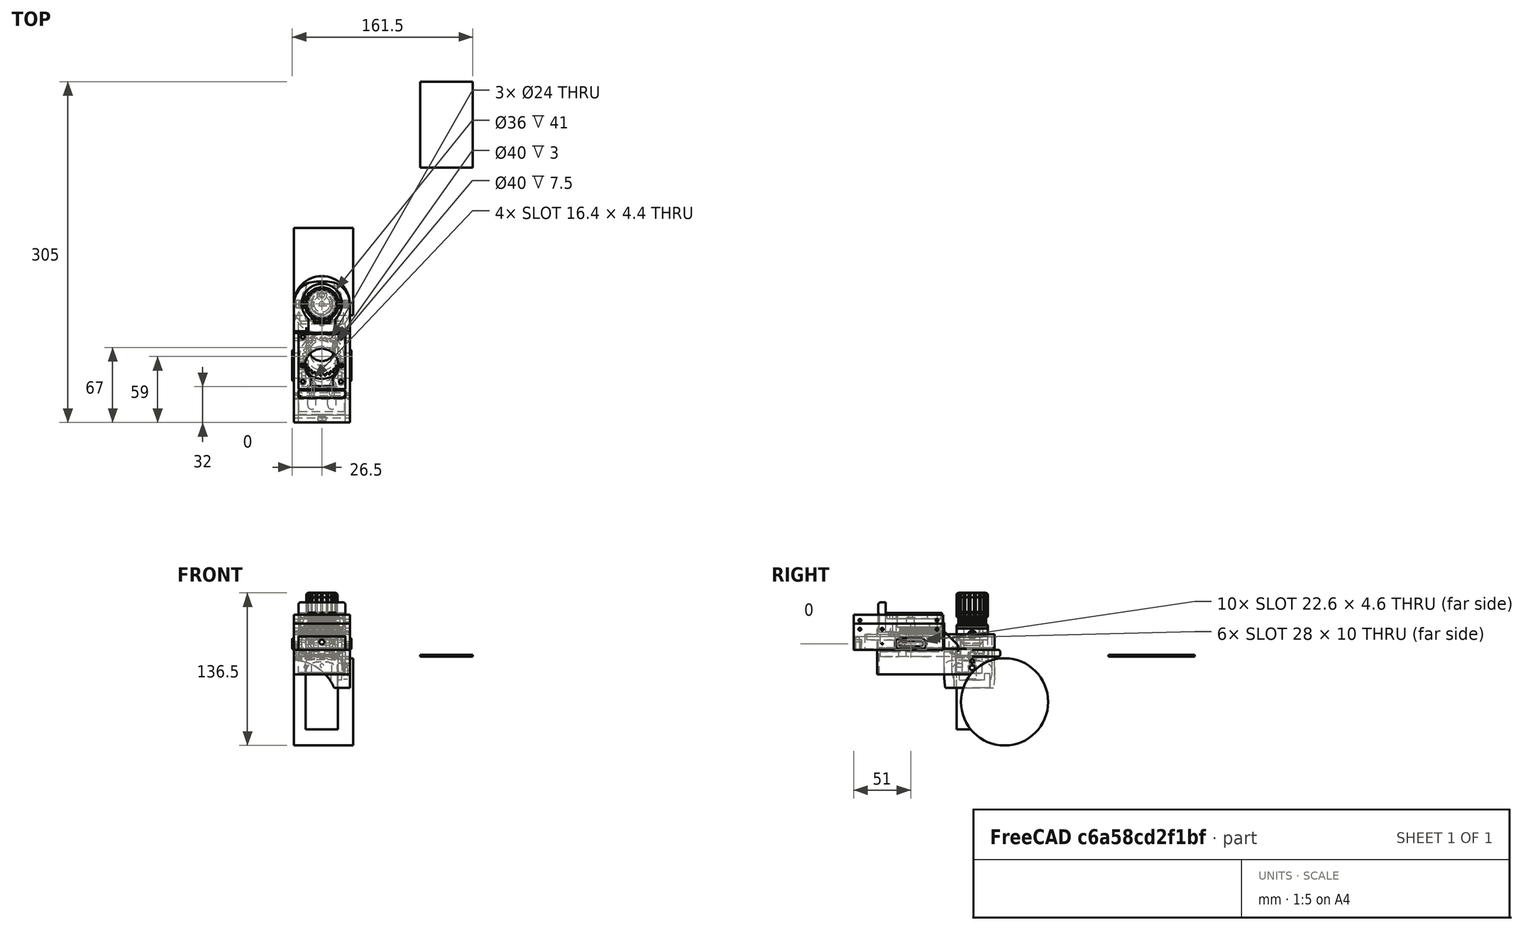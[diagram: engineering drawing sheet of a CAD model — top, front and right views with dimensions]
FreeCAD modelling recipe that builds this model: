
FCSTD DOCUMENT  (FreeCAD 0.18R4 (GitTag))
Label: new28BYJ-fokuser
License: All rights reserved
LicenseURL: http://en.wikipedia.org/wiki/All_rights_reserved
objects: Part::Feature×777, Part::Cylinder×371, Part::Box×218, Part::MultiFuse×160, Part::Cut×77, Part::Extrusion×34, Part::Fillet×30, App::Part×24, Sketcher::SketchObject×24, Part::FeaturePython×10, Part::Part2DObjectPython×10, Part::Chamfer×5, Part::Sphere×1
note: 1717 computed .brp shape members not serialized (recipe doc carries the construction recipe); baked Part::Feature solids carry a one-line shape summary decoded from their .brp

FEATURE [Part::Feature] Cut018020020009027020001  label="base nema"
  shape: bbox 50 x 86 x 24 mm, 75 faces (baked)
FEATURE [Part::Box] Box  label="Krychle"
  AttacherType = Attacher::AttachEngine3D
  Height = 24
  Length = 50
  Placement = pos=(-25,-66,-16) rot=(0,0,1;0rad)
  Width = 51
FEATURE [Part::Cut] Cut
  Base = -> Cut018020020009027020001
  Tool = -> Box
FEATURE [Part::Box] Box001  label="Krychle001"
  AttacherType = Attacher::AttachEngine3D
  Height = 24
  Length = 50
  Placement = pos=(-25,-85,-16) rot=(0,0,1;0rad)
  Width = 70
FEATURE [Part::Box] Box002  label="Kry"
  AttacherType = Attacher::AttachEngine3D
  Height = 24
  Length = 42
  Placement = pos=(-21,-83,-19.5) rot=(0,0,1;0rad)
  Width = 65
FEATURE [Part::MultiFuse] Fusion
  Shapes = -> [Box001,Cut]
FEATURE [Part::Cylinder] Cylinder  label="Válec"
  Angle = 360
  AttacherType = Attacher::AttachEngine3D
  Height = 27
  Placement = pos=(0,0,-17) rot=(0,0,1;0rad)
  Radius = 14.7
FEATURE [Part::Cylinder] Cylinder001  label="Válec001"
  Angle = 360
  AttacherType = Attacher::AttachEngine3D
  Height = 10
  Placement = pos=(0,-45,0) rot=(0,0,1;0rad)
  Radius = 10
FEATURE [Part::Cylinder] Cylinder002  label="Válec002"
  Angle = 360
  AttacherType = Attacher::AttachEngine3D
  Height = 10
  Placement = pos=(0,-37,0) rot=(0,0,1;0rad)
  Radius = 10
FEATURE [Part::Box] Box003  label="Krychle003"
  AttacherType = Attacher::AttachEngine3D
  Height = 10
  Length = 20
  Placement = pos=(-10,-45,0) rot=(0,0,1;0rad)
  Width = 8
FEATURE [Part::Cylinder] Cylinder003  label="Válec003"
  Angle = 360
  AttacherType = Attacher::AttachEngine3D
  Height = 10
  Placement = pos=(9,-68,0) rot=(0,0,1;0rad)
  Radius = 2.2
FEATURE [Part::Cylinder] Cylinder004  label="Válec004"
  Angle = 360
  AttacherType = Attacher::AttachEngine3D
  Height = 10
  Placement = pos=(-9,-68,0) rot=(0,0,1;0rad)
  Radius = 2.2
FEATURE [Part::Cylinder] Cylinder005  label="Válec005"
  Angle = 360
  AttacherType = Attacher::AttachEngine3D
  Height = 10
  Placement = pos=(9,-80,0) rot=(0,0,1;0rad)
  Radius = 2.2
FEATURE [Part::Cylinder] Cylinder006  label="Válec006"
  Angle = 360
  AttacherType = Attacher::AttachEngine3D
  Height = 10
  Placement = pos=(-9,-80,0) rot=(0,0,1;0rad)
  Radius = 2.2
FEATURE [Part::Box] Box004  label="Krychle004"
  AttacherType = Attacher::AttachEngine3D
  Height = 10
  Length = 4.4
  Placement = pos=(-11.2,-80,0) rot=(0,0,1;0rad)
  Width = 12
FEATURE [Part::Box] Box005  label="Krychle005"
  AttacherType = Attacher::AttachEngine3D
  Height = 10
  Length = 4.4
  Placement = pos=(6.8,-80,0) rot=(0,0,1;0rad)
  Width = 12
FEATURE [Part::MultiFuse] Fusion001
  Shapes = -> [Cylinder,Cylinder001,Cylinder002,Box003,Cylinder003,Cylinder004,Cylinder005,Cylinder006,Box004,Box005,Box002]
FEATURE [Part::Cut] Cut018020020009027020002  label="N_EAF"
  Base = -> Fusion
  Tool = -> Fusion001
FEATURE [Part::Box] Box021049  label="Krychle076"
  AttacherType = Attacher::AttachEngine3D
  Height = 24
  Length = 50
  Placement = pos=(-25,-66,-16) rot=(0,0,1;0rad)
  Width = 51
FEATURE [Part::Feature] Cut018020020009019001  label="Nema refractor"
  shape: bbox 50 x 89 x 24 mm, 96 faces (baked)
FEATURE [Part::Cut] Cut018020020009027020002002
  Base = -> Cut018020020009019001
  Tool = -> Box021049
FEATURE [Part::Feature] Cylinder112019  label="Válec127"
  Placement = pos=(0,0,0) rot=(0,0,1;4.18879rad)
  shape: bbox 7.858 x 10.31 x 3.3 mm, 3 faces (baked)
FEATURE [Part::Feature] difference001004  label="Pulley GT2  - 043"
  shape: bbox 27.96 x 27.96 x 19.5 mm, 1014 faces (baked)
FEATURE [Part::Feature] Cylinder112018  label="Válec126"
  Placement = pos=(0,0,0) rot=(0,0,1;2.0944rad)
  shape: bbox 7.858 x 10.31 x 3.3 mm, 3 faces (baked)
FEATURE [Part::Cylinder] Cylinder112004  label="Válec112"
  Angle = 360
  AttacherType = Attacher::AttachEngine3D
  Height = 40
  Placement = pos=(-20,0,19.5) rot=(0,1,0;1.5708rad)
  Radius = 2.15
FEATURE [Part::Cylinder] Cylinder112013  label="Válec121"
  Angle = 360
  AttacherType = Attacher::AttachEngine3D
  Height = 17
  Placement = pos=(0,0,8) rot=(0,0,1;0rad)
  Radius = 9
FEATURE [Part::Chamfer] Chamfer006
  Base = -> Cylinder112013
  Edges = 1 edges r=4: [Edge3]
FEATURE [Part::Cylinder] Cylinder112014  label="Válec122"
  Angle = 360
  AttacherType = Attacher::AttachEngine3D
  Height = 25
  Radius = 5.5
FEATURE [Part::Cylinder] Cylinder112008  label="Válec116"
  Angle = 360
  AttacherType = Attacher::AttachEngine3D
  Height = 40
  Placement = pos=(0,0,-5) rot=(0,0,1;0rad)
  Radius = 2.15
FEATURE [Part::Cylinder] Cylinder112015  label="Válec123"
  Angle = 360
  AttacherType = Attacher::AttachEngine3D
  Height = 10
  Placement = pos=(0,0,15) rot=(0,0,1;0rad)
  Radius = 14
FEATURE [Part::Cylinder] Cylinder112011  label="Válec119"
  Angle = 360
  AttacherType = Attacher::AttachEngine3D
  Height = 18
  Placement = pos=(0,0,36) rot=(0,0,1;0rad)
  Radius = 14
FEATURE [Part::Cylinder] Cylinder112010  label="Válec118"
  Angle = 360
  AttacherType = Attacher::AttachEngine3D
  Height = 27
  Radius = 7.2
FEATURE [Part::Cylinder] Cylinder112016  label="Válec124"
  Angle = 360
  AttacherType = Attacher::AttachEngine3D
  Height = 40
  Placement = pos=(0,0,-5) rot=(0,0,1;0rad)
  Radius = 2.15
FEATURE [Part::Cylinder] Cylinder112017  label="Válec125"
  Angle = 360
  AttacherType = Attacher::AttachEngine3D
  Height = 8.5
  Radius = 9
FEATURE [Part::Cut] Cut018020020009016
  Base = -> difference001004
  Placement = pos=(0,0,16.5) rot=(0,0,1;0rad)
  Tool = -> Cylinder112017
FEATURE [Part::MultiFuse] Fusion005033
  Shapes = -> [Cut018020020009016,Cylinder112014,Chamfer006,Cylinder112011,Cylinder112015]
FEATURE [Part::Fillet] Fillet011
  Base = -> Fusion005033
  Edges = 2 edges: [Edge8 r=1,Edge2738 r=3]
FEATURE [Part::Cylinder] Cylinder112012  label="Válec120"
  Angle = 360
  AttacherType = Attacher::AttachEngine3D
  Height = 10
  Placement = pos=(0,0,4.5) rot=(0,1,0;1.5708rad)
  Radius = 1.65
FEATURE [Part::MultiFuse] Fusion005032
  Shapes = -> [Cylinder112016,Cylinder112012,Cylinder112018,Cylinder112019]
FEATURE [Part::Cut] Cut018020020009017  label="pully40 v003"
  Base = -> Fillet011
  Tool = -> Fusion005032
FEATURE [Part::Cylinder] Cylinder112020  label="Válec128"
  Angle = 360
  AttacherType = Attacher::AttachEngine3D
  Height = 10
  Placement = pos=(-19,0,19.5) rot=(0,1,0;1.5708rad)
  Radius = 3.7
FEATURE [Part::Cylinder] Cylinder112021  label="Válec129"
  Angle = 360
  AttacherType = Attacher::AttachEngine3D
  Height = 10
  Placement = pos=(9,0,19.5) rot=(0,1,0;1.5708rad)
  Radius = 3.7
FEATURE [Part::MultiFuse] Fusion005034
  Shapes = -> [Cylinder112020,Cylinder112021,Cylinder112008,Cylinder112004,Cylinder112010]
FEATURE [Part::Cut] Cut018020020009018  label="Pulley40 V3"
  Base = -> Cut018020020009017
  Tool = -> Fusion005034
FEATURE [Part::Feature] Cut018020020009027020002003003  label="N_EAF002"
  shape: bbox 50 x 105 x 24 mm, 61 faces (baked)
FEATURE [Part::Fillet] Fillet  label="N_EAF_a"
  Base = -> Cut018020020009027020002003003
  Edges = 8 edges r=1.5: [Edge82,Edge83,Edge87,Edge88,Edge97,Edge100,Edge103,Edge126]
FEATURE [Part::Box] Box021055  label="Krychle082"
  AttacherType = Attacher::AttachEngine3D
  Height = 24
  Length = 50
  Placement = pos=(-25,-85,-16) rot=(0,0,1;0rad)
  Width = 70
FEATURE [Part::MultiFuse] Fusion005036
  Shapes = -> [Cut018020020009027020002002,Box021055]
FEATURE [Part::Cylinder] Cylinder112024003  label="Válec135"
  Angle = 360
  AttacherType = Attacher::AttachEngine3D
  Height = 10
  Placement = pos=(9,-80,0) rot=(0,0,1;0rad)
  Radius = 2.2
FEATURE [Part::Cylinder] Cylinder112024004  label="Válec136"
  Angle = 360
  AttacherType = Attacher::AttachEngine3D
  Height = 10
  Placement = pos=(0,-45,0) rot=(0,0,1;0rad)
  Radius = 10
FEATURE [Part::Cylinder] Cylinder112024005  label="Válec137"
  Angle = 360
  AttacherType = Attacher::AttachEngine3D
  Height = 10
  Placement = pos=(-9,-80,0) rot=(0,0,1;0rad)
  Radius = 2.2
FEATURE [Part::Box] Box021056  label="Krychle083"
  AttacherType = Attacher::AttachEngine3D
  Height = 10
  Length = 4.4
  Placement = pos=(-11.2,-80,0) rot=(0,0,1;0rad)
  Width = 12
FEATURE [Part::Box] Box021057  label="Krychle084"
  AttacherType = Attacher::AttachEngine3D
  Height = 10
  Length = 4.4
  Placement = pos=(6.8,-80,0) rot=(0,0,1;0rad)
  Width = 12
FEATURE [Part::Cylinder] Cylinder112024006  label="Válec138"
  Angle = 360
  AttacherType = Attacher::AttachEngine3D
  Height = 10
  Placement = pos=(-9,-68,0) rot=(0,0,1;0rad)
  Radius = 2.2
FEATURE [Part::Cylinder] Cylinder112024007  label="Válec139"
  Angle = 360
  AttacherType = Attacher::AttachEngine3D
  Height = 10
  Placement = pos=(9,-68,0) rot=(0,0,1;0rad)
  Radius = 2.2
FEATURE [Part::Box] Box021058  label="Kry001"
  AttacherType = Attacher::AttachEngine3D
  Height = 24
  Length = 42
  Placement = pos=(-21,-83,-19.5) rot=(0,0,1;0rad)
  Width = 65
FEATURE [Part::Cylinder] Cylinder112024008  label="Válec140"
  Angle = 360
  AttacherType = Attacher::AttachEngine3D
  Height = 10
  Placement = pos=(0,-37,0) rot=(0,0,1;0rad)
  Radius = 10
FEATURE [Part::Box] Box021059  label="Krychle085"
  AttacherType = Attacher::AttachEngine3D
  Height = 10
  Length = 20
  Placement = pos=(-10,-45,0) rot=(0,0,1;0rad)
  Width = 8
FEATURE [Part::Cylinder] Cylinder112024009  label="Válec141"
  Angle = 360
  AttacherType = Attacher::AttachEngine3D
  Height = 27
  Placement = pos=(0,0,-17) rot=(0,0,1;0rad)
  Radius = 14.7
FEATURE [Part::MultiFuse] Fusion005037
  Shapes = -> [Cylinder112024009,Cylinder112024004,Cylinder112024008,Box021059,Cylinder112024007,Cylinder112024006,Cylinder112024003,Cylinder112024005,Box021056,Box021057,Box021058]
FEATURE [Part::Cut] Cut018020020009027020002003004  label="R_EAF"
  Base = -> Fusion005036
  Tool = -> Fusion005037
FEATURE [Part::Feature] Cut018020020009027020002003004001  label="R_EAF001"
  shape: bbox 50 x 108 x 24 mm, 82 faces (baked)
FEATURE [Part::Fillet] Fillet012  label="R_EAF_a"
  Base = -> Cut018020020009027020002003004001
  Edges = 8 edges r=1.5: [Edge106,Edge136,Edge138,Edge196,Edge197,Edge198,Edge243,Edge244]
FEATURE [App::Part] Part001  label="Refractor"
  Group = -> [Cut018020020009019001,Box021049,Cut018020020009027020002002,Cylinder112024006,Box021057,Box021058,Cylinder112024007,Cylinder112024008,Cylinder112024009,Box021059,Box021056,Box021055,Cylinder112024005,Cylinder112024003,Cylinder112024004,Fusion005036,Fusion005037,Cut018020020009027020002003004,Cut018020020009027020002003004001,Fillet012]
  License = CC BY 3.0
  LicenseURL = http://creativecommons.org/licenses/by/3.0/
  Origin = -> Origin001
FEATURE [Part::Cylinder] Cylinder112024015  label="cy4"
  Angle = 360
  AttacherType = Attacher::AttachEngine3D
  Height = 24
  Placement = pos=(-9,-68,0) rot=(0,0,1;0rad)
  Radius = 2.2
FEATURE [Part::Box] Box021060  label="cub3"
  AttacherType = Attacher::AttachEngine3D
  Height = 24
  Length = 4.4
  Placement = pos=(6.8,-80,0) rot=(0,0,1;0rad)
  Width = 12
FEATURE [Part::Box] Box021061  label="cub5"
  AttacherType = Attacher::AttachEngine3D
  Height = 15
  Length = 42
  Placement = pos=(-21,-83,22) rot=(0,0,1;0rad)
  Width = 65
FEATURE [Part::Cylinder] Cylinder112024016  label="cy3"
  Angle = 360
  AttacherType = Attacher::AttachEngine3D
  Height = 24
  Placement = pos=(9,-68,0) rot=(0,0,1;0rad)
  Radius = 2.2
FEATURE [Part::Cylinder] Cylinder112024017  label="cy2"
  Angle = 360
  AttacherType = Attacher::AttachEngine3D
  Height = 24
  Placement = pos=(0,-39,0) rot=(0,0,1;0rad)
  Radius = 14
FEATURE [Part::Box] Box021062  label="cub1"
  AttacherType = Attacher::AttachEngine3D
  Height = 6
  Length = 28
  Placement = pos=(-14,-45,0) rot=(0,0,1;0rad)
  Width = 6
FEATURE [Part::Box] Box021063  label="cub2"
  AttacherType = Attacher::AttachEngine3D
  Height = 24
  Length = 4.4
  Placement = pos=(-11.2,-80,0) rot=(0,0,1;0rad)
  Width = 12
FEATURE [Part::Cylinder] Cylinder112024019  label="cy6"
  Angle = 360
  AttacherType = Attacher::AttachEngine3D
  Height = 24
  Placement = pos=(-9,-80,0) rot=(0,0,1;0rad)
  Radius = 2.2
FEATURE [Part::Cylinder] Cylinder112024020  label="cy5"
  Angle = 360
  AttacherType = Attacher::AttachEngine3D
  Height = 24
  Placement = pos=(9,-80,0) rot=(0,0,1;0rad)
  Radius = 2.2
FEATURE [Part::Cylinder] Cylinder112024021  label="cy1"
  Angle = 360
  AttacherType = Attacher::AttachEngine3D
  Height = 24
  Placement = pos=(0,-45,0) rot=(0,0,1;0rad)
  Radius = 14
FEATURE [Part::FeaturePython] Screw  label="M4x30-Screw"  # Fasteners workbench fastener (typed FeaturePython)
  Placement = pos=(0,0,7.5) rot=(0,0,1;0rad)
  diameter = 6
  invert = false
  length = 1
  matchOuter = false
  offset = 0
  thread = false
  type = 13
FEATURE [Part::Cylinder] Cylinder112024022  label="Válec154"
  Angle = 360
  AttacherType = Attacher::AttachEngine3D
  Height = 10
  Radius = 9
FEATURE [Part::Cut] Cut018020020009027020002003004003
  Base = -> Cylinder112024022
  Tool = -> Screw
FEATURE [Part::Fillet] Fillet013  label="knob"
  Base = -> Cut018020020009027020002003004003
  Edges = 2 edges r=2: [Edge1,Edge3]
  Placement = pos=(0,0,2) rot=(0,0,1;0rad)
FEATURE [Part::Cylinder] Cylinder112024026  label="Cy9"
  Angle = 360
  AttacherType = Attacher::AttachEngine3D
  Height = 6
  Radius = 25
FEATURE [Part::Cylinder] Cylinder112024027  label="cy7"
  Angle = 360
  AttacherType = Attacher::AttachEngine3D
  Height = 10
  Radius = 10
FEATURE [Part::Box] Box021064  label="Cub6"
  AttacherType = Attacher::AttachEngine3D
  Height = 30
  Length = 50
  Placement = pos=(-25,-85,0) rot=(0,0,1;0rad)
  Width = 60
FEATURE [Part::Box] Box021065  label="Cub7"
  AttacherType = Attacher::AttachEngine3D
  Height = 6
  Length = 50
  Placement = pos=(-25,-85,0) rot=(0,0,1;0rad)
  Width = 85
FEATURE [Part::Box] Box021067  label="cub4"
  AttacherType = Attacher::AttachEngine3D
  Height = 18
  Length = 28
  Placement = pos=(-14,-45,6) rot=(0,0,1;0rad)
  Width = 25
FEATURE [Part::Cylinder] Cylinder112024025003  label="hole3s"
  Angle = 360
  AttacherType = Attacher::AttachEngine3D
  Height = 10
  Placement = pos=(0,16.5,0) rot=(0,0,1;0rad)
  Radius = 1.7
FEATURE [Part::Feature] Cylinder112024025003001  label="hole2s"
  Placement = pos=(0,0,0) rot=(0,0,1;2.0944rad)
  shape: bbox 3.4 x 3.4 x 10 mm, 3 faces (baked)
FEATURE [Part::Feature] Cylinder112024025003002  label="hole1s"
  Placement = pos=(0,0,0) rot=(0,0,1;4.18879rad)
  shape: bbox 3.4 x 3.4 x 10 mm, 3 faces (baked)
FEATURE [Part::Cylinder] Cylinder112024025003003  label="hole3i"
  Angle = 360
  AttacherType = Attacher::AttachEngine3D
  Height = 4
  Placement = pos=(0,16.5,3) rot=(0,0,1;0rad)
  Radius = 3
FEATURE [Part::Feature] Cylinder112024025003003001  label="holeě2i"
  Placement = pos=(0,0,0) rot=(0,0,1;2.0944rad)
  shape: bbox 6 x 6 x 4 mm, 3 faces (baked)
FEATURE [Part::Feature] Cylinder112024025003003002  label="hole1i"
  Placement = pos=(0,0,0) rot=(0,0,1;4.18879rad)
  shape: bbox 6 x 6 x 4 mm, 3 faces (baked)
FEATURE [Part::MultiFuse] Fusion005041  label="Hole for SC screw"
  Placement = pos=(0,0,0) rot=(0,0,1;3.14159rad)
  Shapes = -> [Cylinder112024025003003002,Cylinder112024025003002,Cylinder112024025003003001,Cylinder112024025003001,Cylinder112024025003,Cylinder112024025003003]
FEATURE [Part::Box] Box021068  label="Cub8"
  AttacherType = Attacher::AttachEngine3D
  Height = 16
  Length = 50
  Placement = pos=(-25,-25,6) rot=(0,0,1;0rad)
  Width = 12.5
FEATURE [Part::Chamfer] Chamfer
  Base = -> Box021068
  Edges = 1 edges r=12: [Edge12]
FEATURE [Part::MultiFuse] Fusion005040  label="Solid base"
  Shapes = -> [Box021064,Cylinder112024026,Box021065,Chamfer]
FEATURE [Part::Cylinder] Cylinder112024025003003003  label="cy8"
  Angle = 360
  AttacherType = Attacher::AttachEngine3D
  Height = 15
  Placement = pos=(0,0,6) rot=(0,0,1;0rad)
  Radius = 25
FEATURE [Part::MultiFuse] Fusion005039  label="Holes"
  Shapes = -> [Cylinder112024021,Cylinder112024017,Box021062,Cylinder112024016,Cylinder112024015,Cylinder112024020,Cylinder112024019,Box021063,Box021060,Cylinder112024027,Box021067,Box021061,Cylinder112024025003003003]
FEATURE [Part::Cut] Cut018020020009027020002003004004  label="SCT-base"
  Base = -> Fusion005040
  Tool = -> Fusion005039
FEATURE [Part::Feature] difference001001  label="difference002"
  Placement = pos=(0,0,30) rot=(1,0,0;3.14159rad)
  shape: bbox 29.87 x 29.87 x 23.5 mm, 1122 faces (baked)
FEATURE [Part::Cylinder] Cylinder112024025003003004  label="Válec169"
  Angle = 360
  AttacherType = Attacher::AttachEngine3D
  Height = 30
  Placement = pos=(0,0,30) rot=(0,0,1;0rad)
  Radius = 7.5
FEATURE [Part::Cylinder] Cylinder112024025003003005  label="Válec170"
  Angle = 360
  AttacherType = Attacher::AttachEngine3D
  Height = 5
  Placement = pos=(0,0,30) rot=(0,0,1;0rad)
  Radius = 13
FEATURE [Part::MultiFuse] Fusion005042
  Shapes = -> [Cylinder112024025003003004,difference001001,Cylinder112024025003003005]
FEATURE [Part::Fillet] Fillet015  label="SCT-PulleyV1"
  Base = -> Fusion005042
  Edges = 2 edges r=3: [Edge1,Edge4]
FEATURE [Part::Cylinder] Cylinder112024025003003006  label="Válec171"
  Angle = 360
  AttacherType = Attacher::AttachEngine3D
  Height = 30
  Placement = pos=(11,0,30) rot=(0,0,1;0rad)
  Radius = 2
FEATURE [Part::Cylinder] Cylinder112024025003003007  label="Válec172"
  Angle = 360
  AttacherType = Attacher::AttachEngine3D
  Height = 30
  Placement = pos=(0,0,30) rot=(0,0,1;0rad)
  Radius = 11
FEATURE [Part::Feature] Cylinder112024025003003006001  label="Válec173"
  Placement = pos=(0,0,0) rot=(0,0,1;0.698132rad)
  shape: bbox 4 x 4 x 30 mm, 3 faces (baked)
FEATURE [Part::Feature] Cylinder112024025003003006002  label="Válec174"
  Placement = pos=(0,0,0) rot=(0,0,1;1.0472rad)
  shape: bbox 4 x 4 x 30 mm, 3 faces (baked)
FEATURE [Part::Feature] Cylinder112024025003003006003  label="Válec175"
  Placement = pos=(0,0,0) rot=(0,0,1;0.349066rad)
  shape: bbox 4 x 4 x 30 mm, 3 faces (baked)
FEATURE [Part::Feature] Cylinder112024025003003006004  label="Válec176"
  Placement = pos=(0,0,0) rot=(0,0,1;1.39626rad)
  shape: bbox 4 x 4 x 30 mm, 3 faces (baked)
FEATURE [Part::Feature] Cylinder112024025003003006005  label="Válec177"
  Placement = pos=(0,0,0) rot=(0,0,1;1.74533rad)
  shape: bbox 4 x 4 x 30 mm, 3 faces (baked)
FEATURE [Part::MultiFuse] Fusion005043
  Placement = pos=(0,0,-6) rot=(0,0,1;0rad)
  Shapes = -> [Cylinder112024025003003006001,Cylinder112024025003003006002,Cylinder112024025003003006003,Cylinder112024025003003006004,Cylinder112024025003003006005,Cylinder112024025003003006]
FEATURE [Part::Feature] Fusion005043001  label="Fusion005044"
  Placement = pos=(0,0,-6) rot=(0,0,1;4.18879rad)
  shape: bbox 19.84 x 11.07 x 30 mm, 12 faces (baked)
FEATURE [Part::Feature] Fusion005043002  label="Fusion005045"
  Placement = pos=(0,0,-6) rot=(0,0,1;2.0944rad)
  shape: bbox 9.5 x 20.6 x 30 mm, 12 faces (baked)
FEATURE [Part::MultiFuse] Fusion005043003
  Shapes = -> [Cylinder112024025003003007,Fusion005043,Fusion005043001,Fusion005043002]
FEATURE [Part::Sphere] Sphere  label="Koule"
  Angle1 = -90
  Angle2 = 90
  Angle3 = 360
  AttacherType = Attacher::AttachEngine3D
  Placement = pos=(0,0,47) rot=(0,0,1;0rad)
  Radius = 13
FEATURE [Part::Cylinder] Cylinder112024025003003006006  label="Válec178"
  Angle = 360
  AttacherType = Attacher::AttachEngine3D
  Height = 13
  Placement = pos=(0,0,47) rot=(0,0,1;0rad)
  Radius = 14
FEATURE [Part::Cut] Cut018020020009027020002003004004002
  Base = -> Cylinder112024025003003006006
  Tool = -> Sphere
FEATURE [Part::Cut] Cut018020020009027020002003004004003
  Base = -> Fusion005043003
  Tool = -> Cut018020020009027020002003004004002
FEATURE [Part::Cylinder] Cylinder112024025003003006007  label="Válec179"
  Angle = 360
  AttacherType = Attacher::AttachEngine3D
  Height = 9
  Radius = 9.5
FEATURE [Part::Cylinder] Cylinder112024025003003006008  label="Válec180"
  Angle = 360
  AttacherType = Attacher::AttachEngine3D
  Height = 10
  Radius = 6.7
FEATURE [Part::Cut] Cut018020020009027020002003004004004  label="Distance ring"
  Base = -> Cylinder112024025003003006007
  Tool = -> Cylinder112024025003003006008
FEATURE [Part::Fillet] Fillet016  label="SCT-EAF-no screw"
  Base = -> Cut018020020009027020002003004004
  Edges = 16 edges r=1.5: [Edge6,Edge7,Edge8,Edge20,Edge24,Edge51,Edge53,Edge54,Edge55,Edge60,Edge102,Edge104,Edge113,Edge115,Edge126,Edge127]
FEATURE [Part::Cut] Cut018020020009027020002003004004005  label="SCT-EAF 9,25 Edge HD"
  Base = -> Fillet016
  Tool = -> Fusion005041
FEATURE [App::Part] Part003  label="SCT"
  Group = -> [Cut018020020009027020002003004004,Cylinder112024015,Cylinder112024025003003001,Cylinder112024025003002,Cylinder112024025003001,Cylinder112024025003003002,Fusion005039,Fusion005040,Fusion005041,Box021067,Cylinder112024025003003003,Cylinder112024027,Box021068,Box021064,Cylinder112024025003,Box021065,Cylinder112024025003003,Chamfer,Fillet016,Cylinder112024016,Box021061,Cylinder112024021,Box021062,+7 more]
  License = CC BY 3.0
  LicenseURL = http://creativecommons.org/licenses/by/3.0/
  Origin = -> Origin003
FEATURE [Part::Feature] difference001006  label="Pulley43"
  Placement = pos=(0,0,24) rot=(0,0,1;0rad)
  shape: bbox 29.87 x 29.87 x 17.5 mm, 1122 faces (baked)
FEATURE [Part::Cylinder] Cylinder112024025003003006009  label="Válec181"
  Angle = 360
  AttacherType = Attacher::AttachEngine3D
  Height = 20
  Placement = pos=(0,0,6) rot=(0,0,1;0rad)
  Radius = 6.5
FEATURE [Part::MultiFuse] Fusion005043004
  Shapes = -> [difference001006,Cut018020020009027020002003004004003]
FEATURE [Part::Cut] Cut018020020009027020002003004004006  label="PulleyV3sct"
  Base = -> Fusion005043004
  Tool = -> Cylinder112024025003003006009
FEATURE [Part::Cylinder] Cylinder112024025003003006010  label="Válec182"
  Angle = 360
  AttacherType = Attacher::AttachEngine3D
  Height = 17
  Placement = pos=(15,0,36) rot=(0,0,1;0rad)
  Radius = 2
FEATURE [Part::Feature] Cylinder112024025003003006010001  label="Válec183"
  Placement = pos=(0,0,0) rot=(0,0,1;0.349066rad)
  shape: bbox 4 x 4 x 17 mm, 3 faces (baked)
FEATURE [Part::Feature] Cylinder112024025003003006010002  label="Válec184"
  Placement = pos=(0,0,0) rot=(0,0,1;0.698132rad)
  shape: bbox 4 x 4 x 17 mm, 3 faces (baked)
FEATURE [Part::MultiFuse] Fusion005043005
  Shapes = -> [Cylinder112024025003003006010,Cylinder112024025003003006010001,Cylinder112024025003003006010002]
FEATURE [Part::Feature] Fusion005043005001  label="Fusion005043006"
  Placement = pos=(0,0,0) rot=(0,0,1;1.0472rad)
  shape: bbox 14.1 x 5.782 x 17 mm, 9 faces, 3 solids (baked)
FEATURE [Part::Feature] Fusion005043005002  label="Fusion005043007"
  Placement = pos=(0,0,0) rot=(0,0,1;2.0944rad)
  shape: bbox 10.6 x 11.86 x 17 mm, 9 faces, 3 solids (baked)
FEATURE [Part::Feature] Fusion005043005003  label="Fusion005043008"
  Placement = pos=(0,0,0) rot=(0,0,1;4.18879rad)
  shape: bbox 14.1 x 5.782 x 17 mm, 9 faces, 3 solids (baked)
FEATURE [Part::Feature] Fusion005043005004  label="Fusion005043009"
  Placement = pos=(0,0,0) rot=(0,0,1;3.14159rad)
  shape: bbox 7.509 x 13.64 x 17 mm, 9 faces, 3 solids (baked)
FEATURE [Part::Feature] Fusion005043005005  label="Fusion005043010"
  Placement = pos=(0,0,0) rot=(0,0,-1;1.0472rad)
  shape: bbox 10.6 x 11.86 x 17 mm, 9 faces, 3 solids (baked)
FEATURE [Part::MultiFuse] Fusion005043005006
  Shapes = -> [Fusion005043005,Fusion005043005001,Fusion005043005002,Fusion005043005003,Fusion005043005005,Fusion005043005004]
FEATURE [Part::Cut] Cut018020020009027020002003004004007  label="Pulley-CrayfordV4"
  Base = -> Cut018020020009018
  Tool = -> Fusion005043005006
FEATURE [App::Part] Part002  label="Pulley"
  Group = -> [Cylinder112024025003003006008,Cylinder112024025003003006007,Cut018020020009027020002003004004004,Cylinder112024025003003006005,Fusion005043003,Fusion005043,Cut018020020009027020002003004004002,Cut018020020009027020002003004004003,Cylinder112024025003003006003,Cylinder112024025003003006002,Cylinder112024025003003006001,Cylinder112024025003003006004,Cylinder112024025003003006009,+48 more]
  License = CC BY 3.0
  LicenseURL = http://creativecommons.org/licenses/by/3.0/
  Origin = -> Origin002
FEATURE [Part::FeaturePython] Screw001  label="M4x30-Screw001"  # Fasteners workbench fastener (typed FeaturePython)
  Placement = pos=(0,0,7.5) rot=(0,0,1;0rad)
  diameter = 6
  invert = false
  length = 1
  matchOuter = false
  offset = 0
  thread = false
  type = 13
FEATURE [Part::Cylinder] Cylinder112024025003003006010003  label="Válec185"
  Angle = 360
  AttacherType = Attacher::AttachEngine3D
  Height = 10
  Radius = 8.5
FEATURE [Part::Cut] Cut018020020009027020002003004004008
  Base = -> Cylinder112024025003003006010003
  Tool = -> Screw001
FEATURE [Part::Fillet] Fillet017  label="knob001"
  Base = -> Cut018020020009027020002003004004008
  Edges = 2 edges r=2: [Edge1,Edge3]
FEATURE [Part::Cylinder] Cylinder112024025003003006010004  label="Válec186"
  Angle = 360
  AttacherType = Attacher::AttachEngine3D
  Height = 10
  Placement = pos=(8.5,0,0) rot=(0,0,1;0.349066rad)
  Radius = 1
FEATURE [Part::Feature] Cylinder112024025003003006010004001  label="Válec187"
  Placement = pos=(0,0,0) rot=(0,0,1;0.349066rad)
  shape: bbox 2 x 2 x 10 mm, 3 faces (baked)
FEATURE [Part::Feature] Cylinder112024025003003006010004002  label="Válec188"
  Placement = pos=(0,0,0) rot=(0,0,1;0.698132rad)
  shape: bbox 2 x 2 x 10 mm, 3 faces (baked)
FEATURE [Part::MultiFuse] Fusion005043005007
  Shapes = -> [Cylinder112024025003003006010004,Cylinder112024025003003006010004001,Cylinder112024025003003006010004002]
FEATURE [Part::Feature] Fusion005043005007001  label="Fusion005043005008"
  Placement = pos=(0,0,0) rot=(0,0,1;1.0472rad)
  shape: bbox 7.726 x 3.01 x 10 mm, 9 faces, 3 solids (baked)
FEATURE [Part::MultiFuse] Fusion005043005007002
  Shapes = -> [Fusion005043005007,Fusion005043005007001]
FEATURE [Part::Feature] Fusion005043005007002001  label="Fusion005043005007003"
  Placement = pos=(0,0,0) rot=(0,0,1;4.18879rad)
  shape: bbox 14.24 x 7.464 x 10 mm, 18 faces, 6 solids (baked)
FEATURE [Part::Feature] Fusion005043005007002002  label="Fusion005043005007004"
  Placement = pos=(0,0,0) rot=(0,0,1;2.0944rad)
  shape: bbox 6.25 x 14.82 x 10 mm, 18 faces, 6 solids (baked)
FEATURE [Part::MultiFuse] Fusion005043005007002003
  Shapes = -> [Fusion005043005007002001,Fusion005043005007002002,Fusion005043005007002]
FEATURE [Part::Cut] Cut018020020009027020002003004004009  label="Knob M4 v2"
  Base = -> Fillet017
  Tool = -> Fusion005043005007002003
FEATURE [Part::Cylinder] Cylinder112024025003003006010004004  label="Válec190"
  Angle = 360
  AttacherType = Attacher::AttachEngine3D
  Height = 17
  Placement = pos=(10,-24,6) rot=(0,0,1;0rad)
  Radius = 4.5
FEATURE [Part::Box] Box021069  label="Krychle086"
  AttacherType = Attacher::AttachEngine3D
  Height = 17
  Length = 11
  Placement = pos=(10,-28.5,6) rot=(0,0,1;0rad)
  Width = 9
FEATURE [Part::MultiFuse] Fusion005043005007002004
  Shapes = -> [Cylinder112024025003003006010004004,Box021069]
FEATURE [Part::Cylinder] Cylinder112024025003003006010004005  label="Válec191"
  Angle = 360
  AttacherType = Attacher::AttachEngine3D
  Height = 17
  Placement = pos=(-10,-24,6) rot=(0,0,1;0rad)
  Radius = 4.5
FEATURE [Part::Box] Box021070  label="Krychle087"
  AttacherType = Attacher::AttachEngine3D
  Height = 17
  Length = 11
  Placement = pos=(-21,-28.5,6) rot=(0,0,1;0rad)
  Width = 9
FEATURE [Part::MultiFuse] Fusion005043005007002005
  Shapes = -> [Cylinder112024025003003006010004005,Box021070]
FEATURE [Part::Cylinder] Cylinder112024025003003006010004006  label="cy009"
  Angle = 360
  AttacherType = Attacher::AttachEngine3D
  Height = 24
  Placement = pos=(-9,-68,0) rot=(0,0,1;0rad)
  Radius = 2.2
FEATURE [Part::Feature] Cylinder112024025003003006010004007  label="holeě2i001"
  Placement = pos=(0,0,0) rot=(0,0,1;2.0944rad)
  shape: bbox 6 x 6 x 4 mm, 3 faces (baked)
FEATURE [Part::Feature] Cylinder112024025003003006010004008  label="hole1s001"
  Placement = pos=(0,0,0) rot=(0,0,1;4.18879rad)
  shape: bbox 3.4 x 3.4 x 10 mm, 3 faces (baked)
FEATURE [Part::Feature] Cylinder112024025003003006010004009  label="hole2s001"
  Placement = pos=(0,0,0) rot=(0,0,1;2.0944rad)
  shape: bbox 3.4 x 3.4 x 10 mm, 3 faces (baked)
FEATURE [Part::Feature] Cylinder112024025003003006010004010  label="hole1i001"
  Placement = pos=(0,0,0) rot=(0,0,1;4.18879rad)
  shape: bbox 6 x 6 x 4 mm, 3 faces (baked)
FEATURE [Part::Box] Box021071  label="cub006"
  AttacherType = Attacher::AttachEngine3D
  Height = 18
  Length = 28
  Placement = pos=(-14,-45,6) rot=(0,0,1;0rad)
  Width = 25
FEATURE [Part::Cylinder] Cylinder112024025003003006010004011  label="cy010"
  Angle = 360
  AttacherType = Attacher::AttachEngine3D
  Height = 15
  Placement = pos=(0,0,6) rot=(0,0,1;0rad)
  Radius = 25
FEATURE [Part::Cylinder] Cylinder112024025003003006010004012  label="cy011"
  Angle = 360
  AttacherType = Attacher::AttachEngine3D
  Height = 10
  Radius = 10
FEATURE [Part::Box] Box021072  label="Cub009"
  AttacherType = Attacher::AttachEngine3D
  Height = 16
  Length = 50
  Placement = pos=(-25,-25,6) rot=(0,0,1;0rad)
  Width = 12.5
FEATURE [Part::Box] Box021073  label="Cub010"
  AttacherType = Attacher::AttachEngine3D
  Height = 30
  Length = 50
  Placement = pos=(-25,-85,0) rot=(0,0,1;0rad)
  Width = 60
FEATURE [Part::Cylinder] Cylinder112024025003003006010004013  label="hole3s001"
  Angle = 360
  AttacherType = Attacher::AttachEngine3D
  Height = 10
  Placement = pos=(0,16.5,0) rot=(0,0,1;0rad)
  Radius = 1.7
FEATURE [Part::Box] Box021074  label="Cub011"
  AttacherType = Attacher::AttachEngine3D
  Height = 6
  Length = 50
  Placement = pos=(-25,-85,0) rot=(0,0,1;0rad)
  Width = 85
FEATURE [Part::Cylinder] Cylinder112024025003003006010004014  label="hole3i001"
  Angle = 360
  AttacherType = Attacher::AttachEngine3D
  Height = 4
  Placement = pos=(0,16.5,3) rot=(0,0,1;0rad)
  Radius = 3
FEATURE [Part::MultiFuse] Fusion005043005007002009  label="Hole for SC screw001"
  Placement = pos=(0,0,0) rot=(0,0,1;3.14159rad)
  Shapes = -> [Cylinder112024025003003006010004010,Cylinder112024025003003006010004008,Cylinder112024025003003006010004007,Cylinder112024025003003006010004009,Cylinder112024025003003006010004013,Cylinder112024025003003006010004014]
FEATURE [Part::Chamfer] Chamfer007
  Base = -> Box021072
  Edges = 1 edges r=12: [Edge12]
FEATURE [Part::Cylinder] Cylinder112024025003003006010004015  label="cy012"
  Angle = 360
  AttacherType = Attacher::AttachEngine3D
  Height = 24
  Placement = pos=(9,-68,0) rot=(0,0,1;0rad)
  Radius = 2.2
FEATURE [Part::Box] Box021075  label="cub007"
  AttacherType = Attacher::AttachEngine3D
  Height = 15
  Length = 42
  Placement = pos=(-21,-83,22) rot=(0,0,1;0rad)
  Width = 65
FEATURE [Part::Cylinder] Cylinder112024025003003006010004016  label="cy013"
  Angle = 360
  AttacherType = Attacher::AttachEngine3D
  Height = 24
  Placement = pos=(0,-45,0) rot=(0,0,1;0rad)
  Radius = 14
FEATURE [Part::Box] Box021076  label="cub008"
  AttacherType = Attacher::AttachEngine3D
  Height = 6
  Length = 28
  Placement = pos=(-14,-45,0) rot=(0,0,1;0rad)
  Width = 6
FEATURE [Part::Cylinder] Cylinder112024025003003006010004017  label="Cy010"
  Angle = 360
  AttacherType = Attacher::AttachEngine3D
  Height = 6
  Radius = 25
FEATURE [Part::MultiFuse] Fusion005043005007002008  label="Solid base001"
  Shapes = -> [Box021073,Cylinder112024025003003006010004017,Box021074,Chamfer007]
FEATURE [Part::Cylinder] Cylinder112024025003003006010004018  label="cy014"
  Angle = 360
  AttacherType = Attacher::AttachEngine3D
  Height = 24
  Placement = pos=(0,-39,0) rot=(0,0,1;0rad)
  Radius = 14
FEATURE [Part::Box] Box021077  label="cub009"
  AttacherType = Attacher::AttachEngine3D
  Height = 24
  Length = 4.4
  Placement = pos=(6.8,-80,0) rot=(0,0,1;0rad)
  Width = 12
FEATURE [Part::Box] Box021078  label="cub010"
  AttacherType = Attacher::AttachEngine3D
  Height = 24
  Length = 4.4
  Placement = pos=(-11.2,-80,0) rot=(0,0,1;0rad)
  Width = 12
FEATURE [Part::Cylinder] Cylinder112024025003003006010004019  label="cy015"
  Angle = 360
  AttacherType = Attacher::AttachEngine3D
  Height = 24
  Placement = pos=(-9,-80,0) rot=(0,0,1;0rad)
  Radius = 2.2
FEATURE [Part::Cylinder] Cylinder112024025003003006010004020  label="cy016"
  Angle = 360
  AttacherType = Attacher::AttachEngine3D
  Height = 24
  Placement = pos=(9,-80,0) rot=(0,0,1;0rad)
  Radius = 2.2
FEATURE [Part::MultiFuse] Fusion005043005007002007  label="Holes001"
  Shapes = -> [Cylinder112024025003003006010004016,Cylinder112024025003003006010004018,Box021076,Cylinder112024025003003006010004015,Cylinder112024025003003006010004006,Cylinder112024025003003006010004020,Cylinder112024025003003006010004019,Box021078,Box021077,Cylinder112024025003003006010004012,Box021071,Box021075,Cylinder112024025003003006010004011]
FEATURE [Part::Cut] Cut018020020009027020002003004004010  label="SCT-base001"
  Base = -> Fusion005043005007002008
  Tool = -> Fusion005043005007002007
FEATURE [Part::Fillet] Fillet018  label="SCT-EAF-no screw001"
  Base = -> Cut018020020009027020002003004004010
  Edges = 16 edges r=1.5: [Edge6,Edge7,Edge8,Edge20,Edge24,Edge51,Edge53,Edge54,Edge55,Edge60,Edge102,Edge104,Edge113,Edge115,Edge126,Edge127]
FEATURE [Part::Cut] Cut018020020009027020002003004004011  label="SCT-EAF 9,25 Edge HD001"
  Base = -> Fillet018
  Tool = -> Fusion005043005007002009
FEATURE [Part::Cylinder] Cylinder112024025003003006010004021  label="Válec192"
  Angle = 360
  AttacherType = Attacher::AttachEngine3D
  Height = 14
  Placement = pos=(14,-24,6) rot=(0,0,1;0rad)
  Radius = 1.15
FEATURE [Part::Box] Box021079  label="Krychle088"
  AttacherType = Attacher::AttachEngine3D
  Height = 14
  Length = 8
  Placement = pos=(10,-28.3,6) rot=(0,0,1;0rad)
  Width = 8.6
FEATURE [Part::Cylinder] Cylinder112024025003003006010004022  label="Válec193"
  Angle = 360
  AttacherType = Attacher::AttachEngine3D
  Height = 6
  Placement = pos=(10,-24,0) rot=(0,0,1;0rad)
  Radius = 1.7
FEATURE [Part::Box] Box021080  label="Krychle089"
  AttacherType = Attacher::AttachEngine3D
  Height = 6
  Length = 8
  Placement = pos=(10,-25.7,0) rot=(0,0,1;0rad)
  Width = 3.4
FEATURE [Part::Cylinder] Cylinder112024025003003006010004023  label="Válec194"
  Angle = 360
  AttacherType = Attacher::AttachEngine3D
  Height = 6
  Placement = pos=(18,-24,0) rot=(0,0,1;0rad)
  Radius = 1.7
FEATURE [Part::MultiFuse] Fusion005043005007002011
  Shapes = -> [Cylinder112024025003003006010004022,Box021080,Cylinder112024025003003006010004023]
FEATURE [Part::Cylinder] Cylinder112024025003003006010004024  label="Válec195"
  Angle = 360
  AttacherType = Attacher::AttachEngine3D
  Height = 6
  Placement = pos=(10,-24,0) rot=(0,0,1;0rad)
  Radius = 1.7
FEATURE [Part::Box] Box021081  label="Krychle090"
  AttacherType = Attacher::AttachEngine3D
  Height = 6
  Length = 8
  Placement = pos=(10,-25.7,0) rot=(0,0,1;0rad)
  Width = 3.4
FEATURE [Part::Cylinder] Cylinder112024025003003006010004025  label="Válec196"
  Angle = 360
  AttacherType = Attacher::AttachEngine3D
  Height = 6
  Placement = pos=(18,-24,0) rot=(0,0,1;0rad)
  Radius = 1.7
FEATURE [Part::MultiFuse] Fusion005043005007002012
  Placement = pos=(-28,0,0) rot=(0,0,1;0rad)
  Shapes = -> [Cylinder112024025003003006010004024,Box021081,Cylinder112024025003003006010004025]
FEATURE [Part::Cylinder] Cylinder112024025003003006010004026  label="Válec197"
  Angle = 360
  AttacherType = Attacher::AttachEngine3D
  Height = 50
  Placement = pos=(-25,-24,11) rot=(0,1,0;1.5708rad)
  Radius = 1.15
FEATURE [Part::Cylinder] Cylinder112024025003003006010004027  label="Válec198"
  Angle = 360
  AttacherType = Attacher::AttachEngine3D
  Height = 14
  Placement = pos=(10,-24,6) rot=(0,0,1;0rad)
  Radius = 4.3
FEATURE [Part::Cylinder] Cylinder112024025003003006010004028  label="Válec199"
  Angle = 360
  AttacherType = Attacher::AttachEngine3D
  Height = 14
  Placement = pos=(17.5,-24,11) rot=(0,1,0;1.5708rad)
  Radius = 1.7
FEATURE [Part::MultiFuse] Fusion005043005007002015
  Shapes = -> [Cylinder112024025003003006010004021,Cylinder112024025003003006010004028]
FEATURE [Part::Cylinder] Cylinder112024025003003006010004029  label="Válec200"
  Angle = 360
  AttacherType = Attacher::AttachEngine3D
  Height = 3.2
  Placement = pos=(10,-24,0) rot=(0,0,1;0rad)
  Radius = 3
FEATURE [Part::Box] Box021082  label="Krychle091"
  AttacherType = Attacher::AttachEngine3D
  Height = 3.2
  Length = 8
  Placement = pos=(10,-27,0) rot=(0,0,1;0rad)
  Width = 6
FEATURE [Part::Cylinder] Cylinder112024025003003006010004030  label="Válec201"
  Angle = 360
  AttacherType = Attacher::AttachEngine3D
  Height = 3.2
  Placement = pos=(18,-24,0) rot=(0,0,1;0rad)
  Radius = 3
FEATURE [Part::MultiFuse] Fusion005043005007002016
  Shapes = -> [Cylinder112024025003003006010004029,Box021082,Cylinder112024025003003006010004030]
FEATURE [Part::Box] Box021083  label="Krychle092"
  AttacherType = Attacher::AttachEngine3D
  Height = 3.2
  Length = 8
  Placement = pos=(10,-27,0) rot=(0,0,1;0rad)
  Width = 6
FEATURE [Part::Cylinder] Cylinder112024025003003006010004031  label="Válec202"
  Angle = 360
  AttacherType = Attacher::AttachEngine3D
  Height = 3.2
  Placement = pos=(10,-24,0) rot=(0,0,1;0rad)
  Radius = 3
FEATURE [Part::Cylinder] Cylinder112024025003003006010004032  label="Válec203"
  Angle = 360
  AttacherType = Attacher::AttachEngine3D
  Height = 3.2
  Placement = pos=(18,-24,0) rot=(0,0,1;0rad)
  Radius = 3
FEATURE [Part::MultiFuse] Fusion005043005007002017
  Placement = pos=(-28,0,0) rot=(0,0,1;0rad)
  Shapes = -> [Cylinder112024025003003006010004031,Box021083,Cylinder112024025003003006010004032]
FEATURE [Part::MultiFuse] Fusion005043005007002006
  Shapes = -> [Fusion005043005007002004,Fusion005043005007002005,Fusion005043005007002011,Fusion005043005007002012,Cylinder112024025003003006010004026,Fusion005043005007002016,Fusion005043005007002017]
FEATURE [Part::Cut] Cut018020020009027020002003004004012  label="STC-EAF V2"
  Base = -> Cut018020020009027020002003004004011
  Tool = -> Fusion005043005007002006
FEATURE [Part::Cylinder] Cylinder112024025003003006010004033  label="Válec204"
  Angle = 360
  AttacherType = Attacher::AttachEngine3D
  Height = 10
  Placement = pos=(8.5,0,0) rot=(0,0,1;0.349066rad)
  Radius = 1
FEATURE [Part::Cylinder] Cylinder112024025003003006010004034  label="Válec205"
  Angle = 360
  AttacherType = Attacher::AttachEngine3D
  Height = 7
  Radius = 8.5
FEATURE [Part::Feature] Cylinder112024025003003006010004035  label="Válec206"
  Placement = pos=(0,0,0) rot=(0,0,1;0.349066rad)
  shape: bbox 2 x 2 x 10 mm, 3 faces (baked)
FEATURE [Part::Feature] Fusion005043005007002021
  Placement = pos=(0,0,0) rot=(0,0,1;2.0944rad)
  shape: bbox 6.25 x 14.82 x 10 mm, 18 faces, 6 solids (baked)
FEATURE [Part::Feature] Fusion005043005007002022
  Placement = pos=(0,0,0) rot=(0,0,1;4.18879rad)
  shape: bbox 14.24 x 7.464 x 10 mm, 18 faces, 6 solids (baked)
FEATURE [Part::Feature] Fusion005043005007002023
  Placement = pos=(0,0,0) rot=(0,0,1;1.0472rad)
  shape: bbox 7.726 x 3.01 x 10 mm, 9 faces, 3 solids (baked)
FEATURE [Part::Feature] Cylinder112024025003003006010004036  label="Válec207"
  Placement = pos=(0,0,0) rot=(0,0,1;0.698132rad)
  shape: bbox 2 x 2 x 10 mm, 3 faces (baked)
FEATURE [Part::MultiFuse] Fusion005043005007002020
  Shapes = -> [Cylinder112024025003003006010004033,Cylinder112024025003003006010004035,Cylinder112024025003003006010004036]
FEATURE [Part::MultiFuse] Fusion005043005007002019
  Shapes = -> [Fusion005043005007002020,Fusion005043005007002023]
FEATURE [Part::MultiFuse] Fusion005043005007002018
  Shapes = -> [Fusion005043005007002022,Fusion005043005007002021,Fusion005043005007002019]
FEATURE [Part::FeaturePython] Screw005  label="M3x10-Screw"  # Fasteners workbench fastener (typed FeaturePython)
  Placement = pos=(0,0,4) rot=(0,0,1;0rad)
  diameter = 3
  invert = false
  length = 3
  matchOuter = false
  offset = 0
  thread = false
  type = 5
FEATURE [Part::Cut] Cut018020020009027020002003004004014
  Base = -> Cylinder112024025003003006010004034
  Tool = -> Screw005
FEATURE [Part::Fillet] Fillet019
  Base = -> Cut018020020009027020002003004004014
  Edges = 2 edges r=1.5: [Edge1,Edge3]
FEATURE [Part::Cut] Cut018020020009027020002003004004015
  Base = -> Fillet019
  Tool = -> Fusion005043005007002018
FEATURE [Part::Cylinder] Cylinder112024025003003006010004037  label="Válec208"
  Angle = 360
  AttacherType = Attacher::AttachEngine3D
  Height = 3
  Placement = pos=(0,0,4) rot=(0,0,1;0rad)
  Radius = 2.5
FEATURE [Part::Cut] Cut018020020009027020002003004004016  label="Knob M3"
  Base = -> Cut018020020009027020002003004004015
  Tool = -> Cylinder112024025003003006010004037
FEATURE [Part::FeaturePython] Screw006  label="M4x10-Screw"  # Fasteners workbench fastener (typed FeaturePython)
  Placement = pos=(0,0,6) rot=(0,0,1;0rad)
  diameter = 4
  invert = false
  length = 2
  matchOuter = false
  offset = 0
  thread = false
  type = 5
FEATURE [Part::Feature] Fusion005043005007002024
  Placement = pos=(0,0,0) rot=(0,0,1;2.0944rad)
  shape: bbox 6.25 x 14.82 x 10 mm, 18 faces, 6 solids (baked)
FEATURE [Part::Feature] Fusion005043005007002025
  Placement = pos=(0,0,0) rot=(0,0,1;4.18879rad)
  shape: bbox 14.24 x 7.464 x 10 mm, 18 faces, 6 solids (baked)
FEATURE [Part::Feature] Fusion005043005007002026
  Placement = pos=(0,0,0) rot=(0,0,1;1.0472rad)
  shape: bbox 7.726 x 3.01 x 10 mm, 9 faces, 3 solids (baked)
FEATURE [Part::Feature] Cylinder112024025003003006010004038  label="Válec209"
  Placement = pos=(0,0,0) rot=(0,0,1;0.698132rad)
  shape: bbox 2 x 2 x 10 mm, 3 faces (baked)
FEATURE [Part::Feature] Cylinder112024025003003006010004039  label="Válec210"
  Placement = pos=(0,0,0) rot=(0,0,1;0.349066rad)
  shape: bbox 2 x 2 x 10 mm, 3 faces (baked)
FEATURE [Part::Cylinder] Cylinder112024025003003006010004040  label="Válec211"
  Angle = 360
  AttacherType = Attacher::AttachEngine3D
  Height = 10
  Placement = pos=(8.5,0,0) rot=(0,0,1;0.349066rad)
  Radius = 1
FEATURE [Part::Cylinder] Cylinder112024025003003006010004041  label="Válec212"
  Angle = 360
  AttacherType = Attacher::AttachEngine3D
  Height = 10
  Radius = 8.5
FEATURE [Part::Cylinder] Cylinder112024025003003006010004042  label="Válec213"
  Angle = 360
  AttacherType = Attacher::AttachEngine3D
  Height = 4
  Placement = pos=(0,0,6) rot=(0,0,1;0rad)
  Radius = 3.1
FEATURE [Part::MultiFuse] Fusion005043005007002029
  Shapes = -> [Cylinder112024025003003006010004040,Cylinder112024025003003006010004039,Cylinder112024025003003006010004038]
FEATURE [Part::MultiFuse] Fusion005043005007002028
  Shapes = -> [Fusion005043005007002029,Fusion005043005007002026]
FEATURE [Part::MultiFuse] Fusion005043005007002027
  Shapes = -> [Fusion005043005007002025,Fusion005043005007002024,Fusion005043005007002028]
FEATURE [Part::MultiFuse] Fusion005043005007002030
  Shapes = -> [Cylinder112024025003003006010004042,Screw006]
FEATURE [Part::Cut] Cut018020020009027020002003004004017
  Base = -> Cylinder112024025003003006010004041
  Tool = -> Fusion005043005007002030
FEATURE [Part::Fillet] Fillet020
  Base = -> Cut018020020009027020002003004004017
  Edges = 2 edges r=1.6: [Edge1,Edge3]
FEATURE [Part::Cut] Cut018020020009027020002003004004018  label="Knib M4 v2"
  Base = -> Fillet020
  Tool = -> Fusion005043005007002027
FEATURE [Part::Cylinder] Cylinder112024025003003006010004043  label="Válec214"
  Angle = 360
  AttacherType = Attacher::AttachEngine3D
  Height = 14
  Placement = pos=(11,-24,4) rot=(0,0,1;0rad)
  Radius = 1
FEATURE [Part::MultiFuse] Fusion005043005007002014
  Shapes = -> [Box021079,Cylinder112024025003003006010004027,Cylinder112024025003003006010004043]
FEATURE [Part::Cut] Cut018020020009027020002003004004013  label="kladka"
  Base = -> Fusion005043005007002014
  Tool = -> Fusion005043005007002015
FEATURE [Part::Chamfer] Chamfer008  label=" tensioner"
  Base = -> Cut018020020009027020002003004004013
  Edges = 2 edges r=0.3: [Edge1,Edge4]
FEATURE [App::Part] Part006  label="SCT - V2"
  Group = -> [Cut018020020009027020002003004004010,Cut018020020009027020002003004004011,Chamfer007,Fillet018,Cylinder112024025003003006010004004,Box021072,Box021074,Box021073,Box021070,Cylinder112024025003003006010004006,Cylinder112024025003003006010004011,Box021069,Box021071,Cylinder112024025003003006010004014,Cylinder112024025003003006010004015,Cylinder112024025003003006010004016,Box021075,Box021076,+62 more]
  License = CC BY 3.0
  LicenseURL = http://creativecommons.org/licenses/by/3.0/
  Origin = -> Origin006
FEATURE [Part::Feature] Cylinder112024025003003006010004044  label="holeě2i002"
  Placement = pos=(0,0,0) rot=(0,0,1;2.0944rad)
  shape: bbox 6 x 6 x 4 mm, 3 faces (baked)
FEATURE [Part::Feature] Cylinder112024025003003006010004045  label="hole1s002"
  Placement = pos=(0,0,0) rot=(0,0,1;4.18879rad)
  shape: bbox 3.4 x 3.4 x 10 mm, 3 faces (baked)
FEATURE [Part::Feature] Cylinder112024025003003006010004046  label="hole2s002"
  Placement = pos=(0,0,0) rot=(0,0,1;2.0944rad)
  shape: bbox 3.4 x 3.4 x 10 mm, 3 faces (baked)
FEATURE [Part::Feature] Cylinder112024025003003006010004047  label="hole1i002"
  Placement = pos=(0,0,0) rot=(0,0,1;4.18879rad)
  shape: bbox 6 x 6 x 4 mm, 3 faces (baked)
FEATURE [Part::Box] Box021084  label="Cub012"
  AttacherType = Attacher::AttachEngine3D
  Height = 31
  Length = 50
  Placement = pos=(-25,-93,0) rot=(0,0,1;0rad)
  Width = 68
FEATURE [Part::Cylinder] Cylinder112024025003003006010004048  label="Cy011"
  Angle = 360
  AttacherType = Attacher::AttachEngine3D
  Height = 6
  Radius = 25
FEATURE [Part::Cylinder] Cylinder112024025003003006010004049  label="hole3i002"
  Angle = 360
  AttacherType = Attacher::AttachEngine3D
  Height = 4
  Placement = pos=(0,16.5,3) rot=(0,0,1;0rad)
  Radius = 3
FEATURE [Part::Cylinder] Cylinder112024025003003006010004052  label="cy017"
  Angle = 360
  AttacherType = Attacher::AttachEngine3D
  Height = 24
  Placement = pos=(-9,-68,0) rot=(0,0,1;0rad)
  Radius = 2.2
FEATURE [Part::Box] Box021087  label="cub011"
  AttacherType = Attacher::AttachEngine3D
  Height = 18
  Length = 28
  Placement = pos=(-14,-45,6) rot=(0,0,1;0rad)
  Width = 25
FEATURE [Part::Cylinder] Cylinder112024025003003006010004053  label="cy018"
  Angle = 360
  AttacherType = Attacher::AttachEngine3D
  Height = 15
  Placement = pos=(0,0,6) rot=(0,0,1;0rad)
  Radius = 25
FEATURE [Part::Box] Box021088  label="Cub013"
  AttacherType = Attacher::AttachEngine3D
  Height = 16
  Length = 50
  Placement = pos=(-25,-25,6) rot=(0,0,1;0rad)
  Width = 12.5
FEATURE [Part::Chamfer] Chamfer009
  Base = -> Box021088
  Edges = 1 edges r=12: [Edge12]
FEATURE [Part::Box] Box021089  label="Cub014"
  AttacherType = Attacher::AttachEngine3D
  Height = 6
  Length = 50
  Placement = pos=(-25,-85,0) rot=(0,0,1;0rad)
  Width = 85
FEATURE [Part::Cylinder] Cylinder112024025003003006010004054  label="cy019"
  Angle = 360
  AttacherType = Attacher::AttachEngine3D
  Height = 24
  Placement = pos=(9,-68,0) rot=(0,0,1;0rad)
  Radius = 2.2
FEATURE [Part::Box] Box021090  label="cub012"
  AttacherType = Attacher::AttachEngine3D
  Height = 18
  Length = 42
  Placement = pos=(-21,-90,19) rot=(0,0,1;0rad)
  Width = 72
FEATURE [Part::Cylinder] Cylinder112024025003003006010004055  label="cy020"
  Angle = 360
  AttacherType = Attacher::AttachEngine3D
  Height = 10
  Radius = 10
FEATURE [Part::Cylinder] Cylinder112024025003003006010004056  label="hole3s002"
  Angle = 360
  AttacherType = Attacher::AttachEngine3D
  Height = 10
  Placement = pos=(0,16.5,0) rot=(0,0,1;0rad)
  Radius = 1.7
FEATURE [Part::Cylinder] Cylinder112024025003003006010004057  label="cy021"
  Angle = 360
  AttacherType = Attacher::AttachEngine3D
  Height = 24
  Placement = pos=(0,-45,0) rot=(0,0,1;0rad)
  Radius = 14
FEATURE [Part::Box] Box021091  label="cub013"
  AttacherType = Attacher::AttachEngine3D
  Height = 6
  Length = 28
  Placement = pos=(-14,-45,0) rot=(0,0,1;0rad)
  Width = 6
FEATURE [Part::MultiFuse] Fusion005043005007002034  label="Hole for SC screw002"
  Placement = pos=(0,0,0) rot=(0,0,1;3.14159rad)
  Shapes = -> [Cylinder112024025003003006010004047,Cylinder112024025003003006010004045,Cylinder112024025003003006010004044,Cylinder112024025003003006010004046,Cylinder112024025003003006010004056,Cylinder112024025003003006010004049]
FEATURE [Part::MultiFuse] Fusion005043005007002039  label="Solid base002"
  Shapes = -> [Box021084,Cylinder112024025003003006010004048,Box021089,Chamfer009]
FEATURE [Part::Box] Box021096  label="cub014"
  AttacherType = Attacher::AttachEngine3D
  Height = 24
  Length = 4.4
  Placement = pos=(6.8,-80,0) rot=(0,0,1;0rad)
  Width = 12
FEATURE [Part::Cylinder] Cylinder112024025003003006010004066  label="cy022"
  Angle = 360
  AttacherType = Attacher::AttachEngine3D
  Height = 24
  Placement = pos=(9,-80,0) rot=(0,0,1;0rad)
  Radius = 2.2
FEATURE [Part::Cylinder] Cylinder112024025003003006010004067  label="cy023"
  Angle = 360
  AttacherType = Attacher::AttachEngine3D
  Height = 24
  Placement = pos=(-9,-80,0) rot=(0,0,1;0rad)
  Radius = 2.2
FEATURE [Part::Box] Box021097  label="cub015"
  AttacherType = Attacher::AttachEngine3D
  Height = 24
  Length = 4.4
  Placement = pos=(-11.2,-80,0) rot=(0,0,1;0rad)
  Width = 12
FEATURE [Part::Cylinder] Cylinder112024025003003006010004069  label="cy024"
  Angle = 360
  AttacherType = Attacher::AttachEngine3D
  Height = 24
  Placement = pos=(0,-39,0) rot=(0,0,1;0rad)
  Radius = 14
FEATURE [Part::Box] Box021098  label="Krychle099"
  AttacherType = Attacher::AttachEngine3D
  Height = 3
  Length = 41
  Placement = pos=(-20.5,-83,19) rot=(0,0,1;0rad)
  Width = 61
FEATURE [Part::Box] Box021099  label="Krychle100"
  AttacherType = Attacher::AttachEngine3D
  Height = 12
  Length = 41
  Placement = pos=(-20.5,-83,19) rot=(0,0,1;0rad)
  Width = 6
FEATURE [Part::Box] Box021100  label="Krychle101"
  AttacherType = Attacher::AttachEngine3D
  Height = 8
  Length = 41
  Placement = pos=(-20.5,-24.5,19) rot=(0,0,1;0rad)
  Width = 2.5
FEATURE [Part::MultiFuse] Fusion005043005007002041  label="Plate"
  Shapes = -> [Box021100,Box021099,Box021098]
FEATURE [Part::Cylinder] Cylinder112024025003003006010004070  label="cy025"
  Angle = 360
  AttacherType = Attacher::AttachEngine3D
  Height = 24
  Placement = pos=(0,-39,0) rot=(0,0,1;0rad)
  Radius = 14
FEATURE [Part::Cylinder] Cylinder112024025003003006010004071  label="cy026"
  Angle = 360
  AttacherType = Attacher::AttachEngine3D
  Height = 24
  Placement = pos=(-9,-72.5,0) rot=(0,0,1;0rad)
  Radius = 2.2
FEATURE [Part::Cylinder] Cylinder112024025003003006010004072  label="cy027"
  Angle = 360
  AttacherType = Attacher::AttachEngine3D
  Height = 24
  Placement = pos=(9,-72.5,0) rot=(0,0,1;0rad)
  Radius = 2.2
FEATURE [Part::FeaturePython] Screw007  label="M4x25-Screw"  # Fasteners workbench fastener (typed FeaturePython)
  Placement = pos=(0,-79.75,26) rot=(-1,0,0;1.5708rad)
  diameter = 6
  invert = false
  length = 0
  matchOuter = false
  offset = 0
  thread = false
  type = 13
FEATURE [Part::Cylinder] Cylinder112024025003003006010004073  label="cy028"
  Angle = 360
  AttacherType = Attacher::AttachEngine3D
  Height = 24
  Placement = pos=(0,-72.5,26) rot=(1,0,0;1.5708rad)
  Radius = 2.2
FEATURE [Part::MultiFuse] Fusion005043005007002036  label="Holes002"
  Shapes = -> [Cylinder112024025003003006010004057,Cylinder112024025003003006010004069,Box021091,Cylinder112024025003003006010004054,Cylinder112024025003003006010004052,Cylinder112024025003003006010004066,Cylinder112024025003003006010004067,Box021097,Box021096,Cylinder112024025003003006010004055,Box021087,Box021090,Cylinder112024025003003006010004053,Cylinder112024025003003006010004073]
FEATURE [Part::Cut] Cut018020020009027020002003004004019  label="SCT-base002"
  Base = -> Fusion005043005007002039
  Tool = -> Fusion005043005007002036
FEATURE [Part::Fillet] Fillet021  label="SCT-EAF-no screw002"
  Base = -> Cut018020020009027020002003004004019
  Edges = 9 edges: [Edge6 r=1.5,Edge7 r=1.5,Edge8 r=1.5,Edge29 r=1,Edge30 r=1,Edge31 r=1,Edge109 r=1,Edge118 r=1,Edge134 r=1]
FEATURE [Part::Cut] Cut018020020009027020002003004004020  label="SCT-EAF 9,25 Edge HD V3"
  Base = -> Fillet021
  Tool = -> Fusion005043005007002034
FEATURE [Part::MultiFuse] Fusion005043005007002042
  Shapes = -> [Screw007,Cylinder112024025003003006010004070,Cylinder112024025003003006010004071,Cylinder112024025003003006010004072]
FEATURE [Part::Cut] Cut018020020009027020002003004004021
  Base = -> Fusion005043005007002041
  Tool = -> Fusion005043005007002042
FEATURE [Part::Fillet] Fillet022  label="Motor plate"
  Base = -> Cut018020020009027020002003004004021
  Edges = 4 edges r=1: [Edge2,Edge4,Edge32,Edge63]
FEATURE [App::Part] Part007  label="SCT EAF V3"
  Group = -> [Fusion005043005007002042,Fusion005043005007002041,Screw007,Cylinder112024025003003006010004071,Box021099,Cylinder112024025003003006010004072,Box021100,Box021098,Cylinder112024025003003006010004070,Cut018020020009027020002003004004021,Fillet022,Chamfer009,Fillet021,Cut018020020009027020002003004004019,Fusion005043005007002034,Fusion005043005007002036,Cylinder112024025003003006010004045,+25 more]
  License = CC BY 3.0
  LicenseURL = http://creativecommons.org/licenses/by/3.0/
  Origin = -> Origin007
FEATURE [Part::FeaturePython] Screw009  label="M4x30-Screw003"  # Fasteners workbench fastener (typed FeaturePython)
  Placement = pos=(0,0,2.25) rot=(0,0,1;0rad)
  diameter = 6
  invert = false
  length = 1
  matchOuter = false
  offset = 0
  thread = false
  type = 13
FEATURE [Part::Cylinder] Cylinder112024025003003006010004075  label="Válec227"
  Angle = 360
  AttacherType = Attacher::AttachEngine3D
  Height = 10
  Placement = pos=(8.5,0,0) rot=(0,0,1;0.349066rad)
  Radius = 1
FEATURE [Part::Cylinder] Cylinder112024025003003006010004076  label="Válec228"
  Angle = 360
  AttacherType = Attacher::AttachEngine3D
  Height = 5
  Radius = 8.5
FEATURE [Part::Cut] Cut018020020009027020002003004004023
  Base = -> Cylinder112024025003003006010004076
  Tool = -> Screw009
FEATURE [Part::Fillet] Fillet024  label="knob003"
  Base = -> Cut018020020009027020002003004004023
  Edges = 2 edges r=2: [Edge1,Edge3]
FEATURE [Part::Feature] Cylinder112024025003003006010004077  label="Válec229"
  Placement = pos=(0,0,0) rot=(0,0,1;0.349066rad)
  shape: bbox 2 x 2 x 10 mm, 3 faces (baked)
FEATURE [Part::Feature] Fusion005043005007002046
  Placement = pos=(0,0,0) rot=(0,0,1;2.0944rad)
  shape: bbox 6.25 x 14.82 x 10 mm, 18 faces, 6 solids (baked)
FEATURE [Part::Feature] Cylinder112024025003003006010004078  label="Válec230"
  Placement = pos=(0,0,0) rot=(0,0,1;0.698132rad)
  shape: bbox 2 x 2 x 10 mm, 3 faces (baked)
FEATURE [Part::MultiFuse] Fusion005043005007002045
  Shapes = -> [Cylinder112024025003003006010004075,Cylinder112024025003003006010004077,Cylinder112024025003003006010004078]
FEATURE [Part::Feature] Fusion005043005007002047
  Placement = pos=(0,0,0) rot=(0,0,1;1.0472rad)
  shape: bbox 7.726 x 3.01 x 10 mm, 9 faces, 3 solids (baked)
FEATURE [Part::MultiFuse] Fusion005043005007002044
  Shapes = -> [Fusion005043005007002045,Fusion005043005007002047]
FEATURE [Part::Feature] Fusion005043005007002048
  Placement = pos=(0,0,0) rot=(0,0,1;4.18879rad)
  shape: bbox 14.24 x 7.464 x 10 mm, 18 faces, 6 solids (baked)
FEATURE [Part::MultiFuse] Fusion005043005007002043
  Shapes = -> [Fusion005043005007002048,Fusion005043005007002046,Fusion005043005007002044]
FEATURE [Part::Cut] Cut018020020009027020002003004004024  label="Knob M4 v003"
  Base = -> Fillet024
  Tool = -> Fusion005043005007002043
FEATURE [App::Part] Part005  label="Knob M4"
  Group = -> [Cylinder112024022,Cut018020020009027020002003004003,Screw,Fillet013,Cut018020020009027020002003004004008,Screw001,Cylinder112024025003003006010003,Cylinder112024025003003006010004,Cylinder112024025003003006010004002,Fusion005043005007001,Fusion005043005007002001,Fusion005043005007002002,Cylinder112024025003003006010004001,Fusion005043005007002,Fusion005043005007,Fusion005043005007002003,Fillet017,+31 more]
  License = CC BY 3.0
  LicenseURL = http://creativecommons.org/licenses/by/3.0/
  Origin = -> Origin005
FEATURE [App::Part] Part  label="Newton"
  Group = -> [Fusion,Fusion001,Cut,Cylinder005,Cylinder001,Cylinder006,Box004,Box005,Box001,Cylinder004,Cylinder003,Box002,Box,Cylinder002,Box003,Cylinder,Cut018020020009027020001,Cut018020020009027020002,Cut018020020009027020002003003,Fillet,Part005]
  License = CC BY 3.0
  LicenseURL = http://creativecommons.org/licenses/by/3.0/
  Origin = -> Origin
FEATURE [Part::Feature] Cut018020020009027020002003004004025  label="base nema001"
  shape: bbox 50 x 86 x 24 mm, 75 faces (baked)
FEATURE [Part::Cylinder] Cylinder112024025003003006010004079  label="Válec231"
  Angle = 360
  AttacherType = Attacher::AttachEngine3D
  Height = 10
  Placement = pos=(0,-37,0) rot=(0,0,1;0rad)
  Radius = 10
FEATURE [Part::Cylinder] Cylinder112024025003003006010004080  label="Válec232"
  Angle = 360
  AttacherType = Attacher::AttachEngine3D
  Height = 10
  Placement = pos=(-9,-68,0) rot=(0,0,1;0rad)
  Radius = 2.2
FEATURE [Part::Box] Box021101  label="Krychle102"
  AttacherType = Attacher::AttachEngine3D
  Height = 10
  Length = 4.4
  Placement = pos=(6.8,-80,0) rot=(0,0,1;0rad)
  Width = 12
FEATURE [Part::Box] Box021102  label="Krychle103"
  AttacherType = Attacher::AttachEngine3D
  Height = 10
  Length = 20
  Placement = pos=(-10,-45,0) rot=(0,0,1;0rad)
  Width = 8
FEATURE [Part::Cylinder] Cylinder112024025003003006010004081  label="Válec233"
  Angle = 360
  AttacherType = Attacher::AttachEngine3D
  Height = 10
  Placement = pos=(-9,-80,0) rot=(0,0,1;0rad)
  Radius = 2.2
FEATURE [Part::Cylinder] Cylinder112024025003003006010004082  label="Válec234"
  Angle = 360
  AttacherType = Attacher::AttachEngine3D
  Height = 10
  Placement = pos=(9,-68,0) rot=(0,0,1;0rad)
  Radius = 2.2
FEATURE [Part::Box] Box021103  label="Krychle104"
  AttacherType = Attacher::AttachEngine3D
  Height = 10
  Length = 4.4
  Placement = pos=(-11.2,-80,0) rot=(0,0,1;0rad)
  Width = 12
FEATURE [Part::Box] Box021104  label="Kry002"
  AttacherType = Attacher::AttachEngine3D
  Height = 24
  Length = 42
  Placement = pos=(-21,-93,-19.5) rot=(0,0,1;0rad)
  Width = 75
FEATURE [Part::Cylinder] Cylinder112024025003003006010004083  label="Válec235"
  Angle = 360
  AttacherType = Attacher::AttachEngine3D
  Height = 10
  Placement = pos=(0,-45,0) rot=(0,0,1;0rad)
  Radius = 10
FEATURE [Part::Cylinder] Cylinder112024025003003006010004084  label="Válec236"
  Angle = 360
  AttacherType = Attacher::AttachEngine3D
  Height = 10
  Placement = pos=(9,-80,0) rot=(0,0,1;0rad)
  Radius = 2.2
FEATURE [Part::Cylinder] Cylinder112024025003003006010004085  label="Válec237"
  Angle = 360
  AttacherType = Attacher::AttachEngine3D
  Height = 27
  Placement = pos=(0,0,-17) rot=(0,0,1;0rad)
  Radius = 14.7
FEATURE [Part::Box] Box021105  label="Krychle105"
  AttacherType = Attacher::AttachEngine3D
  Height = 24
  Length = 50
  Placement = pos=(-25,-66,-16) rot=(0,0,1;0rad)
  Width = 51
FEATURE [Part::Cut] Cut018020020009027020002003004004027
  Base = -> Cut018020020009027020002003004004025
  Tool = -> Box021105
FEATURE [Part::Box] Box021106  label="Krychle106"
  AttacherType = Attacher::AttachEngine3D
  Height = 24
  Length = 50
  Placement = pos=(-25,-96,-16) rot=(0,0,1;0rad)
  Width = 81
FEATURE [Part::MultiFuse] Fusion005043005007002050
  Shapes = -> [Box021106,Cut018020020009027020002003004004027]
FEATURE [Part::FeaturePython] Screw010  label="M4x25-Screw001"  # Fasteners workbench fastener (typed FeaturePython)
  Placement = pos=(0,-79.75,26) rot=(-1,0,0;1.5708rad)
  diameter = 6
  invert = false
  length = 0
  matchOuter = false
  offset = 0
  thread = false
  type = 13
FEATURE [Part::Box] Box021107  label="Krychle107"
  AttacherType = Attacher::AttachEngine3D
  Height = 12
  Length = 41
  Placement = pos=(-20.5,-83,19) rot=(0,0,1;0rad)
  Width = 6
FEATURE [Part::Cylinder] Cylinder112024025003003006010004086  label="cy029"
  Angle = 360
  AttacherType = Attacher::AttachEngine3D
  Height = 24
  Placement = pos=(0,-39,0) rot=(0,0,1;0rad)
  Radius = 14
FEATURE [Part::Cylinder] Cylinder112024025003003006010004087  label="cy030"
  Angle = 360
  AttacherType = Attacher::AttachEngine3D
  Height = 24
  Placement = pos=(9,-72.5,0) rot=(0,0,1;0rad)
  Radius = 2.2
FEATURE [Part::Cylinder] Cylinder112024025003003006010004088  label="cy031"
  Angle = 360
  AttacherType = Attacher::AttachEngine3D
  Height = 24
  Placement = pos=(-9,-72.5,0) rot=(0,0,1;0rad)
  Radius = 2.2
FEATURE [Part::MultiFuse] Fusion005043005007002052
  Shapes = -> [Screw010,Cylinder112024025003003006010004086,Cylinder112024025003003006010004088,Cylinder112024025003003006010004087]
FEATURE [Part::Box] Box021108  label="Krychle108"
  AttacherType = Attacher::AttachEngine3D
  Height = 3
  Length = 41
  Placement = pos=(-20.5,-83,19) rot=(0,0,1;0rad)
  Width = 61
FEATURE [Part::Box] Box021109  label="Krychle109"
  AttacherType = Attacher::AttachEngine3D
  Height = 8
  Length = 41
  Placement = pos=(-20.5,-24.5,19) rot=(0,0,1;0rad)
  Width = 2.5
FEATURE [Part::MultiFuse] Fusion005043005007002051  label="Plate001"
  Shapes = -> [Box021109,Box021107,Box021108]
FEATURE [Part::Cut] Cut018020020009027020002003004004028
  Base = -> Fusion005043005007002051
  Tool = -> Fusion005043005007002052
FEATURE [Part::Fillet] Fillet025  label="Motor plate001"
  Base = -> Cut018020020009027020002003004004028
  Edges = 4 edges r=1: [Edge2,Edge4,Edge32,Edge63]
  Placement = pos=(0,0,24) rot=(0,1,0;3.14159rad)
FEATURE [Part::Cylinder] Cylinder112024025003003006010004089  label="Válec238"
  Angle = 360
  AttacherType = Attacher::AttachEngine3D
  Height = 10
  Placement = pos=(0,-89,-2) rot=(1,0,0;1.5708rad)
  Radius = 2.2
FEATURE [Part::MultiFuse] Fusion005043005007002049
  Shapes = -> [Cylinder112024025003003006010004085,Cylinder112024025003003006010004083,Cylinder112024025003003006010004079,Box021102,Cylinder112024025003003006010004082,Cylinder112024025003003006010004080,Cylinder112024025003003006010004084,Cylinder112024025003003006010004081,Box021103,Box021101,Box021104,Cylinder112024025003003006010004089]
FEATURE [Part::Cut] Cut018020020009027020002003004004026  label="N_EAF003"
  Base = -> Fusion005043005007002050
  Tool = -> Fusion005043005007002049
FEATURE [Part::Feature] Cut018020020009027020002003004004026001  label="N_EAF004"
  shape: bbox 50 x 116 x 24 mm, 62 faces (baked)
FEATURE [Part::Fillet] Fillet026  label="N_EAFV2"
  Base = -> Cut018020020009027020002003004004026001
  Edges = 8 edges r=1: [Edge75,Edge76,Edge78,Edge79,Edge80,Edge81,Edge177,Edge180]
FEATURE [App::Part] Part009  label="Newton V2"
  Group = -> [Cut018020020009027020002003004004026001,Fillet026,Cut018020020009027020002003004004025,Fusion005043005007002050,Fusion005043005007002049,Cylinder112024025003003006010004080,Cylinder112024025003003006010004079,Box021102,Box021103,Box021104,Cylinder112024025003003006010004081,Cylinder112024025003003006010004084,Cylinder112024025003003006010004085,Box021105,Cylinder112024025003003006010004082,+6 more]
  Origin = -> Origin009
FEATURE [Part::Feature] Cut018020020009027020002003004004026002  label="Nema refractor001"
  shape: bbox 50 x 89 x 24 mm, 96 faces (baked)
FEATURE [Part::Box] Box021110  label="Krychle110"
  AttacherType = Attacher::AttachEngine3D
  Height = 24
  Length = 50
  Placement = pos=(-25,-66,-16) rot=(0,0,1;0rad)
  Width = 51
FEATURE [Part::Cut] Cut018020020009027020002003004004026004
  Base = -> Cut018020020009027020002003004004026002
  Tool = -> Box021110
FEATURE [Part::Box] Box021111  label="Krychle111"
  AttacherType = Attacher::AttachEngine3D
  Height = 24
  Length = 50
  Placement = pos=(-25,-96,-16) rot=(0,0,1;0rad)
  Width = 81
FEATURE [Part::MultiFuse] Fusion005043005007002054
  Shapes = -> [Cut018020020009027020002003004004026004,Box021111]
FEATURE [Part::Box] Box021112  label="Krychle112"
  AttacherType = Attacher::AttachEngine3D
  Height = 10
  Length = 4.4
  Placement = pos=(6.8,-80,0) rot=(0,0,1;0rad)
  Width = 12
FEATURE [Part::Cylinder] Cylinder112024025003003006010004090  label="Válec239"
  Angle = 360
  AttacherType = Attacher::AttachEngine3D
  Height = 10
  Placement = pos=(0,-45,0) rot=(0,0,1;0rad)
  Radius = 10
FEATURE [Part::Box] Box021113  label="Krychle113"
  AttacherType = Attacher::AttachEngine3D
  Height = 10
  Length = 4.4
  Placement = pos=(-11.2,-80,0) rot=(0,0,1;0rad)
  Width = 12
FEATURE [Part::Cylinder] Cylinder112024025003003006010004091  label="Válec240"
  Angle = 360
  AttacherType = Attacher::AttachEngine3D
  Height = 10
  Placement = pos=(9,-80,0) rot=(0,0,1;0rad)
  Radius = 2.2
FEATURE [Part::Cylinder] Cylinder112024025003003006010004092  label="Válec241"
  Angle = 360
  AttacherType = Attacher::AttachEngine3D
  Height = 10
  Placement = pos=(-9,-80,0) rot=(0,0,1;0rad)
  Radius = 2.2
FEATURE [Part::Cylinder] Cylinder112024025003003006010004093  label="Válec242"
  Angle = 360
  AttacherType = Attacher::AttachEngine3D
  Height = 10
  Placement = pos=(-9,-68,0) rot=(0,0,1;0rad)
  Radius = 2.2
FEATURE [Part::Cylinder] Cylinder112024025003003006010004094  label="Válec243"
  Angle = 360
  AttacherType = Attacher::AttachEngine3D
  Height = 10
  Placement = pos=(9,-68,0) rot=(0,0,1;0rad)
  Radius = 2.2
FEATURE [Part::Box] Box021114  label="Kry003"
  AttacherType = Attacher::AttachEngine3D
  Height = 24
  Length = 42
  Placement = pos=(-21,-93,-19.5) rot=(0,0,1;0rad)
  Width = 75
FEATURE [Part::Cylinder] Cylinder112024025003003006010004095  label="Válec244"
  Angle = 360
  AttacherType = Attacher::AttachEngine3D
  Height = 10
  Placement = pos=(0,-37,0) rot=(0,0,1;0rad)
  Radius = 10
FEATURE [Part::Cylinder] Cylinder112024025003003006010004096  label="Válec245"
  Angle = 360
  AttacherType = Attacher::AttachEngine3D
  Height = 27
  Placement = pos=(0,0,-17) rot=(0,0,1;0rad)
  Radius = 14.7
FEATURE [Part::Box] Box021115  label="Krychle114"
  AttacherType = Attacher::AttachEngine3D
  Height = 10
  Length = 20
  Placement = pos=(-10,-45,0) rot=(0,0,1;0rad)
  Width = 8
FEATURE [Part::Cylinder] Cylinder112024025003003006010004097  label="Válec246"
  Angle = 360
  AttacherType = Attacher::AttachEngine3D
  Height = 10
  Placement = pos=(0,-86,-2) rot=(1,0,0;1.5708rad)
  Radius = 2.2
FEATURE [Part::MultiFuse] Fusion005043005007002053
  Shapes = -> [Cylinder112024025003003006010004096,Cylinder112024025003003006010004090,Cylinder112024025003003006010004095,Box021115,Cylinder112024025003003006010004094,Cylinder112024025003003006010004093,Cylinder112024025003003006010004091,Cylinder112024025003003006010004092,Box021113,Box021112,Box021114,Cylinder112024025003003006010004097]
FEATURE [Part::Cut] Cut018020020009027020002003004004026003  label="R_EAF002"
  Base = -> Fusion005043005007002054
  Tool = -> Fusion005043005007002053
FEATURE [Part::Feature] Cut018020020009027020002003004004026003001  label="R_EAF003"
  shape: bbox 50 x 119 x 24 mm, 83 faces (baked)
FEATURE [Part::Fillet] Fillet027
  Base = -> Cut018020020009027020002003004004026003001
  Edges = 8 edges r=1: [Edge1,Edge2,Edge3,Edge4,Edge56,Edge61,Edge246,Edge249]
FEATURE [App::Part] Part010  label="Refractor V2"
  Group = -> [Cut018020020009027020002003004004026002,Cylinder112024025003003006010004090,Box021110,Box021111,Box021112,Cylinder112024025003003006010004091,Box021113,Cylinder112024025003003006010004093,Cylinder112024025003003006010004094,Box021114,Cylinder112024025003003006010004096,Cylinder112024025003003006010004092,Box021115,Cylinder112024025003003006010004095,Cylinder112024025003003006010004097,+17 more]
  License = CC BY 3.0
  LicenseURL = http://creativecommons.org/licenses/by/3.0/
  Origin = -> Origin010
FEATURE [Part::Cylinder] Cylinder112024025003003006010004098  label="Cy012"
  Angle = 360
  AttacherType = Attacher::AttachEngine3D
  Height = 6
  Radius = 25
FEATURE [Part::Box] Box021116  label="Cub015"
  AttacherType = Attacher::AttachEngine3D
  Height = 17.5
  Length = 50
  Placement = pos=(-25,-85,0) rot=(0,0,1;0rad)
  Width = 85
FEATURE [Part::Feature] Cylinder112024025003003006010004099  label="hole2s003"
  Placement = pos=(0,0,0) rot=(0,0,1;2.0944rad)
  shape: bbox 3.4 x 3.4 x 10 mm, 3 faces (baked)
FEATURE [Part::Feature] Cylinder112024025003003006010004100  label="holeě2i003"
  Placement = pos=(0,0,0) rot=(0,0,1;2.0944rad)
  shape: bbox 6 x 6 x 4 mm, 3 faces (baked)
FEATURE [Part::Feature] Cylinder112024025003003006010004101  label="hole1i003"
  Placement = pos=(0,0,0) rot=(0,0,1;4.18879rad)
  shape: bbox 6 x 6 x 4 mm, 3 faces (baked)
FEATURE [Part::Feature] Cylinder112024025003003006010004102  label="hole1s003"
  Placement = pos=(0,0,0) rot=(0,0,1;4.18879rad)
  shape: bbox 3.4 x 3.4 x 10 mm, 3 faces (baked)
FEATURE [Part::Cylinder] Cylinder112024025003003006010004103  label="hole3i003"
  Angle = 360
  AttacherType = Attacher::AttachEngine3D
  Height = 4
  Placement = pos=(0,16.5,3) rot=(0,0,1;0rad)
  Radius = 3
FEATURE [Part::Box] Box021117  label="Cub016"
  AttacherType = Attacher::AttachEngine3D
  Height = 6
  Length = 50
  Placement = pos=(-25,-85,0) rot=(0,0,1;0rad)
  Width = 85
FEATURE [Part::MultiFuse] Fusion005043005007002055  label="Solid base003"
  Shapes = -> [Box021116,Cylinder112024025003003006010004098,Box021117]
FEATURE [Part::Cylinder] Cylinder112024025003003006010004104  label="hole3s003"
  Angle = 360
  AttacherType = Attacher::AttachEngine3D
  Height = 10
  Placement = pos=(0,16.5,0) rot=(0,0,1;0rad)
  Radius = 1.7
FEATURE [Part::MultiFuse] Fusion005043005007002056  label="Hole for SC screw003"
  Placement = pos=(0,0,0) rot=(0,0,1;3.66519rad)
  Shapes = -> [Cylinder112024025003003006010004101,Cylinder112024025003003006010004102,Cylinder112024025003003006010004100,Cylinder112024025003003006010004099,Cylinder112024025003003006010004104,Cylinder112024025003003006010004103]
FEATURE [Part::Cylinder] Cylinder112024025003003006010004105  label="cy032"
  Angle = 360
  AttacherType = Attacher::AttachEngine3D
  Height = 24
  Placement = pos=(9,-61,12) rot=(0,0,1;0rad)
  Radius = 4
FEATURE [Part::Cylinder] Cylinder112024025003003006010004106  label="cy033"
  Angle = 360
  AttacherType = Attacher::AttachEngine3D
  Height = 24
  Placement = pos=(0,-41.5,6) rot=(0,0,1;0rad)
  Radius = 14
FEATURE [Part::Cylinder] Cylinder112024025003003006010004107  label="cy034"
  Angle = 360
  AttacherType = Attacher::AttachEngine3D
  Height = 15
  Placement = pos=(0,0,6) rot=(0,0,1;0rad)
  Radius = 22
FEATURE [Part::Cylinder] Cylinder112024025003003006010004108  label="cy035"
  Angle = 360
  AttacherType = Attacher::AttachEngine3D
  Height = 24
  Placement = pos=(-9,-61,12) rot=(0,0,1;0rad)
  Radius = 4
FEATURE [Part::Cylinder] Cylinder112024025003003006010004109  label="cy036"
  Angle = 360
  AttacherType = Attacher::AttachEngine3D
  Height = 10
  Radius = 10
FEATURE [Part::Box] Box021120  label="cub018"
  AttacherType = Attacher::AttachEngine3D
  Height = 18
  Length = 28
  Placement = pos=(-14,-41.5,6) rot=(0,0,1;0rad)
  Width = 41.5
FEATURE [Part::Box] Box021122  label="cub019"
  AttacherType = Attacher::AttachEngine3D
  Height = 10
  Length = 8
  Placement = pos=(-13,-78,12) rot=(0,0,1;0rad)
  Width = 17
FEATURE [Part::Cylinder] Cylinder112024025003003006010004111  label="cy038"
  Angle = 360
  AttacherType = Attacher::AttachEngine3D
  Height = 24
  Placement = pos=(9,-78,12) rot=(0,0,1;0rad)
  Radius = 4
FEATURE [Part::Box] Box021123  label="cub020"
  AttacherType = Attacher::AttachEngine3D
  Height = 10
  Length = 8
  Placement = pos=(5,-78,12) rot=(0,0,1;0rad)
  Width = 17
FEATURE [Part::Cylinder] Cylinder112024025003003006010004112  label="cy039"
  Angle = 360
  AttacherType = Attacher::AttachEngine3D
  Height = 24
  Placement = pos=(-9,-78,12) rot=(0,0,1;0rad)
  Radius = 4
FEATURE [Part::Feature] Cylinder112024025003003006010004114  label="hole2s004"
  Placement = pos=(0,0,0) rot=(0,0,1;2.0944rad)
  shape: bbox 3.4 x 3.4 x 10 mm, 3 faces (baked)
FEATURE [Part::Feature] Cylinder112024025003003006010004115  label="hole1i004"
  Placement = pos=(0,0,0) rot=(0,0,1;4.18879rad)
  shape: bbox 6 x 6 x 4 mm, 3 faces (baked)
FEATURE [Part::Feature] Cylinder112024025003003006010004116  label="holeě2i004"
  Placement = pos=(0,0,0) rot=(0,0,1;2.0944rad)
  shape: bbox 6 x 6 x 4 mm, 3 faces (baked)
FEATURE [Part::Feature] Cylinder112024025003003006010004117  label="hole1s004"
  Placement = pos=(0,0,0) rot=(0,0,1;4.18879rad)
  shape: bbox 3.4 x 3.4 x 10 mm, 3 faces (baked)
FEATURE [Part::Cylinder] Cylinder112024025003003006010004118  label="hole3i004"
  Angle = 360
  AttacherType = Attacher::AttachEngine3D
  Height = 4
  Placement = pos=(0,16.5,3) rot=(0,0,1;0rad)
  Radius = 3
FEATURE [Part::Cylinder] Cylinder112024025003003006010004119  label="hole3s004"
  Angle = 360
  AttacherType = Attacher::AttachEngine3D
  Height = 10
  Placement = pos=(0,16.5,0) rot=(0,0,1;0rad)
  Radius = 1.7
FEATURE [Part::MultiFuse] Fusion005043005007002058  label="Hole for SC screw004"
  Placement = pos=(0,0,0) rot=(0,0,1;0.523599rad)
  Shapes = -> [Cylinder112024025003003006010004115,Cylinder112024025003003006010004117,Cylinder112024025003003006010004116,Cylinder112024025003003006010004114,Cylinder112024025003003006010004119,Cylinder112024025003003006010004118]
FEATURE [Part::Box] Box021124  label="ukos"
  AttacherType = Attacher::AttachEngine3D
  Height = 30
  Length = 50
  Placement = pos=(-25,0,6) rot=(1,0,0;0.977384rad)
  Width = 10
FEATURE [Part::Box] Box021125  label="Krychle116"
  AttacherType = Attacher::AttachEngine3D
  Height = 14
  Length = 5
  Placement = pos=(-25,-87,4) rot=(0,0,1;0rad)
  Width = 73
FEATURE [Part::Box] Box021126  label="Krychle117"
  AttacherType = Attacher::AttachEngine3D
  Height = 14
  Length = 5
  Placement = pos=(20,-87,4) rot=(0,0,1;0rad)
  Width = 73
FEATURE [Part::Cylinder] Cylinder112024025003003006010004120  label="Válec247"
  Angle = 360
  AttacherType = Attacher::AttachEngine3D
  Height = 20
  Placement = pos=(-27,-53.5,11) rot=(0,1,0;1.5708rad)
  Radius = 2.2
FEATURE [Part::Box] Box021127  label="Krychle118"
  AttacherType = Attacher::AttachEngine3D
  Height = 10
  Length = 3.5
  Placement = pos=(13.5,-57,11) rot=(0,0,1;0rad)
  Width = 7
FEATURE [Sketcher::SketchObject] Sketch
  MapMode = 5
  Placement = pos=(13.5,-57,11) rot=(0.57735,-0.57735,-0.57735;2.0944rad)
  Support = -> [Box021127]
  sketch-geometry (7):
    g0: LineSegment StartX=-3.5 StartY=4 StartZ=0 EndX=-6.9641 EndY=2 EndZ=0
    g1: LineSegment StartX=-6.9641 StartY=2 StartZ=0 EndX=-6.9641 EndY=-2 EndZ=0
    g2: LineSegment StartX=-6.9641 StartY=-2 StartZ=0 EndX=-3.5 EndY=-4 EndZ=0
    g3: LineSegment StartX=-3.5 StartY=-4 StartZ=0 EndX=-0.0358984 EndY=-2 EndZ=0
    g4: LineSegment StartX=-0.0358984 StartY=-2 StartZ=0 EndX=-0.0358984 EndY=2 EndZ=0
    g5: LineSegment StartX=-0.0358984 StartY=2 StartZ=0 EndX=-3.5 EndY=4 EndZ=0
    g6: Circle [constr] CenterX=-3.5 CenterY=0 CenterZ=0 NormalX=0 NormalY=0 NormalZ=1 AngleXU=0 Radius=4
  constraints (14):
    c: Coincident(g0,g1)
    c: Coincident(g1,g2)
    c: Coincident(g2,g3)
    c: Coincident(g3,g4)
    c: Coincident(g4,g5)
    c: Coincident(g5,g0)
    c: Equal(g0, g1-g5) x5
    c: PointOnObject(g0,g6)
    c: PointOnObject(g1,g6)
    c: PointOnObject(g2,g6)
    c: PointOnObject(g3,g6)
    c: PointOnObject(g4,g6)
    c: PointOnObject(g5,g6)
    c: PointOnObject(g6,g-1)
FEATURE [Part::Extrusion] Extrude
  Base = -> Sketch
  Dir = (-1,0,0)
  DirMode = 2
  FaceMakerClass = Part::FaceMakerBullseye
  LengthFwd = -3.5
  LengthRev = 0
  Solid = true
  Symmetric = false
FEATURE [Part::MultiFuse] Fusion005043005007002059  label="Matice"
  Placement = pos=(0.5,0,0) rot=(0,0,1;0rad)
  Shapes = -> [Box021127,Extrude]
FEATURE [Part::Box] Box021128  label="Krychle119"
  AttacherType = Attacher::AttachEngine3D
  Height = 10
  Length = 3.5
  Placement = pos=(13.5,-57,11) rot=(0,0,1;0rad)
  Width = 7
FEATURE [Sketcher::SketchObject] Sketch001
  MapMode = 5
  Placement = pos=(13.5,-57,11) rot=(0.57735,-0.57735,-0.57735;2.0944rad)
  Support = -> [Box021128]
  sketch-geometry (7):
    g0: LineSegment StartX=-3.5 StartY=4 StartZ=0 EndX=-6.9641 EndY=2 EndZ=0
    g1: LineSegment StartX=-6.9641 StartY=2 StartZ=0 EndX=-6.9641 EndY=-2 EndZ=0
    g2: LineSegment StartX=-6.9641 StartY=-2 StartZ=0 EndX=-3.5 EndY=-4 EndZ=0
    g3: LineSegment StartX=-3.5 StartY=-4 StartZ=0 EndX=-0.0358984 EndY=-2 EndZ=0
    g4: LineSegment StartX=-0.0358984 StartY=-2 StartZ=0 EndX=-0.0358984 EndY=2 EndZ=0
    g5: LineSegment StartX=-0.0358984 StartY=2 StartZ=0 EndX=-3.5 EndY=4 EndZ=0
    g6: Circle [constr] CenterX=-3.5 CenterY=0 CenterZ=0 NormalX=0 NormalY=0 NormalZ=1 AngleXU=0 Radius=4
  constraints (14):
    c: Coincident(g0,g1)
    c: Coincident(g1,g2)
    c: Coincident(g2,g3)
    c: Coincident(g3,g4)
    c: Coincident(g4,g5)
    c: Coincident(g5,g0)
    c: Equal(g0, g1-g5) x5
    c: PointOnObject(g0,g6)
    c: PointOnObject(g1,g6)
    c: PointOnObject(g2,g6)
    c: PointOnObject(g3,g6)
    c: PointOnObject(g4,g6)
    c: PointOnObject(g5,g6)
    c: PointOnObject(g6,g-1)
FEATURE [Part::Extrusion] Extrude001
  Base = -> Sketch001
  Dir = (-1,0,0)
  DirMode = 2
  FaceMakerClass = Part::FaceMakerBullseye
  LengthFwd = -3.5
  LengthRev = 0
  Solid = true
  Symmetric = false
FEATURE [Part::MultiFuse] Fusion005043005007002060  label="Matice001"
  Placement = pos=(-31,0,0) rot=(0,0,1;0rad)
  Shapes = -> [Box021128,Extrude001]
FEATURE [Part::Cylinder] Cylinder112024025003003006010004121  label="Válec248"
  Angle = 360
  AttacherType = Attacher::AttachEngine3D
  Height = 20
  Placement = pos=(7,-53.5,11) rot=(0,1,0;1.5708rad)
  Radius = 2.2
FEATURE [Part::MultiFuse] Fusion005043005007002061  label="matice dir"
  Placement = pos=(0,0,-0.5) rot=(0,0,1;0rad)
  Shapes = -> [Cylinder112024025003003006010004120,Fusion005043005007002059,Fusion005043005007002060,Cylinder112024025003003006010004121]
FEATURE [Part::MultiFuse] Fusion005043005007002057  label="Holes003"
  Shapes = -> [Cylinder112024025003003006010004106,Cylinder112024025003003006010004105,Cylinder112024025003003006010004108,Cylinder112024025003003006010004111,Cylinder112024025003003006010004112,Box021122,Box021123,Cylinder112024025003003006010004109,Box021120,Cylinder112024025003003006010004107,Fusion005043005007002056,Fusion005043005007002058,Box021124,Box021125,Box021126,Fusion005043005007002061]
FEATURE [Part::Cut] Cut018020020009027020002003004004026003002  label="SCT-base003"
  Base = -> Fusion005043005007002055
  Tool = -> Fusion005043005007002057
FEATURE [Part::Fillet] Fillet028  label="SCT-baseV4"
  Base = -> Cut018020020009027020002003004004026003002
  Edges = 5 edges r=1: [Edge1,Edge8,Edge30,Edge35,Edge37]
FEATURE [Part::Box] Box021129  label="Krychle120"
  AttacherType = Attacher::AttachEngine3D
  Height = 42.5
  Length = 50
  Placement = pos=(-25,-84,6) rot=(0,0,1;0rad)
  Width = 58
FEATURE [Part::Box] Box021130  label="Krychle121"
  AttacherType = Attacher::AttachEngine3D
  Height = 12.5
  Length = 42
  Placement = pos=(-21,-84,5.5) rot=(0,0,1;0rad)
  Width = 58
FEATURE [Part::Box] Box021131  label="Krychle122"
  AttacherType = Attacher::AttachEngine3D
  Height = 26
  Length = 42
  Placement = pos=(-21,-77.5,22.5) rot=(0,0,1;0rad)
  Width = 58
FEATURE [Part::Box] Box021132  label="Krychle123"
  AttacherType = Attacher::AttachEngine3D
  Height = 10
  Length = 53
  Placement = pos=(-26.5,-64,6.5) rot=(0,0,1;0rad)
  Width = 18
FEATURE [Part::Cylinder] Cylinder112024025003003006010004122  label="Válec249"
  Angle = 360
  AttacherType = Attacher::AttachEngine3D
  Height = 53
  Placement = pos=(-26.5,-46,11.5) rot=(0,1,0;1.5708rad)
  Radius = 5
FEATURE [Part::Cylinder] Cylinder112024025003003006010004123  label="Válec250"
  Angle = 360
  AttacherType = Attacher::AttachEngine3D
  Height = 53
  Placement = pos=(-26.5,-64,11.5) rot=(0,1,0;1.5708rad)
  Radius = 5
FEATURE [Part::MultiFuse] Fusion005043005007002062  label="Motor M1"
  Shapes = -> [Cylinder112024025003003006010004123,Cylinder112024025003003006010004122,Box021132,Box021129]
FEATURE [Part::Box] Box021133  label="Krychle124"
  AttacherType = Attacher::AttachEngine3D
  Height = 19.5
  Length = 50
  Placement = pos=(-25,-77.5,29.5) rot=(0,0,1;0rad)
  Width = 58
FEATURE [Part::Cylinder] Cylinder112024025003003006010004128  label="cy043"
  Angle = 360
  AttacherType = Attacher::AttachEngine3D
  Height = 24
  Placement = pos=(0,-39,0) rot=(0,0,1;0rad)
  Radius = 12
FEATURE [Part::Cylinder] Cylinder112024025003003006010004129  label="cy044"
  Angle = 360
  AttacherType = Attacher::AttachEngine3D
  Height = 24
  Placement = pos=(-9,-72.5,0) rot=(0,0,1;0rad)
  Radius = 2.2
FEATURE [Part::Cylinder] Cylinder112024025003003006010004130  label="cy045"
  Angle = 360
  AttacherType = Attacher::AttachEngine3D
  Height = 24
  Placement = pos=(9,-72.5,0) rot=(0,0,1;0rad)
  Radius = 2.2
FEATURE [Part::Cylinder] Cylinder112024025003003006010004131  label="Válec251"
  Angle = 360
  AttacherType = Attacher::AttachEngine3D
  Height = 53
  Placement = pos=(-26.5,-64,11.5) rot=(0,1,0;1.5708rad)
  Radius = 2.3
FEATURE [Part::Cylinder] Cylinder112024025003003006010004132  label="Válec252"
  Angle = 360
  AttacherType = Attacher::AttachEngine3D
  Height = 53
  Placement = pos=(-26.5,-46,11.5) rot=(0,1,0;1.5708rad)
  Radius = 2.3
FEATURE [Part::Box] Box021137  label="Krychle128"
  AttacherType = Attacher::AttachEngine3D
  Height = 4.6
  Length = 53
  Placement = pos=(-26.5,-64,9.2) rot=(0,0,1;0rad)
  Width = 18
FEATURE [Part::Box] Box021138  label="Krychle129"
  AttacherType = Attacher::AttachEngine3D
  Height = 19
  Length = 4
  Placement = pos=(21,-84,29.5) rot=(0,0,1;0rad)
  Width = 6.5
FEATURE [Part::Box] Box021139  label="Krychle130"
  AttacherType = Attacher::AttachEngine3D
  Height = 19
  Length = 4
  Placement = pos=(-25,-84,29.5) rot=(0,0,1;0rad)
  Width = 6.5
FEATURE [Part::MultiFuse] Fusion005043005007002063  label="Motor vyrezy"
  Shapes = -> [Box021130,Box021131,Box021133,Cylinder112024025003003006010004129,Cylinder112024025003003006010004130,Cylinder112024025003003006010004128,Cylinder112024025003003006010004131,Cylinder112024025003003006010004132,Box021137,Box021138,Box021139]
FEATURE [Part::Cut] Cut018020020009027020002003004004026003003  label="EAF Motor"
  Base = -> Fusion005043005007002062
  Tool = -> Fusion005043005007002063
FEATURE [Part::Fillet] Fillet030  label="EAF-Motor V4"
  Base = -> Cut018020020009027020002003004004026003003
  Edges = 20 edges: [Edge4 r=1,Edge7 r=1,Edge8 r=1,Edge9 r=2,Edge10 r=2,Edge16 r=1,Edge20 r=1,Edge24 r=2,Edge28 r=2,Edge31 r=2,Edge34 r=1,Edge39 r=2,Edge43 r=2,Edge77 r=2,Edge79 r=2,Edge85 r=2,Edge117 r=1,Edge120 r=1,Edge123 r=1,Edge124 r=1]
FEATURE [Part::Part2DObjectPython] ShapeString  # Draft 2D object (typed FeaturePython)
  FontFile = <path>
  Placement = pos=(-13.13,-84,29.82) rot=(1,0,0;1.5708rad)
  Size = 10
  String = EAF
  Tracking = 0
FEATURE [Part::Extrusion] Extrude002
  Base = -> ShapeString
  Dir = (0,-1,0)
  DirMode = 2
  FaceMakerClass = Part::FaceMakerBullseye
  LengthFwd = -0.75
  LengthRev = 0
  Solid = false
  Symmetric = false
FEATURE [Part::Cut] Cut018020020009027020002003004004026003005  label="EAF-motor-V4"
  Base = -> Fillet030
  Tool = -> Extrude002
FEATURE [Part::Feature] Cut018020020009027020002003004004026003005001  label="EAF-motor-V005"
  shape: bbox 53 x 58 x 42.5 mm, 103 faces (baked)
FEATURE [Part::Feature] Cut018020020009027020002003004004026003005002  label="EAF-motor-V006"
  Placement = pos=(0,0,25.5) rot=(0,1,0;3.14159rad)
  shape: bbox 53 x 58 x 42.5 mm, 103 faces (baked)
FEATURE [Part::Box] Box021145  label="Krychle135"
  AttacherType = Attacher::AttachEngine3D
  Height = 13
  Length = 50
  Placement = pos=(-25,-96,7) rot=(0,0,1;0rad)
  Width = 116
FEATURE [Part::Cylinder] Cylinder016  label="TubusTelescop"
  Angle = 360
  AttacherType = Attacher::AttachEngine3D
  Height = 250
  Placement = pos=(-103,29,-200) rot=(0,0,1;0rad)
  Radius = 90
FEATURE [Part::Cylinder] Cylinder112024025003003006010004141  label="Velky"
  Angle = 360
  AttacherType = Attacher::AttachEngine3D
  Height = 53
  Placement = pos=(-25,29,-40.5) rot=(0,1,0;1.5708rad)
  Radius = 39
FEATURE [Part::Box] Box021146  label="Krychle136"
  AttacherType = Attacher::AttachEngine3D
  Height = 50
  Length = 29
  Placement = pos=(-14.5,-14,-65) rot=(0,0,1;0rad)
  Width = 16
FEATURE [Part::Cylinder] Cylinder112024025003003006010004142  label="Válec261"
  Angle = 360
  AttacherType = Attacher::AttachEngine3D
  Height = 16
  Placement = pos=(0,0,-15) rot=(0,0,1;0rad)
  Radius = 9
FEATURE [Part::Cylinder] Cylinder112024025003003006010004143  label="Válec262"
  Angle = 360
  AttacherType = Attacher::AttachEngine3D
  Height = 16
  Placement = pos=(0,0,-15) rot=(0,0,1;0rad)
  Radius = 14
FEATURE [Part::MultiFuse] Fusion005043005007002069  label="Tělo"
  Shapes = -> [Box021146,Cylinder112024025003003006010004141,Cylinder112024025003003006010004143]
FEATURE [Part::Cylinder] Cylinder112024025003003006010004144  label="Válec263"
  Angle = 360
  AttacherType = Attacher::AttachEngine3D
  Height = 10
  Placement = pos=(0,-6,-8) rot=(1,0,0;1.5708rad)
  Radius = 1.6
FEATURE [Part::MultiFuse] Fusion005043005007002068  label="Diry v telo"
  Shapes = -> [Cylinder112024025003003006010004144,Cylinder112024025003003006010004142]
FEATURE [Part::Cut] Cut018020020009027020002003004004026003005005  label="Body001"
  Base = -> Fusion005043005007002069
  Tool = -> Fusion005043005007002068
FEATURE [Part::Box] Box021147  label="Krychle137"
  AttacherType = Attacher::AttachEngine3D
  Height = 23
  Length = 50
  Placement = pos=(-25,-25,-16) rot=(0.995037,0,0.099504;0rad)
  Width = 45
FEATURE [Part::MultiFuse] Fusion005043005007002070  label="Main"
  Shapes = -> [Box021147,Box021145]
FEATURE [Part::Fillet] Fillet028002
  Base = -> Fusion005043005007002070
  Edges = 4 edges r=20: [Edge3,Edge10,Edge13,Edge23]
FEATURE [Part::Cylinder] Cylinder112024025003003006010004145  label="Válec264"
  Angle = 360
  AttacherType = Attacher::AttachEngine3D
  Height = 41
  Placement = pos=(0,0,-17) rot=(0,0,1;0rad)
  Radius = 14.7
FEATURE [Part::Box] Box021148  label="Krychle138"
  AttacherType = Attacher::AttachEngine3D
  Height = 50
  Length = 29
  Placement = pos=(-14.5,-14,-65) rot=(0,0,1;0rad)
  Width = 16
FEATURE [Part::Cylinder] Cylinder112024025003003006010004146  label="Velky001"
  Angle = 360
  AttacherType = Attacher::AttachEngine3D
  Height = 53
  Placement = pos=(-25,29,-40.5) rot=(0,1,0;1.5708rad)
  Radius = 39
FEATURE [Part::Cylinder] Cylinder112024025003003006010004147  label="Válec265"
  Angle = 360
  AttacherType = Attacher::AttachEngine3D
  Height = 16
  Placement = pos=(0,0,-15) rot=(0,0,1;0rad)
  Radius = 14
FEATURE [Part::MultiFuse] Fusion005043005007002072  label="Tělo001"
  Shapes = -> [Box021148,Cylinder112024025003003006010004146,Cylinder112024025003003006010004147]
FEATURE [Part::Cylinder] Cylinder112024025003003006010004148  label="Válec266"
  Angle = 360
  AttacherType = Attacher::AttachEngine3D
  Height = 10
  Placement = pos=(0,-6,-8) rot=(1,0,0;1.5708rad)
  Radius = 1.6
FEATURE [Part::Cylinder] Cylinder112024025003003006010004149  label="Válec267"
  Angle = 360
  AttacherType = Attacher::AttachEngine3D
  Height = 16
  Placement = pos=(0,0,-15) rot=(0,0,1;0rad)
  Radius = 9
FEATURE [Part::MultiFuse] Fusion005043005007002071  label="Diry v telo001"
  Shapes = -> [Cylinder112024025003003006010004148,Cylinder112024025003003006010004149]
FEATURE [Part::Cut] Cut018020020009027020002003004004026003005006  label="Body002"
  Base = -> Fusion005043005007002072
  Tool = -> Fusion005043005007002071
FEATURE [Part::Cylinder] Cylinder112024025003003006010004150  label="TubusTelescop001"
  Angle = 360
  AttacherType = Attacher::AttachEngine3D
  Height = 250
  Placement = pos=(-104.5,29,-200) rot=(0,0,1;0rad)
  Radius = 90.5
FEATURE [Part::Box] Box021149  label="Krychle139"
  AttacherType = Attacher::AttachEngine3D
  Height = 16
  Length = 30
  Placement = pos=(-15,-25,-32) rot=(0,0,1;0rad)
  Width = 10
FEATURE [Part::Cylinder] Cylinder112024025003003006010004151  label="Válec268"
  Angle = 360
  AttacherType = Attacher::AttachEngine3D
  Height = 10
  Placement = pos=(-11,-15,-27) rot=(1,0,0;1.5708rad)
  Radius = 1.7
FEATURE [Part::MultiFuse] Fusion005043005007002074  label="Body003"
  Shapes = -> [Box021149,Fillet028002]
FEATURE [Part::Cylinder] Cylinder112024025003003006010004152  label="Válec269"
  Angle = 360
  AttacherType = Attacher::AttachEngine3D
  Height = 10
  Placement = pos=(11,-15,-27) rot=(1,0,0;1.5708rad)
  Radius = 1.7
FEATURE [Part::Cylinder] Cylinder112024025003003006010004153  label="Válec270"
  Angle = 360
  AttacherType = Attacher::AttachEngine3D
  Height = 5
  Placement = pos=(11,-20,-27) rot=(1,0,0;1.5708rad)
  Radius = 3
FEATURE [Part::Cylinder] Cylinder112024025003003006010004154  label="Válec271"
  Angle = 360
  AttacherType = Attacher::AttachEngine3D
  Height = 5
  Placement = pos=(-11,-20,-27) rot=(1,0,0;1.5708rad)
  Radius = 3
FEATURE [Part::MultiFuse] Fusion005043005007002075  label="Inbus"
  Shapes = -> [Cylinder112024025003003006010004151,Cylinder112024025003003006010004152,Cylinder112024025003003006010004153,Cylinder112024025003003006010004154]
FEATURE [Part::Box] Box021150  label="Krychle140"
  AttacherType = Attacher::AttachEngine3D
  Height = 13
  Length = 4.5
  Placement = pos=(-25,-102,7) rot=(0,0,1;0rad)
  Width = 77
FEATURE [Part::Box] Box021151  label="Krychle141"
  AttacherType = Attacher::AttachEngine3D
  Height = 13
  Length = 4.5
  Placement = pos=(20.5,-102,7) rot=(0,0,1;0rad)
  Width = 77
FEATURE [Part::Cylinder] Cylinder112024025003003006010004155  label="sroub"
  Angle = 360
  AttacherType = Attacher::AttachEngine3D
  Height = 60
  Placement = pos=(-30,-64,14) rot=(0,1,0;1.5708rad)
  Radius = 2.2
FEATURE [Part::Cylinder] Cylinder112024025003003006010004156  label="Válec273"
  Angle = 360
  AttacherType = Attacher::AttachEngine3D
  Height = 13
  Placement = pos=(0,-57.5,7) rot=(0,0,1;0rad)
  Radius = 12
FEATURE [Part::Box] Box021152  label="Krychle142"
  AttacherType = Attacher::AttachEngine3D
  Height = 13
  Length = 24
  Placement = pos=(-12,-57.5,7) rot=(0,0,1;0rad)
  Width = 49
FEATURE [Part::Cylinder] Cylinder112024025003003006010004157  label="Válec274"
  Angle = 360
  AttacherType = Attacher::AttachEngine3D
  Height = 5
  Placement = pos=(-9,-90.5,7) rot=(0,0,1;0rad)
  Radius = 3.7
FEATURE [Part::Cylinder] Cylinder112024025003003006010004158  label="Válec275"
  Angle = 360
  AttacherType = Attacher::AttachEngine3D
  Height = 5
  Placement = pos=(9,-90.5,7) rot=(0,0,1;0rad)
  Radius = 3.7
FEATURE [Part::Cylinder] Cylinder112024025003003006010004159  label="Válec276"
  Angle = 360
  AttacherType = Attacher::AttachEngine3D
  Height = 5
  Placement = pos=(-9,-72.5,7) rot=(0,0,1;0rad)
  Radius = 3.7
FEATURE [Part::Cylinder] Cylinder112024025003003006010004160  label="Válec277"
  Angle = 360
  AttacherType = Attacher::AttachEngine3D
  Height = 5
  Placement = pos=(9,-72.5,7) rot=(0,0,1;0rad)
  Radius = 3.7
FEATURE [Part::Box] Box021153  label="Krychle143"
  AttacherType = Attacher::AttachEngine3D
  Height = 5
  Length = 7.4
  Placement = pos=(5.3,-90.5,7) rot=(0,0,1;0rad)
  Width = 18
FEATURE [Part::Box] Box021154  label="Krychle144"
  AttacherType = Attacher::AttachEngine3D
  Height = 5
  Length = 7.4
  Placement = pos=(-12.7,-90.5,7) rot=(0,0,1;0rad)
  Width = 18
FEATURE [Part::Cylinder] Cylinder112024025003003006010004161  label="Válec278"
  Angle = 360
  AttacherType = Attacher::AttachEngine3D
  Height = 10
  Placement = pos=(0,-15,-32) rot=(1,0,0;1.5708rad)
  Radius = 4
FEATURE [Part::Cylinder] Cylinder112024025003003006010004162  label="Válec279"
  Angle = 360
  AttacherType = Attacher::AttachEngine3D
  Height = 14
  Placement = pos=(0,0,6) rot=(0,0,1;0rad)
  Radius = 16.25
FEATURE [Part::Box] Box021155  label="Krychle145"
  AttacherType = Attacher::AttachEngine3D
  Height = 10
  Length = 3.5
  Placement = pos=(13.5,-58,0) rot=(0,0,1;0rad)
  Width = 7
FEATURE [Sketcher::SketchObject] Sketch002
  MapMode = 5
  Placement = pos=(13.5,-58,0) rot=(0.57735,-0.57735,-0.57735;2.0944rad)
  Support = -> [Box021155]
  sketch-geometry (7):
    g0: LineSegment StartX=-3.5 StartY=4 StartZ=0 EndX=-6.9641 EndY=2 EndZ=0
    g1: LineSegment StartX=-6.9641 StartY=2 StartZ=0 EndX=-6.9641 EndY=-2 EndZ=0
    g2: LineSegment StartX=-6.9641 StartY=-2 StartZ=0 EndX=-3.5 EndY=-4 EndZ=0
    g3: LineSegment StartX=-3.5 StartY=-4 StartZ=0 EndX=-0.0358984 EndY=-2 EndZ=0
    g4: LineSegment StartX=-0.0358984 StartY=-2 StartZ=0 EndX=-0.0358984 EndY=2 EndZ=0
    g5: LineSegment StartX=-0.0358984 StartY=2 StartZ=0 EndX=-3.5 EndY=4 EndZ=0
    g6: Circle [constr] CenterX=-3.5 CenterY=0 CenterZ=0 NormalX=0 NormalY=0 NormalZ=1 AngleXU=0 Radius=4
  constraints (14):
    c: Coincident(g0,g1)
    c: Coincident(g1,g2)
    c: Coincident(g2,g3)
    c: Coincident(g3,g4)
    c: Coincident(g4,g5)
    c: Coincident(g5,g0)
    c: Equal(g0, g1-g5) x5
    c: PointOnObject(g0,g6)
    c: PointOnObject(g1,g6)
    c: PointOnObject(g2,g6)
    c: PointOnObject(g3,g6)
    c: PointOnObject(g4,g6)
    c: PointOnObject(g5,g6)
    c: PointOnObject(g6,g-1)
FEATURE [Part::Extrusion] Extrude003
  Base = -> Sketch002
  Dir = (-1,0,0)
  DirMode = 2
  FaceMakerClass = Part::FaceMakerBullseye
  LengthFwd = -3.5
  LengthRev = 0
  Solid = true
  Symmetric = false
FEATURE [Part::MultiFuse] Fusion005043005007002078004  label="Matice002"
  Placement = pos=(1,-118.5,14) rot=(1,0,0;3.14159rad)
  Shapes = -> [Box021155,Extrude003]
FEATURE [Part::Box] Box021156  label="Krychle146"
  AttacherType = Attacher::AttachEngine3D
  Height = 10
  Length = 3.5
  Placement = pos=(13.5,-58,0) rot=(0,0,1;0rad)
  Width = 7
FEATURE [Sketcher::SketchObject] Sketch003
  MapMode = 5
  Placement = pos=(13.5,-58,0) rot=(0.57735,-0.57735,-0.57735;2.0944rad)
  Support = -> [Box021156]
  sketch-geometry (7):
    g0: LineSegment StartX=-3.5 StartY=4 StartZ=0 EndX=-6.9641 EndY=2 EndZ=0
    g1: LineSegment StartX=-6.9641 StartY=2 StartZ=0 EndX=-6.9641 EndY=-2 EndZ=0
    g2: LineSegment StartX=-6.9641 StartY=-2 StartZ=0 EndX=-3.5 EndY=-4 EndZ=0
    g3: LineSegment StartX=-3.5 StartY=-4 StartZ=0 EndX=-0.0358984 EndY=-2 EndZ=0
    g4: LineSegment StartX=-0.0358984 StartY=-2 StartZ=0 EndX=-0.0358984 EndY=2 EndZ=0
    g5: LineSegment StartX=-0.0358984 StartY=2 StartZ=0 EndX=-3.5 EndY=4 EndZ=0
    g6: Circle [constr] CenterX=-3.5 CenterY=0 CenterZ=0 NormalX=0 NormalY=0 NormalZ=1 AngleXU=0 Radius=4
  constraints (14):
    c: Coincident(g0,g1)
    c: Coincident(g1,g2)
    c: Coincident(g2,g3)
    c: Coincident(g3,g4)
    c: Coincident(g4,g5)
    c: Coincident(g5,g0)
    c: Equal(g0, g1-g5) x5
    c: PointOnObject(g0,g6)
    c: PointOnObject(g1,g6)
    c: PointOnObject(g2,g6)
    c: PointOnObject(g3,g6)
    c: PointOnObject(g4,g6)
    c: PointOnObject(g5,g6)
    c: PointOnObject(g6,g-1)
FEATURE [Part::Extrusion] Extrude004
  Base = -> Sketch003
  Dir = (-1,0,0)
  DirMode = 2
  FaceMakerClass = Part::FaceMakerBullseye
  LengthFwd = -3.5
  LengthRev = 0
  Solid = true
  Symmetric = false
FEATURE [Part::MultiFuse] Fusion005043005007002078005  label="Matice003"
  Placement = pos=(-31.5,-118.5,14) rot=(1,0,0;3.14159rad)
  Shapes = -> [Box021156,Extrude004]
FEATURE [Part::Box] Box021157  label="Krychle147"
  AttacherType = Attacher::AttachEngine3D
  Height = 10
  Length = 3.5
  Placement = pos=(13.5,-58,0) rot=(0,0,1;0rad)
  Width = 7
FEATURE [Sketcher::SketchObject] Sketch004
  MapMode = 5
  Placement = pos=(13.5,-58,0) rot=(0.57735,-0.57735,-0.57735;2.0944rad)
  Support = -> [Box021157]
  sketch-geometry (7):
    g0: LineSegment StartX=-3.5 StartY=4 StartZ=0 EndX=-6.9641 EndY=2 EndZ=0
    g1: LineSegment StartX=-6.9641 StartY=2 StartZ=0 EndX=-6.9641 EndY=-2 EndZ=0
    g2: LineSegment StartX=-6.9641 StartY=-2 StartZ=0 EndX=-3.5 EndY=-4 EndZ=0
    g3: LineSegment StartX=-3.5 StartY=-4 StartZ=0 EndX=-0.0358984 EndY=-2 EndZ=0
    g4: LineSegment StartX=-0.0358984 StartY=-2 StartZ=0 EndX=-0.0358984 EndY=2 EndZ=0
    g5: LineSegment StartX=-0.0358984 StartY=2 StartZ=0 EndX=-3.5 EndY=4 EndZ=0
    g6: Circle [constr] CenterX=-3.5 CenterY=0 CenterZ=0 NormalX=0 NormalY=0 NormalZ=1 AngleXU=0 Radius=4
  constraints (14):
    c: Coincident(g0,g1)
    c: Coincident(g1,g2)
    c: Coincident(g2,g3)
    c: Coincident(g3,g4)
    c: Coincident(g4,g5)
    c: Coincident(g5,g0)
    c: Equal(g0, g1-g5) x5
    c: PointOnObject(g0,g6)
    c: PointOnObject(g1,g6)
    c: PointOnObject(g2,g6)
    c: PointOnObject(g3,g6)
    c: PointOnObject(g4,g6)
    c: PointOnObject(g5,g6)
    c: PointOnObject(g6,g-1)
FEATURE [Part::Extrusion] Extrude005
  Base = -> Sketch004
  Dir = (-1,0,0)
  DirMode = 2
  FaceMakerClass = Part::FaceMakerBullseye
  LengthFwd = -3.5
  LengthRev = 0
  Solid = true
  Symmetric = false
FEATURE [Part::MultiFuse] Fusion005043005007002078006  label="Matice004"
  Placement = pos=(3,-27.5,-52) rot=(1,0,0;4.18879rad)
  Shapes = -> [Box021157,Extrude005]
FEATURE [Part::Cylinder] Cylinder112024025003003006010004163  label="Válec280"
  Angle = 360
  AttacherType = Attacher::AttachEngine3D
  Height = 15
  Placement = pos=(13,0,-5) rot=(0,1,0;1.5708rad)
  Radius = 2.2
FEATURE [Part::MultiFuse] Fusion005043005007002073  label="Holes004"
  Shapes = -> [Cylinder112024025003003006010004145,Cylinder112024025003003006010004150,Cut018020020009027020002003004004026003005006,Fusion005043005007002075,Box021150,Box021151,Cylinder112024025003003006010004155,Cylinder112024025003003006010004156,Box021152,Box021154,Box021153,Cylinder112024025003003006010004160,Cylinder112024025003003006010004158,Cylinder112024025003003006010004159,+7 more]
FEATURE [Part::Cut] Cut018020020009027020002003004004026003005007  label="BODY"
  Base = -> Fusion005043005007002074
  Tool = -> Fusion005043005007002073
FEATURE [Part::Feature] Cut018020020009027020002003004004026003005007001  label="BODY001"
  shape: bbox 50 x 116 x 52 mm, 85 faces (baked)
FEATURE [Part::Box] Box021158  label="Krychle148"
  AttacherType = Attacher::AttachEngine3D
  Height = 12.5
  Length = 42
  Placement = pos=(-21,-95,5.5) rot=(0,0,1;0rad)
  Width = 69
FEATURE [Part::Box] Box021159  label="Krychle149"
  AttacherType = Attacher::AttachEngine3D
  Height = 26
  Length = 42
  Placement = pos=(-21,-69.5,30.5) rot=(0,0,1;0rad)
  Width = 58
FEATURE [Part::Box] Box021160  label="Krychle150"
  AttacherType = Attacher::AttachEngine3D
  Height = 10
  Length = 53
  Placement = pos=(-26.5,-64,6.5) rot=(0,0,1;0rad)
  Width = 18
FEATURE [Part::Cylinder] Cylinder112024025003003006010004164  label="Válec281"
  Angle = 360
  AttacherType = Attacher::AttachEngine3D
  Height = 53
  Placement = pos=(-26.5,-46,11.5) rot=(0,1,0;1.5708rad)
  Radius = 5
FEATURE [Part::Cylinder] Cylinder112024025003003006010004165  label="Válec282"
  Angle = 360
  AttacherType = Attacher::AttachEngine3D
  Height = 53
  Placement = pos=(-26.5,-64,11.5) rot=(0,1,0;1.5708rad)
  Radius = 5
FEATURE [Part::Box] Box021161  label="Krychle151"
  AttacherType = Attacher::AttachEngine3D
  Height = 42.5
  Length = 50
  Placement = pos=(-25,-95,6) rot=(0,0,1;0rad)
  Width = 69
FEATURE [Part::Box] Box021162  label="Krychle152"
  AttacherType = Attacher::AttachEngine3D
  Height = 19.5
  Length = 50
  Placement = pos=(-25,-69.5,30.5) rot=(0,0,1;0rad)
  Width = 58
FEATURE [Part::Cylinder] Cylinder112024025003003006010004166  label="cy046"
  Angle = 360
  AttacherType = Attacher::AttachEngine3D
  Height = 32
  Placement = pos=(0,-47.5,0) rot=(0,0,1;0rad)
  Radius = 12
FEATURE [Part::Cylinder] Cylinder112024025003003006010004167  label="cy047"
  Angle = 360
  AttacherType = Attacher::AttachEngine3D
  Height = 20
  Placement = pos=(-15.5,-62.5,15) rot=(0,0,1;0rad)
  Radius = 1.7
FEATURE [Part::Cylinder] Cylinder112024025003003006010004168  label="cy048"
  Angle = 360
  AttacherType = Attacher::AttachEngine3D
  Height = 20
  Placement = pos=(15.5,-62.5,15) rot=(0,0,1;0rad)
  Radius = 1.7
FEATURE [Part::Cylinder] Cylinder112024025003003006010004169  label="Válec283"
  Angle = 360
  AttacherType = Attacher::AttachEngine3D
  Height = 53
  Placement = pos=(-26.5,-64,11.5) rot=(0,1,0;1.5708rad)
  Radius = 2.3
FEATURE [Part::Cylinder] Cylinder112024025003003006010004170  label="Válec284"
  Angle = 360
  AttacherType = Attacher::AttachEngine3D
  Height = 53
  Placement = pos=(-26.5,-46,11.5) rot=(0,1,0;1.5708rad)
  Radius = 2.3
FEATURE [Part::Box] Box021163  label="Krychle153"
  AttacherType = Attacher::AttachEngine3D
  Height = 4.6
  Length = 53
  Placement = pos=(-26.5,-64,9.2) rot=(0,0,1;0rad)
  Width = 18
FEATURE [Part::Box] Box021164  label="Krychle154"
  AttacherType = Attacher::AttachEngine3D
  Height = 19
  Length = 4
  Placement = pos=(21,-84,29.5) rot=(0,0,1;0rad)
  Width = 6.5
FEATURE [Part::Box] Box021165  label="Krychle155"
  AttacherType = Attacher::AttachEngine3D
  Height = 19
  Length = 4
  Placement = pos=(-25,-84,29.5) rot=(0,0,1;0rad)
  Width = 6.5
FEATURE [Part::Part2DObjectPython] ShapeString001  # Draft 2D object (typed FeaturePython)
  FontFile = <path>
  Placement = pos=(-13.13,-84,29.82) rot=(1,0,0;1.5708rad)
  Size = 5
  String = OnStep Fokus
  Tracking = 0
FEATURE [Part::Extrusion] Extrude006  label="Test"
  Base = -> ShapeString001
  Dir = (0,-1,2e-16)
  DirMode = 2
  FaceMakerClass = Part::FaceMakerBullseye
  LengthFwd = -0.75
  LengthRev = 0
  Placement = pos=(-9,-11,-10.5) rot=(0,0,1;0rad)
  Solid = false
  Symmetric = false
FEATURE [Part::MultiFuse] Fusion005043005007002078007  label="Motor M002"
  Shapes = -> [Cylinder112024025003003006010004165,Cylinder112024025003003006010004164,Box021160,Box021161]
FEATURE [Part::Feature] Fusion001001  label="Nema17"
  Placement = pos=(0,0,0) rot=(0,0,1;1.5708rad)
  shape: bbox 42.3 x 48 x 46.35 mm, 98 faces (baked)
FEATURE [App::Part] Part014  label="Nema 17"
  Group = -> [Fusion001001]
  License = CC BY 3.0
  LicenseURL = http://creativecommons.org/licenses/by/3.0/
  Origin = -> Origin014
  Placement = pos=(0,-47.5,57) rot=(1,0,0;3.14159rad)
FEATURE [Part::Cylinder] Cylinder112024025003003006010004171  label="cy049"
  Angle = 360
  AttacherType = Attacher::AttachEngine3D
  Height = 20
  Placement = pos=(-15.5,-31.5,15) rot=(0,0,1;0rad)
  Radius = 1.7
FEATURE [Part::Cylinder] Cylinder112024025003003006010004172  label="cy050"
  Angle = 360
  AttacherType = Attacher::AttachEngine3D
  Height = 20
  Placement = pos=(15.5,-31.5,15) rot=(0,0,1;0rad)
  Radius = 1.7
FEATURE [Part::Cylinder] Cylinder112024025003003006010004173  label="cy051"
  Angle = 360
  AttacherType = Attacher::AttachEngine3D
  Height = 5
  Placement = pos=(-15.5,-31.5,18) rot=(0,0,1;0rad)
  Radius = 3
FEATURE [Part::Cylinder] Cylinder112024025003003006010004174  label="cy052"
  Angle = 360
  AttacherType = Attacher::AttachEngine3D
  Height = 4
  Placement = pos=(15.5,-31.5,18) rot=(0,0,1;0rad)
  Radius = 3
FEATURE [Part::Cylinder] Cylinder112024025003003006010004175  label="cy053"
  Angle = 360
  AttacherType = Attacher::AttachEngine3D
  Height = 4
  Placement = pos=(-15.5,-62.5,18) rot=(0,0,1;0rad)
  Radius = 3
FEATURE [Part::Cylinder] Cylinder112024025003003006010004176  label="cy054"
  Angle = 360
  AttacherType = Attacher::AttachEngine3D
  Height = 4
  Placement = pos=(15.5,-62.5,18) rot=(0,0,1;0rad)
  Radius = 3
FEATURE [Part::MultiFuse] Fusion005043005007002078009  label="motor Inbus"
  Shapes = -> [Cylinder112024025003003006010004171,Cylinder112024025003003006010004172,Cylinder112024025003003006010004167,Cylinder112024025003003006010004168,Cylinder112024025003003006010004173,Cylinder112024025003003006010004174,Cylinder112024025003003006010004175,Cylinder112024025003003006010004176]
FEATURE [Part::Box] Box021166  label="Krychle156"
  AttacherType = Attacher::AttachEngine3D
  Height = 10
  Length = 10
  Width = 10
FEATURE [Part::Feature] Shape
  shape: bbox 19.56 x 2e-07 x 2e-07 mm, 0 faces, 0 solids (baked)
FEATURE [Part::Feature] Shape001
  shape: bbox 2e-07 x 20.45 x 2e-07 mm, 0 faces, 0 solids (baked)
FEATURE [Part::Feature] Shape002
  shape: bbox 19.56 x 2e-07 x 2e-07 mm, 0 faces, 0 solids (baked)
FEATURE [Part::Feature] Shape003
  shape: bbox 2e-07 x 20.32 x 2e-07 mm, 0 faces, 0 solids (baked)
FEATURE [Part::Feature] Shape004
  shape: bbox 0.127 x 0.127 x 2e-07 mm, 0 faces, 0 solids (baked)
FEATURE [Part::Feature] Shape005
  shape: bbox 3.048 x 2.032 x 2e-07 mm, 0 faces, 0 solids (baked)
FEATURE [Part::Feature] Shape006
  shape: bbox 3.81 x 0.127 x 2e-07 mm, 0 faces, 0 solids (baked)
FEATURE [Part::Feature] Shape007
  shape: bbox 2.413 x 2e-07 x 2e-07 mm, 0 faces, 0 solids (baked)
FEATURE [Part::Feature] Shape008
  shape: bbox 0.8865 x 0.8865 x 2e-07 mm, 0 faces, 0 solids (baked)
FEATURE [Part::Feature] Shape009
  shape: bbox 6.243 x 2e-07 x 2e-07 mm, 0 faces, 0 solids (baked)
FEATURE [Part::Feature] Shape010
  shape: bbox 0.8306 x 0.8306 x 2e-07 mm, 0 faces, 0 solids (baked)
FEATURE [Part::Feature] Shape011
  shape: bbox 1.168 x 0.6909 x 2e-07 mm, 0 faces, 0 solids (baked)
FEATURE [Part::Feature] Shape012
  shape: bbox 1.118 x 0.5969 x 2e-07 mm, 0 faces, 0 solids (baked)
FEATURE [Part::Feature] Shape013
  shape: bbox 4.064 x 0.127 x 2e-07 mm, 0 faces, 0 solids (baked)
FEATURE [Part::Feature] Shape014
  shape: bbox 2e-07 x 0.9042 x 2e-07 mm, 0 faces, 0 solids (baked)
FEATURE [Part::Feature] Shape015
  shape: bbox 3.383 x 3.917 x 2e-07 mm, 0 faces, 0 solids (baked)
FEATURE [Part::Feature] Shape016
  shape: bbox 8.024 x 2e-07 x 2e-07 mm, 0 faces, 0 solids (baked)
FEATURE [Part::Feature] Shape017
  shape: bbox 2e-07 x 4.064 x 2e-07 mm, 0 faces, 0 solids (baked)
FEATURE [Part::Feature] Shape018
  shape: bbox 1.778 x 0.127 x 2e-07 mm, 0 faces, 0 solids (baked)
FEATURE [Part::Feature] Shape019
  shape: bbox 5.588 x 2e-07 x 2e-07 mm, 0 faces, 0 solids (baked)
FEATURE [Part::Feature] Shape020
  shape: bbox 5.588 x 2e-07 x 2e-07 mm, 0 faces, 0 solids (baked)
FEATURE [Part::Feature] Shape021
  shape: bbox 2e-07 x 10.16 x 2e-07 mm, 0 faces, 0 solids (baked)
FEATURE [Part::Feature] Shape022
  shape: bbox 2e-07 x 1.27 x 2e-07 mm, 0 faces, 0 solids (baked)
FEATURE [Part::Feature] Shape023
  shape: bbox 2e-07 x 7.62 x 2e-07 mm, 0 faces, 0 solids (baked)
FEATURE [Part::Feature] Shape024
  shape: bbox 2e-07 x 1.27 x 2e-07 mm, 0 faces, 0 solids (baked)
FEATURE [Part::Feature] Shape025
  shape: bbox 1.27 x 2e-07 x 2e-07 mm, 0 faces, 0 solids (baked)
FEATURE [Part::Feature] Shape026
  shape: bbox 2e-07 x 7.62 x 2e-07 mm, 0 faces, 0 solids (baked)
FEATURE [Part::Feature] Shape027
  shape: bbox 1.27 x 2e-07 x 2e-07 mm, 0 faces, 0 solids (baked)
FEATURE [Part::Feature] Shape028
  shape: bbox 2e-07 x 10.2 x 2e-07 mm, 0 faces, 0 solids (baked)
FEATURE [Part::Feature] Shape029
  shape: bbox 14.65 x 2e-07 x 2e-07 mm, 0 faces, 0 solids (baked)
FEATURE [Part::Feature] Shape030
  shape: bbox 2e-07 x 10.2 x 2e-07 mm, 0 faces, 0 solids (baked)
FEATURE [Part::Feature] Shape031
  shape: bbox 14.65 x 2e-07 x 2e-07 mm, 0 faces, 0 solids (baked)
FEATURE [Part::Feature] Shape032
  shape: bbox 1.928 x 2e-07 x 2e-07 mm, 0 faces, 0 solids (baked)
FEATURE [Part::Feature] Shape033
  shape: bbox 2e-07 x 3.302 x 2e-07 mm, 0 faces, 0 solids (baked)
FEATURE [Part::Feature] Shape034
  shape: bbox 1.016 x 2e-07 x 2e-07 mm, 0 faces, 0 solids (baked)
FEATURE [Part::Feature] Shape035
  shape: bbox 2e-07 x 3.048 x 2e-07 mm, 0 faces, 0 solids (baked)
FEATURE [Part::Feature] Shape036
  shape: bbox 1.016 x 2e-07 x 2e-07 mm, 0 faces, 0 solids (baked)
FEATURE [Part::Feature] Shape037
  shape: bbox 2e-07 x 3.048 x 2e-07 mm, 0 faces, 0 solids (baked)
FEATURE [Part::Feature] Shape038
  shape: bbox 1.928 x 0.00254 x 2e-07 mm, 0 faces, 0 solids (baked)
FEATURE [Part::Feature] Shape039
  shape: bbox 2 x 2 x 2e-07 mm, 0 faces, 0 solids (baked)
FEATURE [Part::Feature] Shape040
  shape: bbox 2.5 x 2.5 x 2e-07 mm, 0 faces, 0 solids (baked)
FEATURE [Part::Feature] Shape041
  shape: bbox 2 x 2 x 2e-07 mm, 0 faces, 0 solids (baked)
FEATURE [Part::Feature] Shape042
  shape: bbox 2.5 x 2.5 x 2e-07 mm, 0 faces, 0 solids (baked)
FEATURE [Part::Feature] Shape043
  shape: bbox 2 x 2 x 2e-07 mm, 0 faces, 0 solids (baked)
FEATURE [Part::Feature] Shape044
  shape: bbox 2.5 x 2.5 x 2e-07 mm, 0 faces, 0 solids (baked)
FEATURE [Part::Feature] Shape045
  shape: bbox 2 x 2 x 2e-07 mm, 0 faces, 0 solids (baked)
FEATURE [Part::Feature] Shape046
  shape: bbox 2.5 x 2.5 x 2e-07 mm, 0 faces, 0 solids (baked)
FEATURE [Part::Feature] Shape047
  shape: bbox 1.016 x 1.016 x 2e-07 mm, 0 faces, 0 solids (baked)
FEATURE [Part::Feature] Shape048
  shape: bbox 1.88 x 1.88 x 2e-07 mm, 0 faces, 0 solids (baked)
FEATURE [Part::Feature] Shape049
  shape: bbox 1.016 x 1.016 x 2e-07 mm, 0 faces, 0 solids (baked)
FEATURE [Part::Feature] Shape050
  shape: bbox 1.88 x 1.88 x 2e-07 mm, 0 faces, 0 solids (baked)
FEATURE [Part::Feature] Shape051
  shape: bbox 1.016 x 1.016 x 2e-07 mm, 0 faces, 0 solids (baked)
FEATURE [Part::Feature] Shape052
  shape: bbox 1.88 x 1.88 x 2e-07 mm, 0 faces, 0 solids (baked)
FEATURE [Part::Feature] Shape053
  shape: bbox 0.9144 x 0.9144 x 2e-07 mm, 0 faces, 0 solids (baked)
FEATURE [Part::Feature] Shape054
  shape: bbox 1.524 x 1.524 x 2e-07 mm, 0 faces, 0 solids (baked)
FEATURE [Part::Feature] Shape055
  shape: bbox 0.9144 x 0.9144 x 2e-07 mm, 0 faces, 0 solids (baked)
FEATURE [Part::Feature] Shape056
  shape: bbox 1.524 x 1.524 x 2e-07 mm, 0 faces, 0 solids (baked)
FEATURE [Part::Feature] Shape057
  shape: bbox 0.9144 x 0.9144 x 2e-07 mm, 0 faces, 0 solids (baked)
FEATURE [Part::Feature] Shape058
  shape: bbox 1.524 x 1.524 x 2e-07 mm, 0 faces, 0 solids (baked)
FEATURE [Part::Feature] Shape059
  shape: bbox 0.9144 x 0.9144 x 2e-07 mm, 0 faces, 0 solids (baked)
FEATURE [Part::Feature] Shape060
  shape: bbox 1.524 x 1.524 x 2e-07 mm, 0 faces, 0 solids (baked)
FEATURE [Part::Feature] Shape061
  shape: bbox 1.016 x 1.016 x 2e-07 mm, 0 faces, 0 solids (baked)
FEATURE [Part::Feature] Shape062
  shape: bbox 2e-07 x 1.88 x 2e-07 mm, 0 faces, 0 solids (baked)
FEATURE [Part::Feature] Shape063
  shape: bbox 1.88 x 2e-07 x 2e-07 mm, 0 faces, 0 solids (baked)
FEATURE [Part::Feature] Shape064
  shape: bbox 2e-07 x 1.88 x 2e-07 mm, 0 faces, 0 solids (baked)
FEATURE [Part::Feature] Shape065
  shape: bbox 1.88 x 2e-07 x 2e-07 mm, 0 faces, 0 solids (baked)
FEATURE [Part::Feature] Shape066
  shape: bbox 2.032 x 2.032 x 2e-07 mm, 0 faces, 0 solids (baked)
FEATURE [Part::Feature] Shape067
  shape: bbox 2.032 x 2.032 x 2e-07 mm, 0 faces, 0 solids (baked)
FEATURE [Part::Box] Box021167  label="PCB001"
  AttacherType = Attacher::AttachEngine3D
  Height = 25
  Length = 23
  Placement = pos=(-10.5,-10.5,0) rot=(0,0,1;0rad)
  Width = 21
FEATURE [Part::Box] Box021168  label="Krychle157"
  AttacherType = Attacher::AttachEngine3D
  Height = 16
  Length = 20
  Placement = pos=(-13,-7,0) rot=(0,0,1;0rad)
  Width = 14
FEATURE [Part::Cylinder] Cylinder112024025003003006010004177  label="Válec285"
  Angle = 360
  AttacherType = Attacher::AttachEngine3D
  Height = 15
  Placement = pos=(-2.5,8,-5) rot=(0,0,1;0rad)
  Radius = 0.75
FEATURE [Part::Cylinder] Cylinder112024025003003006010004178  label="Válec286"
  Angle = 360
  AttacherType = Attacher::AttachEngine3D
  Height = 15
  Placement = pos=(5,-7.5,-5) rot=(0,0,1;0rad)
  Radius = 0.75
FEATURE [Part::Cylinder] Cylinder112024025003003006010004179  label="Válec287"
  Angle = 360
  AttacherType = Attacher::AttachEngine3D
  Height = 15
  Placement = pos=(5,8,-5) rot=(0,0,1;0rad)
  Radius = 0.75
FEATURE [Part::Cylinder] Cylinder112024025003003006010004180  label="Válec288"
  Angle = 359
  AttacherType = Attacher::AttachEngine3D
  Height = 18
  Placement = pos=(-2.5,-7.5,-5) rot=(0,0,1;0rad)
  Radius = 0.75
FEATURE [Part::Box] Box021169  label="Krychle158"
  AttacherType = Attacher::AttachEngine3D
  Height = 15
  Length = 21
  Placement = pos=(-10.5,-6,-2) rot=(0,0,1;0rad)
  Width = 12
FEATURE [Part::Cylinder] Cylinder112024025003003006010004181  label="Válec289"
  Angle = 359
  AttacherType = Attacher::AttachEngine3D
  Height = 2
  Placement = pos=(-5.5,-5.5,-2) rot=(0,0,1;0rad)
  Radius = 1.75
FEATURE [Part::Cylinder] Cylinder112024025003003006010004182  label="Válec290"
  Angle = 359
  AttacherType = Attacher::AttachEngine3D
  Height = 2
  Placement = pos=(-5.5,6,-2) rot=(0,0,1;0rad)
  Radius = 1.75
FEATURE [Part::MultiFuse] Fusion005043005007002078010  label="Port"
  Placement = pos=(0,-82,26) rot=(0,0,1;1.5708rad)
  Shapes = -> [Box021167,Box021169,Cylinder112024025003003006010004178,Cylinder112024025003003006010004177,Box021168,Cylinder112024025003003006010004180,Cylinder112024025003003006010004179,Cylinder112024025003003006010004181,Cylinder112024025003003006010004182]
FEATURE [Part::MultiFuse] Fusion005043005007002078008  label="Motor vyrezy001"
  Shapes = -> [Box021158,Box021159,Box021162,Cylinder112024025003003006010004166,Cylinder112024025003003006010004169,Cylinder112024025003003006010004170,Box021163,Fusion005043005007002078009,Fusion005043005007002078010,Extrude006]
FEATURE [Part::Cut] Cut018020020009027020002003004004026003005007002  label="EAF Motor001"
  Base = -> Fusion005043005007002078007
  Tool = -> Fusion005043005007002078008
FEATURE [Part::Fillet] Fillet028003  label="OnSterpFokus"
  Base = -> Cut018020020009027020002003004004026003005007002
  Edges = 14 edges: [Edge4 r=1,Edge7 r=1,Edge8 r=2,Edge17 r=1,Edge21 r=1,Edge25 r=2,Edge38 r=2,Edge42 r=2,Edge46 r=2,Edge48 r=2,Edge677 r=1,Edge680 r=1,Edge683 r=1,Edge684 r=1]
FEATURE [Part::Feature] Fillet028003001  label="OnSterpFokus001"
  shape: bbox 53 x 69 x 42.5 mm, 320 faces (baked)
FEATURE [Part::Feature] Fillet028003002  label="SCT-baseV005"
  shape: bbox 50 x 110 x 18.33 mm, 80 faces (baked)
FEATURE [Part::Box] Box021170  label="Krychle159"
  AttacherType = Attacher::AttachEngine3D
  Height = 13
  Length = 50
  Placement = pos=(-25,-96,7) rot=(0,0,1;0rad)
  Width = 86
FEATURE [Part::Box] Box021171  label="Krychle160"
  AttacherType = Attacher::AttachEngine3D
  Height = 23
  Length = 50
  Placement = pos=(-25,-25,-16) rot=(0.995037,0,0.099504;0rad)
  Width = 15
FEATURE [Part::Cylinder] Cylinder112024025003003006010004190  label="sroub001"
  Angle = 360
  AttacherType = Attacher::AttachEngine3D
  Height = 60
  Placement = pos=(-30,-64,14) rot=(0,1,0;1.5708rad)
  Radius = 2.2
FEATURE [Part::Cylinder] Cylinder112024025003003006010004191  label="Válec296"
  Angle = 360
  AttacherType = Attacher::AttachEngine3D
  Height = 5
  Placement = pos=(-9,-90.5,7) rot=(0,0,1;0rad)
  Radius = 3.7
FEATURE [Part::Box] Box021173  label="Krychle162"
  AttacherType = Attacher::AttachEngine3D
  Height = 13
  Length = 4.5
  Placement = pos=(20.5,-102,7) rot=(0,0,1;0rad)
  Width = 77
FEATURE [Part::Cylinder] Cylinder112024025003003006010004196  label="Válec301"
  Angle = 360
  AttacherType = Attacher::AttachEngine3D
  Height = 5
  Placement = pos=(9,-90.5,7) rot=(0,0,1;0rad)
  Radius = 3.7
FEATURE [Part::Box] Box021174  label="Krychle163"
  AttacherType = Attacher::AttachEngine3D
  Height = 5
  Length = 7.4
  Placement = pos=(5.3,-90.5,7) rot=(0,0,1;0rad)
  Width = 18
FEATURE [Part::Box] Box021178  label="Krychle167"
  AttacherType = Attacher::AttachEngine3D
  Height = 13
  Length = 4.5
  Placement = pos=(-25,-102,7) rot=(0,0,1;0rad)
  Width = 77
FEATURE [Part::Cylinder] Cylinder112024025003003006010004197  label="Válec302"
  Angle = 360
  AttacherType = Attacher::AttachEngine3D
  Height = 5
  Placement = pos=(-9,-72.5,7) rot=(0,0,1;0rad)
  Radius = 3.7
FEATURE [Part::Box] Box021179  label="Krychle168"
  AttacherType = Attacher::AttachEngine3D
  Height = 13
  Length = 24
  Placement = pos=(-12,-57.5,7) rot=(0,0,1;0rad)
  Width = 49
FEATURE [Part::Cylinder] Cylinder112024025003003006010004199  label="Válec304"
  Angle = 360
  AttacherType = Attacher::AttachEngine3D
  Height = 13
  Placement = pos=(0,-57.5,7) rot=(0,0,1;0rad)
  Radius = 12
FEATURE [Part::Cylinder] Cylinder112024025003003006010004200  label="Válec305"
  Angle = 360
  AttacherType = Attacher::AttachEngine3D
  Height = 5
  Placement = pos=(9,-72.5,7) rot=(0,0,1;0rad)
  Radius = 3.7
FEATURE [Part::Box] Box021181  label="Krychle170"
  AttacherType = Attacher::AttachEngine3D
  Height = 5
  Length = 7.4
  Placement = pos=(-12.7,-90.5,7) rot=(0,0,1;0rad)
  Width = 18
FEATURE [Part::Box] Box021175  label="Krychle164"
  AttacherType = Attacher::AttachEngine3D
  Height = 10
  Length = 3.5
  Placement = pos=(13.5,-58,0) rot=(0,0,1;0rad)
  Width = 7
FEATURE [Sketcher::SketchObject] Sketch005
  MapMode = 5
  Placement = pos=(13.5,-58,0) rot=(0.57735,-0.57735,-0.57735;2.0944rad)
  Support = -> [Box021175]
  sketch-geometry (7):
    g0: LineSegment StartX=-3.5 StartY=4 StartZ=0 EndX=-6.9641 EndY=2 EndZ=0
    g1: LineSegment StartX=-6.9641 StartY=2 StartZ=0 EndX=-6.9641 EndY=-2 EndZ=0
    g2: LineSegment StartX=-6.9641 StartY=-2 StartZ=0 EndX=-3.5 EndY=-4 EndZ=0
    g3: LineSegment StartX=-3.5 StartY=-4 StartZ=0 EndX=-0.0358984 EndY=-2 EndZ=0
    g4: LineSegment StartX=-0.0358984 StartY=-2 StartZ=0 EndX=-0.0358984 EndY=2 EndZ=0
    g5: LineSegment StartX=-0.0358984 StartY=2 StartZ=0 EndX=-3.5 EndY=4 EndZ=0
    g6: Circle [constr] CenterX=-3.5 CenterY=0 CenterZ=0 NormalX=0 NormalY=0 NormalZ=1 AngleXU=0 Radius=4
  constraints (14):
    c: Coincident(g0,g1)
    c: Coincident(g1,g2)
    c: Coincident(g2,g3)
    c: Coincident(g3,g4)
    c: Coincident(g4,g5)
    c: Coincident(g5,g0)
    c: Equal(g0, g1-g5) x5
    c: PointOnObject(g0,g6)
    c: PointOnObject(g1,g6)
    c: PointOnObject(g2,g6)
    c: PointOnObject(g3,g6)
    c: PointOnObject(g4,g6)
    c: PointOnObject(g5,g6)
    c: PointOnObject(g6,g-1)
FEATURE [Part::Extrusion] Extrude007
  Base = -> Sketch005
  Dir = (-1,0,0)
  DirMode = 2
  FaceMakerClass = Part::FaceMakerBullseye
  LengthFwd = -3.5
  LengthRev = 0
  Solid = true
  Symmetric = false
FEATURE [Part::Box] Box021176  label="Krychle165"
  AttacherType = Attacher::AttachEngine3D
  Height = 10
  Length = 3.5
  Placement = pos=(13.5,-58,0) rot=(0,0,1;0rad)
  Width = 7
FEATURE [Sketcher::SketchObject] Sketch007
  MapMode = 5
  Placement = pos=(13.5,-58,0) rot=(0.57735,-0.57735,-0.57735;2.0944rad)
  Support = -> [Box021176]
  sketch-geometry (7):
    g0: LineSegment StartX=-3.5 StartY=4 StartZ=0 EndX=-6.9641 EndY=2 EndZ=0
    g1: LineSegment StartX=-6.9641 StartY=2 StartZ=0 EndX=-6.9641 EndY=-2 EndZ=0
    g2: LineSegment StartX=-6.9641 StartY=-2 StartZ=0 EndX=-3.5 EndY=-4 EndZ=0
    g3: LineSegment StartX=-3.5 StartY=-4 StartZ=0 EndX=-0.0358984 EndY=-2 EndZ=0
    g4: LineSegment StartX=-0.0358984 StartY=-2 StartZ=0 EndX=-0.0358984 EndY=2 EndZ=0
    g5: LineSegment StartX=-0.0358984 StartY=2 StartZ=0 EndX=-3.5 EndY=4 EndZ=0
    g6: Circle [constr] CenterX=-3.5 CenterY=0 CenterZ=0 NormalX=0 NormalY=0 NormalZ=1 AngleXU=0 Radius=4
  constraints (14):
    c: Coincident(g0,g1)
    c: Coincident(g1,g2)
    c: Coincident(g2,g3)
    c: Coincident(g3,g4)
    c: Coincident(g4,g5)
    c: Coincident(g5,g0)
    c: Equal(g0, g1-g5) x5
    c: PointOnObject(g0,g6)
    c: PointOnObject(g1,g6)
    c: PointOnObject(g2,g6)
    c: PointOnObject(g3,g6)
    c: PointOnObject(g4,g6)
    c: PointOnObject(g5,g6)
    c: PointOnObject(g6,g-1)
FEATURE [Part::Extrusion] Extrude008
  Base = -> Sketch007
  Dir = (-1,0,0)
  DirMode = 2
  FaceMakerClass = Part::FaceMakerBullseye
  LengthFwd = -3.5
  LengthRev = 0
  Solid = true
  Symmetric = false
FEATURE [Part::MultiFuse] Fusion005043005007002078019  label="Matice007"
  Placement = pos=(1,-118.5,14) rot=(1,0,0;3.14159rad)
  Shapes = -> [Box021175,Extrude007]
FEATURE [Part::MultiFuse] Fusion005043005007002078011  label="Matice005"
  Placement = pos=(-31.5,-118.5,14) rot=(1,0,0;3.14159rad)
  Shapes = -> [Box021176,Extrude008]
FEATURE [Part::MultiFuse] Fusion005043005007002078016  label="Holes005"
  Shapes = -> [Box021178,Box021173,Cylinder112024025003003006010004190,Cylinder112024025003003006010004199,Box021179,Box021181,Box021174,Cylinder112024025003003006010004200,Cylinder112024025003003006010004196,Cylinder112024025003003006010004197,Cylinder112024025003003006010004191,Fusion005043005007002078019,Fusion005043005007002078011]
FEATURE [Part::Cylinder] Cylinder112024025003003006010004201  label="Válec306"
  Angle = 90
  AttacherType = Attacher::AttachEngine3D
  Height = 13
  Placement = pos=(-25,-23,7) rot=(0,0,1;0rad)
  Radius = 13
FEATURE [Part::Cylinder] Cylinder112024025003003006010004202  label="Válec307"
  Angle = 90
  AttacherType = Attacher::AttachEngine3D
  Height = 13
  Placement = pos=(25,-23,7) rot=(0,0,1;1.5708rad)
  Radius = 13
FEATURE [Part::MultiFuse] Fusion005043005007002078013  label="Main001"
  Shapes = -> [Box021171,Box021170,Cut018020020009027020002003004004026003005,Cylinder112024025003003006010004201,Cylinder112024025003003006010004202]
FEATURE [Part::Cut] Cut018020020009027020002003004004026003005007003  label="EAF_H"
  Base = -> Fusion005043005007002078013
  Tool = -> Fusion005043005007002078016
FEATURE [App::Part] Part004  label="Body"
  Group = -> [Cylinder112024025003003006010004142,Box021146,Cylinder112024025003003006010004144,Cylinder112024025003003006010004141,Cylinder112024025003003006010004143,Fusion005043005007002069,Fusion005043005007002068,Cut018020020009027020002003004004026003005005,Cylinder016,ShapeString,Sketch005,Sketch007,Fillet030,Cut018020020009027020002003004004026003005007003,Cut018020020009027020002003004004026003003,+42 more]
  License = CC BY 3.0
  LicenseURL = http://creativecommons.org/licenses/by/3.0/
  Origin = -> Origin004
FEATURE [Part::Part2DObjectPython] ShapeString002  # Draft 2D object (typed FeaturePython)
  FontFile = <path>
  Placement = pos=(-13.13,-84,29.82) rot=(1,0,0;1.5708rad)
  Size = 10
  String = EAF
  Tracking = 0
FEATURE [Part::Box] Box021182  label="Krychle171"
  AttacherType = Attacher::AttachEngine3D
  Height = 4.6
  Length = 53
  Placement = pos=(-26.5,-64,9.2) rot=(0,0,1;0rad)
  Width = 18
FEATURE [Part::Box] Box021183  label="Krychle172"
  AttacherType = Attacher::AttachEngine3D
  Height = 19
  Length = 4
  Placement = pos=(21,-84,29.5) rot=(0,0,1;0rad)
  Width = 6.5
FEATURE [Part::Cylinder] Cylinder112024025003003006010004203  label="cy055"
  Angle = 360
  AttacherType = Attacher::AttachEngine3D
  Height = 24
  Placement = pos=(9,-72.5,0) rot=(0,0,1;0rad)
  Radius = 2.2
FEATURE [Part::Box] Box021184  label="Krychle173"
  AttacherType = Attacher::AttachEngine3D
  Height = 42.5
  Length = 50
  Placement = pos=(-25,-84,6) rot=(0,0,1;0rad)
  Width = 58
FEATURE [Part::Box] Box021185  label="Krychle174"
  AttacherType = Attacher::AttachEngine3D
  Height = 10
  Length = 53
  Placement = pos=(-26.5,-64,6.5) rot=(0,0,1;0rad)
  Width = 18
FEATURE [Part::Cylinder] Cylinder112024025003003006010004204  label="Válec308"
  Angle = 360
  AttacherType = Attacher::AttachEngine3D
  Height = 53
  Placement = pos=(-26.5,-46,11.5) rot=(0,1,0;1.5708rad)
  Radius = 5
FEATURE [Part::Cylinder] Cylinder112024025003003006010004205  label="cy056"
  Angle = 360
  AttacherType = Attacher::AttachEngine3D
  Height = 24
  Placement = pos=(0,-39,0) rot=(0,0,1;0rad)
  Radius = 12
FEATURE [Part::Extrusion] Extrude009
  Base = -> ShapeString002
  Dir = (0,-1,0)
  DirMode = 2
  FaceMakerClass = Part::FaceMakerBullseye
  LengthFwd = -0.75
  LengthRev = 0
  Solid = false
  Symmetric = false
FEATURE [Part::Box] Box021186  label="Krychle175"
  AttacherType = Attacher::AttachEngine3D
  Height = 19.5
  Length = 50
  Placement = pos=(-25,-77.5,29.5) rot=(0,0,1;0rad)
  Width = 58
FEATURE [Part::Cylinder] Cylinder112024025003003006010004206  label="Válec309"
  Angle = 360
  AttacherType = Attacher::AttachEngine3D
  Height = 53
  Placement = pos=(-26.5,-64,11.5) rot=(0,1,0;1.5708rad)
  Radius = 2.3
FEATURE [Part::Box] Box021187  label="Krychle176"
  AttacherType = Attacher::AttachEngine3D
  Height = 26
  Length = 42
  Placement = pos=(-21,-77.5,22.5) rot=(0,0,1;0rad)
  Width = 58
FEATURE [Part::Cylinder] Cylinder112024025003003006010004207  label="cy057"
  Angle = 360
  AttacherType = Attacher::AttachEngine3D
  Height = 24
  Placement = pos=(-9,-72.5,0) rot=(0,0,1;0rad)
  Radius = 2.2
FEATURE [Part::Cylinder] Cylinder112024025003003006010004208  label="Válec310"
  Angle = 360
  AttacherType = Attacher::AttachEngine3D
  Height = 53
  Placement = pos=(-26.5,-46,11.5) rot=(0,1,0;1.5708rad)
  Radius = 2.3
FEATURE [Part::Box] Box021188  label="Krychle177"
  AttacherType = Attacher::AttachEngine3D
  Height = 19
  Length = 4
  Placement = pos=(-25,-84,29.5) rot=(0,0,1;0rad)
  Width = 6.5
FEATURE [Part::Box] Box021189  label="Krychle178"
  AttacherType = Attacher::AttachEngine3D
  Height = 12.5
  Length = 42
  Placement = pos=(-21,-84,5.5) rot=(0,0,1;0rad)
  Width = 58
FEATURE [Part::MultiFuse] Fusion005043005007002078020  label="Motor vyrezy002"
  Shapes = -> [Box021189,Box021187,Box021186,Cylinder112024025003003006010004207,Cylinder112024025003003006010004203,Cylinder112024025003003006010004205,Cylinder112024025003003006010004206,Cylinder112024025003003006010004208,Box021182,Box021183,Box021188]
FEATURE [Part::Cylinder] Cylinder112024025003003006010004209  label="Válec311"
  Angle = 360
  AttacherType = Attacher::AttachEngine3D
  Height = 53
  Placement = pos=(-26.5,-64,11.5) rot=(0,1,0;1.5708rad)
  Radius = 5
FEATURE [Part::MultiFuse] Fusion005043005007002078021  label="Motor M003"
  Shapes = -> [Cylinder112024025003003006010004209,Cylinder112024025003003006010004204,Box021185,Box021184]
FEATURE [Part::Cut] Cut018020020009027020002003004004026003005007006  label="EAF Motor002"
  Base = -> Fusion005043005007002078021
  Tool = -> Fusion005043005007002078020
FEATURE [Part::Fillet] Fillet028003003  label="EAF-Motor V005"
  Base = -> Cut018020020009027020002003004004026003005007006
  Edges = 20 edges: [Edge4 r=1,Edge7 r=1,Edge8 r=1,Edge9 r=2,Edge10 r=2,Edge16 r=1,Edge20 r=1,Edge24 r=2,Edge28 r=2,Edge31 r=2,Edge34 r=1,Edge39 r=2,Edge43 r=2,Edge77 r=2,Edge79 r=2,Edge85 r=2,Edge117 r=1,Edge120 r=1,Edge123 r=1,Edge124 r=1]
FEATURE [Part::Box] Box021190  label="Krychle179"
  AttacherType = Attacher::AttachEngine3D
  Height = 13
  Length = 50
  Placement = pos=(-25,-96,7) rot=(0,0,1;0rad)
  Width = 86
FEATURE [Part::Box] Box021191  label="Krychle180"
  AttacherType = Attacher::AttachEngine3D
  Height = 23
  Length = 50
  Placement = pos=(-25,-25,-16) rot=(0.995037,0,0.099504;0rad)
  Width = 15
FEATURE [Part::Box] Box021192  label="Krychle181"
  AttacherType = Attacher::AttachEngine3D
  Height = 5
  Length = 7.4
  Placement = pos=(5.3,-90.5,7) rot=(0,0,1;0rad)
  Width = 18
FEATURE [Part::Cylinder] Cylinder112024025003003006010004210  label="Válec312"
  Angle = 360
  AttacherType = Attacher::AttachEngine3D
  Height = 5
  Placement = pos=(-9,-90.5,7) rot=(0,0,1;0rad)
  Radius = 3.7
FEATURE [Part::Box] Box021193  label="Krychle182"
  AttacherType = Attacher::AttachEngine3D
  Height = 13
  Length = 4.5
  Placement = pos=(-25,-102,7) rot=(0,0,1;0rad)
  Width = 77
FEATURE [Part::Box] Box021194  label="Krychle183"
  AttacherType = Attacher::AttachEngine3D
  Height = 13
  Length = 4.5
  Placement = pos=(20.5,-102,7) rot=(0,0,1;0rad)
  Width = 77
FEATURE [Part::Cylinder] Cylinder112024025003003006010004211  label="Válec313"
  Angle = 360
  AttacherType = Attacher::AttachEngine3D
  Height = 5
  Placement = pos=(-9,-72.5,7) rot=(0,0,1;0rad)
  Radius = 3.7
FEATURE [Part::Box] Box021195  label="Krychle184"
  AttacherType = Attacher::AttachEngine3D
  Height = 13
  Length = 24
  Placement = pos=(-12,-57.5,7) rot=(0,0,1;0rad)
  Width = 49
FEATURE [Part::Cylinder] Cylinder112024025003003006010004212  label="Válec314"
  Angle = 360
  AttacherType = Attacher::AttachEngine3D
  Height = 13
  Placement = pos=(0,-57.5,7) rot=(0,0,1;0rad)
  Radius = 12
FEATURE [Part::Cylinder] Cylinder112024025003003006010004213  label="sroub002"
  Angle = 360
  AttacherType = Attacher::AttachEngine3D
  Height = 60
  Placement = pos=(-30,-64,14) rot=(0,1,0;1.5708rad)
  Radius = 2.2
FEATURE [Part::Cylinder] Cylinder112024025003003006010004214  label="Válec315"
  Angle = 360
  AttacherType = Attacher::AttachEngine3D
  Height = 5
  Placement = pos=(9,-90.5,7) rot=(0,0,1;0rad)
  Radius = 3.7
FEATURE [Part::Cylinder] Cylinder112024025003003006010004215  label="Válec316"
  Angle = 360
  AttacherType = Attacher::AttachEngine3D
  Height = 5
  Placement = pos=(9,-72.5,7) rot=(0,0,1;0rad)
  Radius = 3.7
FEATURE [Part::Cylinder] Cylinder112024025003003006010004216  label="Válec317"
  Angle = 90
  AttacherType = Attacher::AttachEngine3D
  Height = 13
  Placement = pos=(25,-23,7) rot=(0,0,1;1.5708rad)
  Radius = 13
FEATURE [Part::Cylinder] Cylinder112024025003003006010004217  label="Válec318"
  Angle = 90
  AttacherType = Attacher::AttachEngine3D
  Height = 13
  Placement = pos=(-25,-23,7) rot=(0,0,1;0rad)
  Radius = 13
FEATURE [Part::MultiFuse] Fusion005043005007002078023  label="Main002"
  Shapes = -> [Box021191,Box021190,Cylinder112024025003003006010004217,Cylinder112024025003003006010004216]
FEATURE [Part::Box] Box021196  label="Krychle185"
  AttacherType = Attacher::AttachEngine3D
  Height = 10
  Length = 3.5
  Placement = pos=(13.5,-58,0) rot=(0,0,1;0rad)
  Width = 7
FEATURE [Sketcher::SketchObject] Sketch009
  MapMode = 5
  Placement = pos=(13.5,-58,0) rot=(0.57735,-0.57735,-0.57735;2.0944rad)
  Support = -> [Box021196]
  sketch-geometry (7):
    g0: LineSegment StartX=-3.5 StartY=4 StartZ=0 EndX=-6.9641 EndY=2 EndZ=0
    g1: LineSegment StartX=-6.9641 StartY=2 StartZ=0 EndX=-6.9641 EndY=-2 EndZ=0
    g2: LineSegment StartX=-6.9641 StartY=-2 StartZ=0 EndX=-3.5 EndY=-4 EndZ=0
    g3: LineSegment StartX=-3.5 StartY=-4 StartZ=0 EndX=-0.0358984 EndY=-2 EndZ=0
    g4: LineSegment StartX=-0.0358984 StartY=-2 StartZ=0 EndX=-0.0358984 EndY=2 EndZ=0
    g5: LineSegment StartX=-0.0358984 StartY=2 StartZ=0 EndX=-3.5 EndY=4 EndZ=0
    g6: Circle [constr] CenterX=-3.5 CenterY=0 CenterZ=0 NormalX=0 NormalY=0 NormalZ=1 AngleXU=0 Radius=4
  constraints (14):
    c: Coincident(g0,g1)
    c: Coincident(g1,g2)
    c: Coincident(g2,g3)
    c: Coincident(g3,g4)
    c: Coincident(g4,g5)
    c: Coincident(g5,g0)
    c: Equal(g0, g1-g5) x5
    c: PointOnObject(g0,g6)
    c: PointOnObject(g1,g6)
    c: PointOnObject(g2,g6)
    c: PointOnObject(g3,g6)
    c: PointOnObject(g4,g6)
    c: PointOnObject(g5,g6)
    c: PointOnObject(g6,g-1)
FEATURE [Part::Box] Box021197  label="Krychle186"
  AttacherType = Attacher::AttachEngine3D
  Height = 5
  Length = 7.4
  Placement = pos=(-12.7,-90.5,7) rot=(0,0,1;0rad)
  Width = 18
FEATURE [Part::Box] Box021198  label="Krychle187"
  AttacherType = Attacher::AttachEngine3D
  Height = 10
  Length = 3.5
  Placement = pos=(13.5,-58,0) rot=(0,0,1;0rad)
  Width = 7
FEATURE [Sketcher::SketchObject] Sketch008
  MapMode = 5
  Placement = pos=(13.5,-58,0) rot=(0.57735,-0.57735,-0.57735;2.0944rad)
  Support = -> [Box021198]
  sketch-geometry (7):
    g0: LineSegment StartX=-3.5 StartY=4 StartZ=0 EndX=-6.9641 EndY=2 EndZ=0
    g1: LineSegment StartX=-6.9641 StartY=2 StartZ=0 EndX=-6.9641 EndY=-2 EndZ=0
    g2: LineSegment StartX=-6.9641 StartY=-2 StartZ=0 EndX=-3.5 EndY=-4 EndZ=0
    g3: LineSegment StartX=-3.5 StartY=-4 StartZ=0 EndX=-0.0358984 EndY=-2 EndZ=0
    g4: LineSegment StartX=-0.0358984 StartY=-2 StartZ=0 EndX=-0.0358984 EndY=2 EndZ=0
    g5: LineSegment StartX=-0.0358984 StartY=2 StartZ=0 EndX=-3.5 EndY=4 EndZ=0
    g6: Circle [constr] CenterX=-3.5 CenterY=0 CenterZ=0 NormalX=0 NormalY=0 NormalZ=1 AngleXU=0 Radius=4
  constraints (14):
    c: Coincident(g0,g1)
    c: Coincident(g1,g2)
    c: Coincident(g2,g3)
    c: Coincident(g3,g4)
    c: Coincident(g4,g5)
    c: Coincident(g5,g0)
    c: Equal(g0, g1-g5) x5
    c: PointOnObject(g0,g6)
    c: PointOnObject(g1,g6)
    c: PointOnObject(g2,g6)
    c: PointOnObject(g3,g6)
    c: PointOnObject(g4,g6)
    c: PointOnObject(g5,g6)
    c: PointOnObject(g6,g-1)
FEATURE [Part::Extrusion] Extrude010
  Base = -> Sketch009
  Dir = (-1,0,0)
  DirMode = 2
  FaceMakerClass = Part::FaceMakerBullseye
  LengthFwd = -3.5
  LengthRev = 0
  Solid = true
  Symmetric = false
FEATURE [Part::MultiFuse] Fusion005043005007002078024  label="Matice009"
  Placement = pos=(-31.5,-118.5,14) rot=(1,0,0;3.14159rad)
  Shapes = -> [Box021196,Extrude010]
FEATURE [Part::Extrusion] Extrude011
  Base = -> Sketch008
  Dir = (-1,0,0)
  DirMode = 2
  FaceMakerClass = Part::FaceMakerBullseye
  LengthFwd = -3.5
  LengthRev = 0
  Solid = true
  Symmetric = false
FEATURE [Part::MultiFuse] Fusion005043005007002078022  label="Matice008"
  Placement = pos=(1,-118.5,14) rot=(1,0,0;3.14159rad)
  Shapes = -> [Box021198,Extrude011]
FEATURE [Part::MultiFuse] Fusion005043005007002078025  label="Holes006"
  Shapes = -> [Box021193,Box021194,Cylinder112024025003003006010004213,Cylinder112024025003003006010004212,Box021195,Box021197,Box021192,Cylinder112024025003003006010004215,Cylinder112024025003003006010004214,Cylinder112024025003003006010004211,Cylinder112024025003003006010004210,Fusion005043005007002078022,Fusion005043005007002078024]
FEATURE [Part::Cut] Cut018020020009027020002003004004026003005007005  label="EAF_H001"
  Base = -> Fusion005043005007002078023
  Tool = -> Fusion005043005007002078025
FEATURE [Part::Box] Box021199  label="Krychle188"
  AttacherType = Attacher::AttachEngine3D
  Height = 23
  Length = 50
  Placement = pos=(-25,-25,-16) rot=(0.995037,0,0.099504;0rad)
  Width = 15
FEATURE [Part::Cylinder] Cylinder112024025003003006010004218  label="Válec319"
  Angle = 360
  AttacherType = Attacher::AttachEngine3D
  Height = 5
  Placement = pos=(-9,-90.5,7) rot=(0,0,1;0rad)
  Radius = 3.7
FEATURE [Part::Box] Box021200  label="Krychle189"
  AttacherType = Attacher::AttachEngine3D
  Height = 13
  Length = 50
  Placement = pos=(-25,-96,7) rot=(0,0,1;0rad)
  Width = 73
FEATURE [Part::Box] Box021201  label="Krychle190"
  AttacherType = Attacher::AttachEngine3D
  Height = 5
  Length = 7.4
  Placement = pos=(5.3,-90.5,7) rot=(0,0,1;0rad)
  Width = 18
FEATURE [Part::Box] Box021202  label="Krychle191"
  AttacherType = Attacher::AttachEngine3D
  Height = 10
  Length = 3.5
  Placement = pos=(13.5,-58,0) rot=(0,0,1;0rad)
  Width = 7
FEATURE [Sketcher::SketchObject] Sketch011
  MapMode = 5
  Placement = pos=(13.5,-58,0) rot=(0.57735,-0.57735,-0.57735;2.0944rad)
  Support = -> [Box021202]
  sketch-geometry (7):
    g0: LineSegment StartX=-3.5 StartY=4 StartZ=0 EndX=-6.9641 EndY=2 EndZ=0
    g1: LineSegment StartX=-6.9641 StartY=2 StartZ=0 EndX=-6.9641 EndY=-2 EndZ=0
    g2: LineSegment StartX=-6.9641 StartY=-2 StartZ=0 EndX=-3.5 EndY=-4 EndZ=0
    g3: LineSegment StartX=-3.5 StartY=-4 StartZ=0 EndX=-0.0358984 EndY=-2 EndZ=0
    g4: LineSegment StartX=-0.0358984 StartY=-2 StartZ=0 EndX=-0.0358984 EndY=2 EndZ=0
    g5: LineSegment StartX=-0.0358984 StartY=2 StartZ=0 EndX=-3.5 EndY=4 EndZ=0
    g6: Circle [constr] CenterX=-3.5 CenterY=0 CenterZ=0 NormalX=0 NormalY=0 NormalZ=1 AngleXU=0 Radius=4
  constraints (14):
    c: Coincident(g0,g1)
    c: Coincident(g1,g2)
    c: Coincident(g2,g3)
    c: Coincident(g3,g4)
    c: Coincident(g4,g5)
    c: Coincident(g5,g0)
    c: Equal(g0, g1-g5) x5
    c: PointOnObject(g0,g6)
    c: PointOnObject(g1,g6)
    c: PointOnObject(g2,g6)
    c: PointOnObject(g3,g6)
    c: PointOnObject(g4,g6)
    c: PointOnObject(g5,g6)
    c: PointOnObject(g6,g-1)
FEATURE [Part::Cylinder] Cylinder112024025003003006010004219  label="Válec320"
  Angle = 360
  AttacherType = Attacher::AttachEngine3D
  Height = 13
  Placement = pos=(25,-23,7) rot=(0,0,1;1.5708rad)
  Radius = 13
FEATURE [Part::Box] Box021203  label="Krychle192"
  AttacherType = Attacher::AttachEngine3D
  Height = 5
  Length = 7.4
  Placement = pos=(-12.7,-90.5,7) rot=(0,0,1;0rad)
  Width = 18
FEATURE [Part::Cylinder] Cylinder112024025003003006010004220  label="Válec321"
  Angle = 360
  AttacherType = Attacher::AttachEngine3D
  Height = 5
  Placement = pos=(9,-72.5,7) rot=(0,0,1;0rad)
  Radius = 3.7
FEATURE [Part::Cylinder] Cylinder112024025003003006010004221  label="Válec322"
  Angle = 360
  AttacherType = Attacher::AttachEngine3D
  Height = 13
  Placement = pos=(-25,-23,7) rot=(0,0,1;0rad)
  Radius = 13
FEATURE [Part::Box] Box021204  label="Krychle193"
  AttacherType = Attacher::AttachEngine3D
  Height = 13
  Length = 4.5
  Placement = pos=(20.5,-102,7) rot=(0,0,1;0rad)
  Width = 77
FEATURE [Part::Cylinder] Cylinder112024025003003006010004222  label="Válec323"
  Angle = 360
  AttacherType = Attacher::AttachEngine3D
  Height = 5
  Placement = pos=(9,-90.5,7) rot=(0,0,1;0rad)
  Radius = 3.7
FEATURE [Part::Cylinder] Cylinder112024025003003006010004223  label="sroub003"
  Angle = 360
  AttacherType = Attacher::AttachEngine3D
  Height = 60
  Placement = pos=(-30,-64,14) rot=(0,1,0;1.5708rad)
  Radius = 2.2
FEATURE [Part::Cylinder] Cylinder112024025003003006010004224  label="Válec324"
  Angle = 360
  AttacherType = Attacher::AttachEngine3D
  Height = 13
  Placement = pos=(0,-57.5,7) rot=(0,0,1;0rad)
  Radius = 12
FEATURE [Part::Extrusion] Extrude013
  Base = -> Sketch011
  Dir = (-1,0,0)
  DirMode = 2
  FaceMakerClass = Part::FaceMakerBullseye
  LengthFwd = -3.5
  LengthRev = 0
  Solid = true
  Symmetric = false
FEATURE [Part::MultiFuse] Fusion005043005007002078029  label="Matice011"
  Placement = pos=(-31.5,-118.5,14) rot=(1,0,0;3.14159rad)
  Shapes = -> [Box021202,Extrude013]
FEATURE [Part::Cylinder] Cylinder112024025003003006010004225  label="Válec325"
  Angle = 360
  AttacherType = Attacher::AttachEngine3D
  Height = 5
  Placement = pos=(-9,-72.5,7) rot=(0,0,1;0rad)
  Radius = 3.7
FEATURE [Part::Box] Box021205  label="Krychle194"
  AttacherType = Attacher::AttachEngine3D
  Height = 13
  Length = 24
  Placement = pos=(-12,-57.5,7) rot=(0,0,1;0rad)
  Width = 49
FEATURE [Part::Box] Box021206  label="Krychle195"
  AttacherType = Attacher::AttachEngine3D
  Height = 13
  Length = 4.5
  Placement = pos=(-25,-102,7) rot=(0,0,1;0rad)
  Width = 77
FEATURE [Part::Box] Box021207  label="Krychle196"
  AttacherType = Attacher::AttachEngine3D
  Height = 10
  Length = 3.5
  Placement = pos=(13.5,-58,0) rot=(0,0,1;0rad)
  Width = 7
FEATURE [Sketcher::SketchObject] Sketch010
  MapMode = 5
  Placement = pos=(13.5,-58,0) rot=(0.57735,-0.57735,-0.57735;2.0944rad)
  Support = -> [Box021207]
  sketch-geometry (7):
    g0: LineSegment StartX=-3.5 StartY=4 StartZ=0 EndX=-6.9641 EndY=2 EndZ=0
    g1: LineSegment StartX=-6.9641 StartY=2 StartZ=0 EndX=-6.9641 EndY=-2 EndZ=0
    g2: LineSegment StartX=-6.9641 StartY=-2 StartZ=0 EndX=-3.5 EndY=-4 EndZ=0
    g3: LineSegment StartX=-3.5 StartY=-4 StartZ=0 EndX=-0.0358984 EndY=-2 EndZ=0
    g4: LineSegment StartX=-0.0358984 StartY=-2 StartZ=0 EndX=-0.0358984 EndY=2 EndZ=0
    g5: LineSegment StartX=-0.0358984 StartY=2 StartZ=0 EndX=-3.5 EndY=4 EndZ=0
    g6: Circle [constr] CenterX=-3.5 CenterY=0 CenterZ=0 NormalX=0 NormalY=0 NormalZ=1 AngleXU=0 Radius=4
  constraints (14):
    c: Coincident(g0,g1)
    c: Coincident(g1,g2)
    c: Coincident(g2,g3)
    c: Coincident(g3,g4)
    c: Coincident(g4,g5)
    c: Coincident(g5,g0)
    c: Equal(g0, g1-g5) x5
    c: PointOnObject(g0,g6)
    c: PointOnObject(g1,g6)
    c: PointOnObject(g2,g6)
    c: PointOnObject(g3,g6)
    c: PointOnObject(g4,g6)
    c: PointOnObject(g5,g6)
    c: PointOnObject(g6,g-1)
FEATURE [Part::Extrusion] Extrude012
  Base = -> Sketch010
  Dir = (-1,0,0)
  DirMode = 2
  FaceMakerClass = Part::FaceMakerBullseye
  LengthFwd = -3.5
  LengthRev = 0
  Solid = true
  Symmetric = false
FEATURE [Part::MultiFuse] Fusion005043005007002078028  label="Matice010"
  Placement = pos=(1,-118.5,14) rot=(1,0,0;3.14159rad)
  Shapes = -> [Box021207,Extrude012]
FEATURE [Part::MultiFuse] Fusion005043005007002078027  label="Holes007"
  Shapes = -> [Box021206,Box021204,Cylinder112024025003003006010004223,Cylinder112024025003003006010004224,Box021205,Box021203,Box021201,Cylinder112024025003003006010004220,Cylinder112024025003003006010004222,Cylinder112024025003003006010004225,Cylinder112024025003003006010004218,Fusion005043005007002078028,Fusion005043005007002078029]
FEATURE [Part::Box] Box021208  label="Krychle197"
  AttacherType = Attacher::AttachEngine3D
  Height = 13
  Length = 13
  Placement = pos=(25,-36,7) rot=(0,0,1;0rad)
  Width = 26
FEATURE [Part::Box] Box021209  label="Krychle198"
  AttacherType = Attacher::AttachEngine3D
  Height = 13
  Length = 13
  Placement = pos=(-38,-36,7) rot=(0,0,1;0rad)
  Width = 26
FEATURE [Part::MultiFuse] Fusion005043005007002078030
  Shapes = -> [Cylinder112024025003003006010004221,Cylinder112024025003003006010004219]
FEATURE [Part::MultiFuse] Fusion005043005007002078031
  Shapes = -> [Box021208,Box021209]
FEATURE [Part::Cut] Cut018020020009027020002003004004026003005007008
  Base = -> Fusion005043005007002078030
  Tool = -> Fusion005043005007002078031
FEATURE [Part::MultiFuse] Fusion005043005007002078026  label="Main003"
  Shapes = -> [Box021199,Box021200,Cut018020020009027020002003004004026003005007008]
FEATURE [Part::Cut] Cut018020020009027020002003004004026003005007007  label="EAF_H002"
  Base = -> Fusion005043005007002078026
  Tool = -> Fusion005043005007002078027
FEATURE [Part::Box] Box021210  label="Krychle199"
  AttacherType = Attacher::AttachEngine3D
  Height = 13
  Length = 50
  Placement = pos=(-25,-96,7) rot=(0,0,1;0rad)
  Width = 116
FEATURE [Part::Box] Box021211  label="Krychle200"
  AttacherType = Attacher::AttachEngine3D
  Height = 27
  Length = 50
  Placement = pos=(-25,-25,-20) rot=(0.995037,0,0.099504;0rad)
  Width = 45
FEATURE [Part::MultiFuse] Fusion005043005007002078040  label="Main004"
  Shapes = -> [Box021211,Box021210]
FEATURE [Part::Cylinder] Cylinder112024025003003006010004226  label="Válec326"
  Angle = 360
  AttacherType = Attacher::AttachEngine3D
  Height = 16
  Placement = pos=(0,0,-15) rot=(0,0,1;0rad)
  Radius = 14.5
FEATURE [Part::Cylinder] Cylinder112024025003003006010004229  label="Válec329"
  Angle = 360
  AttacherType = Attacher::AttachEngine3D
  Height = 41
  Placement = pos=(0,0,-21) rot=(0,0,1;0rad)
  Radius = 14.7
FEATURE [Part::Box] Box021212  label="Krychle201"
  AttacherType = Attacher::AttachEngine3D
  Height = 50
  Length = 32
  Placement = pos=(-16,-14,-65) rot=(0,0,1;0rad)
  Width = 16
FEATURE [Part::Box] Box021213  label="Krychle202"
  AttacherType = Attacher::AttachEngine3D
  Height = 20
  Length = 30
  Placement = pos=(-15,-25,-36) rot=(0,0,1;0rad)
  Width = 14
FEATURE [Part::Cylinder] Cylinder112024025003003006010004235  label="Velky002"
  Angle = 360
  AttacherType = Attacher::AttachEngine3D
  Height = 53
  Placement = pos=(-27,27,-44.5) rot=(0,1,0;1.5708rad)
  Radius = 41.5
FEATURE [Part::MultiFuse] Fusion005043005007002078032  label="Tělo002"
  Shapes = -> [Box021212,Cylinder112024025003003006010004235,Cylinder112024025003003006010004226]
FEATURE [Part::Box] Box021214  label="Krychle203"
  AttacherType = Attacher::AttachEngine3D
  Height = 13
  Length = 4.5
  Placement = pos=(-25,-102,7) rot=(0,0,1;0rad)
  Width = 77
FEATURE [Part::Box] Box021215  label="Krychle204"
  AttacherType = Attacher::AttachEngine3D
  Height = 13
  Length = 4.5
  Placement = pos=(20.5,-102,7) rot=(0,0,1;0rad)
  Width = 77
FEATURE [Part::Cylinder] Cylinder112024025003003006010004236  label="sroub004"
  Angle = 360
  AttacherType = Attacher::AttachEngine3D
  Height = 60
  Placement = pos=(-30,-64,14) rot=(0,1,0;1.5708rad)
  Radius = 2.2
FEATURE [Part::Box] Box021216  label="Krychle205"
  AttacherType = Attacher::AttachEngine3D
  Height = 13
  Length = 24
  Placement = pos=(-12,-57.5,7) rot=(0,0,1;0rad)
  Width = 49
FEATURE [Part::Cylinder] Cylinder112024025003003006010004237  label="Válec334"
  Angle = 360
  AttacherType = Attacher::AttachEngine3D
  Height = 13
  Placement = pos=(0,-57.5,7) rot=(0,0,1;0rad)
  Radius = 12
FEATURE [Part::Fillet] Fillet028003004
  Base = -> Fusion005043005007002078040
  Edges = 4 edges r=20: [Edge3,Edge10,Edge13,Edge23]
FEATURE [Part::MultiFuse] Fusion005043005007002078038  label="Body005"
  Shapes = -> [Box021213,Fillet028003004]
FEATURE [Part::Box] Box021217  label="Krychle206"
  AttacherType = Attacher::AttachEngine3D
  Height = 5
  Length = 7.4
  Placement = pos=(-12.7,-90.5,7) rot=(0,0,1;0rad)
  Width = 18
FEATURE [Part::Cylinder] Cylinder112024025003003006010004238  label="Válec335"
  Angle = 360
  AttacherType = Attacher::AttachEngine3D
  Height = 14
  Placement = pos=(0,0,6) rot=(0,0,1;0rad)
  Radius = 16.25
FEATURE [Part::Cylinder] Cylinder112024025003003006010004239  label="Válec336"
  Angle = 360
  AttacherType = Attacher::AttachEngine3D
  Height = 5
  Placement = pos=(9,-90.5,7) rot=(0,0,1;0rad)
  Radius = 3.7
FEATURE [Part::Box] Box021218  label="Krychle207"
  AttacherType = Attacher::AttachEngine3D
  Height = 10
  Length = 3.5
  Placement = pos=(13.5,-58,0) rot=(0,0,1;0rad)
  Width = 7
FEATURE [Sketcher::SketchObject] Sketch012
  MapMode = 5
  Placement = pos=(13.5,-58,0) rot=(0.57735,-0.57735,-0.57735;2.0944rad)
  Support = -> [Box021218]
  sketch-geometry (7):
    g0: LineSegment StartX=-3.5 StartY=4 StartZ=0 EndX=-6.9641 EndY=2 EndZ=0
    g1: LineSegment StartX=-6.9641 StartY=2 StartZ=0 EndX=-6.9641 EndY=-2 EndZ=0
    g2: LineSegment StartX=-6.9641 StartY=-2 StartZ=0 EndX=-3.5 EndY=-4 EndZ=0
    g3: LineSegment StartX=-3.5 StartY=-4 StartZ=0 EndX=-0.0358984 EndY=-2 EndZ=0
    g4: LineSegment StartX=-0.0358984 StartY=-2 StartZ=0 EndX=-0.0358984 EndY=2 EndZ=0
    g5: LineSegment StartX=-0.0358984 StartY=2 StartZ=0 EndX=-3.5 EndY=4 EndZ=0
    g6: Circle [constr] CenterX=-3.5 CenterY=0 CenterZ=0 NormalX=0 NormalY=0 NormalZ=1 AngleXU=0 Radius=4
  constraints (14):
    c: Coincident(g0,g1)
    c: Coincident(g1,g2)
    c: Coincident(g2,g3)
    c: Coincident(g3,g4)
    c: Coincident(g4,g5)
    c: Coincident(g5,g0)
    c: Equal(g0, g1-g5) x5
    c: PointOnObject(g0,g6)
    c: PointOnObject(g1,g6)
    c: PointOnObject(g2,g6)
    c: PointOnObject(g3,g6)
    c: PointOnObject(g4,g6)
    c: PointOnObject(g5,g6)
    c: PointOnObject(g6,g-1)
FEATURE [Part::Box] Box021219  label="Krychle208"
  AttacherType = Attacher::AttachEngine3D
  Height = 5
  Length = 7.4
  Placement = pos=(5.3,-90.5,7) rot=(0,0,1;0rad)
  Width = 18
FEATURE [Part::Box] Box021220  label="Krychle209"
  AttacherType = Attacher::AttachEngine3D
  Height = 10
  Length = 3.5
  Placement = pos=(13.5,-58,0) rot=(0,0,1;0rad)
  Width = 7
FEATURE [Sketcher::SketchObject] Sketch013
  MapMode = 5
  Placement = pos=(13.5,-58,0) rot=(0.57735,-0.57735,-0.57735;2.0944rad)
  Support = -> [Box021220]
  sketch-geometry (7):
    g0: LineSegment StartX=-3.5 StartY=4 StartZ=0 EndX=-6.9641 EndY=2 EndZ=0
    g1: LineSegment StartX=-6.9641 StartY=2 StartZ=0 EndX=-6.9641 EndY=-2 EndZ=0
    g2: LineSegment StartX=-6.9641 StartY=-2 StartZ=0 EndX=-3.5 EndY=-4 EndZ=0
    g3: LineSegment StartX=-3.5 StartY=-4 StartZ=0 EndX=-0.0358984 EndY=-2 EndZ=0
    g4: LineSegment StartX=-0.0358984 StartY=-2 StartZ=0 EndX=-0.0358984 EndY=2 EndZ=0
    g5: LineSegment StartX=-0.0358984 StartY=2 StartZ=0 EndX=-3.5 EndY=4 EndZ=0
    g6: Circle [constr] CenterX=-3.5 CenterY=0 CenterZ=0 NormalX=0 NormalY=0 NormalZ=1 AngleXU=0 Radius=4
  constraints (14):
    c: Coincident(g0,g1)
    c: Coincident(g1,g2)
    c: Coincident(g2,g3)
    c: Coincident(g3,g4)
    c: Coincident(g4,g5)
    c: Coincident(g5,g0)
    c: Equal(g0, g1-g5) x5
    c: PointOnObject(g0,g6)
    c: PointOnObject(g1,g6)
    c: PointOnObject(g2,g6)
    c: PointOnObject(g3,g6)
    c: PointOnObject(g4,g6)
    c: PointOnObject(g5,g6)
    c: PointOnObject(g6,g-1)
FEATURE [Part::Cylinder] Cylinder112024025003003006010004240  label="Válec337"
  Angle = 360
  AttacherType = Attacher::AttachEngine3D
  Height = 5
  Placement = pos=(-9,-72.5,7) rot=(0,0,1;0rad)
  Radius = 3.7
FEATURE [Part::Extrusion] Extrude014
  Base = -> Sketch012
  Dir = (-1,0,0)
  DirMode = 2
  FaceMakerClass = Part::FaceMakerBullseye
  LengthFwd = -3.5
  LengthRev = 0
  Solid = true
  Symmetric = false
FEATURE [Part::MultiFuse] Fusion005043005007002078036  label="Matice012"
  Placement = pos=(1,-118.5,14) rot=(1,0,0;3.14159rad)
  Shapes = -> [Box021218,Extrude014]
FEATURE [Part::Cylinder] Cylinder112024025003003006010004241  label="Válec338"
  Angle = 360
  AttacherType = Attacher::AttachEngine3D
  Height = 5
  Placement = pos=(9,-72.5,7) rot=(0,0,1;0rad)
  Radius = 3.7
FEATURE [Part::Extrusion] Extrude015
  Base = -> Sketch013
  Dir = (-1,0,0)
  DirMode = 2
  FaceMakerClass = Part::FaceMakerBullseye
  LengthFwd = -3.5
  LengthRev = 0
  Solid = true
  Symmetric = false
FEATURE [Part::MultiFuse] Fusion005043005007002078039  label="Matice014"
  Placement = pos=(-31.5,-118.5,14) rot=(1,0,0;3.14159rad)
  Shapes = -> [Box021220,Extrude015]
FEATURE [Part::Cylinder] Cylinder112024025003003006010004242  label="Válec339"
  Angle = 360
  AttacherType = Attacher::AttachEngine3D
  Height = 5
  Placement = pos=(-9,-90.5,7) rot=(0,0,1;0rad)
  Radius = 3.7
FEATURE [Part::Box] Box021221  label="Krychle210"
  AttacherType = Attacher::AttachEngine3D
  Height = 10
  Length = 3.5
  Placement = pos=(13.5,-58,0) rot=(0,0,1;0rad)
  Width = 7
FEATURE [Sketcher::SketchObject] Sketch014
  MapMode = 5
  Placement = pos=(13.5,-58,0) rot=(0.57735,-0.57735,-0.57735;2.0944rad)
  Support = -> [Box021221]
  sketch-geometry (7):
    g0: LineSegment StartX=-3.5 StartY=4 StartZ=0 EndX=-6.9641 EndY=2 EndZ=0
    g1: LineSegment StartX=-6.9641 StartY=2 StartZ=0 EndX=-6.9641 EndY=-2 EndZ=0
    g2: LineSegment StartX=-6.9641 StartY=-2 StartZ=0 EndX=-3.5 EndY=-4 EndZ=0
    g3: LineSegment StartX=-3.5 StartY=-4 StartZ=0 EndX=-0.0358984 EndY=-2 EndZ=0
    g4: LineSegment StartX=-0.0358984 StartY=-2 StartZ=0 EndX=-0.0358984 EndY=2 EndZ=0
    g5: LineSegment StartX=-0.0358984 StartY=2 StartZ=0 EndX=-3.5 EndY=4 EndZ=0
    g6: Circle [constr] CenterX=-3.5 CenterY=0 CenterZ=0 NormalX=0 NormalY=0 NormalZ=1 AngleXU=0 Radius=4
  constraints (14):
    c: Coincident(g0,g1)
    c: Coincident(g1,g2)
    c: Coincident(g2,g3)
    c: Coincident(g3,g4)
    c: Coincident(g4,g5)
    c: Coincident(g5,g0)
    c: Equal(g0, g1-g5) x5
    c: PointOnObject(g0,g6)
    c: PointOnObject(g1,g6)
    c: PointOnObject(g2,g6)
    c: PointOnObject(g3,g6)
    c: PointOnObject(g4,g6)
    c: PointOnObject(g5,g6)
    c: PointOnObject(g6,g-1)
FEATURE [Part::Cylinder] Cylinder112024025003003006010004243  label="Sroub2"
  Angle = 360
  AttacherType = Attacher::AttachEngine3D
  Height = 60
  Placement = pos=(-30,0,-7) rot=(0,1,0;1.5708rad)
  Radius = 2.2
FEATURE [Part::Extrusion] Extrude016
  Base = -> Sketch014
  Dir = (-1,0,0)
  DirMode = 2
  FaceMakerClass = Part::FaceMakerBullseye
  LengthFwd = -3.5
  LengthRev = 0
  Solid = true
  Symmetric = false
FEATURE [Part::MultiFuse] Fusion005043005007002078037  label="Matice013"
  Placement = pos=(5,-27.5,-54) rot=(1,0,0;4.18879rad)
  Shapes = -> [Box021221,Extrude016]
FEATURE [Part::Box] Box021223  label="Krychle212"
  AttacherType = Attacher::AttachEngine3D
  Height = 10
  Length = 3.5
  Placement = pos=(13.5,-58,0) rot=(0,0,1;0rad)
  Width = 7
FEATURE [Sketcher::SketchObject] Sketch015
  MapMode = 5
  Placement = pos=(13.5,-58,0) rot=(0.57735,-0.57735,-0.57735;2.0944rad)
  Support = -> [Box021223]
  sketch-geometry (7):
    g0: LineSegment StartX=-3.5 StartY=4 StartZ=0 EndX=-6.9641 EndY=2 EndZ=0
    g1: LineSegment StartX=-6.9641 StartY=2 StartZ=0 EndX=-6.9641 EndY=-2 EndZ=0
    g2: LineSegment StartX=-6.9641 StartY=-2 StartZ=0 EndX=-3.5 EndY=-4 EndZ=0
    g3: LineSegment StartX=-3.5 StartY=-4 StartZ=0 EndX=-0.0358984 EndY=-2 EndZ=0
    g4: LineSegment StartX=-0.0358984 StartY=-2 StartZ=0 EndX=-0.0358984 EndY=2 EndZ=0
    g5: LineSegment StartX=-0.0358984 StartY=2 StartZ=0 EndX=-3.5 EndY=4 EndZ=0
    g6: Circle [constr] CenterX=-3.5 CenterY=0 CenterZ=0 NormalX=0 NormalY=0 NormalZ=1 AngleXU=0 Radius=4
  constraints (14):
    c: Coincident(g0,g1)
    c: Coincident(g1,g2)
    c: Coincident(g2,g3)
    c: Coincident(g3,g4)
    c: Coincident(g4,g5)
    c: Coincident(g5,g0)
    c: Equal(g0, g1-g5) x5
    c: PointOnObject(g0,g6)
    c: PointOnObject(g1,g6)
    c: PointOnObject(g2,g6)
    c: PointOnObject(g3,g6)
    c: PointOnObject(g4,g6)
    c: PointOnObject(g5,g6)
    c: PointOnObject(g6,g-1)
FEATURE [Part::Extrusion] Extrude017
  Base = -> Sketch015
  Dir = (-1,0,0)
  DirMode = 2
  FaceMakerClass = Part::FaceMakerBullseye
  LengthFwd = -3.5
  LengthRev = 0
  Solid = true
  Symmetric = false
FEATURE [Part::MultiFuse] Fusion005043005007002078041  label="Matice015"
  Placement = pos=(-35,-27.5,-54) rot=(1,0,0;4.18879rad)
  Shapes = -> [Box021223,Extrude017]
FEATURE [Part::MultiFuse] Fusion005043005007002078035  label="Holes008"
  Shapes = -> [Cylinder112024025003003006010004229,Box021214,Box021215,Cylinder112024025003003006010004236,Cylinder112024025003003006010004237,Box021216,Box021217,Box021219,Cylinder112024025003003006010004241,Cylinder112024025003003006010004239,Cylinder112024025003003006010004240,Cylinder112024025003003006010004242,Cylinder112024025003003006010004238,Fusion005043005007002078036,Fusion005043005007002078039,+4 more]
FEATURE [Part::Cut] Cut018020020009027020002003004004026003005007010  label="GSO "
  Base = -> Fusion005043005007002078038
  Tool = -> Fusion005043005007002078035
FEATURE [Part::Feature] Fusion005043005007002078052
  Placement = pos=(0,0,0) rot=(0,0,1;1.0472rad)
  shape: bbox 14.1 x 5.782 x 17 mm, 9 faces, 3 solids (baked)
FEATURE [Part::Feature] Fusion005043005007002078053
  Placement = pos=(0,0,0) rot=(0,0,1;2.0944rad)
  shape: bbox 10.6 x 11.86 x 17 mm, 9 faces, 3 solids (baked)
FEATURE [Part::Feature] Fusion005043005007002078054
  Placement = pos=(0,0,0) rot=(0,0,1;4.18879rad)
  shape: bbox 14.1 x 5.782 x 17 mm, 9 faces, 3 solids (baked)
FEATURE [Part::Feature] Cylinder112024025003003006010004262  label="Válec359"
  Placement = pos=(0,0,0) rot=(0,0,1;0.698132rad)
  shape: bbox 4 x 4 x 17 mm, 3 faces (baked)
FEATURE [Part::Feature] Fusion005043005007002078055
  Placement = pos=(0,0,0) rot=(0,0,1;3.14159rad)
  shape: bbox 7.509 x 13.64 x 17 mm, 9 faces, 3 solids (baked)
FEATURE [Part::Feature] Fusion005043005007002078056
  Placement = pos=(0,0,0) rot=(0,0,-1;1.0472rad)
  shape: bbox 10.6 x 11.86 x 17 mm, 9 faces, 3 solids (baked)
FEATURE [Part::Feature] Cylinder112024025003003006010004263  label="Válec360"
  Placement = pos=(0,0,0) rot=(0,0,1;0.349066rad)
  shape: bbox 4 x 4 x 17 mm, 3 faces (baked)
FEATURE [Part::Cylinder] Cylinder112024025003003006010004264  label="Válec361"
  Angle = 360
  AttacherType = Attacher::AttachEngine3D
  Height = 17
  Placement = pos=(15,0,36) rot=(0,0,1;0rad)
  Radius = 2
FEATURE [Part::MultiFuse] Fusion005043005007002078057
  Shapes = -> [Cylinder112024025003003006010004264,Cylinder112024025003003006010004263,Cylinder112024025003003006010004262]
FEATURE [Part::Feature] difference001007  label="PulleyGSO"
  Placement = pos=(0,0,12.5) rot=(0,0,1;0rad)
  shape: bbox 27.96 x 27.96 x 23.5 mm, 1072 faces (baked)
FEATURE [Part::Cylinder] Cylinder112024025003003006010004276  label="imbus"
  Angle = 360
  AttacherType = Attacher::AttachEngine3D
  Height = 10
  Placement = pos=(0,-8,19.5) rot=(1,0,0;1.5708rad)
  Radius = 2.9
FEATURE [Part::Feature] Cylinder112024025003003006010004276001  label="imbus001"
  Placement = pos=(0,0,0) rot=(0,0,1;2.0944rad)
  shape: bbox 11.56 x 10.02 x 5.8 mm, 3 faces (baked)
FEATURE [Part::Feature] Cylinder112024025003003006010004276002  label="imbus002"
  Placement = pos=(0,0,0) rot=(0,0,1;4.18879rad)
  shape: bbox 11.56 x 10.02 x 5.8 mm, 3 faces (baked)
FEATURE [Part::Cylinder] Cylinder112024025003003006010004276003  label="staff"
  Angle = 360
  AttacherType = Attacher::AttachEngine3D
  Height = 30
  Placement = pos=(0,0,12) rot=(0,0,1;0rad)
  Radius = 2.6
FEATURE [Part::Cylinder] Cylinder112024025003003006010004276004  label="valecspodni001"
  Angle = 360
  AttacherType = Attacher::AttachEngine3D
  Height = 10
  Placement = pos=(0,0,15) rot=(0.707107,0,0.707107;0rad)
  Radius = 14
FEATURE [Part::Cylinder] Cylinder112024025003003006010004276005  label="valecspodni002"
  Angle = 360
  AttacherType = Attacher::AttachEngine3D
  Height = 10
  Placement = pos=(0,0,15) rot=(0.707107,0,0.707107;0rad)
  Radius = 9
FEATURE [Part::Cut] Cut018020020009027020002003004004026003005007011  label="Valecspodni"
  Base = -> Cylinder112024025003003006010004276004
  Tool = -> Cylinder112024025003003006010004276005
FEATURE [Part::Cylinder] Cylinder112024025003003006010004276006  label="Valec horni001"
  Angle = 360
  AttacherType = Attacher::AttachEngine3D
  Height = 18
  Placement = pos=(0,0,36) rot=(0,0,1;0rad)
  Radius = 14
FEATURE [Part::Fillet] Fillet028003005
  Base = -> Cylinder112024025003003006010004276006
  Edges = 1 edges r=2: [Edge1]
FEATURE [Part::MultiFuse] Fusion005043005007002078059  label="PulejMain"
  Shapes = -> [difference001007,Cut018020020009027020002003004004026003005007011,Fillet028003005]
FEATURE [Part::Cylinder] Cylinder112024025003003006010004276007  label="Válec362"
  Angle = 360
  AttacherType = Attacher::AttachEngine3D
  Height = 4
  Placement = pos=(0,0,10) rot=(0,0,1;0rad)
  Radius = 4.2
FEATURE [Part::MultiFuse] Fusion005043005007002078058  label="DiryGSOP"
  Shapes = -> [Fusion005043005007002078057,Fusion005043005007002078052,Fusion005043005007002078053,Fusion005043005007002078054,Fusion005043005007002078056,Fusion005043005007002078055,Cylinder112024025003003006010004276,Cylinder112024025003003006010004276001,Cylinder112024025003003006010004276002,Cylinder112024025003003006010004276003,Cylinder112024025003003006010004276007]
FEATURE [Part::Cut] Cut018020020009027020002003004004026003005007012  label="GSO puley"
  Base = -> Fusion005043005007002078059
  Placement = pos=(0,0,-16) rot=(0,0,1;0rad)
  Tool = -> Fusion005043005007002078058
FEATURE [Part::Cylinder] Cylinder112024025003003006010004232  label="Válec331"
  Angle = 360
  AttacherType = Attacher::AttachEngine3D
  Height = 20
  Placement = pos=(-8,-5,-27) rot=(1,0,0;1.5708rad)
  Radius = 1.7
FEATURE [Part::Cylinder] Cylinder112024025003003006010004233  label="Válec332"
  Angle = 360
  AttacherType = Attacher::AttachEngine3D
  Height = 20
  Placement = pos=(8,-5,-27) rot=(1,0,0;1.5708rad)
  Radius = 1.7
FEATURE [Part::Cylinder] Cylinder112024025003003006010004227  label="Válec327"
  Angle = 360
  AttacherType = Attacher::AttachEngine3D
  Height = 5
  Placement = pos=(8,-20,-27) rot=(1,0,0;1.5708rad)
  Radius = 3
FEATURE [Part::Cylinder] Cylinder112024025003003006010004234  label="Válec333"
  Angle = 360
  AttacherType = Attacher::AttachEngine3D
  Height = 5
  Placement = pos=(-8,-20,-27) rot=(1,0,0;1.5708rad)
  Radius = 3
FEATURE [Part::MultiFuse] Fusion005043005007002078034  label="Inbus001"
  Shapes = -> [Cylinder112024025003003006010004232,Cylinder112024025003003006010004233,Cylinder112024025003003006010004227,Cylinder112024025003003006010004234]
FEATURE [Part::Box] Box021225  label="Krychle214"
  AttacherType = Attacher::AttachEngine3D
  Height = 20
  Length = 30
  Placement = pos=(-15,-11.5,-36.5) rot=(1,0,0;0.174533rad)
  Width = 5
FEATURE [Part::Box] Box021226  label="Krychle215"
  AttacherType = Attacher::AttachEngine3D
  Height = 20
  Length = 30
  Placement = pos=(-15,-25,-36) rot=(0,0,1;0rad)
  Width = 14
FEATURE [Part::MultiFuse] Fusion005043005007002078060  label="GSO 001"
  Shapes = -> [Box021226,Cut018020020009027020002003004004026003005007010]
FEATURE [Part::Cylinder] Cylinder112024025003003006010004276008  label="Válec363"
  Angle = 360
  AttacherType = Attacher::AttachEngine3D
  Height = 43
  Placement = pos=(0,0,-21) rot=(0,0,1;0rad)
  Radius = 15.5
FEATURE [Part::Cylinder] Cylinder112024025003003006010004276009  label="Válec364"
  Angle = 360
  AttacherType = Attacher::AttachEngine3D
  Height = 14
  Placement = pos=(0,0,6.5) rot=(0,0,1;0rad)
  Radius = 17
FEATURE [Part::MultiFuse] Fusion005043005007002078061  label="Diry in"
  Shapes = -> [Box021225,Fusion005043005007002078034,Cylinder112024025003003006010004276008,Cylinder112024025003003006010004276009]
FEATURE [Part::Cut] Cut018020020009027020002003004004026003005007013
  Base = -> Fusion005043005007002078060
  Tool = -> Fusion005043005007002078061
FEATURE [Part::Fillet] Fillet028003006  label="GSO_EAF"
  Base = -> Cut018020020009027020002003004004026003005007013
  Edges = 16 edges: [Edge89 r=0.4,Edge167 r=1,Edge197 r=1,Edge218 r=1,Edge220 r=1,Edge222 r=1,Edge227 r=1,Edge240 r=1,Edge243 r=1,Edge244 r=1,Edge245 r=1,Edge246 r=1,Edge247 r=1,Edge248 r=1,Edge249 r=1,Edge317 r=0.4]
FEATURE [Part::Cylinder] Cylinder112024025003003006010004276010  label="Válec365"
  Angle = 360
  AttacherType = Attacher::AttachEngine3D
  Height = 41
  Placement = pos=(0,0,-21) rot=(0,0,1;0rad)
  Radius = 18
FEATURE [Part::Box] Box021227  label="Krychle216"
  AttacherType = Attacher::AttachEngine3D
  Height = 50
  Length = 32
  Placement = pos=(-16,-14,-65) rot=(0,0,1;0rad)
  Width = 16
FEATURE [Part::Box] Box021228  label="Krychle217"
  AttacherType = Attacher::AttachEngine3D
  Height = 13
  Length = 50
  Placement = pos=(-25,-96,7) rot=(0,0,1;0rad)
  Width = 96
FEATURE [Part::Cylinder] Cylinder112024025003003006010004276011  label="Velky003"
  Angle = 360
  AttacherType = Attacher::AttachEngine3D
  Height = 53
  Placement = pos=(-27,27,-44.5) rot=(0,1,0;1.5708rad)
  Radius = 41.5
FEATURE [Part::Box] Box021229  label="Krychle218"
  AttacherType = Attacher::AttachEngine3D
  Height = 13
  Length = 4.5
  Placement = pos=(20.5,-102,7) rot=(0,0,1;0rad)
  Width = 77
FEATURE [Part::Cylinder] Cylinder112024025003003006010004276012  label="sroub005"
  Angle = 360
  AttacherType = Attacher::AttachEngine3D
  Height = 60
  Placement = pos=(-30,-64,13) rot=(0,1,0;1.5708rad)
  Radius = 2.2
FEATURE [Part::Box] Box021231  label="Krychle220"
  AttacherType = Attacher::AttachEngine3D
  Height = 13
  Length = 4.5
  Placement = pos=(-25,-102,7) rot=(0,0,1;0rad)
  Width = 77
FEATURE [Part::Cylinder] Cylinder112024025003003006010004276013  label="Válec366"
  Angle = 360
  AttacherType = Attacher::AttachEngine3D
  Height = 16
  Placement = pos=(0,0,-15) rot=(0,0,1;0rad)
  Radius = 14.5
FEATURE [Part::MultiFuse] Fusion005043005007002078072  label="Tělo003"
  Placement = pos=(0,0,0) rot=(0,0,1;1.5708rad)
  Shapes = -> [Box021227,Cylinder112024025003003006010004276011,Cylinder112024025003003006010004276013]
FEATURE [Part::Cylinder] Cylinder112024025003003006010004276014  label="Válec367"
  Angle = 360
  AttacherType = Attacher::AttachEngine3D
  Height = 5
  Placement = pos=(-9,-90.5,15) rot=(0,0,1;0rad)
  Radius = 3.7
FEATURE [Part::Cylinder] Cylinder112024025003003006010004276015  label="Válec368"
  Angle = 360
  AttacherType = Attacher::AttachEngine3D
  Height = 5
  Placement = pos=(9,-90.5,15) rot=(0,0,1;0rad)
  Radius = 3.7
FEATURE [Part::Box] Box021233  label="Krychle222"
  AttacherType = Attacher::AttachEngine3D
  Height = 5
  Length = 7.4
  Placement = pos=(-12.7,-90.5,15) rot=(0,0,1;0rad)
  Width = 18
FEATURE [Part::Box] Box021234  label="Krychle223"
  AttacherType = Attacher::AttachEngine3D
  Height = 10
  Length = 3.5
  Placement = pos=(13.5,-58,0) rot=(0,0,1;0rad)
  Width = 7
FEATURE [Sketcher::SketchObject] Sketch016
  MapMode = 5
  Placement = pos=(13.5,-58,0) rot=(0.57735,-0.57735,-0.57735;2.0944rad)
  Support = -> [Box021234]
  sketch-geometry (7):
    g0: LineSegment StartX=-3.5 StartY=4 StartZ=0 EndX=-6.9641 EndY=2 EndZ=0
    g1: LineSegment StartX=-6.9641 StartY=2 StartZ=0 EndX=-6.9641 EndY=-2 EndZ=0
    g2: LineSegment StartX=-6.9641 StartY=-2 StartZ=0 EndX=-3.5 EndY=-4 EndZ=0
    g3: LineSegment StartX=-3.5 StartY=-4 StartZ=0 EndX=-0.0358984 EndY=-2 EndZ=0
    g4: LineSegment StartX=-0.0358984 StartY=-2 StartZ=0 EndX=-0.0358984 EndY=2 EndZ=0
    g5: LineSegment StartX=-0.0358984 StartY=2 StartZ=0 EndX=-3.5 EndY=4 EndZ=0
    g6: Circle [constr] CenterX=-3.5 CenterY=0 CenterZ=0 NormalX=0 NormalY=0 NormalZ=1 AngleXU=0 Radius=4
  constraints (14):
    c: Coincident(g0,g1)
    c: Coincident(g1,g2)
    c: Coincident(g2,g3)
    c: Coincident(g3,g4)
    c: Coincident(g4,g5)
    c: Coincident(g5,g0)
    c: Equal(g0, g1-g5) x5
    c: PointOnObject(g0,g6)
    c: PointOnObject(g1,g6)
    c: PointOnObject(g2,g6)
    c: PointOnObject(g3,g6)
    c: PointOnObject(g4,g6)
    c: PointOnObject(g5,g6)
    c: PointOnObject(g6,g-1)
FEATURE [Part::Extrusion] Extrude019
  Base = -> Sketch016
  Dir = (-1,0,0)
  DirMode = 2
  FaceMakerClass = Part::FaceMakerBullseye
  LengthFwd = -3.5
  LengthRev = 0
  Solid = true
  Symmetric = false
FEATURE [Part::MultiFuse] Fusion005043005007002078067  label="Matice017"
  Placement = pos=(6,-54.5,-10) rot=(1,0,0;3.14159rad)
  Shapes = -> [Box021234,Extrude019]
FEATURE [Part::Cylinder] Cylinder112024025003003006010004276017  label="Sroub003"
  Angle = 360
  AttacherType = Attacher::AttachEngine3D
  Height = 20
  Placement = pos=(10,0,-10) rot=(0,1,0;1.5708rad)
  Radius = 2.2
FEATURE [Part::Box] Box021235  label="Krychle224"
  AttacherType = Attacher::AttachEngine3D
  Height = 10
  Length = 3.5
  Placement = pos=(13.5,-58,0) rot=(0,0,1;0rad)
  Width = 7
FEATURE [Sketcher::SketchObject] Sketch018
  MapMode = 5
  Placement = pos=(13.5,-58,0) rot=(0.57735,-0.57735,-0.57735;2.0944rad)
  Support = -> [Box021235]
  sketch-geometry (7):
    g0: LineSegment StartX=-3.5 StartY=4 StartZ=0 EndX=-6.9641 EndY=2 EndZ=0
    g1: LineSegment StartX=-6.9641 StartY=2 StartZ=0 EndX=-6.9641 EndY=-2 EndZ=0
    g2: LineSegment StartX=-6.9641 StartY=-2 StartZ=0 EndX=-3.5 EndY=-4 EndZ=0
    g3: LineSegment StartX=-3.5 StartY=-4 StartZ=0 EndX=-0.0358984 EndY=-2 EndZ=0
    g4: LineSegment StartX=-0.0358984 StartY=-2 StartZ=0 EndX=-0.0358984 EndY=2 EndZ=0
    g5: LineSegment StartX=-0.0358984 StartY=2 StartZ=0 EndX=-3.5 EndY=4 EndZ=0
    g6: Circle [constr] CenterX=-3.5 CenterY=0 CenterZ=0 NormalX=0 NormalY=0 NormalZ=1 AngleXU=0 Radius=4
  constraints (14):
    c: Coincident(g0,g1)
    c: Coincident(g1,g2)
    c: Coincident(g2,g3)
    c: Coincident(g3,g4)
    c: Coincident(g4,g5)
    c: Coincident(g5,g0)
    c: Equal(g0, g1-g5) x5
    c: PointOnObject(g0,g6)
    c: PointOnObject(g1,g6)
    c: PointOnObject(g2,g6)
    c: PointOnObject(g3,g6)
    c: PointOnObject(g4,g6)
    c: PointOnObject(g5,g6)
    c: PointOnObject(g6,g-1)
FEATURE [Part::Cylinder] Cylinder112024025003003006010004276020  label="Válec372"
  Angle = 360
  AttacherType = Attacher::AttachEngine3D
  Height = 5
  Placement = pos=(-9,-72.5,15) rot=(0,0,1;0rad)
  Radius = 3.7
FEATURE [Part::Cylinder] Cylinder112024025003003006010004276021  label="Válec373"
  Angle = 360
  AttacherType = Attacher::AttachEngine3D
  Height = 13
  Placement = pos=(0,-57.5,7) rot=(0,0,1;0rad)
  Radius = 12
FEATURE [Part::Extrusion] Extrude021
  Base = -> Sketch018
  Dir = (-1,0,0)
  DirMode = 2
  FaceMakerClass = Part::FaceMakerBullseye
  LengthFwd = -3.5
  LengthRev = 0
  Solid = true
  Symmetric = false
FEATURE [Part::MultiFuse] Fusion005043005007002078066  label="Matice016"
  Placement = pos=(1,-118.5,13) rot=(1,0,0;3.14159rad)
  Shapes = -> [Box021235,Extrude021]
FEATURE [Part::Box] Box021236  label="Krychle225"
  AttacherType = Attacher::AttachEngine3D
  Height = 13
  Length = 24
  Placement = pos=(-12,-57.5,7) rot=(0,0,1;0rad)
  Width = 49
FEATURE [Part::Cylinder] Cylinder112024025003003006010004276022  label="Válec374"
  Angle = 360
  AttacherType = Attacher::AttachEngine3D
  Height = 14
  Placement = pos=(0,0,6) rot=(0,0,1;0rad)
  Radius = 16.25
FEATURE [Part::Box] Box021237  label="Krychle226"
  AttacherType = Attacher::AttachEngine3D
  Height = 5
  Length = 7.4
  Placement = pos=(5.3,-90.5,15) rot=(0,0,1;0rad)
  Width = 18
FEATURE [Part::Box] Box021238  label="Krychle227"
  AttacherType = Attacher::AttachEngine3D
  Height = 10
  Length = 3.5
  Placement = pos=(13.5,-58,0) rot=(0,0,1;0rad)
  Width = 7
FEATURE [Sketcher::SketchObject] Sketch019
  MapMode = 5
  Placement = pos=(13.5,-58,0) rot=(0.57735,-0.57735,-0.57735;2.0944rad)
  Support = -> [Box021238]
  sketch-geometry (7):
    g0: LineSegment StartX=-3.5 StartY=4 StartZ=0 EndX=-6.9641 EndY=2 EndZ=0
    g1: LineSegment StartX=-6.9641 StartY=2 StartZ=0 EndX=-6.9641 EndY=-2 EndZ=0
    g2: LineSegment StartX=-6.9641 StartY=-2 StartZ=0 EndX=-3.5 EndY=-4 EndZ=0
    g3: LineSegment StartX=-3.5 StartY=-4 StartZ=0 EndX=-0.0358984 EndY=-2 EndZ=0
    g4: LineSegment StartX=-0.0358984 StartY=-2 StartZ=0 EndX=-0.0358984 EndY=2 EndZ=0
    g5: LineSegment StartX=-0.0358984 StartY=2 StartZ=0 EndX=-3.5 EndY=4 EndZ=0
    g6: Circle [constr] CenterX=-3.5 CenterY=0 CenterZ=0 NormalX=0 NormalY=0 NormalZ=1 AngleXU=0 Radius=4
  constraints (14):
    c: Coincident(g0,g1)
    c: Coincident(g1,g2)
    c: Coincident(g2,g3)
    c: Coincident(g3,g4)
    c: Coincident(g4,g5)
    c: Coincident(g5,g0)
    c: Equal(g0, g1-g5) x5
    c: PointOnObject(g0,g6)
    c: PointOnObject(g1,g6)
    c: PointOnObject(g2,g6)
    c: PointOnObject(g3,g6)
    c: PointOnObject(g4,g6)
    c: PointOnObject(g5,g6)
    c: PointOnObject(g6,g-1)
FEATURE [Part::Extrusion] Extrude018
  Base = -> Sketch019
  Dir = (-1,0,0)
  DirMode = 2
  FaceMakerClass = Part::FaceMakerBullseye
  LengthFwd = -3.5
  LengthRev = 0
  Solid = true
  Symmetric = false
FEATURE [Part::MultiFuse] Fusion005043005007002078071  label="Matice019"
  Placement = pos=(-31.5,-118.5,13) rot=(1,0,0;3.14159rad)
  Shapes = -> [Box021238,Extrude018]
FEATURE [Part::Cylinder] Cylinder112024025003003006010004276023  label="Válec375"
  Angle = 360
  AttacherType = Attacher::AttachEngine3D
  Height = 5
  Placement = pos=(9,-72.5,15) rot=(0,0,1;0rad)
  Radius = 3.7
FEATURE [Part::Box] Box021239  label="Krychle228"
  AttacherType = Attacher::AttachEngine3D
  Height = 10
  Length = 3.5
  Placement = pos=(13.5,-58,0) rot=(0,0,1;0rad)
  Width = 7
FEATURE [Sketcher::SketchObject] Sketch017
  MapMode = 5
  Placement = pos=(13.5,-58,0) rot=(0.57735,-0.57735,-0.57735;2.0944rad)
  Support = -> [Box021239]
  sketch-geometry (7):
    g0: LineSegment StartX=-3.5 StartY=4 StartZ=0 EndX=-6.9641 EndY=2 EndZ=0
    g1: LineSegment StartX=-6.9641 StartY=2 StartZ=0 EndX=-6.9641 EndY=-2 EndZ=0
    g2: LineSegment StartX=-6.9641 StartY=-2 StartZ=0 EndX=-3.5 EndY=-4 EndZ=0
    g3: LineSegment StartX=-3.5 StartY=-4 StartZ=0 EndX=-0.0358984 EndY=-2 EndZ=0
    g4: LineSegment StartX=-0.0358984 StartY=-2 StartZ=0 EndX=-0.0358984 EndY=2 EndZ=0
    g5: LineSegment StartX=-0.0358984 StartY=2 StartZ=0 EndX=-3.5 EndY=4 EndZ=0
    g6: Circle [constr] CenterX=-3.5 CenterY=0 CenterZ=0 NormalX=0 NormalY=0 NormalZ=1 AngleXU=0 Radius=4
  constraints (14):
    c: Coincident(g0,g1)
    c: Coincident(g1,g2)
    c: Coincident(g2,g3)
    c: Coincident(g3,g4)
    c: Coincident(g4,g5)
    c: Coincident(g5,g0)
    c: Equal(g0, g1-g5) x5
    c: PointOnObject(g0,g6)
    c: PointOnObject(g1,g6)
    c: PointOnObject(g2,g6)
    c: PointOnObject(g3,g6)
    c: PointOnObject(g4,g6)
    c: PointOnObject(g5,g6)
    c: PointOnObject(g6,g-1)
FEATURE [Part::Extrusion] Extrude020
  Base = -> Sketch017
  Dir = (-1,0,0)
  DirMode = 2
  FaceMakerClass = Part::FaceMakerBullseye
  LengthFwd = -3.5
  LengthRev = 0
  Solid = true
  Symmetric = false
FEATURE [Part::MultiFuse] Fusion005043005007002078069  label="Matice018"
  Placement = pos=(-36.5,-54.5,1.5) rot=(1,0,0;3.14159rad)
  Shapes = -> [Box021239,Extrude020]
FEATURE [Part::Cylinder] Cylinder112024025003003006010004276024  label="Válec376"
  Angle = 360
  AttacherType = Attacher::AttachEngine3D
  Height = 48
  Placement = pos=(5,0,-28) rot=(0,0,1;0rad)
  Radius = 20
FEATURE [Part::Cylinder] Cylinder112024025003003006010004276025  label="Válec377"
  Angle = 360
  AttacherType = Attacher::AttachEngine3D
  Height = 48
  Placement = pos=(-5,0,-28) rot=(0,0,1;0rad)
  Radius = 20
FEATURE [Part::Box] Box021240  label="Krychle229"
  AttacherType = Attacher::AttachEngine3D
  Height = 48
  Length = 10
  Placement = pos=(-5,-25,-28) rot=(0.995037,0,0.099504;0rad)
  Width = 45
FEATURE [Part::Box] Box021241  label="Krychle230"
  AttacherType = Attacher::AttachEngine3D
  Height = 48
  Length = 50
  Placement = pos=(-25,-5,-28) rot=(0.995037,0,0.099504;0rad)
  Width = 5
FEATURE [Part::Cylinder] Cylinder112024025003003006010004276026  label="Válec378"
  Angle = 360
  AttacherType = Attacher::AttachEngine3D
  Height = 48
  Placement = pos=(-5,-5,-28) rot=(0,0,1;0rad)
  Radius = 20
FEATURE [Part::Cylinder] Cylinder112024025003003006010004276027  label="Válec379"
  Angle = 360
  AttacherType = Attacher::AttachEngine3D
  Height = 48
  Placement = pos=(5,-5,-28) rot=(0,0,1;0rad)
  Radius = 20
FEATURE [Part::MultiFuse] Fusion005043005007002078073  label="Main005"
  Shapes = -> [Box021228,Cylinder112024025003003006010004276025,Box021240,Box021241,Cylinder112024025003003006010004276026,Cylinder112024025003003006010004276027,Cylinder112024025003003006010004276024]
FEATURE [Part::Cylinder] Cylinder112024025003003006010004276028  label="Sroub004"
  Angle = 360
  AttacherType = Attacher::AttachEngine3D
  Height = 20
  Placement = pos=(-35,0,1.5) rot=(0,1,0;1.5708rad)
  Radius = 2.2
FEATURE [Part::MultiFuse] Fusion005043005007002078068  label="Holes009"
  Shapes = -> [Cylinder112024025003003006010004276010,Box021231,Box021229,Cylinder112024025003003006010004276012,Cylinder112024025003003006010004276021,Box021236,Box021233,Box021237,Cylinder112024025003003006010004276023,Cylinder112024025003003006010004276015,Cylinder112024025003003006010004276020,Cylinder112024025003003006010004276014,Cylinder112024025003003006010004276022,Fusion005043005007002078066,+6 more]
FEATURE [Part::Cut] Cut018020020009027020002003004004026003005007014  label="Main006"
  Base = -> Fusion005043005007002078073
  Tool = -> Fusion005043005007002078068
FEATURE [App::Part] Part016  label="PCB"
  Group = -> [Shape,Shape001,Shape002,Shape003,Shape004,Shape005,Shape006,Shape007,Shape008,Shape009,Shape010,Shape011,Shape012,Shape013,Shape014,Shape015,Shape016,Shape017,Shape018,Shape019,Shape020,Shape021,Shape022,Shape023,Shape024,Shape025,Shape026,Shape027,Shape028,Shape029,Shape030,Shape031,Shape032,Shape033,Shape034,Shape035,Shape036,Shape037,Shape038,Shape039,Shape040,Shape041,Shape042,Shape043,+69 more]
  Origin = -> Origin016
  Placement = pos=(-23,45.9,0) rot=(0,0,1;0rad)
FEATURE [Part::Box] Box021242  label="Krychle231"
  AttacherType = Attacher::AttachEngine3D
  Height = 48
  Length = 10
  Placement = pos=(-5,-25,-28) rot=(0.995037,0,0.099504;0rad)
  Width = 50
FEATURE [Part::Box] Box021243  label="Krychle232"
  AttacherType = Attacher::AttachEngine3D
  Height = 13
  Length = 50
  Placement = pos=(-25,-96,7) rot=(0,0,1;0rad)
  Width = 96
FEATURE [Part::Box] Box021244  label="Krychle233"
  AttacherType = Attacher::AttachEngine3D
  Height = 13
  Length = 4.5
  Placement = pos=(20.5,-102,7) rot=(0,0,1;0rad)
  Width = 77
FEATURE [Part::Cylinder] Cylinder112024025003003006010004276030  label="Sroub005"
  Angle = 360
  AttacherType = Attacher::AttachEngine3D
  Height = 20
  Placement = pos=(-30,0,-5) rot=(0,1,0;1.5708rad)
  Radius = 2.2
FEATURE [Part::Cylinder] Cylinder112024025003003006010004276031  label="sroub006"
  Angle = 360
  AttacherType = Attacher::AttachEngine3D
  Height = 60
  Placement = pos=(-30,-64,13) rot=(0,1,0;1.5708rad)
  Radius = 2.2
FEATURE [Part::Box] Box021245  label="Krychle234"
  AttacherType = Attacher::AttachEngine3D
  Height = 10
  Length = 3.5
  Placement = pos=(13.5,-58,0) rot=(0,0,1;0rad)
  Width = 7
FEATURE [Sketcher::SketchObject] Sketch020
  MapMode = 5
  Placement = pos=(13.5,-58,0) rot=(0.57735,-0.57735,-0.57735;2.0944rad)
  Support = -> [Box021245]
  sketch-geometry (7):
    g0: LineSegment StartX=-3.5 StartY=4 StartZ=0 EndX=-6.9641 EndY=2 EndZ=0
    g1: LineSegment StartX=-6.9641 StartY=2 StartZ=0 EndX=-6.9641 EndY=-2 EndZ=0
    g2: LineSegment StartX=-6.9641 StartY=-2 StartZ=0 EndX=-3.5 EndY=-4 EndZ=0
    g3: LineSegment StartX=-3.5 StartY=-4 StartZ=0 EndX=-0.0358984 EndY=-2 EndZ=0
    g4: LineSegment StartX=-0.0358984 StartY=-2 StartZ=0 EndX=-0.0358984 EndY=2 EndZ=0
    g5: LineSegment StartX=-0.0358984 StartY=2 StartZ=0 EndX=-3.5 EndY=4 EndZ=0
    g6: Circle [constr] CenterX=-3.5 CenterY=0 CenterZ=0 NormalX=0 NormalY=0 NormalZ=1 AngleXU=0 Radius=4
  constraints (14):
    c: Coincident(g0,g1)
    c: Coincident(g1,g2)
    c: Coincident(g2,g3)
    c: Coincident(g3,g4)
    c: Coincident(g4,g5)
    c: Coincident(g5,g0)
    c: Equal(g0, g1-g5) x5
    c: PointOnObject(g0,g6)
    c: PointOnObject(g1,g6)
    c: PointOnObject(g2,g6)
    c: PointOnObject(g3,g6)
    c: PointOnObject(g4,g6)
    c: PointOnObject(g5,g6)
    c: PointOnObject(g6,g-1)
FEATURE [Part::Box] Box021246  label="Krychle235"
  AttacherType = Attacher::AttachEngine3D
  Height = 10
  Length = 3.5
  Placement = pos=(13.5,-58,0) rot=(0,0,1;0rad)
  Width = 7
FEATURE [Sketcher::SketchObject] Sketch021
  MapMode = 5
  Placement = pos=(13.5,-58,0) rot=(0.57735,-0.57735,-0.57735;2.0944rad)
  Support = -> [Box021246]
  sketch-geometry (7):
    g0: LineSegment StartX=-3.5 StartY=4 StartZ=0 EndX=-6.9641 EndY=2 EndZ=0
    g1: LineSegment StartX=-6.9641 StartY=2 StartZ=0 EndX=-6.9641 EndY=-2 EndZ=0
    g2: LineSegment StartX=-6.9641 StartY=-2 StartZ=0 EndX=-3.5 EndY=-4 EndZ=0
    g3: LineSegment StartX=-3.5 StartY=-4 StartZ=0 EndX=-0.0358984 EndY=-2 EndZ=0
    g4: LineSegment StartX=-0.0358984 StartY=-2 StartZ=0 EndX=-0.0358984 EndY=2 EndZ=0
    g5: LineSegment StartX=-0.0358984 StartY=2 StartZ=0 EndX=-3.5 EndY=4 EndZ=0
    g6: Circle [constr] CenterX=-3.5 CenterY=0 CenterZ=0 NormalX=0 NormalY=0 NormalZ=1 AngleXU=0 Radius=4
  constraints (14):
    c: Coincident(g0,g1)
    c: Coincident(g1,g2)
    c: Coincident(g2,g3)
    c: Coincident(g3,g4)
    c: Coincident(g4,g5)
    c: Coincident(g5,g0)
    c: Equal(g0, g1-g5) x5
    c: PointOnObject(g0,g6)
    c: PointOnObject(g1,g6)
    c: PointOnObject(g2,g6)
    c: PointOnObject(g3,g6)
    c: PointOnObject(g4,g6)
    c: PointOnObject(g5,g6)
    c: PointOnObject(g6,g-1)
FEATURE [Part::Extrusion] Extrude022
  Base = -> Sketch020
  Dir = (-1,0,0)
  DirMode = 2
  FaceMakerClass = Part::FaceMakerBullseye
  LengthFwd = -3.5
  LengthRev = 0
  Solid = true
  Symmetric = false
FEATURE [Part::MultiFuse] Fusion005043005007002078079  label="Matice020"
  Placement = pos=(1,-118.5,13) rot=(1,0,0;3.14159rad)
  Shapes = -> [Box021245,Extrude022]
FEATURE [Part::Cylinder] Cylinder112024025003003006010004276033  label="Válec382"
  Angle = 360
  AttacherType = Attacher::AttachEngine3D
  Height = 13
  Placement = pos=(0,-57.5,7) rot=(0,0,1;0rad)
  Radius = 12
FEATURE [Part::Box] Box021247  label="Krychle236"
  AttacherType = Attacher::AttachEngine3D
  Height = 20
  Length = 12
  Placement = pos=(-15,-25,-36) rot=(0,0,1;0rad)
  Width = 31
FEATURE [Part::Extrusion] Extrude023
  Base = -> Sketch021
  Dir = (-1,0,0)
  DirMode = 2
  FaceMakerClass = Part::FaceMakerBullseye
  LengthFwd = -3.5
  LengthRev = 0
  Solid = true
  Symmetric = false
FEATURE [Part::MultiFuse] Fusion005043005007002078080  label="Matice021"
  Placement = pos=(-31.5,-118.5,13) rot=(1,0,0;3.14159rad)
  Shapes = -> [Box021246,Extrude023]
FEATURE [Part::Cylinder] Cylinder112024025003003006010004276034  label="Válec383"
  Angle = 360
  AttacherType = Attacher::AttachEngine3D
  Height = 5
  Placement = pos=(-9,-72.5,15) rot=(0,0,1;0rad)
  Radius = 3.7
FEATURE [Part::Box] Box021248  label="Krychle237"
  AttacherType = Attacher::AttachEngine3D
  Height = 5
  Length = 7.4
  Placement = pos=(5.3,-90.5,15) rot=(0,0,1;0rad)
  Width = 18
FEATURE [Part::Box] Box021249  label="Krychle238"
  AttacherType = Attacher::AttachEngine3D
  Height = 13
  Length = 4.5
  Placement = pos=(-25,-102,7) rot=(0,0,1;0rad)
  Width = 77
FEATURE [Part::Cylinder] Cylinder112024025003003006010004276035  label="Válec384"
  Angle = 360
  AttacherType = Attacher::AttachEngine3D
  Height = 50
  Placement = pos=(0,0,-28) rot=(0,0,1;0rad)
  Radius = 18
FEATURE [Part::Box] Box021250  label="Krychle239"
  AttacherType = Attacher::AttachEngine3D
  Height = 5
  Length = 7.4
  Placement = pos=(-12.7,-90.5,15) rot=(0,0,1;0rad)
  Width = 18
FEATURE [Part::Box] Box021251  label="Krychle240"
  AttacherType = Attacher::AttachEngine3D
  Height = 50
  Length = 35
  Placement = pos=(-17.5,-18,-66) rot=(0,0,1;0rad)
  Width = 15
FEATURE [Part::Box] Box021252  label="Krychle241"
  AttacherType = Attacher::AttachEngine3D
  Height = 10
  Length = 3.5
  Placement = pos=(13.5,-58,0) rot=(0,0,1;0rad)
  Width = 7
FEATURE [Sketcher::SketchObject] Sketch022
  MapMode = 5
  Placement = pos=(13.5,-58,0) rot=(0.57735,-0.57735,-0.57735;2.0944rad)
  Support = -> [Box021252]
  sketch-geometry (7):
    g0: LineSegment StartX=-3.5 StartY=4 StartZ=0 EndX=-6.9641 EndY=2 EndZ=0
    g1: LineSegment StartX=-6.9641 StartY=2 StartZ=0 EndX=-6.9641 EndY=-2 EndZ=0
    g2: LineSegment StartX=-6.9641 StartY=-2 StartZ=0 EndX=-3.5 EndY=-4 EndZ=0
    g3: LineSegment StartX=-3.5 StartY=-4 StartZ=0 EndX=-0.0358984 EndY=-2 EndZ=0
    g4: LineSegment StartX=-0.0358984 StartY=-2 StartZ=0 EndX=-0.0358984 EndY=2 EndZ=0
    g5: LineSegment StartX=-0.0358984 StartY=2 StartZ=0 EndX=-3.5 EndY=4 EndZ=0
    g6: Circle [constr] CenterX=-3.5 CenterY=0 CenterZ=0 NormalX=0 NormalY=0 NormalZ=1 AngleXU=0 Radius=4
  constraints (14):
    c: Coincident(g0,g1)
    c: Coincident(g1,g2)
    c: Coincident(g2,g3)
    c: Coincident(g3,g4)
    c: Coincident(g4,g5)
    c: Coincident(g5,g0)
    c: Equal(g0, g1-g5) x5
    c: PointOnObject(g0,g6)
    c: PointOnObject(g1,g6)
    c: PointOnObject(g2,g6)
    c: PointOnObject(g3,g6)
    c: PointOnObject(g4,g6)
    c: PointOnObject(g5,g6)
    c: PointOnObject(g6,g-1)
FEATURE [Part::Cylinder] Cylinder112024025003003006010004276036  label="Válec385"
  Angle = 360
  AttacherType = Attacher::AttachEngine3D
  Height = 5
  Placement = pos=(-9,-90.5,15) rot=(0,0,1;0rad)
  Radius = 3.7
FEATURE [Part::Cylinder] Cylinder112024025003003006010004276037  label="Válec386"
  Angle = 360
  AttacherType = Attacher::AttachEngine3D
  Height = 5
  Placement = pos=(9,-90.5,15) rot=(0,0,1;0rad)
  Radius = 3.7
FEATURE [Part::Box] Box021253  label="Krychle242"
  AttacherType = Attacher::AttachEngine3D
  Height = 13
  Length = 24
  Placement = pos=(-12,-57.5,7) rot=(0,0,1;0rad)
  Width = 49
FEATURE [Part::Cylinder] Cylinder112024025003003006010004276038  label="Velky004"
  Angle = 360
  AttacherType = Attacher::AttachEngine3D
  Height = 53
  Placement = pos=(-27,27,-52.5) rot=(0,1,0;1.5708rad)
  Radius = 43.5
FEATURE [Part::MultiFuse] Fusion005043005007002078074  label="Tělo004"
  Placement = pos=(-2,0,0) rot=(0,0,1;1.5708rad)
  Shapes = -> [Box021251,Cylinder112024025003003006010004276038]
FEATURE [Part::Cylinder] Cylinder112024025003003006010004276039  label="Válec387"
  Angle = 360
  AttacherType = Attacher::AttachEngine3D
  Height = 5
  Placement = pos=(9,-72.5,15) rot=(0,0,1;0rad)
  Radius = 3.7
FEATURE [Part::Extrusion] Extrude025
  Base = -> Sketch022
  Dir = (-1,0,0)
  DirMode = 2
  FaceMakerClass = Part::FaceMakerBullseye
  LengthFwd = -3.5
  LengthRev = 0
  Solid = true
  Symmetric = false
FEATURE [Part::MultiFuse] Fusion005043005007002078083  label="Matice022"
  Placement = pos=(6.25,-54.5,-23) rot=(1,0,0;3.14159rad)
  Shapes = -> [Box021252,Extrude025]
FEATURE [Part::Box] Box021254  label="Krychle243"
  AttacherType = Attacher::AttachEngine3D
  Height = 10
  Length = 3.5
  Placement = pos=(13.5,-58,0) rot=(0,0,1;0rad)
  Width = 7
FEATURE [Part::Cylinder] Cylinder112024025003003006010004276041  label="Válec389"
  Angle = 360
  AttacherType = Attacher::AttachEngine3D
  Height = 5
  Placement = pos=(8,-20,-27) rot=(1,0,0;1.5708rad)
  Radius = 3
FEATURE [Part::Cylinder] Cylinder112024025003003006010004276042  label="Válec390"
  Angle = 360
  AttacherType = Attacher::AttachEngine3D
  Height = 14
  Placement = pos=(0,0,6.5) rot=(0,0,1;0rad)
  Radius = 17
FEATURE [Part::Cylinder] Cylinder112024025003003006010004276043  label="Válec391"
  Angle = 360
  AttacherType = Attacher::AttachEngine3D
  Height = 5
  Placement = pos=(-8,-20,-27) rot=(1,0,0;1.5708rad)
  Radius = 3
FEATURE [Part::Cylinder] Cylinder112024025003003006010004276044  label="Válec392"
  Angle = 360
  AttacherType = Attacher::AttachEngine3D
  Height = 20
  Placement = pos=(8,-5,-27) rot=(1,0,0;1.5708rad)
  Radius = 1.7
FEATURE [Part::Cylinder] Cylinder112024025003003006010004276045  label="Válec393"
  Angle = 360
  AttacherType = Attacher::AttachEngine3D
  Height = 20
  Placement = pos=(-8,-5,-27) rot=(1,0,0;1.5708rad)
  Radius = 1.7
FEATURE [Part::MultiFuse] Fusion005043005007002078076  label="Inbus002"
  Shapes = -> [Cylinder112024025003003006010004276045,Cylinder112024025003003006010004276044,Cylinder112024025003003006010004276041,Cylinder112024025003003006010004276043]
FEATURE [Sketcher::SketchObject] Sketch023
  MapMode = 5
  Placement = pos=(13.5,-58,0) rot=(0.57735,-0.57735,-0.57735;2.0944rad)
  Support = -> [Box021254]
  sketch-geometry (7):
    g0: LineSegment StartX=-3.5 StartY=4 StartZ=0 EndX=-6.9641 EndY=2 EndZ=0
    g1: LineSegment StartX=-6.9641 StartY=2 StartZ=0 EndX=-6.9641 EndY=-2 EndZ=0
    g2: LineSegment StartX=-6.9641 StartY=-2 StartZ=0 EndX=-3.5 EndY=-4 EndZ=0
    g3: LineSegment StartX=-3.5 StartY=-4 StartZ=0 EndX=-0.0358984 EndY=-2 EndZ=0
    g4: LineSegment StartX=-0.0358984 StartY=-2 StartZ=0 EndX=-0.0358984 EndY=2 EndZ=0
    g5: LineSegment StartX=-0.0358984 StartY=2 StartZ=0 EndX=-3.5 EndY=4 EndZ=0
    g6: Circle [constr] CenterX=-3.5 CenterY=0 CenterZ=0 NormalX=0 NormalY=0 NormalZ=1 AngleXU=0 Radius=4
  constraints (14):
    c: Coincident(g0,g1)
    c: Coincident(g1,g2)
    c: Coincident(g2,g3)
    c: Coincident(g3,g4)
    c: Coincident(g4,g5)
    c: Coincident(g5,g0)
    c: Equal(g0, g1-g5) x5
    c: PointOnObject(g0,g6)
    c: PointOnObject(g1,g6)
    c: PointOnObject(g2,g6)
    c: PointOnObject(g3,g6)
    c: PointOnObject(g4,g6)
    c: PointOnObject(g5,g6)
    c: PointOnObject(g6,g-1)
FEATURE [Part::Extrusion] Extrude024
  Base = -> Sketch023
  Dir = (-1,0,0)
  DirMode = 2
  FaceMakerClass = Part::FaceMakerBullseye
  LengthFwd = -3.5
  LengthRev = 0
  Solid = true
  Symmetric = false
FEATURE [Part::MultiFuse] Fusion005043005007002078084  label="Matice023"
  Placement = pos=(-37,-54.5,-5) rot=(1,0,0;3.14159rad)
  Shapes = -> [Box021254,Extrude024]
FEATURE [Part::Cylinder] Cylinder112024025003003006010004276046  label="Válec394"
  Angle = 360
  AttacherType = Attacher::AttachEngine3D
  Height = 48
  Placement = pos=(5,5,-28) rot=(0,0,1;0rad)
  Radius = 20
FEATURE [Part::Cylinder] Cylinder112024025003003006010004276047  label="Válec395"
  Angle = 360
  AttacherType = Attacher::AttachEngine3D
  Height = 48
  Placement = pos=(-5,5,-28) rot=(0,0,1;0rad)
  Radius = 20
FEATURE [Part::Cylinder] Cylinder112024025003003006010004276048  label="Válec396"
  Angle = 360
  AttacherType = Attacher::AttachEngine3D
  Height = 48
  Placement = pos=(5,-5,-28) rot=(0,0,1;0rad)
  Radius = 20
FEATURE [Part::Cylinder] Cylinder112024025003003006010004276049  label="Válec397"
  Angle = 360
  AttacherType = Attacher::AttachEngine3D
  Height = 48
  Placement = pos=(-5,-5,-28) rot=(0,0,1;0rad)
  Radius = 20
FEATURE [Part::Box] Box021257  label="Krychle246"
  AttacherType = Attacher::AttachEngine3D
  Height = 48
  Length = 50
  Placement = pos=(-25,-5,-28) rot=(0.995037,0,0.099504;0rad)
  Width = 10
FEATURE [Part::Cylinder] Cylinder112024025003003006010004276052  label="Sroub007"
  Angle = 360
  AttacherType = Attacher::AttachEngine3D
  Height = 20
  Placement = pos=(15,2.5,-56) rot=(0,1,0;1.5708rad)
  Radius = 2.5
FEATURE [Part::Feature] Fusion005043005007002078086001001  label="M004"
  Placement = pos=(3,43,-6) rot=(0,1,0;0.663225rad)
  shape: bbox 12.88 x 20 x 13.74 mm, 15 faces (baked)
FEATURE [Part::Feature] Fusion005043005007002078086001002  label="M005"
  Placement = pos=(3,0,-6) rot=(0,1,0;0.663225rad)
  shape: bbox 12.88 x 20 x 13.74 mm, 15 faces (baked)
FEATURE [Part::Box] Box021258  label="Krychle247"
  AttacherType = Attacher::AttachEngine3D
  Height = 86
  Length = 9
  Placement = pos=(16,-17.5,-66) rot=(0,0,1;0rad)
  Width = 35
FEATURE [Part::MultiFuse] Fusion005043005007002078075  label="Main007"
  Shapes = -> [Box021242,Box021243,Cylinder112024025003003006010004276046,Cylinder112024025003003006010004276047,Cylinder112024025003003006010004276048,Cylinder112024025003003006010004276049,Box021257,Box021258]
FEATURE [Part::Cylinder] Cylinder112024025003003006010004276053  label="Válec398"
  Angle = 360
  AttacherType = Attacher::AttachEngine3D
  Height = 20
  Placement = pos=(-10,10,-27) rot=(1,0,0;1.5708rad)
  Radius = 1.7
FEATURE [Part::Cylinder] Cylinder112024025003003006010004276054  label="Válec399"
  Angle = 360
  AttacherType = Attacher::AttachEngine3D
  Height = 20
  Placement = pos=(10,10,-27) rot=(1,0,0;1.5708rad)
  Radius = 1.7
FEATURE [Part::Cylinder] Cylinder112024025003003006010004276055  label="Válec400"
  Angle = 360
  AttacherType = Attacher::AttachEngine3D
  Height = 5
  Placement = pos=(10,-8,-27) rot=(1,0,0;1.5708rad)
  Radius = 3
FEATURE [Part::Cylinder] Cylinder112024025003003006010004276056  label="Válec401"
  Angle = 360
  AttacherType = Attacher::AttachEngine3D
  Height = 5
  Placement = pos=(-10,-8,-27) rot=(1,0,0;1.5708rad)
  Radius = 3
FEATURE [Part::MultiFuse] Fusion005043005007002078086001003  label="Inbus003"
  Placement = pos=(12,0,-29) rot=(0,0,1;1.5708rad)
  Shapes = -> [Cylinder112024025003003006010004276053,Cylinder112024025003003006010004276054,Cylinder112024025003003006010004276055,Cylinder112024025003003006010004276056]
FEATURE [Part::Cylinder] Cylinder112024025003003006010004276057  label="Sroub008"
  Angle = 360
  AttacherType = Attacher::AttachEngine3D
  Height = 10
  Placement = pos=(20,2.5,-56) rot=(0,1,0;1.5708rad)
  Radius = 4.2
FEATURE [Part::MultiFuse] Fusion005043005007002078078  label="Holes010"
  Shapes = -> [Cylinder112024025003003006010004276035,Box021249,Box021244,Cylinder112024025003003006010004276031,Cylinder112024025003003006010004276033,Box021253,Box021250,Box021248,Cylinder112024025003003006010004276039,Cylinder112024025003003006010004276037,Cylinder112024025003003006010004276034,Cylinder112024025003003006010004276036,Fusion005043005007002078079,Fusion005043005007002078080,+8 more]
FEATURE [Part::MultiFuse] Fusion005043005007002078081  label="Diry in001"
  Shapes = -> [Cylinder112024025003003006010004276042,Fusion005043005007002078078]
FEATURE [Part::Cut] Cut018020020009027020002003004004026003005007015  label="Ref_EAF_v4"
  Base = -> Fusion005043005007002078075
  Placement = pos=(0,0,0) rot=(1,0,0;3.14159rad)
  Tool = -> Fusion005043005007002078081
FEATURE [App::Part] Part013  label="Newton EAF  V4"
  Group = -> [Cut018020020009027020002003004004026003005007001,Box021145,Box021147,Cylinder112024025003003006010004145,Box021148,Cylinder112024025003003006010004146,Cylinder112024025003003006010004147,Cylinder112024025003003006010004148,Cylinder112024025003003006010004149,Cylinder112024025003003006010004150,Box021149,Cylinder112024025003003006010004151,Cylinder112024025003003006010004152,+88 more]
  Origin = -> Origin013
  Placement = pos=(0,0,25.5) rot=(0,1,0;3.14159rad)
FEATURE [Part::Cylinder] Cylinder112024025003003006010004276058  label="Válec402"
  Angle = 360
  AttacherType = Attacher::AttachEngine3D
  Height = 18
  Placement = pos=(0,0,39) rot=(0,0,1;0rad)
  Radius = 14
FEATURE [Part::Cylinder] Cylinder112024025003003006010004276059  label="Válec403"
  Angle = 360
  AttacherType = Attacher::AttachEngine3D
  Height = 13
  Placement = pos=(0,0,15) rot=(0,0,1;0rad)
  Radius = 14
FEATURE [Part::Cylinder] Cylinder112024025003003006010004276062  label="Válec406"
  Angle = 360
  AttacherType = Attacher::AttachEngine3D
  Height = 18
  Placement = pos=(0,0,7) rot=(0,0,1;0rad)
  Radius = 9.8
FEATURE [Part::Cylinder] Cylinder112024025003003006010004276064  label="Válec408"
  Angle = 360
  AttacherType = Attacher::AttachEngine3D
  Height = 10
  Placement = pos=(-19,0,19.5) rot=(0,1,0;1.5708rad)
  Radius = 3.7
FEATURE [Part::Cylinder] Cylinder112024025003003006010004276065  label="Válec409"
  Angle = 360
  AttacherType = Attacher::AttachEngine3D
  Height = 10
  Placement = pos=(9,0,19.5) rot=(0,1,0;1.5708rad)
  Radius = 3.7
FEATURE [Part::Cylinder] Cylinder112024025003003006010004276067  label="Válec411"
  Angle = 360
  AttacherType = Attacher::AttachEngine3D
  Height = 27
  Radius = 7.2
FEATURE [Part::Cylinder] Cylinder112024025003003006010004276069  label="Válec413"
  Angle = 360
  AttacherType = Attacher::AttachEngine3D
  Height = 40
  Placement = pos=(-20,0,19.5) rot=(0,1,0;1.5708rad)
  Radius = 2.15
FEATURE [Part::Feature] Cylinder112024025003003006010004276070  label="Válec414"
  Placement = pos=(0,0,0) rot=(0,0,1;4.18879rad)
  shape: bbox 7.858 x 10.31 x 3.3 mm, 3 faces (baked)
FEATURE [Part::Feature] Cylinder112024025003003006010004276071  label="Válec415"
  Placement = pos=(0,0,0) rot=(0,0,1;2.0944rad)
  shape: bbox 7.858 x 10.31 x 3.3 mm, 3 faces (baked)
FEATURE [Part::Feature] difference001008  label="Pulley GT2  - 044"
  Placement = pos=(0,0,19.5) rot=(0,0,1;0rad)
  shape: bbox 27.96 x 27.96 x 19.5 mm, 1014 faces (baked)
FEATURE [Part::MultiFuse] Fusion005043005007002078086001005
  Shapes = -> [Cylinder112024025003003006010004276071,Cylinder112024025003003006010004276070]
FEATURE [App::Part] Part015  label="TMP"
  Group = -> [Box021164,Box021165,Box021166,Box021247,Cylinder112024025003003006010004276045,Cylinder112024025003003006010004276043,Cylinder112024025003003006010004276041,Cylinder112024025003003006010004276044,Fusion005043005007002078076,Box021252,Extrude025,Sketch022,Fusion005043005007002078083,Cylinder112024025003003006010004276070,Cylinder112024025003003006010004276071,Fusion005043005007002078086001005]
  Origin = -> Origin015
FEATURE [Part::Cylinder] Cylinder112024025003003006010004276072  label="Válec416"
  Angle = 360
  AttacherType = Attacher::AttachEngine3D
  Height = 17
  Placement = pos=(15,0,36) rot=(0,0,1;0rad)
  Radius = 2
FEATURE [Part::Feature] Fusion005043005007002078086001007
  Placement = pos=(0,0,0) rot=(0,0,1;2.0944rad)
  shape: bbox 10.6 x 11.86 x 17 mm, 9 faces, 3 solids (baked)
FEATURE [Part::Feature] Fusion005043005007002078086001008
  Placement = pos=(0,0,0) rot=(0,0,1;1.0472rad)
  shape: bbox 14.1 x 5.782 x 17 mm, 9 faces, 3 solids (baked)
FEATURE [Part::Feature] Cylinder112024025003003006010004276073  label="Válec417"
  Placement = pos=(0,0,0) rot=(0,0,1;0.349066rad)
  shape: bbox 4 x 4 x 17 mm, 3 faces (baked)
FEATURE [Part::Feature] Fusion005043005007002078086001009
  Placement = pos=(0,0,0) rot=(0,0,1;4.18879rad)
  shape: bbox 14.1 x 5.782 x 17 mm, 9 faces, 3 solids (baked)
FEATURE [Part::Feature] Cylinder112024025003003006010004276074  label="Válec418"
  Placement = pos=(0,0,0) rot=(0,0,1;0.698132rad)
  shape: bbox 4 x 4 x 17 mm, 3 faces (baked)
FEATURE [Part::Feature] Fusion005043005007002078086001010
  Placement = pos=(0,0,0) rot=(0,0,-1;1.0472rad)
  shape: bbox 10.6 x 11.86 x 17 mm, 9 faces, 3 solids (baked)
FEATURE [Part::Feature] Fusion005043005007002078086001011
  Placement = pos=(0,0,0) rot=(0,0,1;3.14159rad)
  shape: bbox 7.509 x 13.64 x 17 mm, 9 faces, 3 solids (baked)
FEATURE [Part::MultiFuse] Fusion005043005007002078086001012
  Shapes = -> [Cylinder112024025003003006010004276072,Cylinder112024025003003006010004276073,Cylinder112024025003003006010004276074]
FEATURE [Part::MultiFuse] Fusion005043005007002078086001013
  Placement = pos=(0,0,4) rot=(0,0,1;0rad)
  Shapes = -> [Fusion005043005007002078086001012,Fusion005043005007002078086001008,Fusion005043005007002078086001007,Fusion005043005007002078086001009,Fusion005043005007002078086001010,Fusion005043005007002078086001011]
FEATURE [Part::MultiFuse] Fusion005043005007002078086001004  label="VROUBKY Z INBUD"
  Shapes = -> [Cylinder112024025003003006010004276064,Cylinder112024025003003006010004276065,Cylinder112024025003003006010004276069,Cylinder112024025003003006010004276067,Fusion005043005007002078086001013]
FEATURE [Part::MultiFuse] Fusion005043005007002078086001014
  Shapes = -> [Cylinder112024025003003006010004276059,Cylinder112024025003003006010004276058,difference001008,Cylinder112024025003003006010004276062]
FEATURE [Part::Fillet] Fillet028003007
  Base = -> Fusion005043005007002078086001014
  Edges = 2 edges r=2: [Edge49,Edge2734]
FEATURE [Part::Cut] Cut018020020009027020002003004004026003005007016  label="PulleyR"
  Base = -> Fillet028003007
  Tool = -> Fusion005043005007002078086001004
FEATURE [Part::Feature] Compound001  label="28BYJ-48 final"
  Placement = pos=(0,0,-1) rot=(0,0,1;0rad)
  shape: bbox 42 x 31 x 29 mm, 57 faces, 3 solids (baked)
FEATURE [App::Part] Part020  label="Motor 28BYJ-48"
  Group = -> [Compound001]
  License = CC BY 3.0
  LicenseURL = http://creativecommons.org/licenses/by/3.0/
  Origin = -> Origin020
FEATURE [Part::Feature] Cut002001  label="S dirou 4"
  Placement = pos=(0,0,-22) rot=(0,0,1;1.0472rad)
  shape: bbox 18 x 18 x 12 mm, 118 faces (baked)
FEATURE [Part::Feature] Cut002002  label="S dirou 5"
  Placement = pos=(0,0,0) rot=(1,0,0;3.14159rad)
  shape: bbox 18 x 18 x 12 mm, 108 faces (baked)
FEATURE [Part::Feature] Cut005005  label="Pulley-GT2-16_28BYJ--48"
  Placement = pos=(0,0,0) rot=(1,0,0;3.14159rad)
  shape: bbox 12.68 x 12.68 x 11 mm, 393 faces (baked)
FEATURE [App::Part] Part019  label="Pulley-GT2-16_28BYJ-48"
  Group = -> [Cut005005]
  License = CC BY 3.0
  LicenseURL = http://creativecommons.org/licenses/by/3.0/
  Origin = -> Origin019
  Placement = pos=(0,8,30) rot=(0,0,1;0rad)
FEATURE [App::Part] Part021  label="Motor a pastorek"
  Group = -> [Part020,Part019]
  License = CC BY 3.0
  LicenseURL = http://creativecommons.org/licenses/by/3.0/
  Origin = -> Origin021
  Placement = pos=(0,-55,52) rot=(0,1,0;3.14159rad)
FEATURE [Part::MultiFuse] Fusion029
  Shapes = -> [Cut002001,Cut002002]
FEATURE [Part::Cylinder] Cylinder072  label="Válec068"
  Angle = 360
  AttacherType = Attacher::AttachEngine3D
  Height = 10
  Placement = pos=(0,0,-3) rot=(0,0,1;0rad)
  Radius = 10
FEATURE [Part::Cut] Cut002003  label="Clutch"
  Base = -> Fusion029
  Placement = pos=(0,29,22) rot=(0,0,1;0rad)
  Tool = -> Cylinder072
FEATURE [App::Part] Part018  label="GSO"
  Group = -> [Fillet028003005,Cylinder112024025003003006010004276004,Cylinder112024025003003006010004264,Cylinder112024025003003006010004276005,Cylinder112024025003003006010004276,Cylinder112024025003003006010004276003,Cylinder112024025003003006010004276006,Cylinder112024025003003006010004276007,Fusion005043005007002078054,Fusion005043005007002078053,Cylinder112024025003003006010004263,+94 more]
  Origin = -> Origin018
FEATURE [Part::Feature] Shape312
  shape: bbox 0.6 x 0.6 x 2e-07 mm, 0 faces, 0 solids (baked)
FEATURE [Part::Feature] Shape292
  shape: bbox 2e-07 x 10.17 x 2e-07 mm, 0 faces, 0 solids (baked)
FEATURE [Part::Feature] Shape315
  shape: bbox 3.2 x 1.594 x 2e-07 mm, 0 faces, 0 solids (baked)
FEATURE [Part::Feature] Shape326
  shape: bbox 3 x 3 x 2e-07 mm, 0 faces, 0 solids (baked)
FEATURE [Part::Feature] Shape328
  shape: bbox 0.9 x 0.9 x 2e-07 mm, 0 faces, 0 solids (baked)
FEATURE [Part::Feature] Shape330
  shape: bbox 0.9 x 0.9 x 2e-07 mm, 0 faces, 0 solids (baked)
FEATURE [Part::Feature] Shape321
  shape: bbox 3.5 x 3.5 x 2e-07 mm, 0 faces, 0 solids (baked)
FEATURE [Part::Feature] Shape337
  shape: bbox 1.524 x 1.524 x 2e-07 mm, 0 faces, 0 solids (baked)
FEATURE [Part::Feature] Shape285
  shape: bbox 2e-07 x 15.5 x 2e-07 mm, 0 faces, 0 solids (baked)
FEATURE [Part::Feature] Shape320
  shape: bbox 3 x 3 x 2e-07 mm, 0 faces, 0 solids (baked)
FEATURE [Part::Feature] Shape313
  shape: bbox 4.4 x 2.2 x 2e-07 mm, 0 faces, 0 solids (baked)
FEATURE [Part::Feature] Shape332
  shape: bbox 0.9 x 0.9 x 2e-07 mm, 0 faces, 0 solids (baked)
FEATURE [Part::Feature] Shape283
  shape: bbox 2e-07 x 5.08 x 2e-07 mm, 0 faces, 0 solids (baked)
FEATURE [Part::Feature] Shape297
  shape: bbox 2e-07 x 1.016 x 2e-07 mm, 0 faces, 0 solids (baked)
FEATURE [Part::Feature] Shape317
  shape: bbox 12 x 12 x 2e-07 mm, 0 faces, 0 solids (baked)
FEATURE [Part::Feature] Shape343
  shape: bbox 1.524 x 1.524 x 2e-07 mm, 0 faces, 0 solids (baked)
FEATURE [Part::Feature] Shape336
  shape: bbox 0.9144 x 0.9144 x 2e-07 mm, 0 faces, 0 solids (baked)
FEATURE [Part::Feature] Shape344
  shape: bbox 0.9144 x 0.9144 x 2e-07 mm, 0 faces, 0 solids (baked)
FEATURE [Part::Feature] Shape323
  shape: bbox 3.5 x 3.5 x 2e-07 mm, 0 faces, 0 solids (baked)
FEATURE [Part::Feature] Shape333
  shape: bbox 1.651 x 1.651 x 2e-07 mm, 0 faces, 0 solids (baked)
FEATURE [Part::Feature] Shape290
  shape: bbox 7.517 x 2e-07 x 2e-07 mm, 0 faces, 0 solids (baked)
FEATURE [Part::Feature] Shape309
  shape: bbox 6.1 x 3.154 x 2e-07 mm, 0 faces, 0 solids (baked)
FEATURE [Part::Feature] Shape345
  shape: bbox 1.524 x 1.524 x 2e-07 mm, 0 faces, 0 solids (baked)
FEATURE [Part::Feature] Shape331
  shape: bbox 1.651 x 1.651 x 2e-07 mm, 0 faces, 0 solids (baked)
FEATURE [Part::Feature] Shape346
  shape: bbox 0.9144 x 0.9144 x 2e-07 mm, 0 faces, 0 solids (baked)
FEATURE [Part::Feature] Shape291
  shape: bbox 7.513 x 2e-07 x 2e-07 mm, 0 faces, 0 solids (baked)
FEATURE [Part::Feature] Shape293
  shape: bbox 7.513 x 2e-07 x 2e-07 mm, 0 faces, 0 solids (baked)
FEATURE [Part::Feature] Shape308
  shape: bbox 9.758 x 8.689 x 2e-07 mm, 0 faces, 0 solids (baked)
FEATURE [Part::Feature] Shape286
  shape: bbox 2e-07 x 15.5 x 2e-07 mm, 0 faces, 0 solids (baked)
FEATURE [Part::Feature] Shape287
  shape: bbox 18.16 x 2e-07 x 2e-07 mm, 0 faces, 0 solids (baked)
FEATURE [Part::Feature] Shape299
  shape: bbox 2e-07 x 2.032 x 2e-07 mm, 0 faces, 0 solids (baked)
FEATURE [Part::Feature] Shape294
  shape: bbox 7.517 x 2e-07 x 2e-07 mm, 0 faces, 0 solids (baked)
FEATURE [Part::Feature] Shape304
  shape: bbox 4 x 3.547 x 2e-07 mm, 0 faces, 0 solids (baked)
FEATURE [Part::Feature] Shape284
  shape: bbox 18.16 x 2e-07 x 2e-07 mm, 0 faces, 0 solids (baked)
FEATURE [Part::Feature] Shape302
  shape: bbox 1.27 x 2e-07 x 2e-07 mm, 0 faces, 0 solids (baked)
FEATURE [Part::Feature] Shape295
  shape: bbox 1.016 x 2e-07 x 2e-07 mm, 0 faces, 0 solids (baked)
FEATURE [Part::Feature] Shape305
  shape: bbox 0.6 x 0.6 x 2e-07 mm, 0 faces, 0 solids (baked)
FEATURE [Part::Feature] Shape306
  shape: bbox 0.25 x 0.25 x 2e-07 mm, 0 faces, 0 solids (baked)
FEATURE [Part::Feature] Shape310
  shape: bbox 0.3 x 0.3 x 2e-07 mm, 0 faces, 0 solids (baked)
FEATURE [Part::Feature] Shape314
  shape: bbox 4.4 x 2.2 x 2e-07 mm, 0 faces, 0 solids (baked)
FEATURE [Part::Feature] Shape301
  shape: bbox 2e-07 x 0.762 x 2e-07 mm, 0 faces, 0 solids (baked)
FEATURE [Part::Feature] Shape318
  shape: bbox 2.54 x 2.54 x 2e-07 mm, 0 faces, 0 solids (baked)
FEATURE [Part::Feature] Shape303
  shape: bbox 4 x 3.547 x 2e-07 mm, 0 faces, 0 solids (baked)
FEATURE [Part::Feature] Shape322
  shape: bbox 3 x 3 x 2e-07 mm, 0 faces, 0 solids (baked)
FEATURE [Part::Feature] Shape288
  shape: bbox 7.513 x 2e-07 x 2e-07 mm, 0 faces, 0 solids (baked)
FEATURE [Part::Feature] Shape289
  shape: bbox 7.521 x 2e-07 x 2e-07 mm, 0 faces, 0 solids (baked)
FEATURE [Part::Feature] Shape298
  shape: bbox 1.016 x 2e-07 x 2e-07 mm, 0 faces, 0 solids (baked)
FEATURE [Part::Feature] Shape300
  shape: bbox 2e-07 x 0.254 x 2e-07 mm, 0 faces, 0 solids (baked)
FEATURE [Part::Feature] Shape296
  shape: bbox 2e-07 x 1.016 x 2e-07 mm, 0 faces, 0 solids (baked)
FEATURE [Part::Feature] Shape307
  shape: bbox 1.27 x 0.635 x 2e-07 mm, 0 faces, 0 solids (baked)
FEATURE [Part::Feature] Shape311
  shape: bbox 1.27 x 0.635 x 2e-07 mm, 0 faces, 0 solids (baked)
FEATURE [Part::Feature] Shape316
  shape: bbox 3.2 x 1.594 x 2e-07 mm, 0 faces, 0 solids (baked)
FEATURE [Part::Feature] Shape319
  shape: bbox 8 x 8 x 2e-07 mm, 0 faces, 0 solids (baked)
FEATURE [Part::Feature] Shape324
  shape: bbox 3 x 3 x 2e-07 mm, 0 faces, 0 solids (baked)
FEATURE [Part::Feature] Shape325
  shape: bbox 3.5 x 3.5 x 2e-07 mm, 0 faces, 0 solids (baked)
FEATURE [Part::Feature] Shape327
  shape: bbox 3.5 x 3.5 x 2e-07 mm, 0 faces, 0 solids (baked)
FEATURE [Part::Feature] Shape329
  shape: bbox 1.651 x 1.651 x 2e-07 mm, 0 faces, 0 solids (baked)
FEATURE [Part::Feature] Shape334
  shape: bbox 0.9 x 0.9 x 2e-07 mm, 0 faces, 0 solids (baked)
FEATURE [Part::Feature] Shape335
  shape: bbox 1.651 x 1.651 x 2e-07 mm, 0 faces, 0 solids (baked)
FEATURE [Part::Feature] Shape339
  shape: bbox 1.524 x 1.524 x 2e-07 mm, 0 faces, 0 solids (baked)
FEATURE [Part::Feature] Shape338
  shape: bbox 0.9144 x 0.9144 x 2e-07 mm, 0 faces, 0 solids (baked)
FEATURE [Part::Feature] Shape340
  shape: bbox 0.9144 x 0.9144 x 2e-07 mm, 0 faces, 0 solids (baked)
FEATURE [Part::Feature] Shape341
  shape: bbox 1.524 x 1.524 x 2e-07 mm, 0 faces, 0 solids (baked)
FEATURE [Part::Feature] Shape342
  shape: bbox 0.9144 x 0.9144 x 2e-07 mm, 0 faces, 0 solids (baked)
FEATURE [Part::Feature] Shape365
  shape: bbox 1.575 x 1.575 x 2e-07 mm, 0 faces, 0 solids (baked)
FEATURE [Part::Feature] Shape369
  shape: bbox 1.905 x 1.905 x 2e-07 mm, 0 faces, 0 solids (baked)
FEATURE [Part::Feature] Shape374
  shape: bbox 1 x 1 x 2e-07 mm, 0 faces, 0 solids (baked)
FEATURE [Part::Feature] Shape361
  shape: bbox 1.575 x 1.575 x 2e-07 mm, 0 faces, 0 solids (baked)
FEATURE [Part::Feature] Shape375
  shape: bbox 2.159 x 2.159 x 2e-07 mm, 0 faces, 0 solids (baked)
FEATURE [Part::Feature] Shape356
  shape: bbox 1.016 x 1.016 x 2e-07 mm, 0 faces, 0 solids (baked)
FEATURE [Part::Feature] Shape353
  shape: bbox 1.88 x 1.88 x 2e-07 mm, 0 faces, 0 solids (baked)
FEATURE [Part::Feature] Shape370
  shape: bbox 1 x 1 x 2e-07 mm, 0 faces, 0 solids (baked)
FEATURE [Part::Feature] Shape352
  shape: bbox 1.016 x 1.016 x 2e-07 mm, 0 faces, 0 solids (baked)
FEATURE [Part::Feature] Shape376
  shape: bbox 1 x 1 x 2e-07 mm, 0 faces, 0 solids (baked)
FEATURE [Part::Feature] Shape350
  shape: bbox 1.016 x 1.016 x 2e-07 mm, 0 faces, 0 solids (baked)
FEATURE [Part::Feature] Shape358
  shape: bbox 0.889 x 0.889 x 2e-07 mm, 0 faces, 0 solids (baked)
FEATURE [Part::Feature] Shape377
  shape: bbox 2.159 x 2.159 x 2e-07 mm, 0 faces, 0 solids (baked)
FEATURE [Part::Feature] Shape351
  shape: bbox 1.88 x 1.88 x 2e-07 mm, 0 faces, 0 solids (baked)
FEATURE [Part::Feature] Shape378
  shape: bbox 1.2 x 1.2 x 2e-07 mm, 0 faces, 0 solids (baked)
FEATURE [Part::Feature] Shape379
  shape: bbox 1.8 x 1.8 x 2e-07 mm, 0 faces, 0 solids (baked)
FEATURE [Part::Feature] Shape363
  shape: bbox 1.575 x 1.575 x 2e-07 mm, 0 faces, 0 solids (baked)
FEATURE [Part::Feature] Shape380
  shape: bbox 1.2 x 1.2 x 2e-07 mm, 0 faces, 0 solids (baked)
FEATURE [Part::Feature] Shape381
  shape: bbox 1.8 x 1.8 x 2e-07 mm, 0 faces, 0 solids (baked)
FEATURE [Part::Feature] Shape382
  shape: bbox 0.9 x 0.9 x 2e-07 mm, 0 faces, 0 solids (baked)
FEATURE [Part::Feature] Shape383
  shape: bbox 1.5 x 1.5 x 2e-07 mm, 0 faces, 0 solids (baked)
FEATURE [Part::Feature] Shape384
  shape: bbox 0.9 x 0.9 x 2e-07 mm, 0 faces, 0 solids (baked)
FEATURE [Part::Feature] Shape385
  shape: bbox 1.5 x 1.5 x 2e-07 mm, 0 faces, 0 solids (baked)
FEATURE [Part::Feature] Shape372
  shape: bbox 1 x 1 x 2e-07 mm, 0 faces, 0 solids (baked)
FEATURE [Part::Feature] Shape360
  shape: bbox 0.889 x 0.889 x 2e-07 mm, 0 faces, 0 solids (baked)
FEATURE [Part::Feature] Shape362
  shape: bbox 0.889 x 0.889 x 2e-07 mm, 0 faces, 0 solids (baked)
FEATURE [Part::Feature] Shape367
  shape: bbox 1.905 x 1.905 x 2e-07 mm, 0 faces, 0 solids (baked)
FEATURE [Part::Feature] Shape386
  shape: bbox 0.9 x 0.9 x 2e-07 mm, 0 faces, 0 solids (baked)
FEATURE [Part::Feature] Shape357
  shape: bbox 1.88 x 1.88 x 2e-07 mm, 0 faces, 0 solids (baked)
FEATURE [Part::Feature] Shape348
  shape: bbox 0.9144 x 0.9144 x 2e-07 mm, 0 faces, 0 solids (baked)
FEATURE [Part::Feature] Shape347
  shape: bbox 1.524 x 1.524 x 2e-07 mm, 0 faces, 0 solids (baked)
FEATURE [Part::Feature] Shape355
  shape: bbox 1.88 x 1.88 x 2e-07 mm, 0 faces, 0 solids (baked)
FEATURE [Part::Feature] Shape359
  shape: bbox 1.575 x 1.575 x 2e-07 mm, 0 faces, 0 solids (baked)
FEATURE [Part::Feature] Shape368
  shape: bbox 1.118 x 1.118 x 2e-07 mm, 0 faces, 0 solids (baked)
FEATURE [Part::Feature] Shape366
  shape: bbox 1.118 x 1.118 x 2e-07 mm, 0 faces, 0 solids (baked)
FEATURE [Part::Feature] Shape364
  shape: bbox 0.889 x 0.889 x 2e-07 mm, 0 faces, 0 solids (baked)
FEATURE [Part::Feature] Shape371
  shape: bbox 2.159 x 2.159 x 2e-07 mm, 0 faces, 0 solids (baked)
FEATURE [Part::Feature] Shape349
  shape: bbox 1.524 x 1.524 x 2e-07 mm, 0 faces, 0 solids (baked)
FEATURE [Part::Feature] Shape354
  shape: bbox 1.016 x 1.016 x 2e-07 mm, 0 faces, 0 solids (baked)
FEATURE [Part::Feature] Shape373
  shape: bbox 2.159 x 2.159 x 2e-07 mm, 0 faces, 0 solids (baked)
FEATURE [Part::Feature] Shape431
  shape: bbox 1.5 x 1.5 x 2e-07 mm, 0 faces, 0 solids (baked)
FEATURE [Part::Feature] Shape436
  shape: bbox 0.9144 x 0.9144 x 2e-07 mm, 0 faces, 0 solids (baked)
FEATURE [Part::Feature] Shape438
  shape: bbox 0.9144 x 0.9144 x 2e-07 mm, 0 faces, 0 solids (baked)
FEATURE [Part::Feature] Shape441
  shape: bbox 1.524 x 1.524 x 2e-07 mm, 0 faces, 0 solids (baked)
FEATURE [Part::Feature] Shape408
  shape: bbox 0.9 x 0.9 x 2e-07 mm, 0 faces, 0 solids (baked)
FEATURE [Part::Feature] Shape413
  shape: bbox 1.5 x 1.5 x 2e-07 mm, 0 faces, 0 solids (baked)
FEATURE [Part::Feature] Shape415
  shape: bbox 1.5 x 1.5 x 2e-07 mm, 0 faces, 0 solids (baked)
FEATURE [Part::Feature] Shape428
  shape: bbox 0.9 x 0.9 x 2e-07 mm, 0 faces, 0 solids (baked)
FEATURE [Part::Feature] Shape414
  shape: bbox 0.9 x 0.9 x 2e-07 mm, 0 faces, 0 solids (baked)
FEATURE [Part::Feature] Shape439
  shape: bbox 1.524 x 1.524 x 2e-07 mm, 0 faces, 0 solids (baked)
FEATURE [Part::Feature] Shape393
  shape: bbox 1.5 x 1.5 x 2e-07 mm, 0 faces, 0 solids (baked)
FEATURE [Part::Feature] Shape390
  shape: bbox 0.9 x 0.9 x 2e-07 mm, 0 faces, 0 solids (baked)
FEATURE [Part::Feature] Shape420
  shape: bbox 0.9 x 0.9 x 2e-07 mm, 0 faces, 0 solids (baked)
FEATURE [Part::Feature] Shape419
  shape: bbox 1.5 x 1.5 x 2e-07 mm, 0 faces, 0 solids (baked)
FEATURE [Part::Feature] Shape394
  shape: bbox 0.9 x 0.9 x 2e-07 mm, 0 faces, 0 solids (baked)
FEATURE [Part::Feature] Shape396
  shape: bbox 0.9 x 0.9 x 2e-07 mm, 0 faces, 0 solids (baked)
FEATURE [Part::Feature] Shape401
  shape: bbox 1.5 x 1.5 x 2e-07 mm, 0 faces, 0 solids (baked)
FEATURE [Part::Feature] Shape387
  shape: bbox 1.5 x 1.5 x 2e-07 mm, 0 faces, 0 solids (baked)
FEATURE [Part::Feature] Shape388
  shape: bbox 0.9 x 0.9 x 2e-07 mm, 0 faces, 0 solids (baked)
FEATURE [Part::Feature] Shape398
  shape: bbox 0.9 x 0.9 x 2e-07 mm, 0 faces, 0 solids (baked)
FEATURE [Part::Feature] Shape399
  shape: bbox 1.5 x 1.5 x 2e-07 mm, 0 faces, 0 solids (baked)
FEATURE [Part::Feature] Shape405
  shape: bbox 1.5 x 1.5 x 2e-07 mm, 0 faces, 0 solids (baked)
FEATURE [Part::Feature] Shape412
  shape: bbox 0.9 x 0.9 x 2e-07 mm, 0 faces, 0 solids (baked)
FEATURE [Part::Feature] Shape403
  shape: bbox 1.5 x 1.5 x 2e-07 mm, 0 faces, 0 solids (baked)
FEATURE [Part::Feature] Shape421
  shape: bbox 1.5 x 1.5 x 2e-07 mm, 0 faces, 0 solids (baked)
FEATURE [Part::Feature] Shape424
  shape: bbox 0.9 x 0.9 x 2e-07 mm, 0 faces, 0 solids (baked)
FEATURE [Part::Feature] Shape425
  shape: bbox 1.5 x 1.5 x 2e-07 mm, 0 faces, 0 solids (baked)
FEATURE [Part::Feature] Shape426
  shape: bbox 0.9 x 0.9 x 2e-07 mm, 0 faces, 0 solids (baked)
FEATURE [Part::Feature] Shape429
  shape: bbox 1.5 x 1.5 x 2e-07 mm, 0 faces, 0 solids (baked)
FEATURE [Part::Feature] Shape432
  shape: bbox 0.9 x 0.9 x 2e-07 mm, 0 faces, 0 solids (baked)
FEATURE [Part::Feature] Shape391
  shape: bbox 1.5 x 1.5 x 2e-07 mm, 0 faces, 0 solids (baked)
FEATURE [Part::Feature] Shape400
  shape: bbox 0.9 x 0.9 x 2e-07 mm, 0 faces, 0 solids (baked)
FEATURE [Part::Feature] Shape406
  shape: bbox 0.9 x 0.9 x 2e-07 mm, 0 faces, 0 solids (baked)
FEATURE [Part::Feature] Shape389
  shape: bbox 1.5 x 1.5 x 2e-07 mm, 0 faces, 0 solids (baked)
FEATURE [Part::Feature] Shape418
  shape: bbox 0.9 x 0.9 x 2e-07 mm, 0 faces, 0 solids (baked)
FEATURE [Part::Feature] Shape422
  shape: bbox 0.9 x 0.9 x 2e-07 mm, 0 faces, 0 solids (baked)
FEATURE [Part::Feature] Shape402
  shape: bbox 0.9 x 0.9 x 2e-07 mm, 0 faces, 0 solids (baked)
FEATURE [Part::Feature] Shape434
  shape: bbox 0.9 x 0.9 x 2e-07 mm, 0 faces, 0 solids (baked)
FEATURE [Part::Feature] Shape435
  shape: bbox 1.5 x 1.5 x 2e-07 mm, 0 faces, 0 solids (baked)
FEATURE [Part::Feature] Shape407
  shape: bbox 1.5 x 1.5 x 2e-07 mm, 0 faces, 0 solids (baked)
FEATURE [Part::Feature] Shape416
  shape: bbox 0.9 x 0.9 x 2e-07 mm, 0 faces, 0 solids (baked)
FEATURE [Part::Feature] Shape410
  shape: bbox 0.9 x 0.9 x 2e-07 mm, 0 faces, 0 solids (baked)
FEATURE [Part::Feature] Shape411
  shape: bbox 1.5 x 1.5 x 2e-07 mm, 0 faces, 0 solids (baked)
FEATURE [Part::Feature] Shape409
  shape: bbox 1.5 x 1.5 x 2e-07 mm, 0 faces, 0 solids (baked)
FEATURE [Part::Feature] Shape423
  shape: bbox 1.5 x 1.5 x 2e-07 mm, 0 faces, 0 solids (baked)
FEATURE [Part::Feature] Shape427
  shape: bbox 1.5 x 1.5 x 2e-07 mm, 0 faces, 0 solids (baked)
FEATURE [Part::Feature] Shape417
  shape: bbox 1.5 x 1.5 x 2e-07 mm, 0 faces, 0 solids (baked)
FEATURE [Part::Feature] Shape430
  shape: bbox 0.9 x 0.9 x 2e-07 mm, 0 faces, 0 solids (baked)
FEATURE [Part::Feature] Shape404
  shape: bbox 0.9 x 0.9 x 2e-07 mm, 0 faces, 0 solids (baked)
FEATURE [Part::Feature] Shape392
  shape: bbox 0.9 x 0.9 x 2e-07 mm, 0 faces, 0 solids (baked)
FEATURE [Part::Feature] Shape395
  shape: bbox 1.5 x 1.5 x 2e-07 mm, 0 faces, 0 solids (baked)
FEATURE [Part::Feature] Shape397
  shape: bbox 1.5 x 1.5 x 2e-07 mm, 0 faces, 0 solids (baked)
FEATURE [Part::Feature] Shape433
  shape: bbox 1.5 x 1.5 x 2e-07 mm, 0 faces, 0 solids (baked)
FEATURE [Part::Feature] Shape437
  shape: bbox 1.524 x 1.524 x 2e-07 mm, 0 faces, 0 solids (baked)
FEATURE [Part::Feature] Shape440
  shape: bbox 0.9144 x 0.9144 x 2e-07 mm, 0 faces, 0 solids (baked)
FEATURE [Part::Feature] Shape442
  shape: bbox 0.9144 x 0.9144 x 2e-07 mm, 0 faces, 0 solids (baked)
FEATURE [Part::Feature] Shape443
  shape: bbox 1.524 x 1.524 x 2e-07 mm, 0 faces, 0 solids (baked)
FEATURE [Part::Feature] Shape445
  shape: bbox 1.524 x 1.524 x 2e-07 mm, 0 faces, 0 solids (baked)
FEATURE [Part::Feature] Shape446
  shape: bbox 0.9144 x 0.9144 x 2e-07 mm, 0 faces, 0 solids (baked)
FEATURE [Part::Feature] Shape447
  shape: bbox 1.524 x 1.524 x 2e-07 mm, 0 faces, 0 solids (baked)
FEATURE [Part::Feature] Shape448
  shape: bbox 0.9144 x 0.9144 x 2e-07 mm, 0 faces, 0 solids (baked)
FEATURE [Part::Feature] Shape449
  shape: bbox 1.524 x 1.524 x 2e-07 mm, 0 faces, 0 solids (baked)
FEATURE [Part::Feature] Shape444
  shape: bbox 0.9144 x 0.9144 x 2e-07 mm, 0 faces, 0 solids (baked)
FEATURE [Part::Feature] Shape450
  shape: bbox 0.9144 x 0.9144 x 2e-07 mm, 0 faces, 0 solids (baked)
FEATURE [Part::Feature] Shape477
  shape: bbox 1.524 x 1.524 x 2e-07 mm, 0 faces, 0 solids (baked)
FEATURE [Part::Feature] Shape482
  shape: bbox 0.9144 x 0.9144 x 2e-07 mm, 0 faces, 0 solids (baked)
FEATURE [Part::Feature] Shape463
  shape: bbox 1.88 x 1.88 x 2e-07 mm, 0 faces, 0 solids (baked)
FEATURE [Part::Feature] Shape457
  shape: bbox 2 x 2 x 2e-07 mm, 0 faces, 0 solids (baked)
FEATURE [Part::Feature] Shape487
  shape: bbox 1.524 x 1.524 x 2e-07 mm, 0 faces, 0 solids (baked)
FEATURE [Part::Feature] Shape452
  shape: bbox 0.9 x 0.9 x 2e-07 mm, 0 faces, 0 solids (baked)
FEATURE [Part::Feature] Shape468
  shape: bbox 0.8992 x 0.8992 x 2e-07 mm, 0 faces, 0 solids (baked)
FEATURE [Part::Feature] Shape451
  shape: bbox 1.524 x 1.524 x 2e-07 mm, 0 faces, 0 solids (baked)
FEATURE [Part::Feature] Shape483
  shape: bbox 1.524 x 1.524 x 2e-07 mm, 0 faces, 0 solids (baked)
FEATURE [Part::Feature] Shape488
  shape: bbox 0.9144 x 0.9144 x 2e-07 mm, 0 faces, 0 solids (baked)
FEATURE [Part::Feature] Shape459
  shape: bbox 2 x 2 x 2e-07 mm, 0 faces, 0 solids (baked)
FEATURE [Part::Feature] Shape465
  shape: bbox 1.7 x 1.7 x 2e-07 mm, 0 faces, 0 solids (baked)
FEATURE [Part::Feature] Shape460
  shape: bbox 0.8992 x 0.8992 x 2e-07 mm, 0 faces, 0 solids (baked)
FEATURE [Part::Feature] Shape454
  shape: bbox 0.9 x 0.9 x 2e-07 mm, 0 faces, 0 solids (baked)
FEATURE [Part::Feature] Shape467
  shape: bbox 1.88 x 1.88 x 2e-07 mm, 0 faces, 0 solids (baked)
FEATURE [Part::Feature] Shape469
  shape: bbox 1.88 x 1.88 x 2e-07 mm, 0 faces, 0 solids (baked)
FEATURE [Part::Feature] Shape462
  shape: bbox 0.8992 x 0.8992 x 2e-07 mm, 0 faces, 0 solids (baked)
FEATURE [Part::Feature] Shape472
  shape: bbox 0.8992 x 0.8992 x 2e-07 mm, 0 faces, 0 solids (baked)
FEATURE [Part::Feature] Shape484
  shape: bbox 0.9144 x 0.9144 x 2e-07 mm, 0 faces, 0 solids (baked)
FEATURE [Part::Feature] Shape489
  shape: bbox 1.524 x 1.524 x 2e-07 mm, 0 faces, 0 solids (baked)
FEATURE [Part::Feature] Shape474
  shape: bbox 0.9144 x 0.9144 x 2e-07 mm, 0 faces, 0 solids (baked)
FEATURE [Part::Feature] Shape475
  shape: bbox 1.524 x 1.524 x 2e-07 mm, 0 faces, 0 solids (baked)
FEATURE [Part::Feature] Shape478
  shape: bbox 0.9144 x 0.9144 x 2e-07 mm, 0 faces, 0 solids (baked)
FEATURE [Part::Feature] Shape480
  shape: bbox 0.9144 x 0.9144 x 2e-07 mm, 0 faces, 0 solids (baked)
FEATURE [Part::Feature] Shape476
  shape: bbox 0.9144 x 0.9144 x 2e-07 mm, 0 faces, 0 solids (baked)
FEATURE [Part::Feature] Shape473
  shape: bbox 1.88 x 1.88 x 2e-07 mm, 0 faces, 0 solids (baked)
FEATURE [Part::Feature] Shape458
  shape: bbox 1.3 x 1.3 x 2e-07 mm, 0 faces, 0 solids (baked)
FEATURE [Part::Feature] Shape479
  shape: bbox 1.524 x 1.524 x 2e-07 mm, 0 faces, 0 solids (baked)
FEATURE [Part::Feature] Shape481
  shape: bbox 1.524 x 1.524 x 2e-07 mm, 0 faces, 0 solids (baked)
FEATURE [Part::Feature] Shape485
  shape: bbox 1.524 x 1.524 x 2e-07 mm, 0 faces, 0 solids (baked)
FEATURE [Part::Feature] Shape464
  shape: bbox 1.1 x 1.1 x 2e-07 mm, 0 faces, 0 solids (baked)
FEATURE [Part::Feature] Shape453
  shape: bbox 1.8 x 1.8 x 2e-07 mm, 0 faces, 0 solids (baked)
FEATURE [Part::Feature] Shape486
  shape: bbox 0.9144 x 0.9144 x 2e-07 mm, 0 faces, 0 solids (baked)
FEATURE [Part::Feature] Shape455
  shape: bbox 1.8 x 1.8 x 2e-07 mm, 0 faces, 0 solids (baked)
FEATURE [Part::Feature] Shape470
  shape: bbox 0.8992 x 0.8992 x 2e-07 mm, 0 faces, 0 solids (baked)
FEATURE [Part::Feature] Shape456
  shape: bbox 1.3 x 1.3 x 2e-07 mm, 0 faces, 0 solids (baked)
FEATURE [Part::Feature] Shape490
  shape: bbox 0.9144 x 0.9144 x 2e-07 mm, 0 faces, 0 solids (baked)
FEATURE [Part::Feature] Shape471
  shape: bbox 1.88 x 1.88 x 2e-07 mm, 0 faces, 0 solids (baked)
FEATURE [Part::Feature] Shape461
  shape: bbox 1.88 x 1.88 x 2e-07 mm, 0 faces, 0 solids (baked)
FEATURE [Part::Feature] Shape466
  shape: bbox 0.8992 x 0.8992 x 2e-07 mm, 0 faces, 0 solids (baked)
FEATURE [Part::Feature] Shape563
  shape: bbox 1.118 x 1.118 x 2e-07 mm, 0 faces, 0 solids (baked)
FEATURE [Part::Feature] Shape579
  shape: bbox 3.3 x 3.3 x 2e-07 mm, 0 faces, 0 solids (baked)
FEATURE [Part::Feature] Shape543
  shape: bbox 1 x 1 x 2e-07 mm, 0 faces, 0 solids (baked)
FEATURE [Part::Feature] Shape568
  shape: bbox 0.9 x 0.9 x 2e-07 mm, 0 faces, 0 solids (baked)
FEATURE [Part::Feature] Shape551
  shape: bbox 2e-07 x 1.88 x 2e-07 mm, 0 faces, 0 solids (baked)
FEATURE [Part::Feature] Shape560
  shape: bbox 1.575 x 2e-07 x 2e-07 mm, 0 faces, 0 solids (baked)
FEATURE [Part::Feature] Shape545
  shape: bbox 1.6 x 2e-07 x 2e-07 mm, 0 faces, 0 solids (baked)
FEATURE [Part::Feature] Shape532
  shape: bbox 1.6 x 0.8 x 2e-07 mm, 0 faces, 0 solids (baked)
FEATURE [Part::Feature] Shape548
  shape: bbox 1.016 x 1.016 x 2e-07 mm, 0 faces, 0 solids (baked)
FEATURE [Part::Feature] Shape552
  shape: bbox 1.88 x 2e-07 x 2e-07 mm, 0 faces, 0 solids (baked)
FEATURE [Part::Feature] Shape539
  shape: bbox 1 x 1 x 2e-07 mm, 0 faces, 0 solids (baked)
FEATURE [Part::Feature] Shape538
  shape: bbox 1.6 x 0.8 x 2e-07 mm, 0 faces, 0 solids (baked)
FEATURE [Part::Feature] Shape561
  shape: bbox 2e-07 x 1.575 x 2e-07 mm, 0 faces, 0 solids (baked)
FEATURE [Part::Feature] Shape541
  shape: bbox 1.6 x 0.8 x 2e-07 mm, 0 faces, 0 solids (baked)
FEATURE [Part::Feature] Shape540
  shape: bbox 1.6 x 0.8 x 2e-07 mm, 0 faces, 0 solids (baked)
FEATURE [Part::Feature] Shape534
  shape: bbox 1.6 x 0.8 x 2e-07 mm, 0 faces, 0 solids (baked)
FEATURE [Part::Feature] Shape557
  shape: bbox 2e-07 x 1.575 x 2e-07 mm, 0 faces, 0 solids (baked)
FEATURE [Part::Feature] Shape558
  shape: bbox 0.889 x 0.889 x 2e-07 mm, 0 faces, 0 solids (baked)
FEATURE [Part::Feature] Shape566
  shape: bbox 1.905 x 2e-07 x 2e-07 mm, 0 faces, 0 solids (baked)
FEATURE [Part::Feature] Shape555
  shape: bbox 2e-07 x 1.575 x 2e-07 mm, 0 faces, 0 solids (baked)
FEATURE [Part::Feature] Shape556
  shape: bbox 1.575 x 2e-07 x 2e-07 mm, 0 faces, 0 solids (baked)
FEATURE [Part::Feature] Shape567
  shape: bbox 2e-07 x 1.905 x 2e-07 mm, 0 faces, 0 solids (baked)
FEATURE [Part::Feature] Shape544
  shape: bbox 2e-07 x 1.6 x 2e-07 mm, 0 faces, 0 solids (baked)
FEATURE [Part::Feature] Shape569
  shape: bbox 1.5 x 2e-07 x 2e-07 mm, 0 faces, 0 solids (baked)
FEATURE [Part::Feature] Shape546
  shape: bbox 2e-07 x 1.6 x 2e-07 mm, 0 faces, 0 solids (baked)
FEATURE [Part::Feature] Shape559
  shape: bbox 2e-07 x 1.575 x 2e-07 mm, 0 faces, 0 solids (baked)
FEATURE [Part::Feature] Shape571
  shape: bbox 1.5 x 2e-07 x 2e-07 mm, 0 faces, 0 solids (baked)
FEATURE [Part::Feature] Shape553
  shape: bbox 0.889 x 0.889 x 2e-07 mm, 0 faces, 0 solids (baked)
FEATURE [Part::Feature] Shape574
  shape: bbox 1.7 x 2e-07 x 2e-07 mm, 0 faces, 0 solids (baked)
FEATURE [Part::Feature] Shape537
  shape: bbox 1.6 x 0.8 x 2e-07 mm, 0 faces, 0 solids (baked)
FEATURE [Part::Feature] Shape575
  shape: bbox 2e-07 x 1.575 x 2e-07 mm, 0 faces, 0 solids (baked)
FEATURE [Part::Feature] Shape550
  shape: bbox 1.88 x 2e-07 x 2e-07 mm, 0 faces, 0 solids (baked)
FEATURE [Part::Feature] Shape564
  shape: bbox 1.905 x 2e-07 x 2e-07 mm, 0 faces, 0 solids (baked)
FEATURE [Part::Feature] Shape576
  shape: bbox 1.7 x 2e-07 x 2e-07 mm, 0 faces, 0 solids (baked)
FEATURE [Part::Feature] Shape577
  shape: bbox 2e-07 x 1.575 x 2e-07 mm, 0 faces, 0 solids (baked)
FEATURE [Part::Feature] Shape535
  shape: bbox 1.6 x 0.8 x 2e-07 mm, 0 faces, 0 solids (baked)
FEATURE [Part::Feature] Shape536
  shape: bbox 1 x 1 x 2e-07 mm, 0 faces, 0 solids (baked)
FEATURE [Part::Feature] Shape570
  shape: bbox 2e-07 x 1.5 x 2e-07 mm, 0 faces, 0 solids (baked)
FEATURE [Part::Feature] Shape533
  shape: bbox 1 x 1 x 2e-07 mm, 0 faces, 0 solids (baked)
FEATURE [Part::Feature] Shape572
  shape: bbox 2e-07 x 1.5 x 2e-07 mm, 0 faces, 0 solids (baked)
FEATURE [Part::Feature] Shape542
  shape: bbox 1 x 1 x 2e-07 mm, 0 faces, 0 solids (baked)
FEATURE [Part::Feature] Shape565
  shape: bbox 2e-07 x 1.905 x 2e-07 mm, 0 faces, 0 solids (baked)
FEATURE [Part::Feature] Shape578
  shape: bbox 0.61 x 0.61 x 2e-07 mm, 0 faces, 0 solids (baked)
FEATURE [Part::Feature] Shape547
  shape: bbox 1.6 x 2e-07 x 2e-07 mm, 0 faces, 0 solids (baked)
FEATURE [Part::Feature] Shape554
  shape: bbox 1.575 x 2e-07 x 2e-07 mm, 0 faces, 0 solids (baked)
FEATURE [Part::Feature] Shape549
  shape: bbox 2e-07 x 1.88 x 2e-07 mm, 0 faces, 0 solids (baked)
FEATURE [Part::Feature] Shape531
  shape: bbox 1.6 x 0.8 x 2e-07 mm, 0 faces, 0 solids (baked)
FEATURE [Part::Feature] Shape562
  shape: bbox 1.575 x 2e-07 x 2e-07 mm, 0 faces, 0 solids (baked)
FEATURE [Part::Feature] Shape573
  shape: bbox 1.1 x 1.1 x 2e-07 mm, 0 faces, 0 solids (baked)
FEATURE [Part::Feature] Shape580
  shape: bbox 3.3 x 3.3 x 2e-07 mm, 0 faces, 0 solids (baked)
FEATURE [Part::Feature] Shape501
  shape: bbox 1.6 x 0.8 x 2e-07 mm, 0 faces, 0 solids (baked)
FEATURE [Part::Feature] Shape507
  shape: bbox 1.6 x 0.8 x 2e-07 mm, 0 faces, 0 solids (baked)
FEATURE [Part::Feature] Shape509
  shape: bbox 1 x 1 x 2e-07 mm, 0 faces, 0 solids (baked)
FEATURE [Part::Feature] Shape493
  shape: bbox 1.524 x 1.524 x 2e-07 mm, 0 faces, 0 solids (baked)
FEATURE [Part::Feature] Shape515
  shape: bbox 1 x 1 x 2e-07 mm, 0 faces, 0 solids (baked)
FEATURE [Part::Feature] Shape504
  shape: bbox 1.6 x 0.8 x 2e-07 mm, 0 faces, 0 solids (baked)
FEATURE [Part::Feature] Shape516
  shape: bbox 1.6 x 0.8 x 2e-07 mm, 0 faces, 0 solids (baked)
FEATURE [Part::Feature] Shape505
  shape: bbox 1.6 x 0.8 x 2e-07 mm, 0 faces, 0 solids (baked)
FEATURE [Part::Feature] Shape514
  shape: bbox 1.6 x 0.8 x 2e-07 mm, 0 faces, 0 solids (baked)
FEATURE [Part::Feature] Shape517
  shape: bbox 1.6 x 0.8 x 2e-07 mm, 0 faces, 0 solids (baked)
FEATURE [Part::Feature] Shape492
  shape: bbox 0.9144 x 0.9144 x 2e-07 mm, 0 faces, 0 solids (baked)
FEATURE [Part::Feature] Shape520
  shape: bbox 1.6 x 0.8 x 2e-07 mm, 0 faces, 0 solids (baked)
FEATURE [Part::Feature] Shape524
  shape: bbox 1 x 1 x 2e-07 mm, 0 faces, 0 solids (baked)
FEATURE [Part::Feature] Shape495
  shape: bbox 1.524 x 1.524 x 2e-07 mm, 0 faces, 0 solids (baked)
FEATURE [Part::Feature] Shape512
  shape: bbox 1 x 1 x 2e-07 mm, 0 faces, 0 solids (baked)
FEATURE [Part::Feature] Shape497
  shape: bbox 1.524 x 1.524 x 2e-07 mm, 0 faces, 0 solids (baked)
FEATURE [Part::Feature] Shape498
  shape: bbox 1.6 x 0.8 x 2e-07 mm, 0 faces, 0 solids (baked)
FEATURE [Part::Feature] Shape499
  shape: bbox 1.6 x 0.8 x 2e-07 mm, 0 faces, 0 solids (baked)
FEATURE [Part::Feature] Shape508
  shape: bbox 1.6 x 0.8 x 2e-07 mm, 0 faces, 0 solids (baked)
FEATURE [Part::Feature] Shape510
  shape: bbox 1.6 x 0.8 x 2e-07 mm, 0 faces, 0 solids (baked)
FEATURE [Part::Feature] Shape494
  shape: bbox 0.9144 x 0.9144 x 2e-07 mm, 0 faces, 0 solids (baked)
FEATURE [Part::Feature] Shape513
  shape: bbox 1.6 x 0.8 x 2e-07 mm, 0 faces, 0 solids (baked)
FEATURE [Part::Feature] Shape518
  shape: bbox 1 x 1 x 2e-07 mm, 0 faces, 0 solids (baked)
FEATURE [Part::Feature] Shape522
  shape: bbox 1.6 x 0.8 x 2e-07 mm, 0 faces, 0 solids (baked)
FEATURE [Part::Feature] Shape502
  shape: bbox 1.6 x 0.8 x 2e-07 mm, 0 faces, 0 solids (baked)
FEATURE [Part::Feature] Shape525
  shape: bbox 1.6 x 0.8 x 2e-07 mm, 0 faces, 0 solids (baked)
FEATURE [Part::Feature] Shape526
  shape: bbox 1.6 x 0.8 x 2e-07 mm, 0 faces, 0 solids (baked)
FEATURE [Part::Feature] Shape527
  shape: bbox 1 x 1 x 2e-07 mm, 0 faces, 0 solids (baked)
FEATURE [Part::Feature] Shape523
  shape: bbox 1.6 x 0.8 x 2e-07 mm, 0 faces, 0 solids (baked)
FEATURE [Part::Feature] Shape500
  shape: bbox 1 x 1 x 2e-07 mm, 0 faces, 0 solids (baked)
FEATURE [Part::Feature] Shape506
  shape: bbox 1 x 1 x 2e-07 mm, 0 faces, 0 solids (baked)
FEATURE [Part::Feature] Shape511
  shape: bbox 1.6 x 0.8 x 2e-07 mm, 0 faces, 0 solids (baked)
FEATURE [Part::Feature] Shape519
  shape: bbox 1.6 x 0.8 x 2e-07 mm, 0 faces, 0 solids (baked)
FEATURE [Part::Feature] Shape491
  shape: bbox 1.524 x 1.524 x 2e-07 mm, 0 faces, 0 solids (baked)
FEATURE [Part::Feature] Shape528
  shape: bbox 1.6 x 0.8 x 2e-07 mm, 0 faces, 0 solids (baked)
FEATURE [Part::Feature] Shape529
  shape: bbox 1.6 x 0.8 x 2e-07 mm, 0 faces, 0 solids (baked)
FEATURE [Part::Feature] Shape530
  shape: bbox 1 x 1 x 2e-07 mm, 0 faces, 0 solids (baked)
FEATURE [Part::Feature] Shape503
  shape: bbox 1 x 1 x 2e-07 mm, 0 faces, 0 solids (baked)
FEATURE [Part::Feature] Shape521
  shape: bbox 1 x 1 x 2e-07 mm, 0 faces, 0 solids (baked)
FEATURE [Part::Feature] Shape496
  shape: bbox 0.9144 x 0.9144 x 2e-07 mm, 0 faces, 0 solids (baked)
FEATURE [Part::Feature] Shape581
  shape: bbox 1.704 x 2e-07 x 2e-07 mm, 0 faces, 0 solids (baked)
FEATURE [Part::Box] Box021259  label="Krychle248"
  AttacherType = Attacher::AttachEngine3D
  Height = 1.6
  Length = 47
  Placement = pos=(88,122,0) rot=(0,0,1;0rad)
  Width = 77
FEATURE [Part::Feature] Shape582
  shape: bbox 31.76 x 2e-07 x 2e-07 mm, 0 faces, 0 solids (baked)
FEATURE [Part::Feature] Shape583
  shape: bbox 0.9931 x 2e-07 x 2e-07 mm, 0 faces, 0 solids (baked)
FEATURE [Part::Feature] Shape584
  shape: bbox 1.245 x 1.242 x 2e-07 mm, 0 faces, 0 solids (baked)
FEATURE [Part::Feature] Shape585
  shape: bbox 2e-07 x 1.735 x 2e-07 mm, 0 faces, 0 solids (baked)
FEATURE [Part::Feature] Shape586
  shape: bbox 1.072 x 1.074 x 2e-07 mm, 0 faces, 0 solids (baked)
FEATURE [Part::Feature] Shape587
  shape: bbox 1.669 x 1.671 x 2e-07 mm, 0 faces, 0 solids (baked)
FEATURE [Part::Feature] Shape588
  shape: bbox 0.7417 x 0.7417 x 2e-07 mm, 0 faces, 0 solids (baked)
FEATURE [Part::Feature] Shape589
  shape: bbox 4.9 x 2e-07 x 2e-07 mm, 0 faces, 0 solids (baked)
FEATURE [Part::Feature] Shape590
  shape: bbox 1.143 x 1.143 x 2e-07 mm, 0 faces, 0 solids (baked)
FEATURE [Part::Feature] Shape591
  shape: bbox 1.143 x 1.143 x 2e-07 mm, 0 faces, 0 solids (baked)
FEATURE [Part::Feature] Shape592
  shape: bbox 4.191 x 2e-07 x 2e-07 mm, 0 faces, 0 solids (baked)
FEATURE [Part::Feature] Shape593
  shape: bbox 2.924 x 2e-07 x 2e-07 mm, 0 faces, 0 solids (baked)
FEATURE [Part::Feature] Shape594
  shape: bbox 1.905 x 1.905 x 2e-07 mm, 0 faces, 0 solids (baked)
FEATURE [Part::Feature] Shape595
  shape: bbox 0.127 x 46.23 x 2e-07 mm, 0 faces, 0 solids (baked)
FEATURE [Part::Feature] Shape596
  shape: bbox 4.95 x 4.95 x 2e-07 mm, 0 faces, 0 solids (baked)
FEATURE [Part::Feature] Shape597
  shape: bbox 2e-07 x 5.702 x 2e-07 mm, 0 faces, 0 solids (baked)
FEATURE [Part::Feature] Shape598
  shape: bbox 3.048 x 2e-07 x 2e-07 mm, 0 faces, 0 solids (baked)
FEATURE [Part::Feature] Shape599
  shape: bbox 3.002 x 3.002 x 2e-07 mm, 0 faces, 0 solids (baked)
FEATURE [Part::Feature] Shape600
  shape: bbox 1.905 x 1.905 x 2e-07 mm, 0 faces, 0 solids (baked)
FEATURE [Part::Feature] Shape601
  shape: bbox 10.48 x 10.48 x 2e-07 mm, 0 faces, 0 solids (baked)
FEATURE [Part::Feature] Shape602
  shape: bbox 7.663 x 2e-07 x 2e-07 mm, 0 faces, 0 solids (baked)
FEATURE [Part::Feature] Shape603
  shape: bbox 2.939 x 2.936 x 2e-07 mm, 0 faces, 0 solids (baked)
FEATURE [Part::Feature] Shape604
  shape: bbox 0.5055 x 0.5055 x 2e-07 mm, 0 faces, 0 solids (baked)
FEATURE [Part::Feature] Shape605
  shape: bbox 2e-07 x 0.3099 x 2e-07 mm, 0 faces, 0 solids (baked)
FEATURE [Part::Feature] Shape606
  shape: bbox 19.87 x 2e-07 x 2e-07 mm, 0 faces, 0 solids (baked)
FEATURE [Part::Feature] Shape607
  shape: bbox 2.924 x 2e-07 x 2e-07 mm, 0 faces, 0 solids (baked)
FEATURE [Part::Feature] Shape608
  shape: bbox 31.94 x 2e-07 x 2e-07 mm, 0 faces, 0 solids (baked)
FEATURE [Part::Feature] Shape609
  shape: bbox 1.831 x 1.831 x 2e-07 mm, 0 faces, 0 solids (baked)
FEATURE [Part::Feature] Shape610
  shape: bbox 3.033 x 3.033 x 2e-07 mm, 0 faces, 0 solids (baked)
FEATURE [Part::Feature] Shape611
  shape: bbox 17.13 x 2e-07 x 2e-07 mm, 0 faces, 0 solids (baked)
FEATURE [Part::Feature] Shape612
  shape: bbox 76.58 x 0.127 x 2e-07 mm, 0 faces, 0 solids (baked)
FEATURE [Part::Feature] Shape613
  shape: bbox 9.934 x 2e-07 x 2e-07 mm, 0 faces, 0 solids (baked)
FEATURE [Part::Feature] Shape614
  shape: bbox 8.131 x 2e-07 x 2e-07 mm, 0 faces, 0 solids (baked)
FEATURE [Part::Feature] Shape615
  shape: bbox 11.16 x 2e-07 x 2e-07 mm, 0 faces, 0 solids (baked)
FEATURE [Part::Feature] Shape616
  shape: bbox 2.367 x 2.367 x 2e-07 mm, 0 faces, 0 solids (baked)
FEATURE [Part::Feature] Shape617
  shape: bbox 0.03556 x 0.03556 x 2e-07 mm, 0 faces, 0 solids (baked)
FEATURE [Part::Feature] Shape618
  shape: bbox 5.89 x 5.89 x 2e-07 mm, 0 faces, 0 solids (baked)
FEATURE [Part::Feature] Shape619
  shape: bbox 0.127 x 0.127 x 2e-07 mm, 0 faces, 0 solids (baked)
FEATURE [Part::Feature] Shape620
  shape: bbox 2e-07 x 46.1 x 2e-07 mm, 0 faces, 0 solids (baked)
FEATURE [Part::Feature] Shape621
  shape: bbox 9.804 x 9.804 x 2e-07 mm, 0 faces, 0 solids (baked)
FEATURE [Part::Feature] Shape622
  shape: bbox 4.501 x 4.501 x 2e-07 mm, 0 faces, 0 solids (baked)
FEATURE [Part::Feature] Shape623
  shape: bbox 8.092 x 2e-07 x 2e-07 mm, 0 faces, 0 solids (baked)
FEATURE [Part::Feature] Shape624
  shape: bbox 2.924 x 2e-07 x 2e-07 mm, 0 faces, 0 solids (baked)
FEATURE [Part::Feature] Shape625
  shape: bbox 1.905 x 1.905 x 2e-07 mm, 0 faces, 0 solids (baked)
FEATURE [Part::Feature] Shape626
  shape: bbox 8.004 x 2e-07 x 2e-07 mm, 0 faces, 0 solids (baked)
FEATURE [Part::Feature] Shape627
  shape: bbox 76.71 x 0.254 x 2e-07 mm, 0 faces, 0 solids (baked)
FEATURE [Part::Feature] Shape628
  shape: bbox 6.19 x 6.19 x 2e-07 mm, 0 faces, 0 solids (baked)
FEATURE [Part::Feature] Shape629
  shape: bbox 13.71 x 2e-07 x 2e-07 mm, 0 faces, 0 solids (baked)
FEATURE [Part::Feature] Shape089
  shape: bbox 1.27 x 1.27 x 2e-07 mm, 0 faces, 0 solids (baked)
FEATURE [Part::Feature] Shape630
  shape: bbox 5.08 x 2e-07 x 2e-07 mm, 0 faces, 0 solids (baked)
FEATURE [Part::Feature] Shape090
  shape: bbox 0.2692 x 2e-07 x 2e-07 mm, 0 faces, 0 solids (baked)
FEATURE [Part::Feature] Shape631
  shape: bbox 0.1905 x 0.188 x 2e-07 mm, 0 faces, 0 solids (baked)
FEATURE [Part::Feature] Shape071
  shape: bbox 5.306 x 5.306 x 2e-07 mm, 0 faces, 0 solids (baked)
FEATURE [Part::Feature] Shape095
  shape: bbox 1.402 x 1.402 x 2e-07 mm, 0 faces, 0 solids (baked)
FEATURE [Part::Feature] Shape632
  shape: bbox 2e-07 x 5.687 x 2e-07 mm, 0 faces, 0 solids (baked)
FEATURE [Part::Feature] Shape096
  shape: bbox 2e-07 x 1.836 x 2e-07 mm, 0 faces, 0 solids (baked)
FEATURE [Part::Feature] Shape633
  shape: bbox 3.81 x 2e-07 x 2e-07 mm, 0 faces, 0 solids (baked)
FEATURE [Part::Feature] Shape634
  shape: bbox 2e-07 x 1.14 x 2e-07 mm, 0 faces, 0 solids (baked)
FEATURE [Part::Feature] Shape635
  shape: bbox 7.097 x 2e-07 x 2e-07 mm, 0 faces, 0 solids (baked)
FEATURE [Part::Feature] Shape636
  shape: bbox 1.781 x 2e-07 x 2e-07 mm, 0 faces, 0 solids (baked)
FEATURE [Part::Feature] Shape069
  shape: bbox 11.7 x 11.7 x 2e-07 mm, 0 faces, 0 solids (baked)
FEATURE [Part::Feature] Shape076
  shape: bbox 4.445 x 4.445 x 2e-07 mm, 0 faces, 0 solids (baked)
FEATURE [Part::Feature] Shape077
  shape: bbox 8.555 x 2e-07 x 2e-07 mm, 0 faces, 0 solids (baked)
FEATURE [Part::Feature] Shape637
  shape: bbox 5.847 x 2e-07 x 2e-07 mm, 0 faces, 0 solids (baked)
FEATURE [Part::Feature] Shape081
  shape: bbox 1.102 x 2e-07 x 2e-07 mm, 0 faces, 0 solids (baked)
FEATURE [Part::Feature] Shape085
  shape: bbox 2e-07 x 0.508 x 2e-07 mm, 0 faces, 0 solids (baked)
FEATURE [Part::Feature] Shape084
  shape: bbox 5.832 x 5.832 x 2e-07 mm, 0 faces, 0 solids (baked)
FEATURE [Part::Feature] Shape093
  shape: bbox 2e-07 x 1.836 x 2e-07 mm, 0 faces, 0 solids (baked)
FEATURE [Part::Feature] Shape094
  shape: bbox 1.387 x 1.389 x 2e-07 mm, 0 faces, 0 solids (baked)
FEATURE [Part::Feature] Shape080
  shape: bbox 2e-07 x 0.5309 x 2e-07 mm, 0 faces, 0 solids (baked)
FEATURE [Part::Feature] Shape638
  shape: bbox 2.54 x 2.54 x 2e-07 mm, 0 faces, 0 solids (baked)
FEATURE [Part::Feature] Shape086
  shape: bbox 5.207 x 5.207 x 2e-07 mm, 0 faces, 0 solids (baked)
FEATURE [Part::Feature] Shape091
  shape: bbox 2e-07 x 1.692 x 2e-07 mm, 0 faces, 0 solids (baked)
FEATURE [Part::Feature] Shape088
  shape: bbox 2e-07 x 2.487 x 2e-07 mm, 0 faces, 0 solids (baked)
FEATURE [Part::Feature] Shape074
  shape: bbox 1.425 x 1.425 x 2e-07 mm, 0 faces, 0 solids (baked)
FEATURE [Part::Feature] Shape092
  shape: bbox 2.87 x 2.87 x 2e-07 mm, 0 faces, 0 solids (baked)
FEATURE [Part::Feature] Shape097
  shape: bbox 2.855 x 2.858 x 2e-07 mm, 0 faces, 0 solids (baked)
FEATURE [Part::Feature] Shape639
  shape: bbox 2.794 x 2.794 x 2e-07 mm, 0 faces, 0 solids (baked)
FEATURE [Part::Feature] Shape640
  shape: bbox 4.191 x 4.191 x 2e-07 mm, 0 faces, 0 solids (baked)
FEATURE [Part::Feature] Shape073
  shape: bbox 4.798 x 4.798 x 2e-07 mm, 0 faces, 0 solids (baked)
FEATURE [Part::Feature] Shape641
  shape: bbox 2.921 x 2.921 x 2e-07 mm, 0 faces, 0 solids (baked)
FEATURE [Part::Feature] Shape068
  shape: bbox 2e-07 x 0.4445 x 2e-07 mm, 0 faces, 0 solids (baked)
FEATURE [Part::Feature] Shape078
  shape: bbox 0.1549 x 0.1549 x 2e-07 mm, 0 faces, 0 solids (baked)
FEATURE [Part::Feature] Shape087
  shape: bbox 1.285 x 1.283 x 2e-07 mm, 0 faces, 0 solids (baked)
FEATURE [Part::Feature] Shape098
  shape: bbox 2e-07 x 0.2438 x 2e-07 mm, 0 faces, 0 solids (baked)
FEATURE [Part::Feature] Shape099
  shape: bbox 2.87 x 2.87 x 2e-07 mm, 0 faces, 0 solids (baked)
FEATURE [Part::Feature] Shape082
  shape: bbox 6.35 x 6.35 x 2e-07 mm, 0 faces, 0 solids (baked)
FEATURE [Part::Feature] Shape100
  shape: bbox 2e-07 x 1.593 x 2e-07 mm, 0 faces, 0 solids (baked)
FEATURE [Part::Feature] Shape642
  shape: bbox 0.127 x 0.127 x 2e-07 mm, 0 faces, 0 solids (baked)
FEATURE [Part::Feature] Shape643
  shape: bbox 1.201 x 1.201 x 2e-07 mm, 0 faces, 0 solids (baked)
FEATURE [Part::Feature] Shape644
  shape: bbox 0.5359 x 2e-07 x 2e-07 mm, 0 faces, 0 solids (baked)
FEATURE [Part::Feature] Shape645
  shape: bbox 2e-07 x 3.937 x 2e-07 mm, 0 faces, 0 solids (baked)
FEATURE [Part::Feature] Shape075
  shape: bbox 15.58 x 2e-07 x 2e-07 mm, 0 faces, 0 solids (baked)
FEATURE [Part::Feature] Shape079
  shape: bbox 2.009 x 2.009 x 2e-07 mm, 0 faces, 0 solids (baked)
FEATURE [Part::Feature] Shape646
  shape: bbox 4.29 x 4.29 x 2e-07 mm, 0 faces, 0 solids (baked)
FEATURE [Part::Feature] Shape083
  shape: bbox 4.646 x 2e-07 x 2e-07 mm, 0 faces, 0 solids (baked)
FEATURE [Part::Feature] Shape647
  shape: bbox 6.604 x 2e-07 x 2e-07 mm, 0 faces, 0 solids (baked)
FEATURE [Part::Feature] Shape648
  shape: bbox 2.477 x 2.477 x 2e-07 mm, 0 faces, 0 solids (baked)
FEATURE [Part::Feature] Shape070
  shape: bbox 2e-07 x 6.462 x 2e-07 mm, 0 faces, 0 solids (baked)
FEATURE [Part::Feature] Shape072
  shape: bbox 25.84 x 2e-07 x 2e-07 mm, 0 faces, 0 solids (baked)
FEATURE [Part::Feature] Shape124
  shape: bbox 1.463 x 1.463 x 2e-07 mm, 0 faces, 0 solids (baked)
FEATURE [Part::Feature] Shape125
  shape: bbox 0.7112 x 2e-07 x 2e-07 mm, 0 faces, 0 solids (baked)
FEATURE [Part::Feature] Shape126
  shape: bbox 9.03 x 9.03 x 2e-07 mm, 0 faces, 0 solids (baked)
FEATURE [Part::Feature] Shape112
  shape: bbox 6.746 x 2e-07 x 2e-07 mm, 0 faces, 0 solids (baked)
FEATURE [Part::Feature] Shape103
  shape: bbox 2e-07 x 0.9728 x 2e-07 mm, 0 faces, 0 solids (baked)
FEATURE [Part::Feature] Shape101
  shape: bbox 1.387 x 1.389 x 2e-07 mm, 0 faces, 0 solids (baked)
FEATURE [Part::Feature] Shape102
  shape: bbox 2.334 x 2.334 x 2e-07 mm, 0 faces, 0 solids (baked)
FEATURE [Part::Feature] Shape107
  shape: bbox 12.8 x 12.8 x 2e-07 mm, 0 faces, 0 solids (baked)
FEATURE [Part::Feature] Shape106
  shape: bbox 2e-07 x 1.153 x 2e-07 mm, 0 faces, 0 solids (baked)
FEATURE [Part::Feature] Shape108
  shape: bbox 2e-07 x 5.862 x 2e-07 mm, 0 faces, 0 solids (baked)
FEATURE [Part::Feature] Shape111
  shape: bbox 8.852 x 8.852 x 2e-07 mm, 0 faces, 0 solids (baked)
FEATURE [Part::Feature] Shape114
  shape: bbox 4.498 x 2e-07 x 2e-07 mm, 0 faces, 0 solids (baked)
FEATURE [Part::Feature] Shape116
  shape: bbox 2.924 x 2e-07 x 2e-07 mm, 0 faces, 0 solids (baked)
FEATURE [Part::Feature] Shape117
  shape: bbox 1.905 x 1.905 x 2e-07 mm, 0 faces, 0 solids (baked)
FEATURE [Part::Feature] Shape104
  shape: bbox 1.636 x 1.636 x 2e-07 mm, 0 faces, 0 solids (baked)
FEATURE [Part::Feature] Shape105
  shape: bbox 0.287 x 2e-07 x 2e-07 mm, 0 faces, 0 solids (baked)
FEATURE [Part::Feature] Shape110
  shape: bbox 0.7112 x 2e-07 x 2e-07 mm, 0 faces, 0 solids (baked)
FEATURE [Part::Feature] Shape109
  shape: bbox 2.113 x 2.113 x 2e-07 mm, 0 faces, 0 solids (baked)
FEATURE [Part::Feature] Shape115
  shape: bbox 3.81 x 3.81 x 2e-07 mm, 0 faces, 0 solids (baked)
FEATURE [Part::Feature] Shape113
  shape: bbox 0.922 x 0.922 x 2e-07 mm, 0 faces, 0 solids (baked)
FEATURE [Part::Feature] Shape118
  shape: bbox 1.425 x 1.422 x 2e-07 mm, 0 faces, 0 solids (baked)
FEATURE [Part::Feature] Shape120
  shape: bbox 0.9322 x 0.9322 x 2e-07 mm, 0 faces, 0 solids (baked)
FEATURE [Part::Feature] Shape121
  shape: bbox 1.163 x 2e-07 x 2e-07 mm, 0 faces, 0 solids (baked)
FEATURE [Part::Feature] Shape122
  shape: bbox 12.81 x 12.81 x 2e-07 mm, 0 faces, 0 solids (baked)
FEATURE [Part::Feature] Shape123
  shape: bbox 2e-07 x 6.944 x 2e-07 mm, 0 faces, 0 solids (baked)
FEATURE [Part::Feature] Shape119
  shape: bbox 2e-07 x 3.846 x 2e-07 mm, 0 faces, 0 solids (baked)
FEATURE [Part::Feature] Shape178
  shape: bbox 2e-07 x 0.8606 x 2e-07 mm, 0 faces, 0 solids (baked)
FEATURE [Part::Feature] Shape149
  shape: bbox 14.73 x 2e-07 x 2e-07 mm, 0 faces, 0 solids (baked)
FEATURE [Part::Feature] Shape173
  shape: bbox 2e-07 x 0.7024 x 2e-07 mm, 0 faces, 0 solids (baked)
FEATURE [Part::Feature] Shape132
  shape: bbox 2e-07 x 7.084 x 2e-07 mm, 0 faces, 0 solids (baked)
FEATURE [Part::Feature] Shape152
  shape: bbox 2.078 x 2.08 x 2e-07 mm, 0 faces, 0 solids (baked)
FEATURE [Part::Feature] Shape158
  shape: bbox 1.361 x 1.361 x 2e-07 mm, 0 faces, 0 solids (baked)
FEATURE [Part::Feature] Shape155
  shape: bbox 3.378 x 2e-07 x 2e-07 mm, 0 faces, 0 solids (baked)
FEATURE [Part::Feature] Shape129
  shape: bbox 2e-07 x 1.803 x 2e-07 mm, 0 faces, 0 solids (baked)
FEATURE [Part::Feature] Shape164
  shape: bbox 2e-07 x 1.698 x 2e-07 mm, 0 faces, 0 solids (baked)
FEATURE [Part::Feature] Shape139
  shape: bbox 2.032 x 2e-07 x 2e-07 mm, 0 faces, 0 solids (baked)
FEATURE [Part::Feature] Shape131
  shape: bbox 0.254 x 0.254 x 2e-07 mm, 0 faces, 0 solids (baked)
FEATURE [Part::Feature] Shape161
  shape: bbox 2.305 x 2e-07 x 2e-07 mm, 0 faces, 0 solids (baked)
FEATURE [Part::Feature] Shape166
  shape: bbox 2e-07 x 1.698 x 2e-07 mm, 0 faces, 0 solids (baked)
FEATURE [Part::Feature] Shape137
  shape: bbox 2e-07 x 7.049 x 2e-07 mm, 0 faces, 0 solids (baked)
FEATURE [Part::Feature] Shape142
  shape: bbox 8.374 x 2e-07 x 2e-07 mm, 0 faces, 0 solids (baked)
FEATURE [Part::Feature] Shape151
  shape: bbox 2e-07 x 3.132 x 2e-07 mm, 0 faces, 0 solids (baked)
FEATURE [Part::Feature] Shape154
  shape: bbox 2e-07 x 1.732 x 2e-07 mm, 0 faces, 0 solids (baked)
FEATURE [Part::Feature] Shape160
  shape: bbox 2.548 x 0.005334 x 2e-07 mm, 0 faces, 0 solids (baked)
FEATURE [Part::Feature] Shape168
  shape: bbox 2e-07 x 1.698 x 2e-07 mm, 0 faces, 0 solids (baked)
FEATURE [Part::Feature] Shape135
  shape: bbox 2e-07 x 3.099 x 2e-07 mm, 0 faces, 0 solids (baked)
FEATURE [Part::Feature] Shape127
  shape: bbox 5.342 x 2e-07 x 2e-07 mm, 0 faces, 0 solids (baked)
FEATURE [Part::Feature] Shape128
  shape: bbox 1.158 x 1.158 x 2e-07 mm, 0 faces, 0 solids (baked)
FEATURE [Part::Feature] Shape130
  shape: bbox 1.267 x 1.267 x 2e-07 mm, 0 faces, 0 solids (baked)
FEATURE [Part::Feature] Shape138
  shape: bbox 3.112 x 3.112 x 2e-07 mm, 0 faces, 0 solids (baked)
FEATURE [Part::Feature] Shape153
  shape: bbox 2e-07 x 1.181 x 2e-07 mm, 0 faces, 0 solids (baked)
FEATURE [Part::Feature] Shape163
  shape: bbox 2e-07 x 0.9889 x 2e-07 mm, 0 faces, 0 solids (baked)
FEATURE [Part::Feature] Shape165
  shape: bbox 2e-07 x 1.698 x 2e-07 mm, 0 faces, 0 solids (baked)
FEATURE [Part::Feature] Shape156
  shape: bbox 9.865 x 9.863 x 2e-07 mm, 0 faces, 0 solids (baked)
FEATURE [Part::Feature] Shape159
  shape: bbox 2.548 x 0.005334 x 2e-07 mm, 0 faces, 0 solids (baked)
FEATURE [Part::Feature] Shape136
  shape: bbox 1.438 x 1.438 x 2e-07 mm, 0 faces, 0 solids (baked)
FEATURE [Part::Feature] Shape147
  shape: bbox 2e-07 x 12.95 x 2e-07 mm, 0 faces, 0 solids (baked)
FEATURE [Part::Feature] Shape170
  shape: bbox 2e-07 x 1.698 x 2e-07 mm, 0 faces, 0 solids (baked)
FEATURE [Part::Feature] Shape141
  shape: bbox 5.525 x 5.525 x 2e-07 mm, 0 faces, 0 solids (baked)
FEATURE [Part::Feature] Shape167
  shape: bbox 2e-07 x 1.698 x 2e-07 mm, 0 faces, 0 solids (baked)
FEATURE [Part::Feature] Shape148
  shape: bbox 7.493 x 7.493 x 2e-07 mm, 0 faces, 0 solids (baked)
FEATURE [Part::Feature] Shape146
  shape: bbox 7.112 x 2e-07 x 2e-07 mm, 0 faces, 0 solids (baked)
FEATURE [Part::Feature] Shape143
  shape: bbox 6.612 x 6.612 x 2e-07 mm, 0 faces, 0 solids (baked)
FEATURE [Part::Feature] Shape162
  shape: bbox 2.325 x 2e-07 x 2e-07 mm, 0 faces, 0 solids (baked)
FEATURE [Part::Feature] Shape150
  shape: bbox 1.862 x 1.862 x 2e-07 mm, 0 faces, 0 solids (baked)
FEATURE [Part::Feature] Shape169
  shape: bbox 2e-07 x 1.698 x 2e-07 mm, 0 faces, 0 solids (baked)
FEATURE [Part::Feature] Shape134
  shape: bbox 5.865 x 5.865 x 2e-07 mm, 0 faces, 0 solids (baked)
FEATURE [Part::Feature] Shape171
  shape: bbox 2e-07 x 0.8489 x 2e-07 mm, 0 faces, 0 solids (baked)
FEATURE [Part::Feature] Shape172
  shape: bbox 2e-07 x 0.4121 x 2e-07 mm, 0 faces, 0 solids (baked)
FEATURE [Part::Feature] Shape133
  shape: bbox 2e-07 x 3.089 x 2e-07 mm, 0 faces, 0 solids (baked)
FEATURE [Part::Feature] Shape174
  shape: bbox 2e-07 x 0.8606 x 2e-07 mm, 0 faces, 0 solids (baked)
FEATURE [Part::Feature] Shape140
  shape: bbox 0.4445 x 0.4445 x 2e-07 mm, 0 faces, 0 solids (baked)
FEATURE [Part::Feature] Shape157
  shape: bbox 2e-07 x 12.14 x 2e-07 mm, 0 faces, 0 solids (baked)
FEATURE [Part::Feature] Shape175
  shape: bbox 2e-07 x 0.8606 x 2e-07 mm, 0 faces, 0 solids (baked)
FEATURE [Part::Feature] Shape176
  shape: bbox 2e-07 x 0.8606 x 2e-07 mm, 0 faces, 0 solids (baked)
FEATURE [Part::Feature] Shape177
  shape: bbox 2e-07 x 0.8606 x 2e-07 mm, 0 faces, 0 solids (baked)
FEATURE [Part::Feature] Shape144
  shape: bbox 2e-07 x 13.79 x 2e-07 mm, 0 faces, 0 solids (baked)
FEATURE [Part::Feature] Shape145
  shape: bbox 0.508 x 0.508 x 2e-07 mm, 0 faces, 0 solids (baked)
FEATURE [Part::Feature] Shape245
  shape: bbox 2e-07 x 6.4 x 2e-07 mm, 0 faces, 0 solids (baked)
FEATURE [Part::Feature] Shape269
  shape: bbox 0.254 x 2e-07 x 2e-07 mm, 0 faces, 0 solids (baked)
FEATURE [Part::Feature] Shape224
  shape: bbox 2.015 x 2e-07 x 2e-07 mm, 0 faces, 0 solids (baked)
FEATURE [Part::Feature] Shape243
  shape: bbox 1.016 x 2e-07 x 2e-07 mm, 0 faces, 0 solids (baked)
FEATURE [Part::Feature] Shape226
  shape: bbox 2e-07 x 1.016 x 2e-07 mm, 0 faces, 0 solids (baked)
FEATURE [Part::Feature] Shape242
  shape: bbox 2e-07 x 1.016 x 2e-07 mm, 0 faces, 0 solids (baked)
FEATURE [Part::Feature] Shape275
  shape: bbox 5.08 x 2e-07 x 2e-07 mm, 0 faces, 0 solids (baked)
FEATURE [Part::Feature] Shape276
  shape: bbox 2e-07 x 0.254 x 2e-07 mm, 0 faces, 0 solids (baked)
FEATURE [Part::Feature] Shape230
  shape: bbox 1.016 x 2e-07 x 2e-07 mm, 0 faces, 0 solids (baked)
FEATURE [Part::Feature] Shape234
  shape: bbox 2e-07 x 2.032 x 2e-07 mm, 0 faces, 0 solids (baked)
FEATURE [Part::Feature] Shape228
  shape: bbox 1.016 x 2e-07 x 2e-07 mm, 0 faces, 0 solids (baked)
FEATURE [Part::Feature] Shape219
  shape: bbox 2e-07 x 1.524 x 2e-07 mm, 0 faces, 0 solids (baked)
FEATURE [Part::Feature] Shape251
  shape: bbox 2e-07 x 10.5 x 2e-07 mm, 0 faces, 0 solids (baked)
FEATURE [Part::Feature] Shape220
  shape: bbox 2.015 x 2e-07 x 2e-07 mm, 0 faces, 0 solids (baked)
FEATURE [Part::Feature] Shape229
  shape: bbox 2e-07 x 2.032 x 2e-07 mm, 0 faces, 0 solids (baked)
FEATURE [Part::Feature] Shape235
  shape: bbox 1.016 x 2e-07 x 2e-07 mm, 0 faces, 0 solids (baked)
FEATURE [Part::Feature] Shape236
  shape: bbox 2e-07 x 1.016 x 2e-07 mm, 0 faces, 0 solids (baked)
FEATURE [Part::Feature] Shape247
  shape: bbox 2e-07 x 6.6 x 2e-07 mm, 0 faces, 0 solids (baked)
FEATURE [Part::Feature] Shape252
  shape: bbox 2e-07 x 10.5 x 2e-07 mm, 0 faces, 0 solids (baked)
FEATURE [Part::Feature] Shape253
  shape: bbox 2e-07 x 10.5 x 2e-07 mm, 0 faces, 0 solids (baked)
FEATURE [Part::Feature] Shape263
  shape: bbox 3.175 x 2e-07 x 2e-07 mm, 0 faces, 0 solids (baked)
FEATURE [Part::Feature] Shape264
  shape: bbox 2e-07 x 2.54 x 2e-07 mm, 0 faces, 0 solids (baked)
FEATURE [Part::Feature] Shape268
  shape: bbox 0.254 x 2e-07 x 2e-07 mm, 0 faces, 0 solids (baked)
FEATURE [Part::Feature] Shape232
  shape: bbox 2e-07 x 1.016 x 2e-07 mm, 0 faces, 0 solids (baked)
FEATURE [Part::Feature] Shape248
  shape: bbox 2e-07 x 6.6 x 2e-07 mm, 0 faces, 0 solids (baked)
FEATURE [Part::Feature] Shape258
  shape: bbox 2e-07 x 0.762 x 2e-07 mm, 0 faces, 0 solids (baked)
FEATURE [Part::Feature] Shape238
  shape: bbox 1.016 x 2e-07 x 2e-07 mm, 0 faces, 0 solids (baked)
FEATURE [Part::Feature] Shape239
  shape: bbox 2e-07 x 2.032 x 2e-07 mm, 0 faces, 0 solids (baked)
FEATURE [Part::Feature] Shape254
  shape: bbox 2e-07 x 10.5 x 2e-07 mm, 0 faces, 0 solids (baked)
FEATURE [Part::Feature] Shape261
  shape: bbox 2e-07 x 0.762 x 2e-07 mm, 0 faces, 0 solids (baked)
FEATURE [Part::Feature] Shape237
  shape: bbox 2e-07 x 1.016 x 2e-07 mm, 0 faces, 0 solids (baked)
FEATURE [Part::Feature] Shape241
  shape: bbox 2e-07 x 1.016 x 2e-07 mm, 0 faces, 0 solids (baked)
FEATURE [Part::Feature] Shape244
  shape: bbox 2e-07 x 2.032 x 2e-07 mm, 0 faces, 0 solids (baked)
FEATURE [Part::Feature] Shape257
  shape: bbox 2e-07 x 0.762 x 2e-07 mm, 0 faces, 0 solids (baked)
FEATURE [Part::Feature] Shape225
  shape: bbox 1.016 x 2e-07 x 2e-07 mm, 0 faces, 0 solids (baked)
FEATURE [Part::Feature] Shape231
  shape: bbox 2e-07 x 1.016 x 2e-07 mm, 0 faces, 0 solids (baked)
FEATURE [Part::Feature] Shape227
  shape: bbox 2e-07 x 1.016 x 2e-07 mm, 0 faces, 0 solids (baked)
FEATURE [Part::Feature] Shape233
  shape: bbox 1.016 x 2e-07 x 2e-07 mm, 0 faces, 0 solids (baked)
FEATURE [Part::Feature] Shape240
  shape: bbox 1.016 x 2e-07 x 2e-07 mm, 0 faces, 0 solids (baked)
FEATURE [Part::Feature] Shape246
  shape: bbox 2e-07 x 6.4 x 2e-07 mm, 0 faces, 0 solids (baked)
FEATURE [Part::Feature] Shape255
  shape: bbox 0.254 x 2e-07 x 2e-07 mm, 0 faces, 0 solids (baked)
FEATURE [Part::Feature] Shape221
  shape: bbox 2e-07 x 35.4 x 2e-07 mm, 0 faces, 0 solids (baked)
FEATURE [Part::Feature] Shape249
  shape: bbox 9 x 2e-07 x 2e-07 mm, 0 faces, 0 solids (baked)
FEATURE [Part::Feature] Shape259
  shape: bbox 5.08 x 2e-07 x 2e-07 mm, 0 faces, 0 solids (baked)
FEATURE [Part::Feature] Shape256
  shape: bbox 0.254 x 2e-07 x 2e-07 mm, 0 faces, 0 solids (baked)
FEATURE [Part::Feature] Shape222
  shape: bbox 5.3 x 2e-07 x 2e-07 mm, 0 faces, 0 solids (baked)
FEATURE [Part::Feature] Shape260
  shape: bbox 2e-07 x 0.762 x 2e-07 mm, 0 faces, 0 solids (baked)
FEATURE [Part::Feature] Shape265
  shape: bbox 5.08 x 2e-07 x 2e-07 mm, 0 faces, 0 solids (baked)
FEATURE [Part::Feature] Shape266
  shape: bbox 2e-07 x 2.54 x 2e-07 mm, 0 faces, 0 solids (baked)
FEATURE [Part::Feature] Shape223
  shape: bbox 2e-07 x 35.4 x 2e-07 mm, 0 faces, 0 solids (baked)
FEATURE [Part::Feature] Shape250
  shape: bbox 9 x 2e-07 x 2e-07 mm, 0 faces, 0 solids (baked)
FEATURE [Part::Feature] Shape267
  shape: bbox 1.905 x 2e-07 x 2e-07 mm, 0 faces, 0 solids (baked)
FEATURE [Part::Feature] Shape262
  shape: bbox 5.08 x 2e-07 x 2e-07 mm, 0 faces, 0 solids (baked)
FEATURE [Part::Feature] Shape270
  shape: bbox 2e-07 x 0.762 x 2e-07 mm, 0 faces, 0 solids (baked)
FEATURE [Part::Feature] Shape271
  shape: bbox 2e-07 x 0.762 x 2e-07 mm, 0 faces, 0 solids (baked)
FEATURE [Part::Feature] Shape272
  shape: bbox 5.08 x 2e-07 x 2e-07 mm, 0 faces, 0 solids (baked)
FEATURE [Part::Feature] Shape273
  shape: bbox 2e-07 x 0.762 x 2e-07 mm, 0 faces, 0 solids (baked)
FEATURE [Part::Feature] Shape274
  shape: bbox 2e-07 x 0.762 x 2e-07 mm, 0 faces, 0 solids (baked)
FEATURE [Part::Feature] Shape277
  shape: bbox 2e-07 x 0.254 x 2e-07 mm, 0 faces, 0 solids (baked)
FEATURE [Part::Feature] Shape278
  shape: bbox 0.762 x 2e-07 x 2e-07 mm, 0 faces, 0 solids (baked)
FEATURE [Part::Feature] Shape279
  shape: bbox 0.762 x 2e-07 x 2e-07 mm, 0 faces, 0 solids (baked)
FEATURE [Part::Feature] Shape280
  shape: bbox 2e-07 x 5.08 x 2e-07 mm, 0 faces, 0 solids (baked)
FEATURE [Part::Feature] Shape281
  shape: bbox 0.762 x 2e-07 x 2e-07 mm, 0 faces, 0 solids (baked)
FEATURE [Part::Feature] Shape282
  shape: bbox 0.762 x 2e-07 x 2e-07 mm, 0 faces, 0 solids (baked)
FEATURE [Part::Feature] Shape194
  shape: bbox 1.905 x 2e-07 x 2e-07 mm, 0 faces, 0 solids (baked)
FEATURE [Part::Feature] Shape182
  shape: bbox 20.32 x 2e-07 x 2e-07 mm, 0 faces, 0 solids (baked)
FEATURE [Part::Feature] Shape201
  shape: bbox 2e-07 x 7.62 x 2e-07 mm, 0 faces, 0 solids (baked)
FEATURE [Part::Feature] Shape215
  shape: bbox 5.207 x 2e-07 x 2e-07 mm, 0 faces, 0 solids (baked)
FEATURE [Part::Feature] Shape216
  shape: bbox 2e-07 x 2.743 x 2e-07 mm, 0 faces, 0 solids (baked)
FEATURE [Part::Feature] Shape184
  shape: bbox 20.32 x 2e-07 x 2e-07 mm, 0 faces, 0 solids (baked)
FEATURE [Part::Feature] Shape217
  shape: bbox 2e-07 x 2.743 x 2e-07 mm, 0 faces, 0 solids (baked)
FEATURE [Part::Feature] Shape218
  shape: bbox 1.524 x 2e-07 x 2e-07 mm, 0 faces, 0 solids (baked)
FEATURE [Part::Feature] Shape189
  shape: bbox 2e-07 x 11.43 x 2e-07 mm, 0 faces, 0 solids (baked)
FEATURE [Part::Feature] Shape200
  shape: bbox 2.54 x 2e-07 x 2e-07 mm, 0 faces, 0 solids (baked)
FEATURE [Part::Feature] Shape203
  shape: bbox 2e-07 x 5.715 x 2e-07 mm, 0 faces, 0 solids (baked)
FEATURE [Part::Feature] Shape196
  shape: bbox 7.62 x 2e-07 x 2e-07 mm, 0 faces, 0 solids (baked)
FEATURE [Part::Feature] Shape199
  shape: bbox 2e-07 x 1.905 x 2e-07 mm, 0 faces, 0 solids (baked)
FEATURE [Part::Feature] Shape179
  shape: bbox 2e-07 x 0.8606 x 2e-07 mm, 0 faces, 0 solids (baked)
FEATURE [Part::Feature] Shape204
  shape: bbox 2e-07 x 17.02 x 2e-07 mm, 0 faces, 0 solids (baked)
FEATURE [Part::Feature] Shape205
  shape: bbox 10.92 x 2e-07 x 2e-07 mm, 0 faces, 0 solids (baked)
FEATURE [Part::Feature] Shape210
  shape: bbox 2e-07 x 5.207 x 2e-07 mm, 0 faces, 0 solids (baked)
FEATURE [Part::Feature] Shape207
  shape: bbox 10.92 x 2e-07 x 2e-07 mm, 0 faces, 0 solids (baked)
FEATURE [Part::Feature] Shape188
  shape: bbox 2e-07 x 12.7 x 2e-07 mm, 0 faces, 0 solids (baked)
FEATURE [Part::Feature] Shape190
  shape: bbox 2e-07 x 1.27 x 2e-07 mm, 0 faces, 0 solids (baked)
FEATURE [Part::Feature] Shape183
  shape: bbox 2e-07 x 15.24 x 2e-07 mm, 0 faces, 0 solids (baked)
FEATURE [Part::Feature] Shape186
  shape: bbox 5.588 x 2e-07 x 2e-07 mm, 0 faces, 0 solids (baked)
FEATURE [Part::Feature] Shape192
  shape: bbox 2e-07 x 10.16 x 2e-07 mm, 0 faces, 0 solids (baked)
FEATURE [Part::Feature] Shape195
  shape: bbox 2e-07 x 2.54 x 2e-07 mm, 0 faces, 0 solids (baked)
FEATURE [Part::Feature] Shape181
  shape: bbox 2e-07 x 0.4303 x 2e-07 mm, 0 faces, 0 solids (baked)
FEATURE [Part::Feature] Shape187
  shape: bbox 5.588 x 2e-07 x 2e-07 mm, 0 faces, 0 solids (baked)
FEATURE [Part::Feature] Shape185
  shape: bbox 2e-07 x 15.24 x 2e-07 mm, 0 faces, 0 solids (baked)
FEATURE [Part::Feature] Shape193
  shape: bbox 1.27 x 2e-07 x 2e-07 mm, 0 faces, 0 solids (baked)
FEATURE [Part::Feature] Shape197
  shape: bbox 2e-07 x 2.54 x 2e-07 mm, 0 faces, 0 solids (baked)
FEATURE [Part::Feature] Shape202
  shape: bbox 2.54 x 2e-07 x 2e-07 mm, 0 faces, 0 solids (baked)
FEATURE [Part::Feature] Shape191
  shape: bbox 1.27 x 2e-07 x 2e-07 mm, 0 faces, 0 solids (baked)
FEATURE [Part::Feature] Shape198
  shape: bbox 5.715 x 2e-07 x 2e-07 mm, 0 faces, 0 solids (baked)
FEATURE [Part::Feature] Shape209
  shape: bbox 2.743 x 2e-07 x 2e-07 mm, 0 faces, 0 solids (baked)
FEATURE [Part::Feature] Shape180
  shape: bbox 5.9 x 2e-07 x 2e-07 mm, 0 faces, 0 solids (baked)
FEATURE [Part::Feature] Shape211
  shape: bbox 2.743 x 2e-07 x 2e-07 mm, 0 faces, 0 solids (baked)
FEATURE [Part::Feature] Shape212
  shape: bbox 2.743 x 2e-07 x 2e-07 mm, 0 faces, 0 solids (baked)
FEATURE [Part::Feature] Shape213
  shape: bbox 5.207 x 2e-07 x 2e-07 mm, 0 faces, 0 solids (baked)
FEATURE [Part::Feature] Shape208
  shape: bbox 2e-07 x 5.207 x 2e-07 mm, 0 faces, 0 solids (baked)
FEATURE [Part::Feature] Shape206
  shape: bbox 2e-07 x 17.02 x 2e-07 mm, 0 faces, 0 solids (baked)
FEATURE [Part::Feature] Shape214
  shape: bbox 2e-07 x 2.743 x 2e-07 mm, 0 faces, 0 solids (baked)
FEATURE [App::Part] Part023  label="PCB002"
  Group = -> [Shape627,Shape620,Shape612,Shape595,Shape626,Shape596,Shape628,Shape613,Shape601,Shape629,Shape622,Shape597,Shape609,Shape614,Shape621,Shape615,Shape618,Shape605,Shape591,Shape592,Shape598,Shape619,Shape623,Shape617,Shape607,Shape600,Shape593,Shape625,Shape624,Shape594,Shape599,Shape611,Shape616,Shape602,Shape603,Shape606,Shape610,Shape604,Shape608,Shape584,Shape585,Shape588,Shape583,Shape586,+537 more]
  Origin = -> Origin022
  Placement = pos=(0,115,1.6) rot=(0,0,1;1.5708rad)
FEATURE [App::Part] Part022  label="FPCB"
  Group = -> [Part023,Box021259]
  Origin = -> Origin023
  Placement = pos=(111.5,-226.5,66) rot=(0,1,0;3.14159rad)
FEATURE [Part::Cylinder] Cylinder112024025003003006010004276076  label="Válec419"
  Angle = 360
  AttacherType = Attacher::AttachEngine3D
  Height = 53
  Placement = pos=(-26.5,-46,11.5) rot=(0,1,0;1.5708rad)
  Radius = 5
FEATURE [Part::Cylinder] Cylinder112024025003003006010004276077  label="cy059"
  Angle = 360
  AttacherType = Attacher::AttachEngine3D
  Height = 24
  Placement = pos=(0,-53,9) rot=(0,0,1;0rad)
  Radius = 15
FEATURE [Part::Box] Box021264  label="Krychle253"
  AttacherType = Attacher::AttachEngine3D
  Height = 4.6
  Length = 53
  Placement = pos=(-26.5,-64,9.2) rot=(0,0,1;0rad)
  Width = 18
FEATURE [Part::Box] Box021265  label="Krychle254"
  AttacherType = Attacher::AttachEngine3D
  Height = 12.5
  Length = 42
  Placement = pos=(-21,-106,5.5) rot=(0,0,1;0rad)
  Width = 80
FEATURE [Part::Cylinder] Cylinder112024025003003006010004276079  label="Válec420"
  Angle = 360
  AttacherType = Attacher::AttachEngine3D
  Height = 53
  Placement = pos=(-26.5,-64,11.5) rot=(0,1,0;1.5708rad)
  Radius = 2.3
FEATURE [Part::Cylinder] Cylinder112024025003003006010004276080  label="Válec421"
  Angle = 360
  AttacherType = Attacher::AttachEngine3D
  Height = 53
  Placement = pos=(-26.5,-46,11.5) rot=(0,1,0;1.5708rad)
  Radius = 2.3
FEATURE [Part::Box] Box021266  label="Krychle255"
  AttacherType = Attacher::AttachEngine3D
  Height = 23.5
  Length = 50
  Placement = pos=(-25,-106,6) rot=(0,0,1;0rad)
  Width = 80
FEATURE [Part::Cylinder] Cylinder112024025003003006010004276081  label="Válec422"
  Angle = 360
  AttacherType = Attacher::AttachEngine3D
  Height = 53
  Placement = pos=(-26.5,-64,11.5) rot=(0,1,0;1.5708rad)
  Radius = 5
FEATURE [Part::Box] Box021267  label="Krychle256"
  AttacherType = Attacher::AttachEngine3D
  Height = 10
  Length = 53
  Placement = pos=(-26.5,-64,6.5) rot=(0,0,1;0rad)
  Width = 18
FEATURE [Part::MultiFuse] Fusion005043005007002078086001015  label="Motor M004"
  Shapes = -> [Cylinder112024025003003006010004276081,Cylinder112024025003003006010004276076,Box021267,Box021266]
FEATURE [Part::Cylinder] Cylinder112024025003003006010004276082  label="cy060"
  Angle = 360
  AttacherType = Attacher::AttachEngine3D
  Height = 24
  Placement = pos=(-17.5,-53,9) rot=(0,0,1;0rad)
  Radius = 1.8
FEATURE [Part::Cylinder] Cylinder112024025003003006010004276083  label="cy061"
  Angle = 360
  AttacherType = Attacher::AttachEngine3D
  Height = 24
  Placement = pos=(17.5,-53,9) rot=(0,0,1;0rad)
  Radius = 1.8
FEATURE [Part::Cylinder] Cylinder112024025003003006010004276084  label="cy062"
  Angle = 360
  AttacherType = Attacher::AttachEngine3D
  Height = 6
  Placement = pos=(-17.5,-53,18) rot=(0,0,1;0rad)
  Radius = 3.8
FEATURE [Part::Cylinder] Cylinder112024025003003006010004276085  label="cy063"
  Angle = 360
  AttacherType = Attacher::AttachEngine3D
  Height = 6
  Placement = pos=(17.5,-53,18) rot=(0,0,1;0rad)
  Radius = 3.8
FEATURE [Part::Box] Box021268  label="Krychle257"
  AttacherType = Attacher::AttachEngine3D
  Height = 6
  Length = 4
  Placement = pos=(-17.5,-56.8,18) rot=(0,0,1;0rad)
  Width = 7.6
FEATURE [Part::Box] Box021269  label="Krychle258"
  AttacherType = Attacher::AttachEngine3D
  Height = 6
  Length = 4
  Placement = pos=(13.5,-56.8,18) rot=(0,0,1;0rad)
  Width = 7.6
FEATURE [Part::Box] Box021270  label="Krychle259"
  AttacherType = Attacher::AttachEngine3D
  Height = 20
  Length = 19
  Placement = pos=(-9.5,-73,18) rot=(0,0,1;0rad)
  Width = 20
FEATURE [Part::Cylinder] Cylinder112024025003003006010004276086  label="Válec423"
  Angle = 360
  AttacherType = Attacher::AttachEngine3D
  Height = 53
  Placement = pos=(-26.5,-31.5,24.5) rot=(0,1,0;1.5708rad)
  Radius = 1.25
FEATURE [Part::Cylinder] Cylinder112024025003003006010004276087  label="Válec424"
  Angle = 360
  AttacherType = Attacher::AttachEngine3D
  Height = 53
  Placement = pos=(-26.5,-100.5,24.5) rot=(0,1,0;1.5708rad)
  Radius = 1.25
FEATURE [Part::Box] Box021271  label="vitreni"
  AttacherType = Attacher::AttachEngine3D
  Height = 45
  Length = 49
  Placement = pos=(-24.5,-105.5,18) rot=(0,0,1;0rad)
  Width = 79
FEATURE [Part::Box] Box021272  label="Vnejsi"
  AttacherType = Attacher::AttachEngine3D
  Height = 47
  Length = 53
  Placement = pos=(-26.5,-107.5,18) rot=(0,0,1;0rad)
  Width = 83
FEATURE [Part::Box] Box021273  label="vitreni001"
  AttacherType = Attacher::AttachEngine3D
  Height = 11.5
  Length = 50
  Placement = pos=(-25,-106,18) rot=(0,0,1;0rad)
  Width = 80
FEATURE [Part::MultiFuse] Fusion005043005007002078086001017
  Shapes = -> [Box021271,Box021273]
FEATURE [Part::Cut] Cut018020020009027020002003004004026003005007018
  Base = -> Box021272
  Tool = -> Fusion005043005007002078086001017
FEATURE [Part::Cylinder] Cylinder112024025003003006010004276088  label="Válec425"
  Angle = 360
  AttacherType = Attacher::AttachEngine3D
  Height = 6
  Placement = pos=(20.5,-30,58) rot=(0,0,1;0rad)
  Radius = 4
FEATURE [Part::Cylinder] Cylinder112024025003003006010004276089  label="Válec426"
  Angle = 360
  AttacherType = Attacher::AttachEngine3D
  Height = 6
  Placement = pos=(-20.5,-30,58) rot=(0,0,1;0rad)
  Radius = 4
FEATURE [Part::Cylinder] Cylinder112024025003003006010004276090  label="Válec427"
  Angle = 360
  AttacherType = Attacher::AttachEngine3D
  Height = 6
  Placement = pos=(-20.5,-102,58) rot=(0,0,1;0rad)
  Radius = 4
FEATURE [Part::Cylinder] Cylinder112024025003003006010004276091  label="Válec428"
  Angle = 360
  AttacherType = Attacher::AttachEngine3D
  Height = 6
  Placement = pos=(20.5,-102,58) rot=(0,0,1;0rad)
  Radius = 4
FEATURE [Part::MultiFuse] Fusion005043005007002078086001018  label="sloupky"
  Shapes = -> [Cylinder112024025003003006010004276088,Cylinder112024025003003006010004276090,Cylinder112024025003003006010004276089,Cylinder112024025003003006010004276091]
FEATURE [Part::MultiFuse] Fusion005043005007002078086001019  label="Vnitrek"
  Shapes = -> [Fusion005043005007002078086001018,Cut018020020009027020002003004004026003005007018]
FEATURE [Part::Cylinder] Cylinder112024025003003006010004276092  label="Válec429"
  Angle = 360
  AttacherType = Attacher::AttachEngine3D
  Height = 5
  Placement = pos=(20.5,-102,58) rot=(0,0,1;0rad)
  Radius = 0.8
FEATURE [Part::Cylinder] Cylinder112024025003003006010004276093  label="Válec430"
  Angle = 360
  AttacherType = Attacher::AttachEngine3D
  Height = 5
  Placement = pos=(-20.5,-102,58) rot=(0,0,1;0rad)
  Radius = 0.8
FEATURE [Part::Cylinder] Cylinder112024025003003006010004276094  label="Válec431"
  Angle = 360
  AttacherType = Attacher::AttachEngine3D
  Height = 5
  Placement = pos=(20.5,-30,58) rot=(0,0,1;0rad)
  Radius = 0.8
FEATURE [Part::Cylinder] Cylinder112024025003003006010004276095  label="Válec432"
  Angle = 360
  AttacherType = Attacher::AttachEngine3D
  Height = 5
  Placement = pos=(-20.5,-30,58) rot=(0,0,1;0rad)
  Radius = 0.8
FEATURE [Part::MultiFuse] Fusion005043005007002078086001020  label="diry"
  Shapes = -> [Cylinder112024025003003006010004276094,Cylinder112024025003003006010004276093,Cylinder112024025003003006010004276095,Cylinder112024025003003006010004276092]
FEATURE [Part::Cylinder] Cylinder112024025003003006010004276096  label="Led"
  Angle = 360
  AttacherType = Attacher::AttachEngine3D
  Height = 10
  Placement = pos=(0.5,-101.2,56) rot=(0,0,1;0rad)
  Radius = 1.8
FEATURE [Part::Cylinder] Cylinder112024025003003006010004276097  label="Válec433"
  Angle = 360
  AttacherType = Attacher::AttachEngine3D
  Height = 53
  Placement = pos=(-26.5,-31.5,24.5) rot=(0,1,0;1.5708rad)
  Radius = 1.7
FEATURE [Part::Cylinder] Cylinder112024025003003006010004276098  label="Válec434"
  Angle = 360
  AttacherType = Attacher::AttachEngine3D
  Height = 53
  Placement = pos=(-26.5,-100.5,24.5) rot=(0,1,0;1.5708rad)
  Radius = 1.7
FEATURE [Part::Cylinder] Cylinder112024025003003006010004276099  label="Led001"
  Angle = 360
  AttacherType = Attacher::AttachEngine3D
  Height = 10
  Placement = pos=(0.5,-95.2,56) rot=(0,0,1;0rad)
  Radius = 1.8
FEATURE [Part::Box] Box021274  label="RJ"
  AttacherType = Attacher::AttachEngine3D
  Height = 13
  Length = 15
  Placement = pos=(-18,-108,43) rot=(0,0,1;0rad)
  Width = 10
FEATURE [Part::Box] Box021275  label="Usdb"
  AttacherType = Attacher::AttachEngine3D
  Height = 4
  Length = 9
  Placement = pos=(6,-108,51.5) rot=(0,0,1;0rad)
  Width = 10
FEATURE [Part::Cylinder] Cylinder112024025003003006010004276100  label="PWR"
  Angle = 360
  AttacherType = Attacher::AttachEngine3D
  Height = 10
  Placement = pos=(10.5,-101,42) rot=(1,0,0;1.5708rad)
  Radius = 4.2
FEATURE [Part::Part2DObjectPython] ShapeString003  # Draft 2D object (typed FeaturePython)
  FontFile = <path>
  Placement = pos=(5,-97,64) rot=(0,0,1;0rad)
  Size = 4
  String = Stat
  Tracking = 0
FEATURE [Part::Extrusion] Extrude026  label="Stat"
  Base = -> ShapeString003
  Dir = (0,0,1)
  DirMode = 2
  FaceMakerClass = Part::FaceMakerBullseye
  LengthFwd = 1
  LengthRev = 0
  Solid = true
  Symmetric = false
FEATURE [Part::Part2DObjectPython] ShapeString004  # Draft 2D object (typed FeaturePython)
  FontFile = <path>
  Placement = pos=(5,-103,64) rot=(0,0,1;0rad)
  Size = 4
  String = Run
  Tracking = 0
FEATURE [Part::Extrusion] Extrude027  label="Run"
  Base = -> ShapeString004
  Dir = (0,0,1)
  DirMode = 2
  FaceMakerClass = Part::FaceMakerBullseye
  LengthFwd = 1
  LengthRev = 0
  Solid = true
  Symmetric = false
FEATURE [Part::Part2DObjectPython] ShapeString005  # Draft 2D object (typed FeaturePython)
  FontFile = <path>
  Placement = pos=(5,-106.5,60) rot=(1,0,0;1.5708rad)
  Size = 4
  String = USB
  Tracking = 0
FEATURE [Part::Extrusion] Extrude028  label="USB"
  Base = -> ShapeString005
  Dir = (0,-1,0)
  DirMode = 2
  FaceMakerClass = Part::FaceMakerBullseye
  LengthFwd = 1
  LengthRev = 0
  Placement = pos=(0,0,-2.5) rot=(0,0,1;0rad)
  Solid = true
  Symmetric = false
FEATURE [Part::Part2DObjectPython] ShapeString006  # Draft 2D object (typed FeaturePython)
  FontFile = <path>
  Placement = pos=(-15.5,-106.5,60) rot=(1,0,0;1.5708rad)
  Size = 4
  String = Aux
  Tracking = 0
FEATURE [Part::Extrusion] Extrude029  label="Aux"
  Base = -> ShapeString006
  Dir = (0,-1,0)
  DirMode = 2
  FaceMakerClass = Part::FaceMakerBullseye
  LengthFwd = 1
  LengthRev = 0
  Placement = pos=(0,0,-2) rot=(0,0,1;0rad)
  Solid = true
  Symmetric = false
FEATURE [Part::Part2DObjectPython] ShapeString007  # Draft 2D object (typed FeaturePython)
  FontFile = <path>
  Placement = pos=(2,-106.5,40) rot=(1,0,0;1.5708rad)
  Size = 4
  String = DC12V
  Tracking = 0
FEATURE [Part::Extrusion] Extrude030  label="12V"
  Base = -> ShapeString007
  Dir = (0,-1,0)
  DirMode = 2
  FaceMakerClass = Part::FaceMakerBullseye
  LengthFwd = 1
  LengthRev = 0
  Placement = pos=(0,0,-10) rot=(0,0,1;0rad)
  Solid = true
  Symmetric = false
FEATURE [Part::Part2DObjectPython] ShapeString008  # Draft 2D object (typed FeaturePython)
  FontFile = <path>
  Placement = pos=(-20,-45,64) rot=(0,0,1;0rad)
  Size = 7
  String =  Focuser
  Tracking = 0
FEATURE [Part::Extrusion] Extrude031  label="Focuser"
  Base = -> ShapeString008
  Dir = (0,0,1)
  DirMode = 2
  FaceMakerClass = Part::FaceMakerBullseye
  LengthFwd = 1
  LengthRev = 0
  Solid = true
  Symmetric = false
FEATURE [Part::Box] Box021276  label="flash"
  AttacherType = Attacher::AttachEngine3D
  Height = 3
  Length = 9
  Placement = pos=(20,-84,49) rot=(0,0,1;0rad)
  Width = 8
FEATURE [Part::Part2DObjectPython] ShapeString009  # Draft 2D object (typed FeaturePython)
  FontFile = <path>
  Placement = pos=(0,0,0) rot=(1,0,0;1.5708rad)
  Size = 3
  String = Flash
  Tracking = 0
FEATURE [Part::Extrusion] Extrude032  label="Flash"
  Base = -> ShapeString009
  Dir = (0,-1,0)
  DirMode = 2
  FaceMakerClass = Part::FaceMakerBullseye
  LengthFwd = 1
  LengthRev = 0
  Placement = pos=(25.5,-85,54) rot=(0,0,1;1.5708rad)
  Solid = true
  Symmetric = false
FEATURE [Part::MultiFuse] Fusion005043005007002078086001022  label="testy"
  Shapes = -> [Extrude026,Extrude027,Extrude028,Extrude029,Extrude030,Extrude031,Extrude032]
FEATURE [Part::MultiFuse] Fusion005043005007002078086001021  label="otvory"
  Shapes = -> [Fusion005043005007002078086001020,Cylinder112024025003003006010004276094,Cylinder112024025003003006010004276093,Cylinder112024025003003006010004276095,Cylinder112024025003003006010004276092,Cylinder112024025003003006010004276096,Cylinder112024025003003006010004276097,Cylinder112024025003003006010004276098,Cylinder112024025003003006010004276099,Box021274,Cylinder112024025003003006010004276100,+3 more]
FEATURE [Part::Cut] Cut018020020009027020002003004004026003005007019  label="Myfocuser Cover"
  Base = -> Fusion005043005007002078086001019
  Tool = -> Fusion005043005007002078086001021
FEATURE [Part::Fillet] Fillet028003009  label="MyfOCUS cOVER"
  Base = -> Cut018020020009027020002003004004026003005007019
  Edges = 8 edges r=1: [Edge395,Edge396,Edge397,Edge484,Edge485,Edge486,Edge497,Edge667]
FEATURE [Part::Feature] Fillet028003009001  label="MyfOCUS cOVER001"
  Placement = pos=(0,0,8) rot=(0,0,1;0rad)
  shape: bbox 53 x 83 x 47 mm, 694 faces (baked)
FEATURE [Part::Feature] Cut018020020009027020002003004004026003005007020  label="Pulley-GT2-16_28BYJ--049"
  Placement = pos=(0,0,0) rot=(1,0,0;3.14159rad)
  shape: bbox 12.68 x 12.68 x 11 mm, 393 faces (baked)
FEATURE [Part::Cylinder] Cylinder112024025003003006010004276103  label="cy064"
  Angle = 360
  AttacherType = Attacher::AttachEngine3D
  Height = 6
  Placement = pos=(0,-45,17) rot=(0,0,1;0rad)
  Radius = 12
FEATURE [Part::MultiFuse] Fusion005043005007002078086001016  label="Motor vyrezy003"
  Shapes = -> [Box021265,Cylinder112024025003003006010004276077,Cylinder112024025003003006010004276079,Cylinder112024025003003006010004276080,Box021264,Cylinder112024025003003006010004276082,Cylinder112024025003003006010004276083,Cylinder112024025003003006010004276084,Cylinder112024025003003006010004276085,Box021268,Box021269,Box021270,Cylinder112024025003003006010004276086,+2 more]
FEATURE [Part::Cut] Cut018020020009027020002003004004026003005007017  label="AF Motor003"
  Base = -> Fusion005043005007002078086001015
  Tool = -> Fusion005043005007002078086001016
FEATURE [Part::Fillet] Fillet028003009002  label="MyFokusMotor"
  Base = -> Cut018020020009027020002003004004026003005007017
  Edges = 12 edges r=1: [Edge4,Edge7,Edge17,Edge21,Edge25,Edge29,Edge41,Edge43,Edge152,Edge155,Edge158,Edge159]
FEATURE [Part::Feature] Cut018020020009027020002003004004026003005007022  label="Pulley-GT2-16_28BYJ--050"
  Placement = pos=(0,0,0) rot=(1,0,0;3.14159rad)
  shape: bbox 12.68 x 12.68 x 11 mm, 393 faces (baked)
FEATURE [Part::Cylinder] Cylinder112024025003003006010004276104  label="Válec437"
  Angle = 360
  AttacherType = Attacher::AttachEngine3D
  Height = 3
  Placement = pos=(0,0,1.5) rot=(0,0,1;0rad)
  Radius = 6.3
FEATURE [Part::MultiFuse] Fusion005043005007002078086001024
  Shapes = -> [Cut018020020009027020002003004004026003005007022,Cylinder112024025003003006010004276104]
FEATURE [Part::Cylinder] Cylinder112024025003003006010004276105  label="Válec438"
  Angle = 360
  AttacherType = Attacher::AttachEngine3D
  Height = 5
  Placement = pos=(0,0,1.5) rot=(0,0,1;0rad)
  Radius = 2.75
FEATURE [Part::Cut] Cut018020020009027020002003004004026003005007023  label="pastorek001"
  Base = -> Fusion005043005007002078086001024
  Tool = -> Cylinder112024025003003006010004276105
FEATURE [Part::Cylinder] Cylinder112024025003003006010004276106  label="Válec439"
  Angle = 360
  AttacherType = Attacher::AttachEngine3D
  Height = 11
  Placement = pos=(0,0,-9.5) rot=(0,0,1;0rad)
  Radius = 3.9
FEATURE [Part::Cylinder] Cylinder112024025003003006010004276107  label="Válec440"
  Angle = 360
  AttacherType = Attacher::AttachEngine3D
  Height = 11
  Placement = pos=(0,0,-9.5) rot=(0,0,1;0rad)
  Radius = 7
FEATURE [Part::Cut] Cut018020020009027020002003004004026003005007024
  Base = -> Cylinder112024025003003006010004276107
  Tool = -> Cylinder112024025003003006010004276106
FEATURE [Part::Cut] Cut018020020009027020002003004004026003005007025  label="SK"
  Base = -> Cut018020020009027020002003004004026003005007020
  Tool = -> Cut018020020009027020002003004004026003005007024
FEATURE [Part::Feature] Cut018020020009027020002003004004026003005007025001  label="SK001"
  shape: bbox 7.8 x 7.8 x 11 mm, 8 faces (baked)
FEATURE [Part::Cylinder] Cylinder112024025003003006010004276108  label="Válec441"
  Angle = 360
  AttacherType = Attacher::AttachEngine3D
  Height = 53
  Placement = pos=(-26.5,-100.5,24.5) rot=(0,1,0;1.5708rad)
  Radius = 1.25
FEATURE [Part::Cylinder] Cylinder112024025003003006010004276109  label="cy065"
  Angle = 360
  AttacherType = Attacher::AttachEngine3D
  Height = 24
  Placement = pos=(0,-53,9) rot=(0,0,1;0rad)
  Radius = 15
FEATURE [Part::Cylinder] Cylinder112024025003003006010004276110  label="Válec442"
  Angle = 360
  AttacherType = Attacher::AttachEngine3D
  Height = 53
  Placement = pos=(-26.5,-46,11.5) rot=(0,1,0;1.5708rad)
  Radius = 5
FEATURE [Part::Cylinder] Cylinder112024025003003006010004276111  label="Válec443"
  Angle = 360
  AttacherType = Attacher::AttachEngine3D
  Height = 53
  Placement = pos=(-26.5,-46,11.5) rot=(0,1,0;1.5708rad)
  Radius = 2.3
FEATURE [Part::Box] Box021277  label="Krychle260"
  AttacherType = Attacher::AttachEngine3D
  Height = 12.5
  Length = 42
  Placement = pos=(-21,-99,5.5) rot=(0,0,1;0rad)
  Width = 80
FEATURE [Part::Box] Box021278  label="Krychle261"
  AttacherType = Attacher::AttachEngine3D
  Height = 10
  Length = 53
  Placement = pos=(-26.5,-64,6.5) rot=(0,0,1;0rad)
  Width = 18
FEATURE [Part::Box] Box021279  label="Krychle262"
  AttacherType = Attacher::AttachEngine3D
  Height = 4.6
  Length = 53
  Placement = pos=(-26.5,-64,9.2) rot=(0,0,1;0rad)
  Width = 18
FEATURE [Part::Cylinder] Cylinder112024025003003006010004276112  label="cy066"
  Angle = 360
  AttacherType = Attacher::AttachEngine3D
  Height = 24
  Placement = pos=(17.5,-53,9) rot=(0,0,1;0rad)
  Radius = 1.8
FEATURE [Part::Cylinder] Cylinder112024025003003006010004276113  label="cy067"
  Angle = 360
  AttacherType = Attacher::AttachEngine3D
  Height = 6
  Placement = pos=(17.5,-53,18) rot=(0,0,1;0rad)
  Radius = 3.8
FEATURE [Part::Box] Box021280  label="Krychle263"
  AttacherType = Attacher::AttachEngine3D
  Height = 6
  Length = 4
  Placement = pos=(-17.5,-56.8,18) rot=(0,0,1;0rad)
  Width = 7.6
FEATURE [Part::Cylinder] Cylinder112024025003003006010004276114  label="Válec444"
  Angle = 360
  AttacherType = Attacher::AttachEngine3D
  Height = 53
  Placement = pos=(-26.5,-64,11.5) rot=(0,1,0;1.5708rad)
  Radius = 2.3
FEATURE [Part::Cylinder] Cylinder112024025003003006010004276115  label="cy068"
  Angle = 360
  AttacherType = Attacher::AttachEngine3D
  Height = 6
  Placement = pos=(-17.5,-53,18) rot=(0,0,1;0rad)
  Radius = 3.8
FEATURE [Part::Box] Box021281  label="Krychle264"
  AttacherType = Attacher::AttachEngine3D
  Height = 6
  Length = 4
  Placement = pos=(13.5,-56.8,18) rot=(0,0,1;0rad)
  Width = 7.6
FEATURE [Part::Box] Box021282  label="Krychle265"
  AttacherType = Attacher::AttachEngine3D
  Height = 23.5
  Length = 50
  Placement = pos=(-25,-106,6) rot=(0,0,1;0rad)
  Width = 80
FEATURE [Part::Cylinder] Cylinder112024025003003006010004276116  label="Válec445"
  Angle = 360
  AttacherType = Attacher::AttachEngine3D
  Height = 53
  Placement = pos=(-26.5,-64,11.5) rot=(0,1,0;1.5708rad)
  Radius = 5
FEATURE [Part::Cylinder] Cylinder112024025003003006010004276117  label="cy069"
  Angle = 360
  AttacherType = Attacher::AttachEngine3D
  Height = 24
  Placement = pos=(-17.5,-53,9) rot=(0,0,1;0rad)
  Radius = 1.8
FEATURE [Part::Box] Box021283  label="Krychle266"
  AttacherType = Attacher::AttachEngine3D
  Height = 20
  Length = 19
  Placement = pos=(-9.5,-73,18) rot=(0,0,1;0rad)
  Width = 20
FEATURE [Part::Cylinder] Cylinder112024025003003006010004276118  label="Válec446"
  Angle = 360
  AttacherType = Attacher::AttachEngine3D
  Height = 53
  Placement = pos=(-26.5,-31.5,24.5) rot=(0,1,0;1.5708rad)
  Radius = 1.25
FEATURE [Part::MultiFuse] Fusion005043005007002078086001025  label="Motor M005"
  Shapes = -> [Cylinder112024025003003006010004276116,Cylinder112024025003003006010004276110,Box021278,Box021282]
FEATURE [Part::Cylinder] Cylinder112024025003003006010004276119  label="cy070"
  Angle = 360
  AttacherType = Attacher::AttachEngine3D
  Height = 6
  Placement = pos=(0,-45,17) rot=(0,0,1;0rad)
  Radius = 12
FEATURE [Part::Cylinder] Cylinder112024025003003006010004276120  label="Válec447"
  Angle = 360
  AttacherType = Attacher::AttachEngine3D
  Height = 20
  Placement = pos=(-27,-53.5,11) rot=(0,1,0;1.5708rad)
  Radius = 2.2
FEATURE [Part::Box] Box021284  label="Krychle267"
  AttacherType = Attacher::AttachEngine3D
  Height = 10
  Length = 3.5
  Placement = pos=(13.5,-57,11) rot=(0,0,1;0rad)
  Width = 7
FEATURE [Sketcher::SketchObject] Sketch024
  MapMode = 5
  Placement = pos=(13.5,-57,11) rot=(0.57735,-0.57735,-0.57735;2.0944rad)
  Support = -> [Box021284]
  sketch-geometry (7):
    g0: LineSegment StartX=-3.5 StartY=4 StartZ=0 EndX=-6.9641 EndY=2 EndZ=0
    g1: LineSegment StartX=-6.9641 StartY=2 StartZ=0 EndX=-6.9641 EndY=-2 EndZ=0
    g2: LineSegment StartX=-6.9641 StartY=-2 StartZ=0 EndX=-3.5 EndY=-4 EndZ=0
    g3: LineSegment StartX=-3.5 StartY=-4 StartZ=0 EndX=-0.0358984 EndY=-2 EndZ=0
    g4: LineSegment StartX=-0.0358984 StartY=-2 StartZ=0 EndX=-0.0358984 EndY=2 EndZ=0
    g5: LineSegment StartX=-0.0358984 StartY=2 StartZ=0 EndX=-3.5 EndY=4 EndZ=0
    g6: Circle [constr] CenterX=-3.5 CenterY=0 CenterZ=0 NormalX=0 NormalY=0 NormalZ=1 AngleXU=0 Radius=4
  constraints (14):
    c: Coincident(g0,g1)
    c: Coincident(g1,g2)
    c: Coincident(g2,g3)
    c: Coincident(g3,g4)
    c: Coincident(g4,g5)
    c: Coincident(g5,g0)
    c: Equal(g0, g1-g5) x5
    c: PointOnObject(g0,g6)
    c: PointOnObject(g1,g6)
    c: PointOnObject(g2,g6)
    c: PointOnObject(g3,g6)
    c: PointOnObject(g4,g6)
    c: PointOnObject(g5,g6)
    c: PointOnObject(g6,g-1)
FEATURE [Part::Extrusion] Extrude033
  Base = -> Sketch024
  Dir = (-1,0,0)
  DirMode = 2
  FaceMakerClass = Part::FaceMakerBullseye
  LengthFwd = -3.5
  LengthRev = 0
  Solid = true
  Symmetric = false
FEATURE [Part::MultiFuse] Fusion005043005007002078086001027  label="Matice024"
  Placement = pos=(-31,0,0) rot=(0,0,1;0rad)
  Shapes = -> [Box021284,Extrude033]
FEATURE [Part::MultiFuse] Fusion005043005007002078086001028  label="matice"
  Placement = pos=(0,0,0) rot=(0,0,1;1.5708rad)
  Shapes = -> [Fusion005043005007002078086001027,Cylinder112024025003003006010004276120]
FEATURE [Part::Feature] Fusion005043005007002078086001028001  label="matice001"
  Placement = pos=(-53.5,-118.5,24) rot=(1,0,0;3.14159rad)
  shape: bbox 7 x 20 x 14 mm, 15 faces (baked)
FEATURE [Part::MultiFuse] Fusion005043005007002078086001026  label="Motor vyrezy004"
  Shapes = -> [Box021277,Cylinder112024025003003006010004276109,Cylinder112024025003003006010004276114,Cylinder112024025003003006010004276111,Box021279,Cylinder112024025003003006010004276117,Cylinder112024025003003006010004276112,Cylinder112024025003003006010004276115,Cylinder112024025003003006010004276113,Box021280,Box021281,Box021283,Cylinder112024025003003006010004276118,+3 more]
FEATURE [Part::Cut] Cut018020020009027020002003004004026003005007025002  label="AF Motor004"
  Base = -> Fusion005043005007002078086001025
  Tool = -> Fusion005043005007002078086001026
FEATURE [Part::Fillet] Fillet028003009002002
  Base = -> Cut018020020009027020002003004004026003005007025002
  Edges = 10 edges r=1: [Edge4,Edge7,Edge17,Edge21,Edge38,Edge42,Edge156,Edge159,Edge162,Edge163]
FEATURE [Part::Feature] Fillet028003009002002001  label="Fillet028003009002003"
  shape: bbox 53 x 80 x 23.5 mm, 79 faces (baked)
FEATURE [App::Part] Part024  label="NewmyAF"
  Group = -> [Cut018020020009027020002003004004026003005007019,Cut018020020009027020002003004004026003005007018,Fusion005043005007002078086001020,Fusion005043005007002078086001021,Fusion005043005007002078086001022,Fusion005043005007002078086001019,Cylinder112024025003003006010004276090,Box021271,Box021272,Box021273,Cylinder112024025003003006010004276088,Cylinder112024025003003006010004276089,+85 more]
  Origin = -> Origin024
  Placement = pos=(0,0,-1) rot=(0,0,1;0rad)
FEATURE [Part::Feature] Fusion005043005007002078086001028002  label="matice002"
  Placement = pos=(-53.5,-118.5,24) rot=(1,0,0;3.14159rad)
  shape: bbox 7 x 20 x 14 mm, 15 faces (baked)
FEATURE [Part::Box] Box021285  label="Krychle268"
  AttacherType = Attacher::AttachEngine3D
  Height = 23.5
  Length = 54
  Placement = pos=(-27,-106,6) rot=(0,0,1;0rad)
  Width = 30
FEATURE [Part::Cylinder] Cylinder112024025003003006010004276122  label="Válec449"
  Angle = 360
  AttacherType = Attacher::AttachEngine3D
  Height = 60
  Placement = pos=(-30,-80.5,24.5) rot=(0,1,0;1.5708rad)
  Radius = 1.6
FEATURE [Part::Box] Box021287  label="Krychle270"
  AttacherType = Attacher::AttachEngine3D
  Height = 12.5
  Length = 42
  Placement = pos=(-21,-99,5.5) rot=(0,0,1;0rad)
  Width = 80
FEATURE [Part::Box] Box021291  label="Krychle274"
  AttacherType = Attacher::AttachEngine3D
  Height = 24
  Length = 50
  Placement = pos=(-25,-84,6) rot=(0,0,1;0rad)
  Width = 20
FEATURE [Part::Cylinder] Cylinder112024025003003006010004276129  label="Válec453"
  Angle = 360
  AttacherType = Attacher::AttachEngine3D
  Height = 60
  Placement = pos=(-30,-80.5,11.5) rot=(0,1,0;1.5708rad)
  Radius = 1
FEATURE [Part::MultiFuse] Fusion005043005007002078086001028004  label="Motor vyrezy005"
  Shapes = -> [Box021287,Box021291,Cylinder112024025003003006010004276129,Cylinder112024025003003006010004276122,Fusion005043005007002078086001028002]
FEATURE [Part::Cut] Cut018020020009027020002003004004026003005007025003  label="Tenzione V4"
  Base = -> Box021285
  Tool = -> Fusion005043005007002078086001028004
FEATURE [Part::Fillet] Fillet028003009002002002  label="tenzioner"
  Base = -> Cut018020020009027020002003004004026003005007025003
  Edges = 12 edges r=1: [Edge1,Edge2,Edge3,Edge7,Edge8,Edge9,Edge11,Edge15,Edge16,Edge17,Edge25,Edge26]
FEATURE [Part::Feature] Fillet028003009002002002001  label="tenzioner001"
  shape: bbox 54 x 30 x 23.5 mm, 46 faces (baked)
FEATURE [Part::FeaturePython] InvoluteGear005  # WARN: FeaturePython — macro-defined, semantics opaque (R4)
  backlash = 0
  beta = 0
  clearance = 0.25
  double_helix = false
  head = 0
  height = 5.5
  module = 1.2
  numpoints = 6
  pressure_angle = 20
  reversed_backlash = false
  shift = 0
  simple = false
  teeth = 27
  undercut = false
FEATURE [Part::Cylinder] Cylinder112024025003003006010004276130  label="Válec454"
  Angle = 360
  AttacherType = Attacher::AttachEngine3D
  Height = 5.5
  Radius = 20
FEATURE [Part::Cut] Cut002  label="ring 001"
  Base = -> Cylinder112024025003003006010004276130
  Placement = pos=(0,-47,21) rot=(0,0,1;0rad)
  Tool = -> InvoluteGear005
FEATURE [Part::Feature] Cut018020020009027020002003004004026003005007025004001  label="EAF-motor-V008"
  Placement = pos=(0,0,25.5) rot=(0,1,0;3.14159rad)
  shape: bbox 53 x 58 x 42.5 mm, 103 faces (baked)
FEATURE [Part::Cylinder] Cylinder112024025003003006010004276131  label="Válec455"
  Angle = 360
  AttacherType = Attacher::AttachEngine3D
  Height = 60
  Placement = pos=(-30,-80.5,11.5) rot=(0,1,0;1.5708rad)
  Radius = 0.6
FEATURE [Part::Cylinder] Cylinder112024025003003006010004276132  label="Válec456"
  Angle = 360
  AttacherType = Attacher::AttachEngine3D
  Height = 60
  Placement = pos=(-30,-80.5,24.5) rot=(0,1,0;1.5708rad)
  Radius = 1.2
FEATURE [Part::MultiFuse] Fusion005043005007002078086001028005
  Shapes = -> [Cylinder112024025003003006010004276131,Cylinder112024025003003006010004276132]
FEATURE [Part::Cut] Cut018020020009027020002003004004026003005007025004002  label="EAF motor"
  Base = -> Cut018020020009027020002003004004026003005007025004001
  Tool = -> Fusion005043005007002078086001028005
FEATURE [App::Part] Part017  label="Fin2"
  Group = -> [Fusion005043005007002078020,Fusion005043005007002078021,Box021185,Cylinder112024025003003006010004209,Cylinder112024025003003006010004207,Cylinder112024025003003006010004206,Cylinder112024025003003006010004205,Box021183,Box021186,Cylinder112024025003003006010004203,Box021184,Cylinder112024025003003006010004204,Box021187,Box021182,Cylinder112024025003003006010004208,Box021188,Box021189,+110 more]
  Origin = -> Origin017
FEATURE [Part::Feature] Cut018020020009027020002003004004026003005007025004002001  label="EAF motor001"
  shape: bbox 53 x 58 x 42.5 mm, 106 faces (baked)
FEATURE [App::Part] Part012  label="SCT -EAF V4"
  Group = -> [Cylinder112024025003003006010004099,Cylinder112024025003003006010004101,Cylinder112024025003003006010004100,Cylinder112024025003003006010004102,Fusion005043005007002055,Fusion005043005007002057,Fusion005043005007002056,Cylinder112024025003003006010004098,Box021116,Cylinder112024025003003006010004103,Box021117,Cut018020020009027020002003004004026003002,Cylinder112024025003003006010004112,+44 more]
  Origin = -> Origin012
FEATURE [Part::Cylinder] Cylinder112024025003003006010004276133  label="Válec457"
  Angle = 360
  AttacherType = Attacher::AttachEngine3D
  Height = 53
  Placement = pos=(-26.5,-64,11.5) rot=(0,1,0;1.5708rad)
  Radius = 5
FEATURE [Part::Cylinder] Cylinder112024025003003006010004276134  label="cy071"
  Angle = 360
  AttacherType = Attacher::AttachEngine3D
  Height = 24
  Placement = pos=(-17.5,-55,9) rot=(0,0,1;0rad)
  Radius = 1.8
FEATURE [Part::Cylinder] Cylinder112024025003003006010004276135  label="cy072"
  Angle = 360
  AttacherType = Attacher::AttachEngine3D
  Height = 6
  Placement = pos=(-17.5,-55,18) rot=(0,0,1;0rad)
  Radius = 3.8
FEATURE [Part::Box] Box021292  label="Krychle275"
  AttacherType = Attacher::AttachEngine3D
  Height = 6
  Length = 4
  Placement = pos=(-17.5,-58.8,18) rot=(0,0,1;0rad)
  Width = 7.6
FEATURE [Part::Cylinder] Cylinder112024025003003006010004276136  label="cy073"
  Angle = 360
  AttacherType = Attacher::AttachEngine3D
  Height = 20
  Placement = pos=(0,-55,18) rot=(0,0,1;0rad)
  Radius = 15
FEATURE [Part::Cylinder] Cylinder112024025003003006010004276137  label="Válec458"
  Angle = 360
  AttacherType = Attacher::AttachEngine3D
  Height = 53
  Placement = pos=(-26.5,-64,11.5) rot=(0,1,0;1.5708rad)
  Radius = 2.3
FEATURE [Part::Cylinder] Cylinder112024025003003006010004276138  label="Válec459"
  Angle = 360
  AttacherType = Attacher::AttachEngine3D
  Height = 53
  Placement = pos=(-26.5,-46,11.5) rot=(0,1,0;1.5708rad)
  Radius = 5
FEATURE [Part::Box] Box021293  label="Krychle276"
  AttacherType = Attacher::AttachEngine3D
  Height = 4.6
  Length = 53
  Placement = pos=(-26.5,-64,9.2) rot=(0,0,1;0rad)
  Width = 18
FEATURE [Part::Cylinder] Cylinder112024025003003006010004276139  label="Válec460"
  Angle = 360
  AttacherType = Attacher::AttachEngine3D
  Height = 53
  Placement = pos=(-26.5,-46,11.5) rot=(0,1,0;1.5708rad)
  Radius = 2.3
FEATURE [Part::Box] Box021294  label="Krychle277"
  AttacherType = Attacher::AttachEngine3D
  Height = 31.5
  Length = 50
  Placement = pos=(-25,-106,6) rot=(0,0,1;0rad)
  Width = 80
FEATURE [Part::Box] Box021295  label="Krychle278"
  AttacherType = Attacher::AttachEngine3D
  Height = 12.5
  Length = 42
  Placement = pos=(-21,-99.5,5.5) rot=(0,0,1;0rad)
  Width = 80
FEATURE [Part::Box] Box021296  label="Krychle279"
  AttacherType = Attacher::AttachEngine3D
  Height = 10
  Length = 53
  Placement = pos=(-26.5,-64,6.5) rot=(0,0,1;0rad)
  Width = 18
FEATURE [Part::Cylinder] Cylinder112024025003003006010004276140  label="cy074"
  Angle = 360
  AttacherType = Attacher::AttachEngine3D
  Height = 24
  Placement = pos=(17.5,-55,9) rot=(0,0,1;0rad)
  Radius = 1.8
FEATURE [Part::Cylinder] Cylinder112024025003003006010004276141  label="cy075"
  Angle = 360
  AttacherType = Attacher::AttachEngine3D
  Height = 6
  Placement = pos=(17.5,-55,18) rot=(0,0,1;0rad)
  Radius = 3.8
FEATURE [Part::Cylinder] Cylinder112024025003003006010004276142  label="Válec461"
  Angle = 360
  AttacherType = Attacher::AttachEngine3D
  Height = 5
  Placement = pos=(-25.5,-31.5,32.5) rot=(0,1,0;1.5708rad)
  Radius = 1.25
FEATURE [Part::Box] Box021297  label="Krychle280"
  AttacherType = Attacher::AttachEngine3D
  Height = 6
  Length = 4
  Placement = pos=(13.5,-58.8,18) rot=(0,0,1;0rad)
  Width = 7.6
FEATURE [Part::Box] Box021298  label="Krychle281"
  AttacherType = Attacher::AttachEngine3D
  Height = 20
  Length = 19
  Placement = pos=(-9.5,-73.5,19) rot=(0,0,1;0rad)
  Width = 20
FEATURE [Part::Cylinder] Cylinder112024025003003006010004276143  label="Válec462"
  Angle = 360
  AttacherType = Attacher::AttachEngine3D
  Height = 53
  Placement = pos=(-26.5,-100.5,32.5) rot=(0,1,0;1.5708rad)
  Radius = 1.25
FEATURE [Part::MultiFuse] Fusion005043005007002078086001028006  label="Motor M006"
  Shapes = -> [Cylinder112024025003003006010004276133,Cylinder112024025003003006010004276138,Box021296,Box021294]
FEATURE [Part::Cylinder] Cylinder112024025003003006010004276144  label="cy076"
  Angle = 360
  AttacherType = Attacher::AttachEngine3D
  Height = 20
  Placement = pos=(0,-47,18) rot=(0,0,1;0rad)
  Radius = 20
FEATURE [Part::Box] Box021299  label="Krychle282"
  AttacherType = Attacher::AttachEngine3D
  Height = 3.5
  Length = 42
  Placement = pos=(-21,-76,34) rot=(0,0,1;0rad)
  Width = 50
FEATURE [Part::Cylinder] Cylinder112024025003003006010004276146  label="cy078"
  Angle = 360
  AttacherType = Attacher::AttachEngine3D
  Height = 4.5
  Placement = pos=(17.5,-55,29.5) rot=(0,0,1;0rad)
  Radius = 3.8
FEATURE [Part::Cylinder] Cylinder112024025003003006010004276147  label="cy079"
  Angle = 360
  AttacherType = Attacher::AttachEngine3D
  Height = 4.5
  Placement = pos=(-17.5,-55,29.5) rot=(0,0,1;0rad)
  Radius = 3.8
FEATURE [Part::Box] Box021300  label="Krychle283"
  AttacherType = Attacher::AttachEngine3D
  Height = 5
  Length = 42
  Placement = pos=(-21,-76,34) rot=(0,0,1;0rad)
  Width = 49
FEATURE [Part::Cylinder] Cylinder112024025003003006010004276148  label="Válec463"
  Angle = 360
  AttacherType = Attacher::AttachEngine3D
  Height = 3.5
  Placement = pos=(-17,-29.5,18) rot=(0,0,1;0rad)
  Radius = 3
FEATURE [Part::Cylinder] Cylinder112024025003003006010004276149  label="Válec464"
  Angle = 360
  AttacherType = Attacher::AttachEngine3D
  Height = 3.5
  Placement = pos=(17,-29.5,18) rot=(0,0,1;0rad)
  Radius = 3
FEATURE [Part::Cylinder] Cylinder112024025003003006010004276150  label="Válec465"
  Angle = 360
  AttacherType = Attacher::AttachEngine3D
  Height = 3.5
  Placement = pos=(-17,-69.5,18) rot=(0,0,1;0rad)
  Radius = 3
FEATURE [Part::Cylinder] Cylinder112024025003003006010004276151  label="Válec466"
  Angle = 360
  AttacherType = Attacher::AttachEngine3D
  Height = 3.5
  Placement = pos=(17,-69.5,18) rot=(0,0,1;0rad)
  Radius = 3
FEATURE [Part::Cylinder] Cylinder112024025003003006010004276152  label="Válec467"
  Angle = 360
  AttacherType = Attacher::AttachEngine3D
  Height = 25
  Placement = pos=(-17,-29.5,18) rot=(0,0,1;0rad)
  Radius = 1.7
FEATURE [Part::Cylinder] Cylinder112024025003003006010004276153  label="Válec468"
  Angle = 360
  AttacherType = Attacher::AttachEngine3D
  Height = 25
  Placement = pos=(-17,-69.5,18) rot=(0,0,1;0rad)
  Radius = 1.7
FEATURE [Part::Cylinder] Cylinder112024025003003006010004276154  label="Válec469"
  Angle = 360
  AttacherType = Attacher::AttachEngine3D
  Height = 25
  Placement = pos=(17,-69.5,18) rot=(0,0,1;0rad)
  Radius = 1.7
FEATURE [Part::Cylinder] Cylinder112024025003003006010004276155  label="Válec470"
  Angle = 360
  AttacherType = Attacher::AttachEngine3D
  Height = 25
  Placement = pos=(17,-29.5,18) rot=(0,0,1;0rad)
  Radius = 1.7
FEATURE [Part::MultiFuse] Fusion005043005007002078086001028011
  Shapes = -> [Cylinder112024025003003006010004276152,Cylinder112024025003003006010004276153,Cylinder112024025003003006010004276154,Cylinder112024025003003006010004276155]
FEATURE [Part::MultiFuse] Fusion005043005007002078086001028008  label="Motor-dira"
  Placement = pos=(0,0,11) rot=(0,0,1;0rad)
  Shapes = -> [Cylinder112024025003003006010004276136,Box021298,Box021297,Box021292,Cylinder112024025003003006010004276141,Cylinder112024025003003006010004276135,Cylinder112024025003003006010004276140,Cylinder112024025003003006010004276134,Fusion005043005007002078086001028011]
FEATURE [Part::Cut] Cut018020020009027020002003004004026003005007025004002003  label="Motor plate002"
  Base = -> Box021300
  Tool = -> Fusion005043005007002078086001028008
FEATURE [Part::Cylinder] Cylinder112024025003003006010004276156  label="Válec471"
  Angle = 360
  AttacherType = Attacher::AttachEngine3D
  Height = 25
  Placement = pos=(-17,-29.5,18) rot=(0,0,1;0rad)
  Radius = 1.7
FEATURE [Part::Cylinder] Cylinder112024025003003006010004276157  label="Válec472"
  Angle = 360
  AttacherType = Attacher::AttachEngine3D
  Height = 25
  Placement = pos=(-17,-69.5,18) rot=(0,0,1;0rad)
  Radius = 1.7
FEATURE [Part::Cylinder] Cylinder112024025003003006010004276158  label="Válec473"
  Angle = 360
  AttacherType = Attacher::AttachEngine3D
  Height = 25
  Placement = pos=(17,-29.5,18) rot=(0,0,1;0rad)
  Radius = 1.7
FEATURE [Part::Cylinder] Cylinder112024025003003006010004276159  label="Válec474"
  Angle = 360
  AttacherType = Attacher::AttachEngine3D
  Height = 25
  Placement = pos=(17,-69.5,18) rot=(0,0,1;0rad)
  Radius = 1.7
FEATURE [Part::MultiFuse] Fusion005043005007002078086001028010
  Shapes = -> [Cylinder112024025003003006010004276148,Cylinder112024025003003006010004276150,Cylinder112024025003003006010004276151,Cylinder112024025003003006010004276149,Cylinder112024025003003006010004276156,Cylinder112024025003003006010004276157,Cylinder112024025003003006010004276158,Cylinder112024025003003006010004276159]
FEATURE [Part::Cylinder] Cylinder112024025003003006010004276160  label="Válec475"
  Angle = 360
  AttacherType = Attacher::AttachEngine3D
  Height = 5
  Placement = pos=(20.5,-31.5,32.5) rot=(0,1,0;1.5708rad)
  Radius = 1.25
FEATURE [Part::Feature] Fusion005043005007002078086001028012  label="matice003"
  Placement = pos=(-53.5,-118.5,24) rot=(1,0,0;3.14159rad)
  shape: bbox 7 x 20 x 14 mm, 15 faces (baked)
FEATURE [Part::MultiFuse] Fusion005043005007002078086001028007  label="Motor vyrezy006"
  Shapes = -> [Box021295,Cylinder112024025003003006010004276137,Cylinder112024025003003006010004276139,Box021293,Cylinder112024025003003006010004276142,Cylinder112024025003003006010004276143,Cylinder112024025003003006010004276144,Box021299,Cylinder112024025003003006010004276147,Cylinder112024025003003006010004276146,Fusion005043005007002078086001028010,Cylinder112024025003003006010004276160,+1 more]
FEATURE [Part::Cut] Cut018020020009027020002003004004026003005007025004002002  label="AF Motor005"
  Base = -> Fusion005043005007002078086001028006
  Tool = -> Fusion005043005007002078086001028007
FEATURE [Part::MultiFuse] Fusion005043005007002078086001028009  label="Motor AF"
  Shapes = -> [Cut018020020009027020002003004004026003005007025004002002,Cut002]
FEATURE [Part::Cylinder] Cylinder112024025003003006010004276161  label="cy080"
  Angle = 360
  AttacherType = Attacher::AttachEngine3D
  Height = 20
  Placement = pos=(0,-47,18) rot=(0,0,1;0rad)
  Radius = 15.3
FEATURE [Part::Cut] Cut018020020009027020002003004004026003005007025004002004
  Base = -> Fusion005043005007002078086001028009
  Tool = -> Cylinder112024025003003006010004276161
FEATURE [Part::Fillet] Fillet028003009002002002002  label="AF gear"
  Base = -> Cut018020020009027020002003004004026003005007025004002004
  Edges = 11 edges r=1: [Edge4,Edge7,Edge17,Edge21,Edge25,Edge35,Edge39,Edge134,Edge137,Edge140,Edge141]
FEATURE [Part::Feature] Fillet028003009002002002002001  label="AF gear001"
  shape: bbox 53 x 80 x 31.5 mm, 199 faces (baked)
FEATURE [Part::Cylinder] Cylinder014004  label="Válec016"
  Angle = 360
  AttacherType = Attacher::AttachEngine3D
  Height = 10
  Placement = pos=(10.5,0,0) rot=(0,0,1;0rad)
  Radius = 2.8
FEATURE [Part::FeaturePython] InvoluteGear002  label="planet"  # WARN: FeaturePython — macro-defined, semantics opaque (R4)
  Placement = pos=(10.5,0,0.25) rot=(0,0,1;0rad)
  backlash = 0
  beta = 0
  clearance = 0.25
  double_helix = false
  head = 0
  height = 5
  module = 1.2
  numpoints = 6
  pressure_angle = 20
  reversed_backlash = false
  shift = 0
  simple = false
  teeth = 9
  undercut = false
FEATURE [Part::Cut] Cut008  label="Planet0 zaklad final"
  Base = -> InvoluteGear002
  Tool = -> Cylinder014004
FEATURE [Part::Cylinder] Cylinder014003  label="Válec015"
  Angle = 360
  AttacherType = Attacher::AttachEngine3D
  Height = 10
  Radius = 2.7
FEATURE [Part::FeaturePython] InvoluteGear  label="Sun"  # WARN: FeaturePython — macro-defined, semantics opaque (R4)
  Placement = pos=(0,0,0.25) rot=(0,0,1;0rad)
  backlash = 0
  beta = 0
  clearance = 0.25
  double_helix = false
  head = 0
  height = 5
  module = 1.2
  numpoints = 6
  pressure_angle = 20
  reversed_backlash = false
  shift = 0
  simple = false
  teeth = 9
  undercut = false
FEATURE [Part::Cut] Cut007  label="Sun0 zaklad"
  Base = -> InvoluteGear
  Tool = -> Cylinder014003
FEATURE [Part::Cylinder] Cylinder010  label="unasec spodek"
  Angle = 360
  AttacherType = Attacher::AttachEngine3D
  Height = 1.5
  Placement = pos=(0,0,-1.5) rot=(0,0,1;0rad)
  Radius = 19.5
FEATURE [Part::Cylinder] Cylinder011  label="unasec stred"
  Angle = 360
  AttacherType = Attacher::AttachEngine3D
  Height = 7
  Placement = pos=(0,0,-1.5) rot=(0,0,1;0rad)
  Radius = 13.5
FEATURE [Part::MultiFuse] Fusion002
  Shapes = -> [Cylinder011,Cylinder010]
FEATURE [Part::Cylinder] Cylinder112024025003003006010004276162  label="Válec476"
  Angle = 360
  AttacherType = Attacher::AttachEngine3D
  Height = 10
  Placement = pos=(0,0,-3) rot=(0,0,1;0rad)
  Radius = 7
FEATURE [Part::Cylinder] Cylinder013  label="Válec011"
  Angle = 360
  AttacherType = Attacher::AttachEngine3D
  Height = 10
  Placement = pos=(10.5,0,0) rot=(0,0,1;0rad)
  Radius = 8
FEATURE [Part::Feature] Cylinder014005005  label="Válec022"
  Placement = pos=(0,0,0) rot=(0,0,1;2.0944rad)
  shape: bbox 5 x 5 x 7 mm, 3 faces (baked)
FEATURE [Part::Feature] Cylinder014005004  label="Válec021"
  shape: bbox 5 x 5 x 7 mm, 3 faces (baked)
FEATURE [Part::Feature] Cylinder014005006  label="Válec023"
  Placement = pos=(0,0,0) rot=(0,0,1;4.18879rad)
  shape: bbox 5 x 5 x 7 mm, 3 faces (baked)
FEATURE [Part::MultiFuse] Fusion006
  Shapes = -> [Cylinder014005006,Cylinder014005004,Cylinder014005005]
FEATURE [Part::Feature] Cylinder014001  label="Válec013"
  Placement = pos=(0,0,0) rot=(0,0,1;2.0944rad)
  shape: bbox 16 x 16 x 10 mm, 3 faces (baked)
FEATURE [Part::Feature] Cylinder014002  label="Válec014"
  Placement = pos=(0,0,0) rot=(0,0,1;4.18879rad)
  shape: bbox 16 x 16 x 10 mm, 3 faces (baked)
FEATURE [Part::MultiFuse] Fusion005043005007002078086001028013
  Shapes = -> [Cylinder112024025003003006010004276162,Cylinder013,Cylinder014002,Cylinder014001]
FEATURE [Part::Cut] Cut004  label="unasec spodek001"
  Base = -> Fusion002
  Tool = -> Fusion005043005007002078086001028013
FEATURE [Part::Feature] Screw_solid003  label="M2x4-Screw (Solid)003"
  Placement = pos=(0,0,0) rot=(0,0,1;1.0472rad)
  shape: bbox 3.6 x 3.6 x 4 mm, 12 faces (baked)
FEATURE [Part::Feature] Screw_solid004  label="M2x4-Screw (Solid)004"
  Placement = pos=(0,0,0) rot=(0,0,-1;1.0472rad)
  shape: bbox 3.6 x 3.6 x 4 mm, 12 faces (baked)
FEATURE [Part::Feature] Screw_solid005  label="M2x4-Screw (Solid)005"
  Placement = pos=(0,0,0) rot=(0,0,1;3.14159rad)
  shape: bbox 3.6 x 3.6 x 4 mm, 12 faces (baked)
FEATURE [Part::MultiFuse] Fusion004  label="srouby002"
  Shapes = -> [Screw_solid003,Screw_solid004,Screw_solid005]
FEATURE [Part::Cut] Cut006  label="Uasec spodek"
  Base = -> Cut004
  Tool = -> Fusion004
FEATURE [Part::MultiFuse] Fusion008  label="Unasec spdek final"
  Shapes = -> [Cut006,Fusion006]
FEATURE [App::Part] Part025  label="S Planetoou"
  Group = -> [Cylinder112024025003003006010004276141,Fusion005043005007002078086001028008,Fusion005043005007002078086001028011,Cylinder112024025003003006010004276136,Cylinder112024025003003006010004276134,Cylinder112024025003003006010004276135,Box021292,Cylinder112024025003003006010004276140,Cylinder112024025003003006010004276152,Box021298,Cylinder112024025003003006010004276155,Box021297,+42 more]
  Origin = -> Origin025
  Placement = pos=(0,-47,26.5) rot=(1,0,0;3.14159rad)
FEATURE [Part::Feature] Fusion008001  label="Unasec spdek final001"
  shape: bbox 39 x 39 x 8.5 mm, 28 faces (baked)
FEATURE [Part::Feature] difference001009  label="GT2-40"
  Placement = pos=(0,0,11) rot=(0,0,1;0rad)
  shape: bbox 15.22 x 15.22 x 11 mm, 484 faces (baked)
FEATURE [Part::Feature] Screw_solid009  label="M2x4-Screw (Solid)009"
  Placement = pos=(0,0,0) rot=(0,0,-1;1.0472rad)
  shape: bbox 3.6 x 3.6 x 4 mm, 12 faces (baked)
FEATURE [Part::Feature] Screw_solid010  label="M2x4-Screw (Solid)010"
  Placement = pos=(0,0,0) rot=(0,0,1;1.0472rad)
  shape: bbox 3.6 x 3.6 x 4 mm, 12 faces (baked)
FEATURE [Part::Feature] Screw_solid011  label="M2x4-Screw (Solid)011"
  Placement = pos=(0,0,0) rot=(0,0,1;3.14159rad)
  shape: bbox 3.6 x 3.6 x 4 mm, 12 faces (baked)
FEATURE [Part::Feature] Cylinder112024025003003006010004276163  label="Válec477"
  Placement = pos=(0,0,0) rot=(0,0,1;4.18879rad)
  shape: bbox 5 x 5 x 7 mm, 3 faces (baked)
FEATURE [Part::Feature] Cylinder112024025003003006010004276164  label="Válec478"
  shape: bbox 5 x 5 x 7 mm, 3 faces (baked)
FEATURE [Part::Feature] Cylinder112024025003003006010004276165  label="Válec479"
  Placement = pos=(0,0,0) rot=(0,0,1;2.0944rad)
  shape: bbox 5 x 5 x 7 mm, 3 faces (baked)
FEATURE [Part::MultiFuse] Fusion005043005007002078086001028015
  Shapes = -> [Cylinder112024025003003006010004276163,Cylinder112024025003003006010004276164,Cylinder112024025003003006010004276165]
FEATURE [Part::MultiFuse] Fusion005043005007002078086001028016  label="srouby004"
  Placement = pos=(0,0,0.5) rot=(0,0,1;0rad)
  Shapes = -> [Screw_solid010,Screw_solid009,Screw_solid011]
FEATURE [Part::Cylinder] Cylinder112024025003003006010004276166  label="Unasec vrch002"
  Angle = 360
  AttacherType = Attacher::AttachEngine3D
  Height = 1.5
  Placement = pos=(0,0,5.5) rot=(0,0,1;0rad)
  Radius = 19.5
FEATURE [Part::Cut] Cut018020020009027020002003004004026003005007025004002005  label="unasec vrch002"
  Base = -> Cylinder112024025003003006010004276166
  Tool = -> Fusion005043005007002078086001028016
FEATURE [Part::Cylinder] Cylinder112024025003003006010004276167  label="Válec480"
  Angle = 360
  AttacherType = Attacher::AttachEngine3D
  Height = 7
  Radius = 2.6
FEATURE [Part::MultiFuse] Fusion005043005007002078086001028014
  Placement = pos=(0,0,1) rot=(0,0,1;0rad)
  Shapes = -> [Fusion005043005007002078086001028015,Cylinder112024025003003006010004276167]
FEATURE [Part::Cut] Cut018020020009027020002003004004026003005007025004002006  label="Unasec Vrch zaklad002"
  Base = -> Cut018020020009027020002003004004026003005007025004002005
  Tool = -> Fusion005043005007002078086001028014
FEATURE [Part::Cylinder] Cylinder112024025003003006010004276168  label="Válec481"
  Angle = 360
  AttacherType = Attacher::AttachEngine3D
  Height = 4
  Placement = pos=(0,0,5.5) rot=(0,0,1;0rad)
  Radius = 7.9
FEATURE [Part::MultiFuse] Fusion005043005007002078086001028017  label="Unasec vrch "
  Shapes = -> [difference001009,Cut018020020009027020002003004004026003005007025004002006,Cylinder112024025003003006010004276168]
FEATURE [Part::Feature] Cut018020020009027020002003004004026003005007025004002009  label="Pulley-GT2-16_28BYJ--051"
  Placement = pos=(0,0,0) rot=(1,0,0;3.14159rad)
  shape: bbox 12.68 x 12.68 x 11 mm, 393 faces (baked)
FEATURE [Part::Cylinder] Cylinder112024025003003006010004276169  label="Válec482"
  Angle = 360
  AttacherType = Attacher::AttachEngine3D
  Height = 11
  Placement = pos=(0,0,-9.5) rot=(0,0,1;0rad)
  Radius = 3.85
FEATURE [Part::Cylinder] Cylinder112024025003003006010004276170  label="Válec483"
  Angle = 360
  AttacherType = Attacher::AttachEngine3D
  Height = 11
  Placement = pos=(0,0,-9.5) rot=(0,0,1;0rad)
  Radius = 7
FEATURE [Part::Cut] Cut018020020009027020002003004004026003005007025004002007
  Base = -> Cylinder112024025003003006010004276170
  Tool = -> Cylinder112024025003003006010004276169
FEATURE [Part::Cut] Cut018020020009027020002003004004026003005007025004002008  label="SK002"
  Base = -> Cut018020020009027020002003004004026003005007025004002009
  Placement = pos=(0,0,3.75) rot=(0,0,1;0rad)
  Tool = -> Cut018020020009027020002003004004026003005007025004002007
FEATURE [Part::MultiFuse] Fusion005043005007002078086001028018  label="Sun pastorek"
  Shapes = -> [Cut007,Cut018020020009027020002003004004026003005007025004002008]
note: 10 file-system paths scrubbed to <path> (originals preserved in the JSON sidecar)
